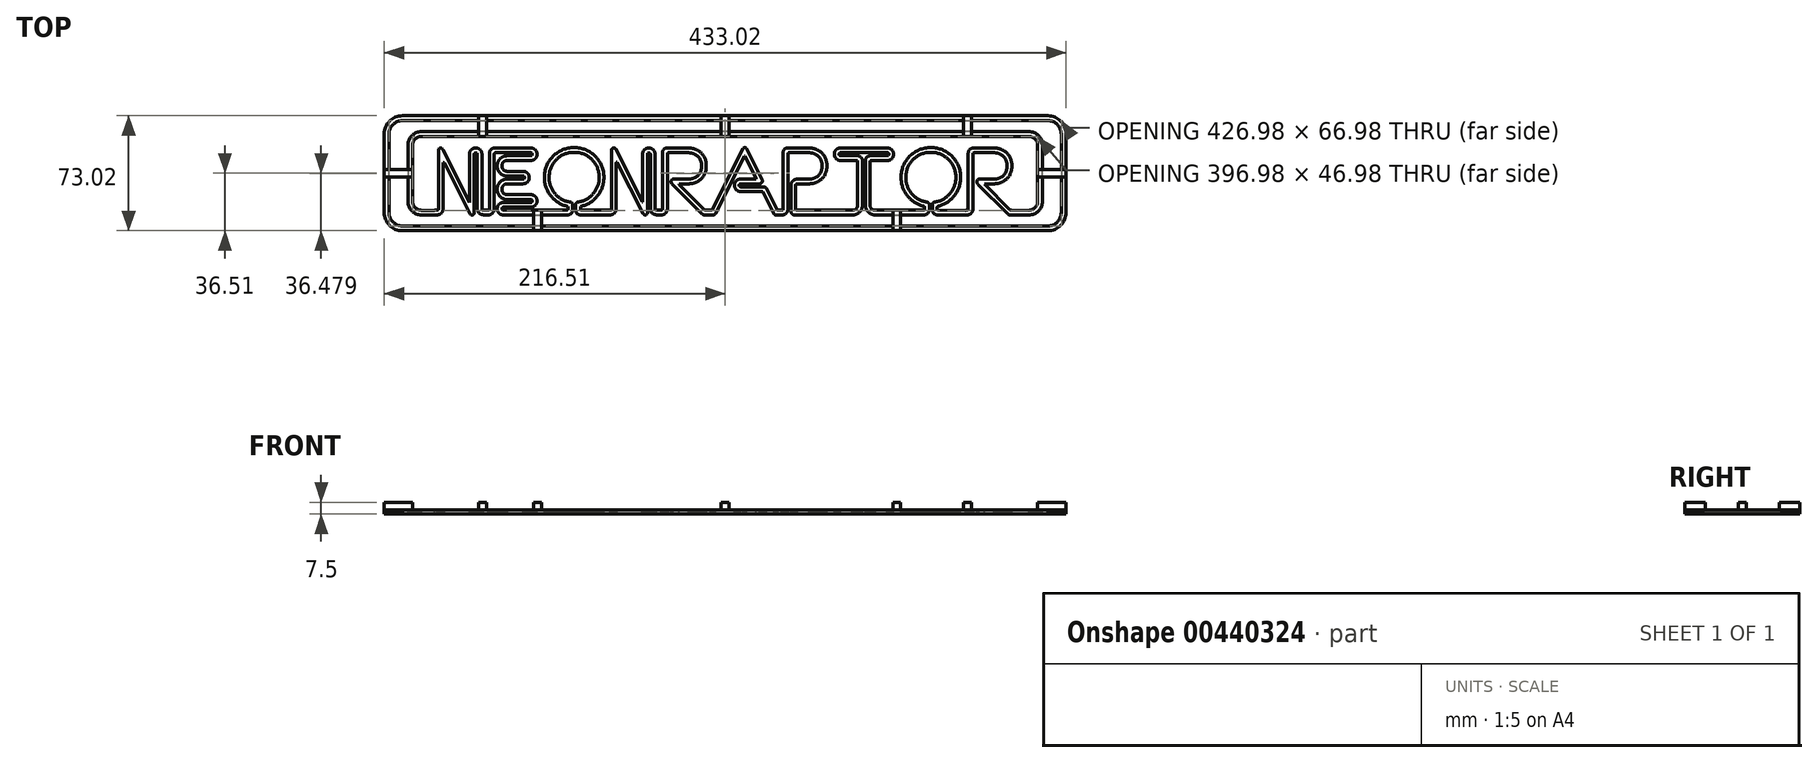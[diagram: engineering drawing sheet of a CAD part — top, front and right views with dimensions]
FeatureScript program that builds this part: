
annotation { "Feature Type Name" : "Feature", "Feature Type Description" : "" }
export const myFeature = defineFeature(function(context is Context, id is Id, definition is map)
    precondition{}
    {
        {
            var Q0;
            Q0=qCreatedBy(makeId("Top.planeOp"),FACE);
            var Q1;
            Q1=qCreatedBy(makeId("Top.planeOp"),FACE);
            var sketch = newSketch(context, id + "F0", { "sketchPlane" : qUnion([Q0, Q1])});
            skLineSegment(sketch, "E0", {"start": v(205, 36.51) * mm, "end": v(-205, 36.51) * mm});
            skLineSegment(sketch, "E1", {"start": v(-205, 36.51) * mm, "end": v(-206.18, 36.45) * mm});
            skLineSegment(sketch, "E2", {"start": v(-206.18, 36.45) * mm, "end": v(-207.32, 36.28) * mm});
            skLineSegment(sketch, "E3", {"start": v(-207.32, 36.28) * mm, "end": v(-208.42, 36) * mm});
            skLineSegment(sketch, "E4", {"start": v(-208.42, 36) * mm, "end": v(-209.48, 35.6) * mm});
            skLineSegment(sketch, "E5", {"start": v(-209.48, 35.6) * mm, "end": v(-210.48, 35.12) * mm});
            skLineSegment(sketch, "E6", {"start": v(-210.48, 35.12) * mm, "end": v(-211.43, 34.54) * mm});
            skLineSegment(sketch, "E7", {"start": v(-211.43, 34.54) * mm, "end": v(-212.32, 33.88) * mm});
            skLineSegment(sketch, "E8", {"start": v(-212.32, 33.88) * mm, "end": v(-213.14, 33.14) * mm});
            skLineSegment(sketch, "E9", {"start": v(-213.14, 33.14) * mm, "end": v(-213.88, 32.32) * mm});
            skLineSegment(sketch, "E10", {"start": v(-213.88, 32.32) * mm, "end": v(-214.54, 31.43) * mm});
            skLineSegment(sketch, "E11", {"start": v(-214.54, 31.43) * mm, "end": v(-215.12, 30.48) * mm});
            skLineSegment(sketch, "E12", {"start": v(-215.12, 30.48) * mm, "end": v(-215.6, 29.48) * mm});
            skLineSegment(sketch, "E13", {"start": v(-215.6, 29.48) * mm, "end": v(-216, 28.42) * mm});
            skLineSegment(sketch, "E14", {"start": v(-216, 28.42) * mm, "end": v(-216.28, 27.32) * mm});
            skLineSegment(sketch, "E15", {"start": v(-216.28, 27.32) * mm, "end": v(-216.45, 26.18) * mm});
            skLineSegment(sketch, "E16", {"start": v(-216.45, 26.18) * mm, "end": v(-216.51, 25) * mm});
            skLineSegment(sketch, "E17", {"start": v(-216.51, 25) * mm, "end": v(-216.51, -25) * mm});
            skLineSegment(sketch, "E18", {"start": v(-216.51, -25) * mm, "end": v(-216.45, -26.18) * mm});
            skLineSegment(sketch, "E19", {"start": v(-216.45, -26.18) * mm, "end": v(-216.28, -27.32) * mm});
            skLineSegment(sketch, "E20", {"start": v(-216.28, -27.32) * mm, "end": v(-216, -28.42) * mm});
            skLineSegment(sketch, "E21", {"start": v(-216, -28.42) * mm, "end": v(-215.6, -29.48) * mm});
            skLineSegment(sketch, "E22", {"start": v(-215.6, -29.48) * mm, "end": v(-215.12, -30.48) * mm});
            skLineSegment(sketch, "E23", {"start": v(-215.12, -30.48) * mm, "end": v(-214.54, -31.43) * mm});
            skLineSegment(sketch, "E24", {"start": v(-214.54, -31.43) * mm, "end": v(-213.88, -32.32) * mm});
            skLineSegment(sketch, "E25", {"start": v(-213.88, -32.32) * mm, "end": v(-213.14, -33.14) * mm});
            skLineSegment(sketch, "E26", {"start": v(-213.14, -33.14) * mm, "end": v(-212.32, -33.88) * mm});
            skLineSegment(sketch, "E27", {"start": v(-212.32, -33.88) * mm, "end": v(-211.43, -34.54) * mm});
            skLineSegment(sketch, "E28", {"start": v(-211.43, -34.54) * mm, "end": v(-210.48, -35.12) * mm});
            skLineSegment(sketch, "E29", {"start": v(-210.48, -35.12) * mm, "end": v(-209.48, -35.6) * mm});
            skLineSegment(sketch, "E30", {"start": v(-209.48, -35.6) * mm, "end": v(-208.42, -36) * mm});
            skLineSegment(sketch, "E31", {"start": v(-208.42, -36) * mm, "end": v(-207.32, -36.28) * mm});
            skLineSegment(sketch, "E32", {"start": v(-207.32, -36.28) * mm, "end": v(-206.18, -36.45) * mm});
            skLineSegment(sketch, "E33", {"start": v(-206.18, -36.45) * mm, "end": v(-205, -36.51) * mm});
            skLineSegment(sketch, "E34", {"start": v(-205, -36.51) * mm, "end": v(205, -36.51) * mm});
            skLineSegment(sketch, "E35", {"start": v(205, -36.51) * mm, "end": v(206.18, -36.45) * mm});
            skLineSegment(sketch, "E36", {"start": v(206.18, -36.45) * mm, "end": v(207.32, -36.28) * mm});
            skLineSegment(sketch, "E37", {"start": v(207.32, -36.28) * mm, "end": v(208.42, -36) * mm});
            skLineSegment(sketch, "E38", {"start": v(208.42, -36) * mm, "end": v(209.48, -35.6) * mm});
            skLineSegment(sketch, "E39", {"start": v(209.48, -35.6) * mm, "end": v(210.48, -35.12) * mm});
            skLineSegment(sketch, "E40", {"start": v(210.48, -35.12) * mm, "end": v(211.43, -34.54) * mm});
            skLineSegment(sketch, "E41", {"start": v(211.43, -34.54) * mm, "end": v(212.32, -33.88) * mm});
            skLineSegment(sketch, "E42", {"start": v(212.32, -33.88) * mm, "end": v(213.14, -33.14) * mm});
            skLineSegment(sketch, "E43", {"start": v(213.14, -33.14) * mm, "end": v(213.88, -32.32) * mm});
            skLineSegment(sketch, "E44", {"start": v(213.88, -32.32) * mm, "end": v(214.54, -31.43) * mm});
            skLineSegment(sketch, "E45", {"start": v(214.54, -31.43) * mm, "end": v(215.12, -30.48) * mm});
            skLineSegment(sketch, "E46", {"start": v(215.12, -30.48) * mm, "end": v(215.6, -29.48) * mm});
            skLineSegment(sketch, "E47", {"start": v(215.6, -29.48) * mm, "end": v(216, -28.42) * mm});
            skLineSegment(sketch, "E48", {"start": v(216, -28.42) * mm, "end": v(216.28, -27.32) * mm});
            skLineSegment(sketch, "E49", {"start": v(216.28, -27.32) * mm, "end": v(216.45, -26.18) * mm});
            skLineSegment(sketch, "E50", {"start": v(216.45, -26.18) * mm, "end": v(216.51, -25) * mm});
            skLineSegment(sketch, "E51", {"start": v(216.51, -25) * mm, "end": v(216.51, 25) * mm});
            skLineSegment(sketch, "E52", {"start": v(216.51, 25) * mm, "end": v(216.45, 26.18) * mm});
            skLineSegment(sketch, "E53", {"start": v(216.45, 26.18) * mm, "end": v(216.28, 27.32) * mm});
            skLineSegment(sketch, "E54", {"start": v(216.28, 27.32) * mm, "end": v(216, 28.42) * mm});
            skLineSegment(sketch, "E55", {"start": v(216, 28.42) * mm, "end": v(215.6, 29.48) * mm});
            skLineSegment(sketch, "E56", {"start": v(215.6, 29.48) * mm, "end": v(215.12, 30.48) * mm});
            skLineSegment(sketch, "E57", {"start": v(215.12, 30.48) * mm, "end": v(214.54, 31.43) * mm});
            skLineSegment(sketch, "E58", {"start": v(214.54, 31.43) * mm, "end": v(213.88, 32.32) * mm});
            skLineSegment(sketch, "E59", {"start": v(213.88, 32.32) * mm, "end": v(213.14, 33.14) * mm});
            skLineSegment(sketch, "E60", {"start": v(213.14, 33.14) * mm, "end": v(212.32, 33.88) * mm});
            skLineSegment(sketch, "E61", {"start": v(212.32, 33.88) * mm, "end": v(211.43, 34.54) * mm});
            skLineSegment(sketch, "E62", {"start": v(211.43, 34.54) * mm, "end": v(210.48, 35.12) * mm});
            skLineSegment(sketch, "E63", {"start": v(210.48, 35.12) * mm, "end": v(209.48, 35.6) * mm});
            skLineSegment(sketch, "E64", {"start": v(209.48, 35.6) * mm, "end": v(208.42, 36) * mm});
            skLineSegment(sketch, "E65", {"start": v(208.42, 36) * mm, "end": v(207.32, 36.28) * mm});
            skLineSegment(sketch, "E66", {"start": v(207.32, 36.28) * mm, "end": v(206.18, 36.45) * mm});
            skLineSegment(sketch, "E67", {"start": v(206.18, 36.45) * mm, "end": v(205, 36.51) * mm});
            skLineSegment(sketch, "E68", {"start": v(213.49, -25) * mm, "end": v(213.45, -25.87) * mm});
            skLineSegment(sketch, "E69", {"start": v(213.45, -25.87) * mm, "end": v(213.32, -26.7) * mm});
            skLineSegment(sketch, "E70", {"start": v(213.32, -26.7) * mm, "end": v(213.1, -27.52) * mm});
            skLineSegment(sketch, "E71", {"start": v(213.1, -27.52) * mm, "end": v(212.82, -28.3) * mm});
            skLineSegment(sketch, "E72", {"start": v(212.82, -28.3) * mm, "end": v(212.46, -29.04) * mm});
            skLineSegment(sketch, "E73", {"start": v(212.46, -29.04) * mm, "end": v(212.04, -29.74) * mm});
            skLineSegment(sketch, "E74", {"start": v(212.04, -29.74) * mm, "end": v(211.55, -30.4) * mm});
            skLineSegment(sketch, "E75", {"start": v(211.55, -30.4) * mm, "end": v(211, -31) * mm});
            skLineSegment(sketch, "E76", {"start": v(211, -31) * mm, "end": v(210.4, -31.55) * mm});
            skLineSegment(sketch, "E77", {"start": v(210.4, -31.55) * mm, "end": v(209.74, -32.04) * mm});
            skLineSegment(sketch, "E78", {"start": v(209.74, -32.04) * mm, "end": v(209.04, -32.46) * mm});
            skLineSegment(sketch, "E79", {"start": v(209.04, -32.46) * mm, "end": v(208.3, -32.82) * mm});
            skLineSegment(sketch, "E80", {"start": v(208.3, -32.82) * mm, "end": v(207.52, -33.1) * mm});
            skLineSegment(sketch, "E81", {"start": v(207.52, -33.1) * mm, "end": v(206.7, -33.32) * mm});
            skLineSegment(sketch, "E82", {"start": v(206.7, -33.32) * mm, "end": v(205.87, -33.45) * mm});
            skLineSegment(sketch, "E83", {"start": v(205.87, -33.45) * mm, "end": v(205, -33.49) * mm});
            skLineSegment(sketch, "E84", {"start": v(205, -33.49) * mm, "end": v(-205, -33.49) * mm});
            skLineSegment(sketch, "E85", {"start": v(-205, -33.49) * mm, "end": v(-205.87, -33.45) * mm});
            skLineSegment(sketch, "E86", {"start": v(-205.87, -33.45) * mm, "end": v(-206.7, -33.32) * mm});
            skLineSegment(sketch, "E87", {"start": v(-206.7, -33.32) * mm, "end": v(-207.52, -33.1) * mm});
            skLineSegment(sketch, "E88", {"start": v(-207.52, -33.1) * mm, "end": v(-208.3, -32.82) * mm});
            skLineSegment(sketch, "E89", {"start": v(-208.3, -32.82) * mm, "end": v(-209.04, -32.46) * mm});
            skLineSegment(sketch, "E90", {"start": v(-209.04, -32.46) * mm, "end": v(-209.74, -32.04) * mm});
            skLineSegment(sketch, "E91", {"start": v(-209.74, -32.04) * mm, "end": v(-210.4, -31.55) * mm});
            skLineSegment(sketch, "E92", {"start": v(-210.4, -31.55) * mm, "end": v(-211, -31) * mm});
            skLineSegment(sketch, "E93", {"start": v(-211, -31) * mm, "end": v(-211.55, -30.4) * mm});
            skLineSegment(sketch, "E94", {"start": v(-211.55, -30.4) * mm, "end": v(-212.04, -29.74) * mm});
            skLineSegment(sketch, "E95", {"start": v(-212.04, -29.74) * mm, "end": v(-212.46, -29.04) * mm});
            skLineSegment(sketch, "E96", {"start": v(-212.46, -29.04) * mm, "end": v(-212.82, -28.3) * mm});
            skLineSegment(sketch, "E97", {"start": v(-212.82, -28.3) * mm, "end": v(-213.1, -27.52) * mm});
            skLineSegment(sketch, "E98", {"start": v(-213.1, -27.52) * mm, "end": v(-213.32, -26.7) * mm});
            skLineSegment(sketch, "E99", {"start": v(-213.32, -26.7) * mm, "end": v(-213.44, -25.87) * mm});
            skLineSegment(sketch, "E100", {"start": v(-213.44, -25.87) * mm, "end": v(-213.49, -25) * mm});
            skLineSegment(sketch, "E101", {"start": v(-213.49, -25) * mm, "end": v(-213.49, 25) * mm});
            skLineSegment(sketch, "E102", {"start": v(-213.49, 25) * mm, "end": v(-213.44, 25.87) * mm});
            skLineSegment(sketch, "E103", {"start": v(-213.44, 25.87) * mm, "end": v(-213.32, 26.7) * mm});
            skLineSegment(sketch, "E104", {"start": v(-213.32, 26.7) * mm, "end": v(-213.1, 27.52) * mm});
            skLineSegment(sketch, "E105", {"start": v(-213.1, 27.52) * mm, "end": v(-212.82, 28.3) * mm});
            skLineSegment(sketch, "E106", {"start": v(-212.82, 28.3) * mm, "end": v(-212.46, 29.04) * mm});
            skLineSegment(sketch, "E107", {"start": v(-212.46, 29.04) * mm, "end": v(-212.04, 29.74) * mm});
            skLineSegment(sketch, "E108", {"start": v(-212.04, 29.74) * mm, "end": v(-211.55, 30.4) * mm});
            skLineSegment(sketch, "E109", {"start": v(-211.55, 30.4) * mm, "end": v(-211, 31) * mm});
            skLineSegment(sketch, "E110", {"start": v(-211, 31) * mm, "end": v(-210.4, 31.55) * mm});
            skLineSegment(sketch, "E111", {"start": v(-210.4, 31.55) * mm, "end": v(-209.74, 32.04) * mm});
            skLineSegment(sketch, "E112", {"start": v(-209.74, 32.04) * mm, "end": v(-209.04, 32.46) * mm});
            skLineSegment(sketch, "E113", {"start": v(-209.04, 32.46) * mm, "end": v(-208.3, 32.82) * mm});
            skLineSegment(sketch, "E114", {"start": v(-208.3, 32.82) * mm, "end": v(-207.52, 33.1) * mm});
            skLineSegment(sketch, "E115", {"start": v(-207.52, 33.1) * mm, "end": v(-206.7, 33.32) * mm});
            skLineSegment(sketch, "E116", {"start": v(-206.7, 33.32) * mm, "end": v(-205.87, 33.44) * mm});
            skLineSegment(sketch, "E117", {"start": v(-205.87, 33.44) * mm, "end": v(-205, 33.49) * mm});
            skLineSegment(sketch, "E118", {"start": v(-205, 33.49) * mm, "end": v(205, 33.49) * mm});
            skLineSegment(sketch, "E119", {"start": v(205, 33.49) * mm, "end": v(205.87, 33.44) * mm});
            skLineSegment(sketch, "E120", {"start": v(205.87, 33.44) * mm, "end": v(206.7, 33.32) * mm});
            skLineSegment(sketch, "E121", {"start": v(206.7, 33.32) * mm, "end": v(207.52, 33.1) * mm});
            skLineSegment(sketch, "E122", {"start": v(207.52, 33.1) * mm, "end": v(208.3, 32.82) * mm});
            skLineSegment(sketch, "E123", {"start": v(208.3, 32.82) * mm, "end": v(209.04, 32.46) * mm});
            skLineSegment(sketch, "E124", {"start": v(209.04, 32.46) * mm, "end": v(209.74, 32.04) * mm});
            skLineSegment(sketch, "E125", {"start": v(209.74, 32.04) * mm, "end": v(210.4, 31.55) * mm});
            skLineSegment(sketch, "E126", {"start": v(210.4, 31.55) * mm, "end": v(211, 31) * mm});
            skLineSegment(sketch, "E127", {"start": v(211, 31) * mm, "end": v(211.55, 30.4) * mm});
            skLineSegment(sketch, "E128", {"start": v(211.55, 30.4) * mm, "end": v(212.04, 29.74) * mm});
            skLineSegment(sketch, "E129", {"start": v(212.04, 29.74) * mm, "end": v(212.46, 29.04) * mm});
            skLineSegment(sketch, "E130", {"start": v(212.46, 29.04) * mm, "end": v(212.82, 28.3) * mm});
            skLineSegment(sketch, "E131", {"start": v(212.82, 28.3) * mm, "end": v(213.1, 27.52) * mm});
            skLineSegment(sketch, "E132", {"start": v(213.1, 27.52) * mm, "end": v(213.32, 26.7) * mm});
            skLineSegment(sketch, "E133", {"start": v(213.32, 26.7) * mm, "end": v(213.45, 25.87) * mm});
            skLineSegment(sketch, "E134", {"start": v(213.45, 25.87) * mm, "end": v(213.49, 25) * mm});
            skLineSegment(sketch, "E135", {"start": v(213.49, 25) * mm, "end": v(213.49, -25) * mm});
            skLineSegment(sketch, "E136", {"start": v(192.86, 26.48) * mm, "end": v(-192.86, 26.48) * mm});
            skLineSegment(sketch, "E137", {"start": v(-192.86, 26.48) * mm, "end": v(-193.74, 26.44) * mm});
            skLineSegment(sketch, "E138", {"start": v(-193.74, 26.44) * mm, "end": v(-194.6, 26.3) * mm});
            skLineSegment(sketch, "E139", {"start": v(-194.6, 26.3) * mm, "end": v(-195.43, 26.1) * mm});
            skLineSegment(sketch, "E140", {"start": v(-195.43, 26.1) * mm, "end": v(-196.22, 25.8) * mm});
            skLineSegment(sketch, "E141", {"start": v(-196.22, 25.8) * mm, "end": v(-196.98, 25.43) * mm});
            skLineSegment(sketch, "E142", {"start": v(-196.98, 25.43) * mm, "end": v(-197.7, 25) * mm});
            skLineSegment(sketch, "E143", {"start": v(-197.7, 25) * mm, "end": v(-198.36, 24.5) * mm});
            skLineSegment(sketch, "E144", {"start": v(-198.36, 24.5) * mm, "end": v(-198.97, 23.94) * mm});
            skLineSegment(sketch, "E145", {"start": v(-198.97, 23.94) * mm, "end": v(-199.53, 23.33) * mm});
            skLineSegment(sketch, "E146", {"start": v(-199.53, 23.33) * mm, "end": v(-200.03, 22.66) * mm});
            skLineSegment(sketch, "E147", {"start": v(-200.03, 22.66) * mm, "end": v(-200.46, 21.95) * mm});
            skLineSegment(sketch, "E148", {"start": v(-200.46, 21.95) * mm, "end": v(-200.83, 21.2) * mm});
            skLineSegment(sketch, "E149", {"start": v(-200.83, 21.2) * mm, "end": v(-201.12, 20.4) * mm});
            skLineSegment(sketch, "E150", {"start": v(-201.12, 20.4) * mm, "end": v(-201.33, 19.57) * mm});
            skLineSegment(sketch, "E151", {"start": v(-201.33, 19.57) * mm, "end": v(-201.47, 18.7) * mm});
            skLineSegment(sketch, "E152", {"start": v(-201.47, 18.7) * mm, "end": v(-201.51, 17.82) * mm});
            skLineSegment(sketch, "E153", {"start": v(-201.51, 17.82) * mm, "end": v(-201.51, -17.89) * mm});
            skLineSegment(sketch, "E154", {"start": v(-201.51, -17.89) * mm, "end": v(-201.47, -18.77) * mm});
            skLineSegment(sketch, "E155", {"start": v(-201.47, -18.77) * mm, "end": v(-201.33, -19.63) * mm});
            skLineSegment(sketch, "E156", {"start": v(-201.33, -19.63) * mm, "end": v(-201.12, -20.46) * mm});
            skLineSegment(sketch, "E157", {"start": v(-201.12, -20.46) * mm, "end": v(-200.83, -21.25) * mm});
            skLineSegment(sketch, "E158", {"start": v(-200.83, -21.25) * mm, "end": v(-200.46, -22) * mm});
            skLineSegment(sketch, "E159", {"start": v(-200.46, -22) * mm, "end": v(-200.03, -22.72) * mm});
            skLineSegment(sketch, "E160", {"start": v(-200.03, -22.72) * mm, "end": v(-199.53, -23.39) * mm});
            skLineSegment(sketch, "E161", {"start": v(-199.53, -23.39) * mm, "end": v(-198.97, -24) * mm});
            skLineSegment(sketch, "E162", {"start": v(-198.97, -24) * mm, "end": v(-198.36, -24.56) * mm});
            skLineSegment(sketch, "E163", {"start": v(-198.36, -24.56) * mm, "end": v(-197.7, -25.06) * mm});
            skLineSegment(sketch, "E164", {"start": v(-197.7, -25.06) * mm, "end": v(-196.98, -25.5) * mm});
            skLineSegment(sketch, "E165", {"start": v(-196.98, -25.5) * mm, "end": v(-196.22, -25.86) * mm});
            skLineSegment(sketch, "E166", {"start": v(-196.22, -25.86) * mm, "end": v(-195.43, -26.15) * mm});
            skLineSegment(sketch, "E167", {"start": v(-195.43, -26.15) * mm, "end": v(-194.6, -26.37) * mm});
            skLineSegment(sketch, "E168", {"start": v(-194.6, -26.37) * mm, "end": v(-193.74, -26.5) * mm});
            skLineSegment(sketch, "E169", {"start": v(-193.74, -26.5) * mm, "end": v(-192.86, -26.54) * mm});
            skLineSegment(sketch, "E170", {"start": v(-192.86, -26.54) * mm, "end": v(-184.5, -26.54) * mm});
            skLineSegment(sketch, "E171", {"start": v(-184.5, -26.54) * mm, "end": v(-184.4, -26.44) * mm});
            skLineSegment(sketch, "E172", {"start": v(-184.4, -26.44) * mm, "end": v(-184.4, -26.44) * mm});
            skLineSegment(sketch, "E173", {"start": v(-184.4, -26.44) * mm, "end": v(-183.06, -26.44) * mm});
            skLineSegment(sketch, "E174", {"start": v(-183.06, -26.44) * mm, "end": v(-182.85, -26.43) * mm});
            skLineSegment(sketch, "E175", {"start": v(-182.85, -26.43) * mm, "end": v(-182.64, -26.42) * mm});
            skLineSegment(sketch, "E176", {"start": v(-182.64, -26.42) * mm, "end": v(-182.44, -26.4) * mm});
            skLineSegment(sketch, "E177", {"start": v(-182.44, -26.4) * mm, "end": v(-182.24, -26.37) * mm});
            skLineSegment(sketch, "E178", {"start": v(-182.24, -26.37) * mm, "end": v(-182.04, -26.33) * mm});
            skLineSegment(sketch, "E179", {"start": v(-182.04, -26.33) * mm, "end": v(-181.85, -26.28) * mm});
            skLineSegment(sketch, "E180", {"start": v(-181.85, -26.28) * mm, "end": v(-181.67, -26.22) * mm});
            skLineSegment(sketch, "E181", {"start": v(-181.67, -26.22) * mm, "end": v(-181.5, -26.16) * mm});
            skLineSegment(sketch, "E182", {"start": v(-181.5, -26.16) * mm, "end": v(-181.32, -26.08) * mm});
            skLineSegment(sketch, "E183", {"start": v(-181.32, -26.08) * mm, "end": v(-181.15, -26) * mm});
            skLineSegment(sketch, "E184", {"start": v(-181.15, -26) * mm, "end": v(-180.98, -25.9) * mm});
            skLineSegment(sketch, "E185", {"start": v(-180.98, -25.9) * mm, "end": v(-180.82, -25.8) * mm});
            skLineSegment(sketch, "E186", {"start": v(-180.82, -25.8) * mm, "end": v(-180.67, -25.7) * mm});
            skLineSegment(sketch, "E187", {"start": v(-180.67, -25.7) * mm, "end": v(-180.52, -25.58) * mm});
            skLineSegment(sketch, "E188", {"start": v(-180.52, -25.58) * mm, "end": v(-180.38, -25.46) * mm});
            skLineSegment(sketch, "E189", {"start": v(-180.38, -25.46) * mm, "end": v(-180.24, -25.32) * mm});
            skLineSegment(sketch, "E190", {"start": v(-180.24, -25.32) * mm, "end": v(-180.1, -25.18) * mm});
            skLineSegment(sketch, "E191", {"start": v(-180.1, -25.18) * mm, "end": v(-179.99, -25.03) * mm});
            skLineSegment(sketch, "E192", {"start": v(-179.99, -25.03) * mm, "end": v(-179.87, -24.88) * mm});
            skLineSegment(sketch, "E193", {"start": v(-179.87, -24.88) * mm, "end": v(-179.77, -24.73) * mm});
            skLineSegment(sketch, "E194", {"start": v(-179.77, -24.73) * mm, "end": v(-179.67, -24.56) * mm});
            skLineSegment(sketch, "E195", {"start": v(-179.67, -24.56) * mm, "end": v(-179.58, -24.4) * mm});
            skLineSegment(sketch, "E196", {"start": v(-179.58, -24.4) * mm, "end": v(-179.5, -24.23) * mm});
            skLineSegment(sketch, "E197", {"start": v(-179.5, -24.23) * mm, "end": v(-179.43, -24.05) * mm});
            skLineSegment(sketch, "E198", {"start": v(-179.43, -24.05) * mm, "end": v(-179.36, -23.87) * mm});
            skLineSegment(sketch, "E199", {"start": v(-179.36, -23.87) * mm, "end": v(-179.3, -23.68) * mm});
            skLineSegment(sketch, "E200", {"start": v(-179.3, -23.68) * mm, "end": v(-179.26, -23.5) * mm});
            skLineSegment(sketch, "E201", {"start": v(-179.26, -23.5) * mm, "end": v(-179.22, -23.3) * mm});
            skLineSegment(sketch, "E202", {"start": v(-179.22, -23.3) * mm, "end": v(-179.2, -23.1) * mm});
            skLineSegment(sketch, "E203", {"start": v(-179.2, -23.1) * mm, "end": v(-179.17, -22.9) * mm});
            skLineSegment(sketch, "E204", {"start": v(-179.17, -22.9) * mm, "end": v(-179.16, -22.69) * mm});
            skLineSegment(sketch, "E205", {"start": v(-179.16, -22.69) * mm, "end": v(-179.15, -22.47) * mm});
            skLineSegment(sketch, "E206", {"start": v(-179.15, -22.47) * mm, "end": v(-179.15, 6.31) * mm});
            skLineSegment(sketch, "E207", {"start": v(-179.15, 6.31) * mm, "end": v(-179.15, 6.36) * mm});
            skLineSegment(sketch, "E208", {"start": v(-179.15, 6.36) * mm, "end": v(-179.14, 6.41) * mm});
            skLineSegment(sketch, "E209", {"start": v(-179.14, 6.41) * mm, "end": v(-179.13, 6.46) * mm});
            skLineSegment(sketch, "E210", {"start": v(-179.13, 6.46) * mm, "end": v(-179.11, 6.5) * mm});
            skLineSegment(sketch, "E211", {"start": v(-179.11, 6.5) * mm, "end": v(-179.1, 6.54) * mm});
            skLineSegment(sketch, "E212", {"start": v(-179.1, 6.54) * mm, "end": v(-179.07, 6.58) * mm});
            skLineSegment(sketch, "E213", {"start": v(-179.07, 6.58) * mm, "end": v(-179.04, 6.6) * mm});
            skLineSegment(sketch, "E214", {"start": v(-179.04, 6.6) * mm, "end": v(-179.01, 6.64) * mm});
            skLineSegment(sketch, "E215", {"start": v(-179.01, 6.64) * mm, "end": v(-178.98, 6.67) * mm});
            skLineSegment(sketch, "E216", {"start": v(-178.98, 6.67) * mm, "end": v(-178.94, 6.69) * mm});
            skLineSegment(sketch, "E217", {"start": v(-178.94, 6.69) * mm, "end": v(-178.9, 6.7) * mm});
            skLineSegment(sketch, "E218", {"start": v(-178.9, 6.7) * mm, "end": v(-178.87, 6.72) * mm});
            skLineSegment(sketch, "E219", {"start": v(-178.87, 6.72) * mm, "end": v(-178.83, 6.74) * mm});
            skLineSegment(sketch, "E220", {"start": v(-178.83, 6.74) * mm, "end": v(-178.79, 6.75) * mm});
            skLineSegment(sketch, "E221", {"start": v(-178.79, 6.75) * mm, "end": v(-178.75, 6.75) * mm});
            skLineSegment(sketch, "E222", {"start": v(-178.75, 6.75) * mm, "end": v(-178.7, 6.75) * mm});
            skLineSegment(sketch, "E223", {"start": v(-178.7, 6.75) * mm, "end": v(-178.67, 6.75) * mm});
            skLineSegment(sketch, "E224", {"start": v(-178.67, 6.75) * mm, "end": v(-178.64, 6.75) * mm});
            skLineSegment(sketch, "E225", {"start": v(-178.64, 6.75) * mm, "end": v(-178.61, 6.74) * mm});
            skLineSegment(sketch, "E226", {"start": v(-178.61, 6.74) * mm, "end": v(-178.58, 6.74) * mm});
            skLineSegment(sketch, "E227", {"start": v(-178.58, 6.74) * mm, "end": v(-178.56, 6.73) * mm});
            skLineSegment(sketch, "E228", {"start": v(-178.56, 6.73) * mm, "end": v(-178.53, 6.72) * mm});
            skLineSegment(sketch, "E229", {"start": v(-178.53, 6.72) * mm, "end": v(-178.5, 6.7) * mm});
            skLineSegment(sketch, "E230", {"start": v(-178.5, 6.7) * mm, "end": v(-178.48, 6.69) * mm});
            skLineSegment(sketch, "E231", {"start": v(-178.48, 6.69) * mm, "end": v(-178.45, 6.67) * mm});
            skLineSegment(sketch, "E232", {"start": v(-178.45, 6.67) * mm, "end": v(-178.43, 6.65) * mm});
            skLineSegment(sketch, "E233", {"start": v(-178.43, 6.65) * mm, "end": v(-178.4, 6.63) * mm});
            skLineSegment(sketch, "E234", {"start": v(-178.4, 6.63) * mm, "end": v(-178.39, 6.61) * mm});
            skLineSegment(sketch, "E235", {"start": v(-178.39, 6.61) * mm, "end": v(-178.37, 6.59) * mm});
            skLineSegment(sketch, "E236", {"start": v(-178.37, 6.59) * mm, "end": v(-178.35, 6.56) * mm});
            skLineSegment(sketch, "E237", {"start": v(-178.35, 6.56) * mm, "end": v(-178.33, 6.54) * mm});
            skLineSegment(sketch, "E238", {"start": v(-178.33, 6.54) * mm, "end": v(-178.32, 6.5) * mm});
            skLineSegment(sketch, "E239", {"start": v(-178.32, 6.5) * mm, "end": v(-162.07, -25.76) * mm});
            skLineSegment(sketch, "E240", {"start": v(-162.07, -25.76) * mm, "end": v(-162.03, -25.83) * mm});
            skLineSegment(sketch, "E241", {"start": v(-162.03, -25.83) * mm, "end": v(-161.98, -25.9) * mm});
            skLineSegment(sketch, "E242", {"start": v(-161.98, -25.9) * mm, "end": v(-161.92, -25.98) * mm});
            skLineSegment(sketch, "E243", {"start": v(-161.92, -25.98) * mm, "end": v(-161.86, -26.04) * mm});
            skLineSegment(sketch, "E244", {"start": v(-161.86, -26.04) * mm, "end": v(-161.8, -26.1) * mm});
            skLineSegment(sketch, "E245", {"start": v(-161.8, -26.1) * mm, "end": v(-161.72, -26.17) * mm});
            skLineSegment(sketch, "E246", {"start": v(-161.72, -26.17) * mm, "end": v(-161.65, -26.22) * mm});
            skLineSegment(sketch, "E247", {"start": v(-161.65, -26.22) * mm, "end": v(-161.57, -26.27) * mm});
            skLineSegment(sketch, "E248", {"start": v(-161.57, -26.27) * mm, "end": v(-161.49, -26.32) * mm});
            skLineSegment(sketch, "E249", {"start": v(-161.49, -26.32) * mm, "end": v(-161.4, -26.36) * mm});
            skLineSegment(sketch, "E250", {"start": v(-161.4, -26.36) * mm, "end": v(-161.32, -26.4) * mm});
            skLineSegment(sketch, "E251", {"start": v(-161.32, -26.4) * mm, "end": v(-161.23, -26.43) * mm});
            skLineSegment(sketch, "E252", {"start": v(-161.23, -26.43) * mm, "end": v(-161.14, -26.46) * mm});
            skLineSegment(sketch, "E253", {"start": v(-161.14, -26.46) * mm, "end": v(-161.05, -26.47) * mm});
            skLineSegment(sketch, "E254", {"start": v(-161.05, -26.47) * mm, "end": v(-160.97, -26.48) * mm});
            skLineSegment(sketch, "E255", {"start": v(-160.97, -26.48) * mm, "end": v(-160.88, -26.49) * mm});
            skLineSegment(sketch, "E256", {"start": v(-160.88, -26.49) * mm, "end": v(-160.61, -26.49) * mm});
            skLineSegment(sketch, "E257", {"start": v(-160.61, -26.49) * mm, "end": v(-160.49, -26.48) * mm});
            skLineSegment(sketch, "E258", {"start": v(-160.49, -26.48) * mm, "end": v(-160.36, -26.46) * mm});
            skLineSegment(sketch, "E259", {"start": v(-160.36, -26.46) * mm, "end": v(-160.24, -26.43) * mm});
            skLineSegment(sketch, "E260", {"start": v(-160.24, -26.43) * mm, "end": v(-160.13, -26.4) * mm});
            skLineSegment(sketch, "E261", {"start": v(-160.13, -26.4) * mm, "end": v(-160.02, -26.34) * mm});
            skLineSegment(sketch, "E262", {"start": v(-160.02, -26.34) * mm, "end": v(-159.91, -26.27) * mm});
            skLineSegment(sketch, "E263", {"start": v(-159.91, -26.27) * mm, "end": v(-159.82, -26.2) * mm});
            skLineSegment(sketch, "E264", {"start": v(-159.82, -26.2) * mm, "end": v(-159.73, -26.12) * mm});
            skLineSegment(sketch, "E265", {"start": v(-159.73, -26.12) * mm, "end": v(-159.65, -26.03) * mm});
            skLineSegment(sketch, "E266", {"start": v(-159.65, -26.03) * mm, "end": v(-159.58, -25.94) * mm});
            skLineSegment(sketch, "E267", {"start": v(-159.58, -25.94) * mm, "end": v(-159.51, -25.83) * mm});
            skLineSegment(sketch, "E268", {"start": v(-159.51, -25.83) * mm, "end": v(-159.46, -25.72) * mm});
            skLineSegment(sketch, "E269", {"start": v(-159.46, -25.72) * mm, "end": v(-159.42, -25.61) * mm});
            skLineSegment(sketch, "E270", {"start": v(-159.42, -25.61) * mm, "end": v(-159.39, -25.5) * mm});
            skLineSegment(sketch, "E271", {"start": v(-159.39, -25.5) * mm, "end": v(-159.37, -25.37) * mm});
            skLineSegment(sketch, "E272", {"start": v(-159.37, -25.37) * mm, "end": v(-159.36, -25.24) * mm});
            skLineSegment(sketch, "E273", {"start": v(-159.36, -25.24) * mm, "end": v(-159.36, 11.98) * mm});
            skLineSegment(sketch, "E274", {"start": v(-159.36, 11.98) * mm, "end": v(-159.36, 12.1) * mm});
            skLineSegment(sketch, "E275", {"start": v(-159.36, 12.1) * mm, "end": v(-159.35, 12.22) * mm});
            skLineSegment(sketch, "E276", {"start": v(-159.35, 12.22) * mm, "end": v(-159.33, 12.33) * mm});
            skLineSegment(sketch, "E277", {"start": v(-159.33, 12.33) * mm, "end": v(-159.3, 12.43) * mm});
            skLineSegment(sketch, "E278", {"start": v(-159.3, 12.43) * mm, "end": v(-159.27, 12.52) * mm});
            skLineSegment(sketch, "E279", {"start": v(-159.27, 12.52) * mm, "end": v(-159.24, 12.6) * mm});
            skLineSegment(sketch, "E280", {"start": v(-159.24, 12.6) * mm, "end": v(-159.19, 12.67) * mm});
            skLineSegment(sketch, "E281", {"start": v(-159.19, 12.67) * mm, "end": v(-159.14, 12.74) * mm});
            skLineSegment(sketch, "E282", {"start": v(-159.14, 12.74) * mm, "end": v(-159.07, 12.8) * mm});
            skLineSegment(sketch, "E283", {"start": v(-159.07, 12.8) * mm, "end": v(-159, 12.85) * mm});
            skLineSegment(sketch, "E284", {"start": v(-159, 12.85) * mm, "end": v(-158.93, 12.9) * mm});
            skLineSegment(sketch, "E285", {"start": v(-158.93, 12.9) * mm, "end": v(-158.84, 12.93) * mm});
            skLineSegment(sketch, "E286", {"start": v(-158.84, 12.93) * mm, "end": v(-158.75, 12.95) * mm});
            skLineSegment(sketch, "E287", {"start": v(-158.75, 12.95) * mm, "end": v(-158.65, 12.97) * mm});
            skLineSegment(sketch, "E288", {"start": v(-158.65, 12.97) * mm, "end": v(-158.55, 12.98) * mm});
            skLineSegment(sketch, "E289", {"start": v(-158.55, 12.98) * mm, "end": v(-158.43, 12.99) * mm});
            skLineSegment(sketch, "E290", {"start": v(-158.43, 12.99) * mm, "end": v(-158.3, 12.98) * mm});
            skLineSegment(sketch, "E291", {"start": v(-158.3, 12.98) * mm, "end": v(-158.2, 12.97) * mm});
            skLineSegment(sketch, "E292", {"start": v(-158.2, 12.97) * mm, "end": v(-158.09, 12.95) * mm});
            skLineSegment(sketch, "E293", {"start": v(-158.09, 12.95) * mm, "end": v(-158, 12.93) * mm});
            skLineSegment(sketch, "E294", {"start": v(-158, 12.93) * mm, "end": v(-157.9, 12.9) * mm});
            skLineSegment(sketch, "E295", {"start": v(-157.9, 12.9) * mm, "end": v(-157.82, 12.85) * mm});
            skLineSegment(sketch, "E296", {"start": v(-157.82, 12.85) * mm, "end": v(-157.75, 12.8) * mm});
            skLineSegment(sketch, "E297", {"start": v(-157.75, 12.8) * mm, "end": v(-157.69, 12.74) * mm});
            skLineSegment(sketch, "E298", {"start": v(-157.69, 12.74) * mm, "end": v(-157.63, 12.67) * mm});
            skLineSegment(sketch, "E299", {"start": v(-157.63, 12.67) * mm, "end": v(-157.58, 12.6) * mm});
            skLineSegment(sketch, "E300", {"start": v(-157.58, 12.6) * mm, "end": v(-157.54, 12.52) * mm});
            skLineSegment(sketch, "E301", {"start": v(-157.54, 12.52) * mm, "end": v(-157.5, 12.43) * mm});
            skLineSegment(sketch, "E302", {"start": v(-157.5, 12.43) * mm, "end": v(-157.48, 12.33) * mm});
            skLineSegment(sketch, "E303", {"start": v(-157.48, 12.33) * mm, "end": v(-157.46, 12.22) * mm});
            skLineSegment(sketch, "E304", {"start": v(-157.46, 12.22) * mm, "end": v(-157.45, 12.1) * mm});
            skLineSegment(sketch, "E305", {"start": v(-157.45, 12.1) * mm, "end": v(-157.45, 11.98) * mm});
            skLineSegment(sketch, "E306", {"start": v(-157.45, 11.98) * mm, "end": v(-157.45, -22.43) * mm});
            skLineSegment(sketch, "E307", {"start": v(-157.45, -22.43) * mm, "end": v(-157.43, -22.85) * mm});
            skLineSegment(sketch, "E308", {"start": v(-157.43, -22.85) * mm, "end": v(-157.38, -23.26) * mm});
            skLineSegment(sketch, "E309", {"start": v(-157.38, -23.26) * mm, "end": v(-157.3, -23.63) * mm});
            skLineSegment(sketch, "E310", {"start": v(-157.3, -23.63) * mm, "end": v(-157.2, -24) * mm});
            skLineSegment(sketch, "E311", {"start": v(-157.2, -24) * mm, "end": v(-157.06, -24.32) * mm});
            skLineSegment(sketch, "E312", {"start": v(-157.06, -24.32) * mm, "end": v(-156.9, -24.63) * mm});
            skLineSegment(sketch, "E313", {"start": v(-156.9, -24.63) * mm, "end": v(-156.7, -24.91) * mm});
            skLineSegment(sketch, "E314", {"start": v(-156.7, -24.91) * mm, "end": v(-156.46, -25.17) * mm});
            skLineSegment(sketch, "E315", {"start": v(-156.46, -25.17) * mm, "end": v(-156.2, -25.4) * mm});
            skLineSegment(sketch, "E316", {"start": v(-156.2, -25.4) * mm, "end": v(-155.91, -25.62) * mm});
            skLineSegment(sketch, "E317", {"start": v(-155.91, -25.62) * mm, "end": v(-155.6, -25.8) * mm});
            skLineSegment(sketch, "E318", {"start": v(-155.6, -25.8) * mm, "end": v(-155.24, -25.97) * mm});
            skLineSegment(sketch, "E319", {"start": v(-155.24, -25.97) * mm, "end": v(-154.86, -26.11) * mm});
            skLineSegment(sketch, "E320", {"start": v(-154.86, -26.11) * mm, "end": v(-154.45, -26.23) * mm});
            skLineSegment(sketch, "E321", {"start": v(-154.45, -26.23) * mm, "end": v(-154, -26.32) * mm});
            skLineSegment(sketch, "E322", {"start": v(-154, -26.32) * mm, "end": v(-153.53, -26.38) * mm});
            skLineSegment(sketch, "E323", {"start": v(-153.53, -26.38) * mm, "end": v(-150.63, -26.49) * mm});
            skLineSegment(sketch, "E324", {"start": v(-150.63, -26.49) * mm, "end": v(-150.41, -26.48) * mm});
            skLineSegment(sketch, "E325", {"start": v(-150.41, -26.48) * mm, "end": v(-150.2, -26.47) * mm});
            skLineSegment(sketch, "E326", {"start": v(-150.2, -26.47) * mm, "end": v(-150, -26.45) * mm});
            skLineSegment(sketch, "E327", {"start": v(-150, -26.45) * mm, "end": v(-149.8, -26.42) * mm});
            skLineSegment(sketch, "E328", {"start": v(-149.8, -26.42) * mm, "end": v(-149.6, -26.38) * mm});
            skLineSegment(sketch, "E329", {"start": v(-149.6, -26.38) * mm, "end": v(-149.41, -26.33) * mm});
            skLineSegment(sketch, "E330", {"start": v(-149.41, -26.33) * mm, "end": v(-149.23, -26.27) * mm});
            skLineSegment(sketch, "E331", {"start": v(-149.23, -26.27) * mm, "end": v(-149.05, -26.2) * mm});
            skLineSegment(sketch, "E332", {"start": v(-149.05, -26.2) * mm, "end": v(-148.87, -26.13) * mm});
            skLineSegment(sketch, "E333", {"start": v(-148.87, -26.13) * mm, "end": v(-148.7, -26.05) * mm});
            skLineSegment(sketch, "E334", {"start": v(-148.7, -26.05) * mm, "end": v(-148.53, -25.96) * mm});
            skLineSegment(sketch, "E335", {"start": v(-148.53, -25.96) * mm, "end": v(-148.37, -25.86) * mm});
            skLineSegment(sketch, "E336", {"start": v(-148.37, -25.86) * mm, "end": v(-148.22, -25.75) * mm});
            skLineSegment(sketch, "E337", {"start": v(-148.22, -25.75) * mm, "end": v(-148.06, -25.63) * mm});
            skLineSegment(sketch, "E338", {"start": v(-148.06, -25.63) * mm, "end": v(-147.92, -25.5) * mm});
            skLineSegment(sketch, "E339", {"start": v(-147.92, -25.5) * mm, "end": v(-147.78, -25.37) * mm});
            skLineSegment(sketch, "E340", {"start": v(-147.78, -25.37) * mm, "end": v(-147.64, -25.23) * mm});
            skLineSegment(sketch, "E341", {"start": v(-147.64, -25.23) * mm, "end": v(-147.52, -25.09) * mm});
            skLineSegment(sketch, "E342", {"start": v(-147.52, -25.09) * mm, "end": v(-147.4, -24.94) * mm});
            skLineSegment(sketch, "E343", {"start": v(-147.4, -24.94) * mm, "end": v(-147.3, -24.78) * mm});
            skLineSegment(sketch, "E344", {"start": v(-147.3, -24.78) * mm, "end": v(-147.2, -24.62) * mm});
            skLineSegment(sketch, "E345", {"start": v(-147.2, -24.62) * mm, "end": v(-147.1, -24.45) * mm});
            skLineSegment(sketch, "E346", {"start": v(-147.1, -24.45) * mm, "end": v(-147.02, -24.28) * mm});
            skLineSegment(sketch, "E347", {"start": v(-147.02, -24.28) * mm, "end": v(-146.94, -24.1) * mm});
            skLineSegment(sketch, "E348", {"start": v(-146.94, -24.1) * mm, "end": v(-146.88, -23.92) * mm});
            skLineSegment(sketch, "E349", {"start": v(-146.88, -23.92) * mm, "end": v(-146.82, -23.74) * mm});
            skLineSegment(sketch, "E350", {"start": v(-146.82, -23.74) * mm, "end": v(-146.77, -23.55) * mm});
            skLineSegment(sketch, "E351", {"start": v(-146.77, -23.55) * mm, "end": v(-146.73, -23.35) * mm});
            skLineSegment(sketch, "E352", {"start": v(-146.73, -23.35) * mm, "end": v(-146.7, -23.15) * mm});
            skLineSegment(sketch, "E353", {"start": v(-146.7, -23.15) * mm, "end": v(-146.68, -22.95) * mm});
            skLineSegment(sketch, "E354", {"start": v(-146.68, -22.95) * mm, "end": v(-146.67, -22.74) * mm});
            skLineSegment(sketch, "E355", {"start": v(-146.67, -22.74) * mm, "end": v(-146.66, -22.53) * mm});
            skLineSegment(sketch, "E356", {"start": v(-146.66, -22.53) * mm, "end": v(-146.66, 12.15) * mm});
            skLineSegment(sketch, "E357", {"start": v(-146.66, 12.15) * mm, "end": v(-146.66, 12.24) * mm});
            skLineSegment(sketch, "E358", {"start": v(-146.66, 12.24) * mm, "end": v(-146.65, 12.33) * mm});
            skLineSegment(sketch, "E359", {"start": v(-146.65, 12.33) * mm, "end": v(-146.62, 12.42) * mm});
            skLineSegment(sketch, "E360", {"start": v(-146.62, 12.42) * mm, "end": v(-146.6, 12.5) * mm});
            skLineSegment(sketch, "E361", {"start": v(-146.6, 12.5) * mm, "end": v(-146.56, 12.58) * mm});
            skLineSegment(sketch, "E362", {"start": v(-146.56, 12.58) * mm, "end": v(-146.51, 12.65) * mm});
            skLineSegment(sketch, "E363", {"start": v(-146.51, 12.65) * mm, "end": v(-146.46, 12.72) * mm});
            skLineSegment(sketch, "E364", {"start": v(-146.46, 12.72) * mm, "end": v(-146.4, 12.78) * mm});
            skLineSegment(sketch, "E365", {"start": v(-146.4, 12.78) * mm, "end": v(-146.34, 12.84) * mm});
            skLineSegment(sketch, "E366", {"start": v(-146.34, 12.84) * mm, "end": v(-146.27, 12.89) * mm});
            skLineSegment(sketch, "E367", {"start": v(-146.27, 12.89) * mm, "end": v(-146.2, 12.93) * mm});
            skLineSegment(sketch, "E368", {"start": v(-146.2, 12.93) * mm, "end": v(-146.12, 12.97) * mm});
            skLineSegment(sketch, "E369", {"start": v(-146.12, 12.97) * mm, "end": v(-146.04, 13) * mm});
            skLineSegment(sketch, "E370", {"start": v(-146.04, 13) * mm, "end": v(-145.96, 13.02) * mm});
            skLineSegment(sketch, "E371", {"start": v(-145.96, 13.02) * mm, "end": v(-145.87, 13.04) * mm});
            skLineSegment(sketch, "E372", {"start": v(-145.87, 13.04) * mm, "end": v(-145.78, 13.04) * mm});
            skLineSegment(sketch, "E373", {"start": v(-145.78, 13.04) * mm, "end": v(-123.48, 13.04) * mm});
            skLineSegment(sketch, "E374", {"start": v(-123.48, 13.04) * mm, "end": v(-123.35, 13.04) * mm});
            skLineSegment(sketch, "E375", {"start": v(-123.35, 13.04) * mm, "end": v(-123.24, 13.03) * mm});
            skLineSegment(sketch, "E376", {"start": v(-123.24, 13.03) * mm, "end": v(-123.13, 13) * mm});
            skLineSegment(sketch, "E377", {"start": v(-123.13, 13) * mm, "end": v(-123.03, 12.98) * mm});
            skLineSegment(sketch, "E378", {"start": v(-123.03, 12.98) * mm, "end": v(-122.94, 12.95) * mm});
            skLineSegment(sketch, "E379", {"start": v(-122.94, 12.95) * mm, "end": v(-122.86, 12.9) * mm});
            skLineSegment(sketch, "E380", {"start": v(-122.86, 12.9) * mm, "end": v(-122.78, 12.86) * mm});
            skLineSegment(sketch, "E381", {"start": v(-122.78, 12.86) * mm, "end": v(-122.72, 12.8) * mm});
            skLineSegment(sketch, "E382", {"start": v(-122.72, 12.8) * mm, "end": v(-122.66, 12.74) * mm});
            skLineSegment(sketch, "E383", {"start": v(-122.66, 12.74) * mm, "end": v(-122.6, 12.67) * mm});
            skLineSegment(sketch, "E384", {"start": v(-122.6, 12.67) * mm, "end": v(-122.56, 12.6) * mm});
            skLineSegment(sketch, "E385", {"start": v(-122.56, 12.6) * mm, "end": v(-122.53, 12.5) * mm});
            skLineSegment(sketch, "E386", {"start": v(-122.53, 12.5) * mm, "end": v(-122.5, 12.41) * mm});
            skLineSegment(sketch, "E387", {"start": v(-122.5, 12.41) * mm, "end": v(-122.48, 12.31) * mm});
            skLineSegment(sketch, "E388", {"start": v(-122.48, 12.31) * mm, "end": v(-122.47, 12.2) * mm});
            skLineSegment(sketch, "E389", {"start": v(-122.47, 12.2) * mm, "end": v(-122.47, 12.08) * mm});
            skLineSegment(sketch, "E390", {"start": v(-122.47, 12.08) * mm, "end": v(-122.47, 11.96) * mm});
            skLineSegment(sketch, "E391", {"start": v(-122.47, 11.96) * mm, "end": v(-122.48, 11.85) * mm});
            skLineSegment(sketch, "E392", {"start": v(-122.48, 11.85) * mm, "end": v(-122.5, 11.75) * mm});
            skLineSegment(sketch, "E393", {"start": v(-122.5, 11.75) * mm, "end": v(-122.53, 11.66) * mm});
            skLineSegment(sketch, "E394", {"start": v(-122.53, 11.66) * mm, "end": v(-122.56, 11.57) * mm});
            skLineSegment(sketch, "E395", {"start": v(-122.56, 11.57) * mm, "end": v(-122.6, 11.5) * mm});
            skLineSegment(sketch, "E396", {"start": v(-122.6, 11.5) * mm, "end": v(-122.66, 11.42) * mm});
            skLineSegment(sketch, "E397", {"start": v(-122.66, 11.42) * mm, "end": v(-122.72, 11.36) * mm});
            skLineSegment(sketch, "E398", {"start": v(-122.72, 11.36) * mm, "end": v(-122.78, 11.3) * mm});
            skLineSegment(sketch, "E399", {"start": v(-122.78, 11.3) * mm, "end": v(-122.86, 11.25) * mm});
            skLineSegment(sketch, "E400", {"start": v(-122.86, 11.25) * mm, "end": v(-122.94, 11.21) * mm});
            skLineSegment(sketch, "E401", {"start": v(-122.94, 11.21) * mm, "end": v(-123.03, 11.18) * mm});
            skLineSegment(sketch, "E402", {"start": v(-123.03, 11.18) * mm, "end": v(-123.13, 11.16) * mm});
            skLineSegment(sketch, "E403", {"start": v(-123.13, 11.16) * mm, "end": v(-123.24, 11.14) * mm});
            skLineSegment(sketch, "E404", {"start": v(-123.24, 11.14) * mm, "end": v(-123.35, 11.13) * mm});
            skLineSegment(sketch, "E405", {"start": v(-123.35, 11.13) * mm, "end": v(-123.48, 11.12) * mm});
            skLineSegment(sketch, "E406", {"start": v(-123.48, 11.12) * mm, "end": v(-138.3, 11.12) * mm});
            skLineSegment(sketch, "E407", {"start": v(-138.3, 11.12) * mm, "end": v(-138.64, 11.12) * mm});
            skLineSegment(sketch, "E408", {"start": v(-138.64, 11.12) * mm, "end": v(-138.98, 11.1) * mm});
            skLineSegment(sketch, "E409", {"start": v(-138.98, 11.1) * mm, "end": v(-139.3, 11.06) * mm});
            skLineSegment(sketch, "E410", {"start": v(-139.3, 11.06) * mm, "end": v(-139.63, 11) * mm});
            skLineSegment(sketch, "E411", {"start": v(-139.63, 11) * mm, "end": v(-139.95, 10.94) * mm});
            skLineSegment(sketch, "E412", {"start": v(-139.95, 10.94) * mm, "end": v(-140.25, 10.86) * mm});
            skLineSegment(sketch, "E413", {"start": v(-140.25, 10.86) * mm, "end": v(-140.55, 10.77) * mm});
            skLineSegment(sketch, "E414", {"start": v(-140.55, 10.77) * mm, "end": v(-140.85, 10.66) * mm});
            skLineSegment(sketch, "E415", {"start": v(-140.85, 10.66) * mm, "end": v(-141.13, 10.54) * mm});
            skLineSegment(sketch, "E416", {"start": v(-141.13, 10.54) * mm, "end": v(-141.41, 10.4) * mm});
            skLineSegment(sketch, "E417", {"start": v(-141.41, 10.4) * mm, "end": v(-141.68, 10.26) * mm});
            skLineSegment(sketch, "E418", {"start": v(-141.68, 10.26) * mm, "end": v(-141.94, 10.1) * mm});
            skLineSegment(sketch, "E419", {"start": v(-141.94, 10.1) * mm, "end": v(-142.2, 9.91) * mm});
            skLineSegment(sketch, "E420", {"start": v(-142.2, 9.91) * mm, "end": v(-142.45, 9.72) * mm});
            skLineSegment(sketch, "E421", {"start": v(-142.45, 9.72) * mm, "end": v(-142.69, 9.52) * mm});
            skLineSegment(sketch, "E422", {"start": v(-142.69, 9.52) * mm, "end": v(-142.92, 9.3) * mm});
            skLineSegment(sketch, "E423", {"start": v(-142.92, 9.3) * mm, "end": v(-143.14, 9.06) * mm});
            skLineSegment(sketch, "E424", {"start": v(-143.14, 9.06) * mm, "end": v(-143.34, 8.82) * mm});
            skLineSegment(sketch, "E425", {"start": v(-143.34, 8.82) * mm, "end": v(-143.54, 8.58) * mm});
            skLineSegment(sketch, "E426", {"start": v(-143.54, 8.58) * mm, "end": v(-143.72, 8.32) * mm});
            skLineSegment(sketch, "E427", {"start": v(-143.72, 8.32) * mm, "end": v(-143.88, 8.06) * mm});
            skLineSegment(sketch, "E428", {"start": v(-143.88, 8.06) * mm, "end": v(-144.03, 7.79) * mm});
            skLineSegment(sketch, "E429", {"start": v(-144.03, 7.79) * mm, "end": v(-144.17, 7.5) * mm});
            skLineSegment(sketch, "E430", {"start": v(-144.17, 7.5) * mm, "end": v(-144.29, 7.22) * mm});
            skLineSegment(sketch, "E431", {"start": v(-144.29, 7.22) * mm, "end": v(-144.4, 6.93) * mm});
            skLineSegment(sketch, "E432", {"start": v(-144.4, 6.93) * mm, "end": v(-144.49, 6.63) * mm});
            skLineSegment(sketch, "E433", {"start": v(-144.49, 6.63) * mm, "end": v(-144.57, 6.32) * mm});
            skLineSegment(sketch, "E434", {"start": v(-144.57, 6.32) * mm, "end": v(-144.63, 6) * mm});
            skLineSegment(sketch, "E435", {"start": v(-144.63, 6) * mm, "end": v(-144.68, 5.68) * mm});
            skLineSegment(sketch, "E436", {"start": v(-144.68, 5.68) * mm, "end": v(-144.72, 5.35) * mm});
            skLineSegment(sketch, "E437", {"start": v(-144.72, 5.35) * mm, "end": v(-144.74, 5.02) * mm});
            skLineSegment(sketch, "E438", {"start": v(-144.74, 5.02) * mm, "end": v(-144.75, 4.67) * mm});
            skLineSegment(sketch, "E439", {"start": v(-144.75, 4.67) * mm, "end": v(-144.74, 4.33) * mm});
            skLineSegment(sketch, "E440", {"start": v(-144.74, 4.33) * mm, "end": v(-144.72, 4) * mm});
            skLineSegment(sketch, "E441", {"start": v(-144.72, 4) * mm, "end": v(-144.68, 3.66) * mm});
            skLineSegment(sketch, "E442", {"start": v(-144.68, 3.66) * mm, "end": v(-144.63, 3.34) * mm});
            skLineSegment(sketch, "E443", {"start": v(-144.63, 3.34) * mm, "end": v(-144.57, 3.02) * mm});
            skLineSegment(sketch, "E444", {"start": v(-144.57, 3.02) * mm, "end": v(-144.49, 2.72) * mm});
            skLineSegment(sketch, "E445", {"start": v(-144.49, 2.72) * mm, "end": v(-144.4, 2.42) * mm});
            skLineSegment(sketch, "E446", {"start": v(-144.4, 2.42) * mm, "end": v(-144.29, 2.12) * mm});
            skLineSegment(sketch, "E447", {"start": v(-144.29, 2.12) * mm, "end": v(-144.17, 1.84) * mm});
            skLineSegment(sketch, "E448", {"start": v(-144.17, 1.84) * mm, "end": v(-144.03, 1.56) * mm});
            skLineSegment(sketch, "E449", {"start": v(-144.03, 1.56) * mm, "end": v(-143.88, 1.29) * mm});
            skLineSegment(sketch, "E450", {"start": v(-143.88, 1.29) * mm, "end": v(-143.72, 1.02) * mm});
            skLineSegment(sketch, "E451", {"start": v(-143.72, 1.02) * mm, "end": v(-143.54, 0.77) * mm});
            skLineSegment(sketch, "E452", {"start": v(-143.54, 0.77) * mm, "end": v(-143.35, 0.52) * mm});
            skLineSegment(sketch, "E453", {"start": v(-143.35, 0.52) * mm, "end": v(-143.14, 0.28) * mm});
            skLineSegment(sketch, "E454", {"start": v(-143.14, 0.28) * mm, "end": v(-142.92, 0.05) * mm});
            skLineSegment(sketch, "E455", {"start": v(-142.92, 0.05) * mm, "end": v(-142.69, -0.17) * mm});
            skLineSegment(sketch, "E456", {"start": v(-142.69, -0.17) * mm, "end": v(-142.45, -0.37) * mm});
            skLineSegment(sketch, "E457", {"start": v(-142.45, -0.37) * mm, "end": v(-142.2, -0.57) * mm});
            skLineSegment(sketch, "E458", {"start": v(-142.2, -0.57) * mm, "end": v(-141.95, -0.75) * mm});
            skLineSegment(sketch, "E459", {"start": v(-141.95, -0.75) * mm, "end": v(-141.68, -0.9) * mm});
            skLineSegment(sketch, "E460", {"start": v(-141.68, -0.9) * mm, "end": v(-141.41, -1.06) * mm});
            skLineSegment(sketch, "E461", {"start": v(-141.41, -1.06) * mm, "end": v(-141.13, -1.2) * mm});
            skLineSegment(sketch, "E462", {"start": v(-141.13, -1.2) * mm, "end": v(-140.85, -1.32) * mm});
            skLineSegment(sketch, "E463", {"start": v(-140.85, -1.32) * mm, "end": v(-140.55, -1.42) * mm});
            skLineSegment(sketch, "E464", {"start": v(-140.55, -1.42) * mm, "end": v(-140.25, -1.52) * mm});
            skLineSegment(sketch, "E465", {"start": v(-140.25, -1.52) * mm, "end": v(-139.95, -1.6) * mm});
            skLineSegment(sketch, "E466", {"start": v(-139.95, -1.6) * mm, "end": v(-139.63, -1.66) * mm});
            skLineSegment(sketch, "E467", {"start": v(-139.63, -1.66) * mm, "end": v(-139.3, -1.71) * mm});
            skLineSegment(sketch, "E468", {"start": v(-139.3, -1.71) * mm, "end": v(-138.98, -1.75) * mm});
            skLineSegment(sketch, "E469", {"start": v(-138.98, -1.75) * mm, "end": v(-138.64, -1.77) * mm});
            skLineSegment(sketch, "E470", {"start": v(-138.64, -1.77) * mm, "end": v(-138.3, -1.78) * mm});
            skLineSegment(sketch, "E471", {"start": v(-138.3, -1.78) * mm, "end": v(-128.4, -1.78) * mm});
            skLineSegment(sketch, "E472", {"start": v(-128.4, -1.78) * mm, "end": v(-128.28, -1.78) * mm});
            skLineSegment(sketch, "E473", {"start": v(-128.28, -1.78) * mm, "end": v(-128.17, -1.8) * mm});
            skLineSegment(sketch, "E474", {"start": v(-128.17, -1.8) * mm, "end": v(-128.07, -1.8) * mm});
            skLineSegment(sketch, "E475", {"start": v(-128.07, -1.8) * mm, "end": v(-127.98, -1.83) * mm});
            skLineSegment(sketch, "E476", {"start": v(-127.98, -1.83) * mm, "end": v(-127.89, -1.86) * mm});
            skLineSegment(sketch, "E477", {"start": v(-127.89, -1.86) * mm, "end": v(-127.81, -1.9) * mm});
            skLineSegment(sketch, "E478", {"start": v(-127.81, -1.9) * mm, "end": v(-127.74, -1.95) * mm});
            skLineSegment(sketch, "E479", {"start": v(-127.74, -1.95) * mm, "end": v(-127.68, -2) * mm});
            skLineSegment(sketch, "E480", {"start": v(-127.68, -2) * mm, "end": v(-127.62, -2.07) * mm});
            skLineSegment(sketch, "E481", {"start": v(-127.62, -2.07) * mm, "end": v(-127.57, -2.13) * mm});
            skLineSegment(sketch, "E482", {"start": v(-127.57, -2.13) * mm, "end": v(-127.53, -2.21) * mm});
            skLineSegment(sketch, "E483", {"start": v(-127.53, -2.21) * mm, "end": v(-127.5, -2.3) * mm});
            skLineSegment(sketch, "E484", {"start": v(-127.5, -2.3) * mm, "end": v(-127.48, -2.39) * mm});
            skLineSegment(sketch, "E485", {"start": v(-127.48, -2.39) * mm, "end": v(-127.46, -2.49) * mm});
            skLineSegment(sketch, "E486", {"start": v(-127.46, -2.49) * mm, "end": v(-127.45, -2.6) * mm});
            skLineSegment(sketch, "E487", {"start": v(-127.45, -2.6) * mm, "end": v(-127.44, -2.7) * mm});
            skLineSegment(sketch, "E488", {"start": v(-127.44, -2.7) * mm, "end": v(-127.45, -2.83) * mm});
            skLineSegment(sketch, "E489", {"start": v(-127.45, -2.83) * mm, "end": v(-127.46, -2.94) * mm});
            skLineSegment(sketch, "E490", {"start": v(-127.46, -2.94) * mm, "end": v(-127.48, -3.05) * mm});
            skLineSegment(sketch, "E491", {"start": v(-127.48, -3.05) * mm, "end": v(-127.5, -3.15) * mm});
            skLineSegment(sketch, "E492", {"start": v(-127.5, -3.15) * mm, "end": v(-127.53, -3.24) * mm});
            skLineSegment(sketch, "E493", {"start": v(-127.53, -3.24) * mm, "end": v(-127.57, -3.32) * mm});
            skLineSegment(sketch, "E494", {"start": v(-127.57, -3.32) * mm, "end": v(-127.62, -3.39) * mm});
            skLineSegment(sketch, "E495", {"start": v(-127.62, -3.39) * mm, "end": v(-127.68, -3.45) * mm});
            skLineSegment(sketch, "E496", {"start": v(-127.68, -3.45) * mm, "end": v(-127.74, -3.51) * mm});
            skLineSegment(sketch, "E497", {"start": v(-127.74, -3.51) * mm, "end": v(-127.81, -3.56) * mm});
            skLineSegment(sketch, "E498", {"start": v(-127.81, -3.56) * mm, "end": v(-127.89, -3.6) * mm});
            skLineSegment(sketch, "E499", {"start": v(-127.89, -3.6) * mm, "end": v(-127.98, -3.63) * mm});
            skLineSegment(sketch, "E500", {"start": v(-127.98, -3.63) * mm, "end": v(-128.07, -3.66) * mm});
            skLineSegment(sketch, "E501", {"start": v(-128.07, -3.66) * mm, "end": v(-128.17, -3.68) * mm});
            skLineSegment(sketch, "E502", {"start": v(-128.17, -3.68) * mm, "end": v(-128.28, -3.69) * mm});
            skLineSegment(sketch, "E503", {"start": v(-128.28, -3.69) * mm, "end": v(-128.4, -3.7) * mm});
            skLineSegment(sketch, "E504", {"start": v(-128.4, -3.7) * mm, "end": v(-138.3, -3.7) * mm});
            skLineSegment(sketch, "E505", {"start": v(-138.3, -3.7) * mm, "end": v(-138.64, -3.7) * mm});
            skLineSegment(sketch, "E506", {"start": v(-138.64, -3.7) * mm, "end": v(-138.98, -3.72) * mm});
            skLineSegment(sketch, "E507", {"start": v(-138.98, -3.72) * mm, "end": v(-139.3, -3.76) * mm});
            skLineSegment(sketch, "E508", {"start": v(-139.3, -3.76) * mm, "end": v(-139.63, -3.8) * mm});
            skLineSegment(sketch, "E509", {"start": v(-139.63, -3.8) * mm, "end": v(-139.95, -3.87) * mm});
            skLineSegment(sketch, "E510", {"start": v(-139.95, -3.87) * mm, "end": v(-140.25, -3.95) * mm});
            skLineSegment(sketch, "E511", {"start": v(-140.25, -3.95) * mm, "end": v(-140.55, -4.04) * mm});
            skLineSegment(sketch, "E512", {"start": v(-140.55, -4.04) * mm, "end": v(-140.85, -4.15) * mm});
            skLineSegment(sketch, "E513", {"start": v(-140.85, -4.15) * mm, "end": v(-141.13, -4.27) * mm});
            skLineSegment(sketch, "E514", {"start": v(-141.13, -4.27) * mm, "end": v(-141.41, -4.4) * mm});
            skLineSegment(sketch, "E515", {"start": v(-141.41, -4.4) * mm, "end": v(-141.68, -4.55) * mm});
            skLineSegment(sketch, "E516", {"start": v(-141.68, -4.55) * mm, "end": v(-141.94, -4.72) * mm});
            skLineSegment(sketch, "E517", {"start": v(-141.94, -4.72) * mm, "end": v(-142.2, -4.9) * mm});
            skLineSegment(sketch, "E518", {"start": v(-142.2, -4.9) * mm, "end": v(-142.45, -5.09) * mm});
            skLineSegment(sketch, "E519", {"start": v(-142.45, -5.09) * mm, "end": v(-142.69, -5.3) * mm});
            skLineSegment(sketch, "E520", {"start": v(-142.69, -5.3) * mm, "end": v(-142.92, -5.51) * mm});
            skLineSegment(sketch, "E521", {"start": v(-142.92, -5.51) * mm, "end": v(-143.14, -5.74) * mm});
            skLineSegment(sketch, "E522", {"start": v(-143.14, -5.74) * mm, "end": v(-143.34, -5.98) * mm});
            skLineSegment(sketch, "E523", {"start": v(-143.34, -5.98) * mm, "end": v(-143.54, -6.23) * mm});
            skLineSegment(sketch, "E524", {"start": v(-143.54, -6.23) * mm, "end": v(-143.72, -6.48) * mm});
            skLineSegment(sketch, "E525", {"start": v(-143.72, -6.48) * mm, "end": v(-143.88, -6.74) * mm});
            skLineSegment(sketch, "E526", {"start": v(-143.88, -6.74) * mm, "end": v(-144.03, -7.01) * mm});
            skLineSegment(sketch, "E527", {"start": v(-144.03, -7.01) * mm, "end": v(-144.17, -7.3) * mm});
            skLineSegment(sketch, "E528", {"start": v(-144.17, -7.3) * mm, "end": v(-144.29, -7.58) * mm});
            skLineSegment(sketch, "E529", {"start": v(-144.29, -7.58) * mm, "end": v(-144.4, -7.87) * mm});
            skLineSegment(sketch, "E530", {"start": v(-144.4, -7.87) * mm, "end": v(-144.49, -8.17) * mm});
            skLineSegment(sketch, "E531", {"start": v(-144.49, -8.17) * mm, "end": v(-144.57, -8.48) * mm});
            skLineSegment(sketch, "E532", {"start": v(-144.57, -8.48) * mm, "end": v(-144.63, -8.8) * mm});
            skLineSegment(sketch, "E533", {"start": v(-144.63, -8.8) * mm, "end": v(-144.68, -9.13) * mm});
            skLineSegment(sketch, "E534", {"start": v(-144.68, -9.13) * mm, "end": v(-144.72, -9.46) * mm});
            skLineSegment(sketch, "E535", {"start": v(-144.72, -9.46) * mm, "end": v(-144.74, -9.8) * mm});
            skLineSegment(sketch, "E536", {"start": v(-144.74, -9.8) * mm, "end": v(-144.75, -10.14) * mm});
            skLineSegment(sketch, "E537", {"start": v(-144.75, -10.14) * mm, "end": v(-144.74, -10.5) * mm});
            skLineSegment(sketch, "E538", {"start": v(-144.74, -10.5) * mm, "end": v(-144.72, -10.83) * mm});
            skLineSegment(sketch, "E539", {"start": v(-144.72, -10.83) * mm, "end": v(-144.68, -11.16) * mm});
            skLineSegment(sketch, "E540", {"start": v(-144.68, -11.16) * mm, "end": v(-144.63, -11.49) * mm});
            skLineSegment(sketch, "E541", {"start": v(-144.63, -11.49) * mm, "end": v(-144.57, -11.8) * mm});
            skLineSegment(sketch, "E542", {"start": v(-144.57, -11.8) * mm, "end": v(-144.49, -12.12) * mm});
            skLineSegment(sketch, "E543", {"start": v(-144.49, -12.12) * mm, "end": v(-144.4, -12.42) * mm});
            skLineSegment(sketch, "E544", {"start": v(-144.4, -12.42) * mm, "end": v(-144.29, -12.72) * mm});
            skLineSegment(sketch, "E545", {"start": v(-144.29, -12.72) * mm, "end": v(-144.17, -13) * mm});
            skLineSegment(sketch, "E546", {"start": v(-144.17, -13) * mm, "end": v(-144.03, -13.28) * mm});
            skLineSegment(sketch, "E547", {"start": v(-144.03, -13.28) * mm, "end": v(-143.88, -13.56) * mm});
            skLineSegment(sketch, "E548", {"start": v(-143.88, -13.56) * mm, "end": v(-143.72, -13.82) * mm});
            skLineSegment(sketch, "E549", {"start": v(-143.72, -13.82) * mm, "end": v(-143.54, -14.08) * mm});
            skLineSegment(sketch, "E550", {"start": v(-143.54, -14.08) * mm, "end": v(-143.35, -14.33) * mm});
            skLineSegment(sketch, "E551", {"start": v(-143.35, -14.33) * mm, "end": v(-143.14, -14.57) * mm});
            skLineSegment(sketch, "E552", {"start": v(-143.14, -14.57) * mm, "end": v(-142.92, -14.8) * mm});
            skLineSegment(sketch, "E553", {"start": v(-142.92, -14.8) * mm, "end": v(-142.69, -15.02) * mm});
            skLineSegment(sketch, "E554", {"start": v(-142.69, -15.02) * mm, "end": v(-142.45, -15.23) * mm});
            skLineSegment(sketch, "E555", {"start": v(-142.45, -15.23) * mm, "end": v(-142.2, -15.43) * mm});
            skLineSegment(sketch, "E556", {"start": v(-142.2, -15.43) * mm, "end": v(-141.95, -15.6) * mm});
            skLineSegment(sketch, "E557", {"start": v(-141.95, -15.6) * mm, "end": v(-141.68, -15.77) * mm});
            skLineSegment(sketch, "E558", {"start": v(-141.68, -15.77) * mm, "end": v(-141.41, -15.92) * mm});
            skLineSegment(sketch, "E559", {"start": v(-141.41, -15.92) * mm, "end": v(-141.13, -16.06) * mm});
            skLineSegment(sketch, "E560", {"start": v(-141.13, -16.06) * mm, "end": v(-140.85, -16.18) * mm});
            skLineSegment(sketch, "E561", {"start": v(-140.85, -16.18) * mm, "end": v(-140.55, -16.3) * mm});
            skLineSegment(sketch, "E562", {"start": v(-140.55, -16.3) * mm, "end": v(-140.25, -16.39) * mm});
            skLineSegment(sketch, "E563", {"start": v(-140.25, -16.39) * mm, "end": v(-139.95, -16.46) * mm});
            skLineSegment(sketch, "E564", {"start": v(-139.95, -16.46) * mm, "end": v(-139.63, -16.53) * mm});
            skLineSegment(sketch, "E565", {"start": v(-139.63, -16.53) * mm, "end": v(-139.3, -16.58) * mm});
            skLineSegment(sketch, "E566", {"start": v(-139.3, -16.58) * mm, "end": v(-138.98, -16.62) * mm});
            skLineSegment(sketch, "E567", {"start": v(-138.98, -16.62) * mm, "end": v(-138.64, -16.64) * mm});
            skLineSegment(sketch, "E568", {"start": v(-138.64, -16.64) * mm, "end": v(-138.3, -16.65) * mm});
            skLineSegment(sketch, "E569", {"start": v(-138.3, -16.65) * mm, "end": v(-123.48, -16.65) * mm});
            skLineSegment(sketch, "E570", {"start": v(-123.48, -16.65) * mm, "end": v(-123.35, -16.65) * mm});
            skLineSegment(sketch, "E571", {"start": v(-123.35, -16.65) * mm, "end": v(-123.24, -16.66) * mm});
            skLineSegment(sketch, "E572", {"start": v(-123.24, -16.66) * mm, "end": v(-123.13, -16.68) * mm});
            skLineSegment(sketch, "E573", {"start": v(-123.13, -16.68) * mm, "end": v(-123.03, -16.7) * mm});
            skLineSegment(sketch, "E574", {"start": v(-123.03, -16.7) * mm, "end": v(-122.94, -16.74) * mm});
            skLineSegment(sketch, "E575", {"start": v(-122.94, -16.74) * mm, "end": v(-122.86, -16.78) * mm});
            skLineSegment(sketch, "E576", {"start": v(-122.86, -16.78) * mm, "end": v(-122.78, -16.83) * mm});
            skLineSegment(sketch, "E577", {"start": v(-122.78, -16.83) * mm, "end": v(-122.72, -16.89) * mm});
            skLineSegment(sketch, "E578", {"start": v(-122.72, -16.89) * mm, "end": v(-122.66, -16.95) * mm});
            skLineSegment(sketch, "E579", {"start": v(-122.66, -16.95) * mm, "end": v(-122.6, -17.02) * mm});
            skLineSegment(sketch, "E580", {"start": v(-122.6, -17.02) * mm, "end": v(-122.56, -17.1) * mm});
            skLineSegment(sketch, "E581", {"start": v(-122.56, -17.1) * mm, "end": v(-122.53, -17.2) * mm});
            skLineSegment(sketch, "E582", {"start": v(-122.53, -17.2) * mm, "end": v(-122.5, -17.3) * mm});
            skLineSegment(sketch, "E583", {"start": v(-122.5, -17.3) * mm, "end": v(-122.48, -17.4) * mm});
            skLineSegment(sketch, "E584", {"start": v(-122.48, -17.4) * mm, "end": v(-122.47, -17.5) * mm});
            skLineSegment(sketch, "E585", {"start": v(-122.47, -17.5) * mm, "end": v(-122.47, -17.63) * mm});
            skLineSegment(sketch, "E586", {"start": v(-122.47, -17.63) * mm, "end": v(-122.47, -17.75) * mm});
            skLineSegment(sketch, "E587", {"start": v(-122.47, -17.75) * mm, "end": v(-122.48, -17.85) * mm});
            skLineSegment(sketch, "E588", {"start": v(-122.48, -17.85) * mm, "end": v(-122.5, -17.95) * mm});
            skLineSegment(sketch, "E589", {"start": v(-122.5, -17.95) * mm, "end": v(-122.53, -18.04) * mm});
            skLineSegment(sketch, "E590", {"start": v(-122.53, -18.04) * mm, "end": v(-122.56, -18.13) * mm});
            skLineSegment(sketch, "E591", {"start": v(-122.56, -18.13) * mm, "end": v(-122.6, -18.2) * mm});
            skLineSegment(sketch, "E592", {"start": v(-122.6, -18.2) * mm, "end": v(-122.66, -18.27) * mm});
            skLineSegment(sketch, "E593", {"start": v(-122.66, -18.27) * mm, "end": v(-122.72, -18.34) * mm});
            skLineSegment(sketch, "E594", {"start": v(-122.72, -18.34) * mm, "end": v(-122.78, -18.39) * mm});
            skLineSegment(sketch, "E595", {"start": v(-122.78, -18.39) * mm, "end": v(-122.86, -18.44) * mm});
            skLineSegment(sketch, "E596", {"start": v(-122.86, -18.44) * mm, "end": v(-122.94, -18.47) * mm});
            skLineSegment(sketch, "E597", {"start": v(-122.94, -18.47) * mm, "end": v(-123.03, -18.5) * mm});
            skLineSegment(sketch, "E598", {"start": v(-123.03, -18.5) * mm, "end": v(-123.13, -18.53) * mm});
            skLineSegment(sketch, "E599", {"start": v(-123.13, -18.53) * mm, "end": v(-123.24, -18.55) * mm});
            skLineSegment(sketch, "E600", {"start": v(-123.24, -18.55) * mm, "end": v(-123.35, -18.56) * mm});
            skLineSegment(sketch, "E601", {"start": v(-123.35, -18.56) * mm, "end": v(-123.48, -18.56) * mm});
            skLineSegment(sketch, "E602", {"start": v(-123.48, -18.56) * mm, "end": v(-140.73, -18.56) * mm});
            skLineSegment(sketch, "E603", {"start": v(-140.73, -18.56) * mm, "end": v(-140.94, -18.57) * mm});
            skLineSegment(sketch, "E604", {"start": v(-140.94, -18.57) * mm, "end": v(-141.15, -18.58) * mm});
            skLineSegment(sketch, "E605", {"start": v(-141.15, -18.58) * mm, "end": v(-141.36, -18.6) * mm});
            skLineSegment(sketch, "E606", {"start": v(-141.36, -18.6) * mm, "end": v(-141.56, -18.63) * mm});
            skLineSegment(sketch, "E607", {"start": v(-141.56, -18.63) * mm, "end": v(-141.75, -18.67) * mm});
            skLineSegment(sketch, "E608", {"start": v(-141.75, -18.67) * mm, "end": v(-141.95, -18.72) * mm});
            skLineSegment(sketch, "E609", {"start": v(-141.95, -18.72) * mm, "end": v(-142.13, -18.78) * mm});
            skLineSegment(sketch, "E610", {"start": v(-142.13, -18.78) * mm, "end": v(-142.31, -18.84) * mm});
            skLineSegment(sketch, "E611", {"start": v(-142.31, -18.84) * mm, "end": v(-142.5, -18.92) * mm});
            skLineSegment(sketch, "E612", {"start": v(-142.5, -18.92) * mm, "end": v(-142.67, -19) * mm});
            skLineSegment(sketch, "E613", {"start": v(-142.67, -19) * mm, "end": v(-142.83, -19.1) * mm});
            skLineSegment(sketch, "E614", {"start": v(-142.83, -19.1) * mm, "end": v(-143, -19.2) * mm});
            skLineSegment(sketch, "E615", {"start": v(-143, -19.2) * mm, "end": v(-143.16, -19.3) * mm});
            skLineSegment(sketch, "E616", {"start": v(-143.16, -19.3) * mm, "end": v(-143.31, -19.42) * mm});
            skLineSegment(sketch, "E617", {"start": v(-143.31, -19.42) * mm, "end": v(-143.46, -19.54) * mm});
            skLineSegment(sketch, "E618", {"start": v(-143.46, -19.54) * mm, "end": v(-143.6, -19.68) * mm});
            skLineSegment(sketch, "E619", {"start": v(-143.6, -19.68) * mm, "end": v(-143.74, -19.82) * mm});
            skLineSegment(sketch, "E620", {"start": v(-143.74, -19.82) * mm, "end": v(-143.87, -19.96) * mm});
            skLineSegment(sketch, "E621", {"start": v(-143.87, -19.96) * mm, "end": v(-144, -20.11) * mm});
            skLineSegment(sketch, "E622", {"start": v(-144, -20.11) * mm, "end": v(-144.1, -20.27) * mm});
            skLineSegment(sketch, "E623", {"start": v(-144.1, -20.27) * mm, "end": v(-144.2, -20.43) * mm});
            skLineSegment(sketch, "E624", {"start": v(-144.2, -20.43) * mm, "end": v(-144.3, -20.6) * mm});
            skLineSegment(sketch, "E625", {"start": v(-144.3, -20.6) * mm, "end": v(-144.38, -20.77) * mm});
            skLineSegment(sketch, "E626", {"start": v(-144.38, -20.77) * mm, "end": v(-144.46, -20.95) * mm});
            skLineSegment(sketch, "E627", {"start": v(-144.46, -20.95) * mm, "end": v(-144.53, -21.13) * mm});
            skLineSegment(sketch, "E628", {"start": v(-144.53, -21.13) * mm, "end": v(-144.59, -21.31) * mm});
            skLineSegment(sketch, "E629", {"start": v(-144.59, -21.31) * mm, "end": v(-144.63, -21.5) * mm});
            skLineSegment(sketch, "E630", {"start": v(-144.63, -21.5) * mm, "end": v(-144.67, -21.7) * mm});
            skLineSegment(sketch, "E631", {"start": v(-144.67, -21.7) * mm, "end": v(-144.7, -21.9) * mm});
            skLineSegment(sketch, "E632", {"start": v(-144.7, -21.9) * mm, "end": v(-144.73, -22.1) * mm});
            skLineSegment(sketch, "E633", {"start": v(-144.73, -22.1) * mm, "end": v(-144.74, -22.31) * mm});
            skLineSegment(sketch, "E634", {"start": v(-144.74, -22.31) * mm, "end": v(-144.75, -22.53) * mm});
            skLineSegment(sketch, "E635", {"start": v(-144.75, -22.53) * mm, "end": v(-144.74, -22.74) * mm});
            skLineSegment(sketch, "E636", {"start": v(-144.74, -22.74) * mm, "end": v(-144.73, -22.95) * mm});
            skLineSegment(sketch, "E637", {"start": v(-144.73, -22.95) * mm, "end": v(-144.7, -23.15) * mm});
            skLineSegment(sketch, "E638", {"start": v(-144.7, -23.15) * mm, "end": v(-144.67, -23.35) * mm});
            skLineSegment(sketch, "E639", {"start": v(-144.67, -23.35) * mm, "end": v(-144.63, -23.55) * mm});
            skLineSegment(sketch, "E640", {"start": v(-144.63, -23.55) * mm, "end": v(-144.59, -23.74) * mm});
            skLineSegment(sketch, "E641", {"start": v(-144.59, -23.74) * mm, "end": v(-144.53, -23.92) * mm});
            skLineSegment(sketch, "E642", {"start": v(-144.53, -23.92) * mm, "end": v(-144.46, -24.1) * mm});
            skLineSegment(sketch, "E643", {"start": v(-144.46, -24.1) * mm, "end": v(-144.38, -24.28) * mm});
            skLineSegment(sketch, "E644", {"start": v(-144.38, -24.28) * mm, "end": v(-144.3, -24.45) * mm});
            skLineSegment(sketch, "E645", {"start": v(-144.3, -24.45) * mm, "end": v(-144.2, -24.62) * mm});
            skLineSegment(sketch, "E646", {"start": v(-144.2, -24.62) * mm, "end": v(-144.1, -24.78) * mm});
            skLineSegment(sketch, "E647", {"start": v(-144.1, -24.78) * mm, "end": v(-144, -24.94) * mm});
            skLineSegment(sketch, "E648", {"start": v(-144, -24.94) * mm, "end": v(-143.87, -25.09) * mm});
            skLineSegment(sketch, "E649", {"start": v(-143.87, -25.09) * mm, "end": v(-143.74, -25.23) * mm});
            skLineSegment(sketch, "E650", {"start": v(-143.74, -25.23) * mm, "end": v(-143.6, -25.38) * mm});
            skLineSegment(sketch, "E651", {"start": v(-143.6, -25.38) * mm, "end": v(-143.46, -25.5) * mm});
            skLineSegment(sketch, "E652", {"start": v(-143.46, -25.5) * mm, "end": v(-143.31, -25.64) * mm});
            skLineSegment(sketch, "E653", {"start": v(-143.31, -25.64) * mm, "end": v(-143.16, -25.75) * mm});
            skLineSegment(sketch, "E654", {"start": v(-143.16, -25.75) * mm, "end": v(-143, -25.86) * mm});
            skLineSegment(sketch, "E655", {"start": v(-143, -25.86) * mm, "end": v(-142.84, -25.96) * mm});
            skLineSegment(sketch, "E656", {"start": v(-142.84, -25.96) * mm, "end": v(-142.67, -26.05) * mm});
            skLineSegment(sketch, "E657", {"start": v(-142.67, -26.05) * mm, "end": v(-142.5, -26.14) * mm});
            skLineSegment(sketch, "E658", {"start": v(-142.5, -26.14) * mm, "end": v(-142.32, -26.2) * mm});
            skLineSegment(sketch, "E659", {"start": v(-142.32, -26.2) * mm, "end": v(-142.13, -26.27) * mm});
            skLineSegment(sketch, "E660", {"start": v(-142.13, -26.27) * mm, "end": v(-141.95, -26.33) * mm});
            skLineSegment(sketch, "E661", {"start": v(-141.95, -26.33) * mm, "end": v(-141.75, -26.38) * mm});
            skLineSegment(sketch, "E662", {"start": v(-141.75, -26.38) * mm, "end": v(-141.56, -26.42) * mm});
            skLineSegment(sketch, "E663", {"start": v(-141.56, -26.42) * mm, "end": v(-141.36, -26.45) * mm});
            skLineSegment(sketch, "E664", {"start": v(-141.36, -26.45) * mm, "end": v(-141.15, -26.47) * mm});
            skLineSegment(sketch, "E665", {"start": v(-141.15, -26.47) * mm, "end": v(-140.94, -26.48) * mm});
            skLineSegment(sketch, "E666", {"start": v(-140.94, -26.48) * mm, "end": v(-140.73, -26.49) * mm});
            skLineSegment(sketch, "E667", {"start": v(-140.73, -26.49) * mm, "end": v(-100, -26.49) * mm});
            skLineSegment(sketch, "E668", {"start": v(-100, -26.49) * mm, "end": v(-99.68, -26.47) * mm});
            skLineSegment(sketch, "E669", {"start": v(-99.68, -26.47) * mm, "end": v(-99.37, -26.42) * mm});
            skLineSegment(sketch, "E670", {"start": v(-99.37, -26.42) * mm, "end": v(-99.07, -26.35) * mm});
            skLineSegment(sketch, "E671", {"start": v(-99.07, -26.35) * mm, "end": v(-98.78, -26.24) * mm});
            skLineSegment(sketch, "E672", {"start": v(-98.78, -26.24) * mm, "end": v(-98.5, -26.11) * mm});
            skLineSegment(sketch, "E673", {"start": v(-98.5, -26.11) * mm, "end": v(-98.25, -25.95) * mm});
            skLineSegment(sketch, "E674", {"start": v(-98.25, -25.95) * mm, "end": v(-98.01, -25.77) * mm});
            skLineSegment(sketch, "E675", {"start": v(-98.01, -25.77) * mm, "end": v(-97.79, -25.57) * mm});
            skLineSegment(sketch, "E676", {"start": v(-97.79, -25.57) * mm, "end": v(-97.59, -25.35) * mm});
            skLineSegment(sketch, "E677", {"start": v(-97.59, -25.35) * mm, "end": v(-97.4, -25.1) * mm});
            skLineSegment(sketch, "E678", {"start": v(-97.4, -25.1) * mm, "end": v(-97.25, -24.85) * mm});
            skLineSegment(sketch, "E679", {"start": v(-97.25, -24.85) * mm, "end": v(-97.12, -24.57) * mm});
            skLineSegment(sketch, "E680", {"start": v(-97.12, -24.57) * mm, "end": v(-97.01, -24.29) * mm});
            skLineSegment(sketch, "E681", {"start": v(-97.01, -24.29) * mm, "end": v(-96.93, -23.99) * mm});
            skLineSegment(sketch, "E682", {"start": v(-96.93, -23.99) * mm, "end": v(-96.89, -23.68) * mm});
            skLineSegment(sketch, "E683", {"start": v(-96.89, -23.68) * mm, "end": v(-96.87, -23.36) * mm});
            skLineSegment(sketch, "E684", {"start": v(-96.87, -23.36) * mm, "end": v(-96.87, -19.84) * mm});
            skLineSegment(sketch, "E685", {"start": v(-96.87, -19.84) * mm, "end": v(-96.88, -19.7) * mm});
            skLineSegment(sketch, "E686", {"start": v(-96.88, -19.7) * mm, "end": v(-96.9, -19.56) * mm});
            skLineSegment(sketch, "E687", {"start": v(-96.9, -19.56) * mm, "end": v(-96.93, -19.43) * mm});
            skLineSegment(sketch, "E688", {"start": v(-96.93, -19.43) * mm, "end": v(-96.97, -19.3) * mm});
            skLineSegment(sketch, "E689", {"start": v(-96.97, -19.3) * mm, "end": v(-97.02, -19.18) * mm});
            skLineSegment(sketch, "E690", {"start": v(-97.02, -19.18) * mm, "end": v(-97.09, -19.06) * mm});
            skLineSegment(sketch, "E691", {"start": v(-97.09, -19.06) * mm, "end": v(-97.16, -18.95) * mm});
            skLineSegment(sketch, "E692", {"start": v(-97.16, -18.95) * mm, "end": v(-97.24, -18.85) * mm});
            skLineSegment(sketch, "E693", {"start": v(-97.24, -18.85) * mm, "end": v(-97.33, -18.75) * mm});
            skLineSegment(sketch, "E694", {"start": v(-97.33, -18.75) * mm, "end": v(-97.43, -18.67) * mm});
            skLineSegment(sketch, "E695", {"start": v(-97.43, -18.67) * mm, "end": v(-97.54, -18.59) * mm});
            skLineSegment(sketch, "E696", {"start": v(-97.54, -18.59) * mm, "end": v(-97.66, -18.52) * mm});
            skLineSegment(sketch, "E697", {"start": v(-97.66, -18.52) * mm, "end": v(-97.78, -18.46) * mm});
            skLineSegment(sketch, "E698", {"start": v(-97.78, -18.46) * mm, "end": v(-97.9, -18.41) * mm});
            skLineSegment(sketch, "E699", {"start": v(-97.9, -18.41) * mm, "end": v(-98.04, -18.38) * mm});
            skLineSegment(sketch, "E700", {"start": v(-98.04, -18.38) * mm, "end": v(-98.17, -18.35) * mm});
            skLineSegment(sketch, "E701", {"start": v(-98.17, -18.35) * mm, "end": v(-98.9, -18.25) * mm});
            skLineSegment(sketch, "E702", {"start": v(-98.9, -18.25) * mm, "end": v(-99.6, -18.1) * mm});
            skLineSegment(sketch, "E703", {"start": v(-99.6, -18.1) * mm, "end": v(-100.29, -17.94) * mm});
            skLineSegment(sketch, "E704", {"start": v(-100.29, -17.94) * mm, "end": v(-100.96, -17.74) * mm});
            skLineSegment(sketch, "E705", {"start": v(-100.96, -17.74) * mm, "end": v(-101.63, -17.52) * mm});
            skLineSegment(sketch, "E706", {"start": v(-101.63, -17.52) * mm, "end": v(-102.27, -17.26) * mm});
            skLineSegment(sketch, "E707", {"start": v(-102.27, -17.26) * mm, "end": v(-102.9, -16.97) * mm});
            skLineSegment(sketch, "E708", {"start": v(-102.9, -16.97) * mm, "end": v(-103.52, -16.66) * mm});
            skLineSegment(sketch, "E709", {"start": v(-103.52, -16.66) * mm, "end": v(-104.12, -16.31) * mm});
            skLineSegment(sketch, "E710", {"start": v(-104.12, -16.31) * mm, "end": v(-104.7, -15.94) * mm});
            skLineSegment(sketch, "E711", {"start": v(-104.7, -15.94) * mm, "end": v(-105.28, -15.53) * mm});
            skLineSegment(sketch, "E712", {"start": v(-105.28, -15.53) * mm, "end": v(-105.84, -15.1) * mm});
            skLineSegment(sketch, "E713", {"start": v(-105.84, -15.1) * mm, "end": v(-106.38, -14.63) * mm});
            skLineSegment(sketch, "E714", {"start": v(-106.38, -14.63) * mm, "end": v(-106.9, -14.14) * mm});
            skLineSegment(sketch, "E715", {"start": v(-106.9, -14.14) * mm, "end": v(-107.4, -13.62) * mm});
            skLineSegment(sketch, "E716", {"start": v(-107.4, -13.62) * mm, "end": v(-107.9, -13.07) * mm});
            skLineSegment(sketch, "E717", {"start": v(-107.9, -13.07) * mm, "end": v(-108.37, -12.5) * mm});
            skLineSegment(sketch, "E718", {"start": v(-108.37, -12.5) * mm, "end": v(-108.8, -11.91) * mm});
            skLineSegment(sketch, "E719", {"start": v(-108.8, -11.91) * mm, "end": v(-109.22, -11.32) * mm});
            skLineSegment(sketch, "E720", {"start": v(-109.22, -11.32) * mm, "end": v(-109.6, -10.71) * mm});
            skLineSegment(sketch, "E721", {"start": v(-109.6, -10.71) * mm, "end": v(-109.95, -10.1) * mm});
            skLineSegment(sketch, "E722", {"start": v(-109.95, -10.1) * mm, "end": v(-110.27, -9.47) * mm});
            skLineSegment(sketch, "E723", {"start": v(-110.27, -9.47) * mm, "end": v(-110.55, -8.83) * mm});
            skLineSegment(sketch, "E724", {"start": v(-110.55, -8.83) * mm, "end": v(-110.81, -8.18) * mm});
            skLineSegment(sketch, "E725", {"start": v(-110.81, -8.18) * mm, "end": v(-111.04, -7.52) * mm});
            skLineSegment(sketch, "E726", {"start": v(-111.04, -7.52) * mm, "end": v(-111.24, -6.85) * mm});
            skLineSegment(sketch, "E727", {"start": v(-111.24, -6.85) * mm, "end": v(-111.4, -6.17) * mm});
            skLineSegment(sketch, "E728", {"start": v(-111.4, -6.17) * mm, "end": v(-111.55, -5.49) * mm});
            skLineSegment(sketch, "E729", {"start": v(-111.55, -5.49) * mm, "end": v(-111.65, -4.79) * mm});
            skLineSegment(sketch, "E730", {"start": v(-111.65, -4.79) * mm, "end": v(-111.73, -4.08) * mm});
            skLineSegment(sketch, "E731", {"start": v(-111.73, -4.08) * mm, "end": v(-111.78, -3.36) * mm});
            skLineSegment(sketch, "E732", {"start": v(-111.78, -3.36) * mm, "end": v(-111.8, -2.63) * mm});
            skLineSegment(sketch, "E733", {"start": v(-111.8, -2.63) * mm, "end": v(-111.77, -1.81) * mm});
            skLineSegment(sketch, "E734", {"start": v(-111.77, -1.81) * mm, "end": v(-111.72, -1) * mm});
            skLineSegment(sketch, "E735", {"start": v(-111.72, -1) * mm, "end": v(-111.63, -0.22) * mm});
            skLineSegment(sketch, "E736", {"start": v(-111.63, -0.22) * mm, "end": v(-111.5, 0.55) * mm});
            skLineSegment(sketch, "E737", {"start": v(-111.5, 0.55) * mm, "end": v(-111.34, 1.31) * mm});
            skLineSegment(sketch, "E738", {"start": v(-111.34, 1.31) * mm, "end": v(-111.14, 2.06) * mm});
            skLineSegment(sketch, "E739", {"start": v(-111.14, 2.06) * mm, "end": v(-110.9, 2.79) * mm});
            skLineSegment(sketch, "E740", {"start": v(-110.9, 2.79) * mm, "end": v(-110.63, 3.5) * mm});
            skLineSegment(sketch, "E741", {"start": v(-110.63, 3.5) * mm, "end": v(-110.32, 4.2) * mm});
            skLineSegment(sketch, "E742", {"start": v(-110.32, 4.2) * mm, "end": v(-109.98, 4.88) * mm});
            skLineSegment(sketch, "E743", {"start": v(-109.98, 4.88) * mm, "end": v(-109.6, 5.55) * mm});
            skLineSegment(sketch, "E744", {"start": v(-109.6, 5.55) * mm, "end": v(-109.18, 6.2) * mm});
            skLineSegment(sketch, "E745", {"start": v(-109.18, 6.2) * mm, "end": v(-108.73, 6.84) * mm});
            skLineSegment(sketch, "E746", {"start": v(-108.73, 6.84) * mm, "end": v(-108.24, 7.46) * mm});
            skLineSegment(sketch, "E747", {"start": v(-108.24, 7.46) * mm, "end": v(-107.72, 8.06) * mm});
            skLineSegment(sketch, "E748", {"start": v(-107.72, 8.06) * mm, "end": v(-107.16, 8.65) * mm});
            skLineSegment(sketch, "E749", {"start": v(-107.16, 8.65) * mm, "end": v(-106.58, 9.21) * mm});
            skLineSegment(sketch, "E750", {"start": v(-106.58, 9.21) * mm, "end": v(-105.98, 9.74) * mm});
            skLineSegment(sketch, "E751", {"start": v(-105.98, 9.74) * mm, "end": v(-105.36, 10.23) * mm});
            skLineSegment(sketch, "E752", {"start": v(-105.36, 10.23) * mm, "end": v(-104.73, 10.68) * mm});
            skLineSegment(sketch, "E753", {"start": v(-104.73, 10.68) * mm, "end": v(-104.08, 11.1) * mm});
            skLineSegment(sketch, "E754", {"start": v(-104.08, 11.1) * mm, "end": v(-103.41, 11.48) * mm});
            skLineSegment(sketch, "E755", {"start": v(-103.41, 11.48) * mm, "end": v(-102.73, 11.83) * mm});
            skLineSegment(sketch, "E756", {"start": v(-102.73, 11.83) * mm, "end": v(-102.03, 12.14) * mm});
            skLineSegment(sketch, "E757", {"start": v(-102.03, 12.14) * mm, "end": v(-101.32, 12.4) * mm});
            skLineSegment(sketch, "E758", {"start": v(-101.32, 12.4) * mm, "end": v(-100.6, 12.65) * mm});
            skLineSegment(sketch, "E759", {"start": v(-100.6, 12.65) * mm, "end": v(-99.85, 12.85) * mm});
            skLineSegment(sketch, "E760", {"start": v(-99.85, 12.85) * mm, "end": v(-99.1, 13.01) * mm});
            skLineSegment(sketch, "E761", {"start": v(-99.1, 13.01) * mm, "end": v(-98.32, 13.14) * mm});
            skLineSegment(sketch, "E762", {"start": v(-98.32, 13.14) * mm, "end": v(-97.53, 13.23) * mm});
            skLineSegment(sketch, "E763", {"start": v(-97.53, 13.23) * mm, "end": v(-96.73, 13.29) * mm});
            skLineSegment(sketch, "E764", {"start": v(-96.73, 13.29) * mm, "end": v(-95.91, 13.3) * mm});
            skLineSegment(sketch, "E765", {"start": v(-95.91, 13.3) * mm, "end": v(-95.09, 13.29) * mm});
            skLineSegment(sketch, "E766", {"start": v(-95.09, 13.29) * mm, "end": v(-94.28, 13.23) * mm});
            skLineSegment(sketch, "E767", {"start": v(-94.28, 13.23) * mm, "end": v(-93.48, 13.14) * mm});
            skLineSegment(sketch, "E768", {"start": v(-93.48, 13.14) * mm, "end": v(-92.7, 13.01) * mm});
            skLineSegment(sketch, "E769", {"start": v(-92.7, 13.01) * mm, "end": v(-91.94, 12.85) * mm});
            skLineSegment(sketch, "E770", {"start": v(-91.94, 12.85) * mm, "end": v(-91.2, 12.65) * mm});
            skLineSegment(sketch, "E771", {"start": v(-91.2, 12.65) * mm, "end": v(-90.46, 12.41) * mm});
            skLineSegment(sketch, "E772", {"start": v(-90.46, 12.41) * mm, "end": v(-89.75, 12.14) * mm});
            skLineSegment(sketch, "E773", {"start": v(-89.75, 12.14) * mm, "end": v(-89.05, 11.83) * mm});
            skLineSegment(sketch, "E774", {"start": v(-89.05, 11.83) * mm, "end": v(-88.36, 11.5) * mm});
            skLineSegment(sketch, "E775", {"start": v(-88.36, 11.5) * mm, "end": v(-87.7, 11.11) * mm});
            skLineSegment(sketch, "E776", {"start": v(-87.7, 11.11) * mm, "end": v(-87.04, 10.7) * mm});
            skLineSegment(sketch, "E777", {"start": v(-87.04, 10.7) * mm, "end": v(-86.4, 10.24) * mm});
            skLineSegment(sketch, "E778", {"start": v(-86.4, 10.24) * mm, "end": v(-85.8, 9.76) * mm});
            skLineSegment(sketch, "E779", {"start": v(-85.8, 9.76) * mm, "end": v(-85.19, 9.24) * mm});
            skLineSegment(sketch, "E780", {"start": v(-85.19, 9.24) * mm, "end": v(-84.6, 8.68) * mm});
            skLineSegment(sketch, "E781", {"start": v(-84.6, 8.68) * mm, "end": v(-84.05, 8.1) * mm});
            skLineSegment(sketch, "E782", {"start": v(-84.05, 8.1) * mm, "end": v(-83.52, 7.5) * mm});
            skLineSegment(sketch, "E783", {"start": v(-83.52, 7.5) * mm, "end": v(-83.04, 6.87) * mm});
            skLineSegment(sketch, "E784", {"start": v(-83.04, 6.87) * mm, "end": v(-82.59, 6.24) * mm});
            skLineSegment(sketch, "E785", {"start": v(-82.59, 6.24) * mm, "end": v(-82.17, 5.59) * mm});
            skLineSegment(sketch, "E786", {"start": v(-82.17, 5.59) * mm, "end": v(-81.8, 4.92) * mm});
            skLineSegment(sketch, "E787", {"start": v(-81.8, 4.92) * mm, "end": v(-81.45, 4.23) * mm});
            skLineSegment(sketch, "E788", {"start": v(-81.45, 4.23) * mm, "end": v(-81.14, 3.53) * mm});
            skLineSegment(sketch, "E789", {"start": v(-81.14, 3.53) * mm, "end": v(-80.87, 2.82) * mm});
            skLineSegment(sketch, "E790", {"start": v(-80.87, 2.82) * mm, "end": v(-80.63, 2.09) * mm});
            skLineSegment(sketch, "E791", {"start": v(-80.63, 2.09) * mm, "end": v(-80.43, 1.34) * mm});
            skLineSegment(sketch, "E792", {"start": v(-80.43, 1.34) * mm, "end": v(-80.27, 0.57) * mm});
            skLineSegment(sketch, "E793", {"start": v(-80.27, 0.57) * mm, "end": v(-80.14, -0.2) * mm});
            skLineSegment(sketch, "E794", {"start": v(-80.14, -0.2) * mm, "end": v(-80.05, -1) * mm});
            skLineSegment(sketch, "E795", {"start": v(-80.05, -1) * mm, "end": v(-80, -1.8) * mm});
            skLineSegment(sketch, "E796", {"start": v(-80, -1.8) * mm, "end": v(-79.98, -2.63) * mm});
            skLineSegment(sketch, "E797", {"start": v(-79.98, -2.63) * mm, "end": v(-80, -3.36) * mm});
            skLineSegment(sketch, "E798", {"start": v(-80, -3.36) * mm, "end": v(-80.04, -4.08) * mm});
            skLineSegment(sketch, "E799", {"start": v(-80.04, -4.08) * mm, "end": v(-80.12, -4.79) * mm});
            skLineSegment(sketch, "E800", {"start": v(-80.12, -4.79) * mm, "end": v(-80.22, -5.48) * mm});
            skLineSegment(sketch, "E801", {"start": v(-80.22, -5.48) * mm, "end": v(-80.36, -6.17) * mm});
            skLineSegment(sketch, "E802", {"start": v(-80.36, -6.17) * mm, "end": v(-80.53, -6.85) * mm});
            skLineSegment(sketch, "E803", {"start": v(-80.53, -6.85) * mm, "end": v(-80.73, -7.52) * mm});
            skLineSegment(sketch, "E804", {"start": v(-80.73, -7.52) * mm, "end": v(-80.96, -8.18) * mm});
            skLineSegment(sketch, "E805", {"start": v(-80.96, -8.18) * mm, "end": v(-81.22, -8.83) * mm});
            skLineSegment(sketch, "E806", {"start": v(-81.22, -8.83) * mm, "end": v(-81.5, -9.47) * mm});
            skLineSegment(sketch, "E807", {"start": v(-81.5, -9.47) * mm, "end": v(-81.83, -10.1) * mm});
            skLineSegment(sketch, "E808", {"start": v(-81.83, -10.1) * mm, "end": v(-82.18, -10.71) * mm});
            skLineSegment(sketch, "E809", {"start": v(-82.18, -10.71) * mm, "end": v(-82.56, -11.32) * mm});
            skLineSegment(sketch, "E810", {"start": v(-82.56, -11.32) * mm, "end": v(-82.97, -11.91) * mm});
            skLineSegment(sketch, "E811", {"start": v(-82.97, -11.91) * mm, "end": v(-83.41, -12.5) * mm});
            skLineSegment(sketch, "E812", {"start": v(-83.41, -12.5) * mm, "end": v(-83.88, -13.07) * mm});
            skLineSegment(sketch, "E813", {"start": v(-83.88, -13.07) * mm, "end": v(-84.38, -13.62) * mm});
            skLineSegment(sketch, "E814", {"start": v(-84.38, -13.62) * mm, "end": v(-84.89, -14.14) * mm});
            skLineSegment(sketch, "E815", {"start": v(-84.89, -14.14) * mm, "end": v(-85.41, -14.63) * mm});
            skLineSegment(sketch, "E816", {"start": v(-85.41, -14.63) * mm, "end": v(-85.95, -15.1) * mm});
            skLineSegment(sketch, "E817", {"start": v(-85.95, -15.1) * mm, "end": v(-86.51, -15.53) * mm});
            skLineSegment(sketch, "E818", {"start": v(-86.51, -15.53) * mm, "end": v(-87.09, -15.94) * mm});
            skLineSegment(sketch, "E819", {"start": v(-87.09, -15.94) * mm, "end": v(-87.67, -16.31) * mm});
            skLineSegment(sketch, "E820", {"start": v(-87.67, -16.31) * mm, "end": v(-88.28, -16.66) * mm});
            skLineSegment(sketch, "E821", {"start": v(-88.28, -16.66) * mm, "end": v(-88.9, -16.97) * mm});
            skLineSegment(sketch, "E822", {"start": v(-88.9, -16.97) * mm, "end": v(-89.53, -17.26) * mm});
            skLineSegment(sketch, "E823", {"start": v(-89.53, -17.26) * mm, "end": v(-90.18, -17.52) * mm});
            skLineSegment(sketch, "E824", {"start": v(-90.18, -17.52) * mm, "end": v(-90.85, -17.74) * mm});
            skLineSegment(sketch, "E825", {"start": v(-90.85, -17.74) * mm, "end": v(-91.52, -17.94) * mm});
            skLineSegment(sketch, "E826", {"start": v(-91.52, -17.94) * mm, "end": v(-92.22, -18.1) * mm});
            skLineSegment(sketch, "E827", {"start": v(-92.22, -18.1) * mm, "end": v(-92.93, -18.25) * mm});
            skLineSegment(sketch, "E828", {"start": v(-92.93, -18.25) * mm, "end": v(-93.65, -18.35) * mm});
            skLineSegment(sketch, "E829", {"start": v(-93.65, -18.35) * mm, "end": v(-93.78, -18.38) * mm});
            skLineSegment(sketch, "E830", {"start": v(-93.78, -18.38) * mm, "end": v(-93.92, -18.41) * mm});
            skLineSegment(sketch, "E831", {"start": v(-93.92, -18.41) * mm, "end": v(-94.04, -18.46) * mm});
            skLineSegment(sketch, "E832", {"start": v(-94.04, -18.46) * mm, "end": v(-94.17, -18.52) * mm});
            skLineSegment(sketch, "E833", {"start": v(-94.17, -18.52) * mm, "end": v(-94.28, -18.59) * mm});
            skLineSegment(sketch, "E834", {"start": v(-94.28, -18.59) * mm, "end": v(-94.39, -18.67) * mm});
            skLineSegment(sketch, "E835", {"start": v(-94.39, -18.67) * mm, "end": v(-94.49, -18.75) * mm});
            skLineSegment(sketch, "E836", {"start": v(-94.49, -18.75) * mm, "end": v(-94.58, -18.85) * mm});
            skLineSegment(sketch, "E837", {"start": v(-94.58, -18.85) * mm, "end": v(-94.66, -18.95) * mm});
            skLineSegment(sketch, "E838", {"start": v(-94.66, -18.95) * mm, "end": v(-94.74, -19.06) * mm});
            skLineSegment(sketch, "E839", {"start": v(-94.74, -19.06) * mm, "end": v(-94.8, -19.18) * mm});
            skLineSegment(sketch, "E840", {"start": v(-94.8, -19.18) * mm, "end": v(-94.85, -19.3) * mm});
            skLineSegment(sketch, "E841", {"start": v(-94.85, -19.3) * mm, "end": v(-94.9, -19.43) * mm});
            skLineSegment(sketch, "E842", {"start": v(-94.9, -19.43) * mm, "end": v(-94.93, -19.56) * mm});
            skLineSegment(sketch, "E843", {"start": v(-94.93, -19.56) * mm, "end": v(-94.95, -19.7) * mm});
            skLineSegment(sketch, "E844", {"start": v(-94.95, -19.7) * mm, "end": v(-94.95, -19.84) * mm});
            skLineSegment(sketch, "E845", {"start": v(-94.95, -19.84) * mm, "end": v(-94.95, -23.36) * mm});
            skLineSegment(sketch, "E846", {"start": v(-94.95, -23.36) * mm, "end": v(-94.94, -23.68) * mm});
            skLineSegment(sketch, "E847", {"start": v(-94.94, -23.68) * mm, "end": v(-94.89, -23.99) * mm});
            skLineSegment(sketch, "E848", {"start": v(-94.89, -23.99) * mm, "end": v(-94.81, -24.29) * mm});
            skLineSegment(sketch, "E849", {"start": v(-94.81, -24.29) * mm, "end": v(-94.7, -24.57) * mm});
            skLineSegment(sketch, "E850", {"start": v(-94.7, -24.57) * mm, "end": v(-94.57, -24.85) * mm});
            skLineSegment(sketch, "E851", {"start": v(-94.57, -24.85) * mm, "end": v(-94.42, -25.1) * mm});
            skLineSegment(sketch, "E852", {"start": v(-94.42, -25.1) * mm, "end": v(-94.24, -25.35) * mm});
            skLineSegment(sketch, "E853", {"start": v(-94.24, -25.35) * mm, "end": v(-94.03, -25.57) * mm});
            skLineSegment(sketch, "E854", {"start": v(-94.03, -25.57) * mm, "end": v(-93.81, -25.77) * mm});
            skLineSegment(sketch, "E855", {"start": v(-93.81, -25.77) * mm, "end": v(-93.57, -25.95) * mm});
            skLineSegment(sketch, "E856", {"start": v(-93.57, -25.95) * mm, "end": v(-93.31, -26.11) * mm});
            skLineSegment(sketch, "E857", {"start": v(-93.31, -26.11) * mm, "end": v(-93.04, -26.24) * mm});
            skLineSegment(sketch, "E858", {"start": v(-93.04, -26.24) * mm, "end": v(-92.75, -26.35) * mm});
            skLineSegment(sketch, "E859", {"start": v(-92.75, -26.35) * mm, "end": v(-92.45, -26.42) * mm});
            skLineSegment(sketch, "E860", {"start": v(-92.45, -26.42) * mm, "end": v(-92.14, -26.47) * mm});
            skLineSegment(sketch, "E861", {"start": v(-92.14, -26.47) * mm, "end": v(-91.82, -26.49) * mm});
            skLineSegment(sketch, "E862", {"start": v(-91.82, -26.49) * mm, "end": v(-73.1, -26.44) * mm});
            skLineSegment(sketch, "E863", {"start": v(-73.1, -26.44) * mm, "end": v(-72.89, -26.43) * mm});
            skLineSegment(sketch, "E864", {"start": v(-72.89, -26.43) * mm, "end": v(-72.68, -26.42) * mm});
            skLineSegment(sketch, "E865", {"start": v(-72.68, -26.42) * mm, "end": v(-72.48, -26.4) * mm});
            skLineSegment(sketch, "E866", {"start": v(-72.48, -26.4) * mm, "end": v(-72.28, -26.37) * mm});
            skLineSegment(sketch, "E867", {"start": v(-72.28, -26.37) * mm, "end": v(-72.08, -26.33) * mm});
            skLineSegment(sketch, "E868", {"start": v(-72.08, -26.33) * mm, "end": v(-71.9, -26.28) * mm});
            skLineSegment(sketch, "E869", {"start": v(-71.9, -26.28) * mm, "end": v(-71.71, -26.22) * mm});
            skLineSegment(sketch, "E870", {"start": v(-71.71, -26.22) * mm, "end": v(-71.53, -26.16) * mm});
            skLineSegment(sketch, "E871", {"start": v(-71.53, -26.16) * mm, "end": v(-71.36, -26.08) * mm});
            skLineSegment(sketch, "E872", {"start": v(-71.36, -26.08) * mm, "end": v(-71.19, -26) * mm});
            skLineSegment(sketch, "E873", {"start": v(-71.19, -26) * mm, "end": v(-71.02, -25.9) * mm});
            skLineSegment(sketch, "E874", {"start": v(-71.02, -25.9) * mm, "end": v(-70.86, -25.8) * mm});
            skLineSegment(sketch, "E875", {"start": v(-70.86, -25.8) * mm, "end": v(-70.71, -25.7) * mm});
            skLineSegment(sketch, "E876", {"start": v(-70.71, -25.7) * mm, "end": v(-70.56, -25.58) * mm});
            skLineSegment(sketch, "E877", {"start": v(-70.56, -25.58) * mm, "end": v(-70.42, -25.46) * mm});
            skLineSegment(sketch, "E878", {"start": v(-70.42, -25.46) * mm, "end": v(-70.28, -25.32) * mm});
            skLineSegment(sketch, "E879", {"start": v(-70.28, -25.32) * mm, "end": v(-70.15, -25.18) * mm});
            skLineSegment(sketch, "E880", {"start": v(-70.15, -25.18) * mm, "end": v(-70.03, -25.03) * mm});
            skLineSegment(sketch, "E881", {"start": v(-70.03, -25.03) * mm, "end": v(-69.91, -24.88) * mm});
            skLineSegment(sketch, "E882", {"start": v(-69.91, -24.88) * mm, "end": v(-69.8, -24.73) * mm});
            skLineSegment(sketch, "E883", {"start": v(-69.8, -24.73) * mm, "end": v(-69.7, -24.56) * mm});
            skLineSegment(sketch, "E884", {"start": v(-69.7, -24.56) * mm, "end": v(-69.62, -24.4) * mm});
            skLineSegment(sketch, "E885", {"start": v(-69.62, -24.4) * mm, "end": v(-69.54, -24.23) * mm});
            skLineSegment(sketch, "E886", {"start": v(-69.54, -24.23) * mm, "end": v(-69.47, -24.05) * mm});
            skLineSegment(sketch, "E887", {"start": v(-69.47, -24.05) * mm, "end": v(-69.4, -23.87) * mm});
            skLineSegment(sketch, "E888", {"start": v(-69.4, -23.87) * mm, "end": v(-69.35, -23.69) * mm});
            skLineSegment(sketch, "E889", {"start": v(-69.35, -23.69) * mm, "end": v(-69.3, -23.5) * mm});
            skLineSegment(sketch, "E890", {"start": v(-69.3, -23.5) * mm, "end": v(-69.26, -23.3) * mm});
            skLineSegment(sketch, "E891", {"start": v(-69.26, -23.3) * mm, "end": v(-69.23, -23.1) * mm});
            skLineSegment(sketch, "E892", {"start": v(-69.23, -23.1) * mm, "end": v(-69.21, -22.9) * mm});
            skLineSegment(sketch, "E893", {"start": v(-69.21, -22.9) * mm, "end": v(-69.2, -22.69) * mm});
            skLineSegment(sketch, "E894", {"start": v(-69.2, -22.69) * mm, "end": v(-69.2, -22.47) * mm});
            skLineSegment(sketch, "E895", {"start": v(-69.2, -22.47) * mm, "end": v(-69.2, 6.62) * mm});
            skLineSegment(sketch, "E896", {"start": v(-69.2, 6.62) * mm, "end": v(-69.2, 6.66) * mm});
            skLineSegment(sketch, "E897", {"start": v(-69.2, 6.66) * mm, "end": v(-69.18, 6.7) * mm});
            skLineSegment(sketch, "E898", {"start": v(-69.18, 6.7) * mm, "end": v(-69.17, 6.74) * mm});
            skLineSegment(sketch, "E899", {"start": v(-69.17, 6.74) * mm, "end": v(-69.16, 6.78) * mm});
            skLineSegment(sketch, "E900", {"start": v(-69.16, 6.78) * mm, "end": v(-69.14, 6.81) * mm});
            skLineSegment(sketch, "E901", {"start": v(-69.14, 6.81) * mm, "end": v(-69.12, 6.84) * mm});
            skLineSegment(sketch, "E902", {"start": v(-69.12, 6.84) * mm, "end": v(-69.1, 6.87) * mm});
            skLineSegment(sketch, "E903", {"start": v(-69.1, 6.87) * mm, "end": v(-69.07, 6.9) * mm});
            skLineSegment(sketch, "E904", {"start": v(-69.07, 6.9) * mm, "end": v(-69.05, 6.92) * mm});
            skLineSegment(sketch, "E905", {"start": v(-69.05, 6.92) * mm, "end": v(-69.02, 6.93) * mm});
            skLineSegment(sketch, "E906", {"start": v(-69.02, 6.93) * mm, "end": v(-68.99, 6.95) * mm});
            skLineSegment(sketch, "E907", {"start": v(-68.99, 6.95) * mm, "end": v(-68.95, 6.96) * mm});
            skLineSegment(sketch, "E908", {"start": v(-68.95, 6.96) * mm, "end": v(-68.92, 6.98) * mm});
            skLineSegment(sketch, "E909", {"start": v(-68.92, 6.98) * mm, "end": v(-68.89, 6.98) * mm});
            skLineSegment(sketch, "E910", {"start": v(-68.89, 6.98) * mm, "end": v(-68.85, 6.99) * mm});
            skLineSegment(sketch, "E911", {"start": v(-68.85, 6.99) * mm, "end": v(-68.82, 6.99) * mm});
            skLineSegment(sketch, "E912", {"start": v(-68.82, 6.99) * mm, "end": v(-68.8, 6.99) * mm});
            skLineSegment(sketch, "E913", {"start": v(-68.8, 6.99) * mm, "end": v(-68.77, 6.99) * mm});
            skLineSegment(sketch, "E914", {"start": v(-68.77, 6.99) * mm, "end": v(-68.74, 6.98) * mm});
            skLineSegment(sketch, "E915", {"start": v(-68.74, 6.98) * mm, "end": v(-68.72, 6.97) * mm});
            skLineSegment(sketch, "E916", {"start": v(-68.72, 6.97) * mm, "end": v(-68.7, 6.97) * mm});
            skLineSegment(sketch, "E917", {"start": v(-68.7, 6.97) * mm, "end": v(-68.67, 6.96) * mm});
            skLineSegment(sketch, "E918", {"start": v(-68.67, 6.96) * mm, "end": v(-68.65, 6.95) * mm});
            skLineSegment(sketch, "E919", {"start": v(-68.65, 6.95) * mm, "end": v(-68.63, 6.94) * mm});
            skLineSegment(sketch, "E920", {"start": v(-68.63, 6.94) * mm, "end": v(-68.6, 6.92) * mm});
            skLineSegment(sketch, "E921", {"start": v(-68.6, 6.92) * mm, "end": v(-68.6, 6.9) * mm});
            skLineSegment(sketch, "E922", {"start": v(-68.6, 6.9) * mm, "end": v(-68.57, 6.89) * mm});
            skLineSegment(sketch, "E923", {"start": v(-68.57, 6.89) * mm, "end": v(-68.55, 6.87) * mm});
            skLineSegment(sketch, "E924", {"start": v(-68.55, 6.87) * mm, "end": v(-68.54, 6.85) * mm});
            skLineSegment(sketch, "E925", {"start": v(-68.54, 6.85) * mm, "end": v(-68.52, 6.83) * mm});
            skLineSegment(sketch, "E926", {"start": v(-68.52, 6.83) * mm, "end": v(-68.5, 6.8) * mm});
            skLineSegment(sketch, "E927", {"start": v(-68.5, 6.8) * mm, "end": v(-68.5, 6.79) * mm});
            skLineSegment(sketch, "E928", {"start": v(-68.5, 6.79) * mm, "end": v(-52.2, -25.59) * mm});
            skLineSegment(sketch, "E929", {"start": v(-52.2, -25.59) * mm, "end": v(-52.14, -25.69) * mm});
            skLineSegment(sketch, "E930", {"start": v(-52.14, -25.69) * mm, "end": v(-52.08, -25.78) * mm});
            skLineSegment(sketch, "E931", {"start": v(-52.08, -25.78) * mm, "end": v(-52, -25.88) * mm});
            skLineSegment(sketch, "E932", {"start": v(-52, -25.88) * mm, "end": v(-51.93, -25.96) * mm});
            skLineSegment(sketch, "E933", {"start": v(-51.93, -25.96) * mm, "end": v(-51.86, -26.04) * mm});
            skLineSegment(sketch, "E934", {"start": v(-51.86, -26.04) * mm, "end": v(-51.77, -26.12) * mm});
            skLineSegment(sketch, "E935", {"start": v(-51.77, -26.12) * mm, "end": v(-51.68, -26.18) * mm});
            skLineSegment(sketch, "E936", {"start": v(-51.68, -26.18) * mm, "end": v(-51.6, -26.25) * mm});
            skLineSegment(sketch, "E937", {"start": v(-51.6, -26.25) * mm, "end": v(-51.5, -26.3) * mm});
            skLineSegment(sketch, "E938", {"start": v(-51.5, -26.3) * mm, "end": v(-51.4, -26.35) * mm});
            skLineSegment(sketch, "E939", {"start": v(-51.4, -26.35) * mm, "end": v(-51.29, -26.4) * mm});
            skLineSegment(sketch, "E940", {"start": v(-51.29, -26.4) * mm, "end": v(-51.18, -26.43) * mm});
            skLineSegment(sketch, "E941", {"start": v(-51.18, -26.43) * mm, "end": v(-51.07, -26.45) * mm});
            skLineSegment(sketch, "E942", {"start": v(-51.07, -26.45) * mm, "end": v(-50.96, -26.47) * mm});
            skLineSegment(sketch, "E943", {"start": v(-50.96, -26.47) * mm, "end": v(-50.85, -26.48) * mm});
            skLineSegment(sketch, "E944", {"start": v(-50.85, -26.48) * mm, "end": v(-50.73, -26.49) * mm});
            skLineSegment(sketch, "E945", {"start": v(-50.73, -26.49) * mm, "end": v(-50.6, -26.48) * mm});
            skLineSegment(sketch, "E946", {"start": v(-50.6, -26.48) * mm, "end": v(-50.46, -26.46) * mm});
            skLineSegment(sketch, "E947", {"start": v(-50.46, -26.46) * mm, "end": v(-50.34, -26.43) * mm});
            skLineSegment(sketch, "E948", {"start": v(-50.34, -26.43) * mm, "end": v(-50.21, -26.38) * mm});
            skLineSegment(sketch, "E949", {"start": v(-50.21, -26.38) * mm, "end": v(-50.1, -26.33) * mm});
            skLineSegment(sketch, "E950", {"start": v(-50.1, -26.33) * mm, "end": v(-49.99, -26.26) * mm});
            skLineSegment(sketch, "E951", {"start": v(-49.99, -26.26) * mm, "end": v(-49.89, -26.19) * mm});
            skLineSegment(sketch, "E952", {"start": v(-49.89, -26.19) * mm, "end": v(-49.8, -26.1) * mm});
            skLineSegment(sketch, "E953", {"start": v(-49.8, -26.1) * mm, "end": v(-49.7, -26) * mm});
            skLineSegment(sketch, "E954", {"start": v(-49.7, -26) * mm, "end": v(-49.63, -25.9) * mm});
            skLineSegment(sketch, "E955", {"start": v(-49.63, -25.9) * mm, "end": v(-49.56, -25.8) * mm});
            skLineSegment(sketch, "E956", {"start": v(-49.56, -25.8) * mm, "end": v(-49.5, -25.68) * mm});
            skLineSegment(sketch, "E957", {"start": v(-49.5, -25.68) * mm, "end": v(-49.46, -25.56) * mm});
            skLineSegment(sketch, "E958", {"start": v(-49.46, -25.56) * mm, "end": v(-49.43, -25.43) * mm});
            skLineSegment(sketch, "E959", {"start": v(-49.43, -25.43) * mm, "end": v(-49.4, -25.3) * mm});
            skLineSegment(sketch, "E960", {"start": v(-49.4, -25.3) * mm, "end": v(-49.4, -25.16) * mm});
            skLineSegment(sketch, "E961", {"start": v(-49.4, -25.16) * mm, "end": v(-49.4, 11.98) * mm});
            skLineSegment(sketch, "E962", {"start": v(-49.4, 11.98) * mm, "end": v(-49.4, 12.1) * mm});
            skLineSegment(sketch, "E963", {"start": v(-49.4, 12.1) * mm, "end": v(-49.39, 12.22) * mm});
            skLineSegment(sketch, "E964", {"start": v(-49.39, 12.22) * mm, "end": v(-49.37, 12.33) * mm});
            skLineSegment(sketch, "E965", {"start": v(-49.37, 12.33) * mm, "end": v(-49.35, 12.43) * mm});
            skLineSegment(sketch, "E966", {"start": v(-49.35, 12.43) * mm, "end": v(-49.31, 12.52) * mm});
            skLineSegment(sketch, "E967", {"start": v(-49.31, 12.52) * mm, "end": v(-49.28, 12.6) * mm});
            skLineSegment(sketch, "E968", {"start": v(-49.28, 12.6) * mm, "end": v(-49.23, 12.67) * mm});
            skLineSegment(sketch, "E969", {"start": v(-49.23, 12.67) * mm, "end": v(-49.17, 12.74) * mm});
            skLineSegment(sketch, "E970", {"start": v(-49.17, 12.74) * mm, "end": v(-49.11, 12.8) * mm});
            skLineSegment(sketch, "E971", {"start": v(-49.11, 12.8) * mm, "end": v(-49.04, 12.85) * mm});
            skLineSegment(sketch, "E972", {"start": v(-49.04, 12.85) * mm, "end": v(-48.97, 12.9) * mm});
            skLineSegment(sketch, "E973", {"start": v(-48.97, 12.9) * mm, "end": v(-48.88, 12.93) * mm});
            skLineSegment(sketch, "E974", {"start": v(-48.88, 12.93) * mm, "end": v(-48.8, 12.95) * mm});
            skLineSegment(sketch, "E975", {"start": v(-48.8, 12.95) * mm, "end": v(-48.7, 12.97) * mm});
            skLineSegment(sketch, "E976", {"start": v(-48.7, 12.97) * mm, "end": v(-48.59, 12.98) * mm});
            skLineSegment(sketch, "E977", {"start": v(-48.59, 12.98) * mm, "end": v(-48.47, 12.99) * mm});
            skLineSegment(sketch, "E978", {"start": v(-48.47, 12.99) * mm, "end": v(-48.35, 12.98) * mm});
            skLineSegment(sketch, "E979", {"start": v(-48.35, 12.98) * mm, "end": v(-48.23, 12.97) * mm});
            skLineSegment(sketch, "E980", {"start": v(-48.23, 12.97) * mm, "end": v(-48.13, 12.95) * mm});
            skLineSegment(sketch, "E981", {"start": v(-48.13, 12.95) * mm, "end": v(-48.03, 12.93) * mm});
            skLineSegment(sketch, "E982", {"start": v(-48.03, 12.93) * mm, "end": v(-47.94, 12.9) * mm});
            skLineSegment(sketch, "E983", {"start": v(-47.94, 12.9) * mm, "end": v(-47.86, 12.85) * mm});
            skLineSegment(sketch, "E984", {"start": v(-47.86, 12.85) * mm, "end": v(-47.8, 12.8) * mm});
            skLineSegment(sketch, "E985", {"start": v(-47.8, 12.8) * mm, "end": v(-47.73, 12.74) * mm});
            skLineSegment(sketch, "E986", {"start": v(-47.73, 12.74) * mm, "end": v(-47.67, 12.67) * mm});
            skLineSegment(sketch, "E987", {"start": v(-47.67, 12.67) * mm, "end": v(-47.62, 12.6) * mm});
            skLineSegment(sketch, "E988", {"start": v(-47.62, 12.6) * mm, "end": v(-47.58, 12.52) * mm});
            skLineSegment(sketch, "E989", {"start": v(-47.58, 12.52) * mm, "end": v(-47.55, 12.43) * mm});
            skLineSegment(sketch, "E990", {"start": v(-47.55, 12.43) * mm, "end": v(-47.52, 12.33) * mm});
            skLineSegment(sketch, "E991", {"start": v(-47.52, 12.33) * mm, "end": v(-47.5, 12.22) * mm});
            skLineSegment(sketch, "E992", {"start": v(-47.5, 12.22) * mm, "end": v(-47.49, 12.1) * mm});
            skLineSegment(sketch, "E993", {"start": v(-47.49, 12.1) * mm, "end": v(-47.49, 11.98) * mm});
            skLineSegment(sketch, "E994", {"start": v(-47.49, 11.98) * mm, "end": v(-47.49, -22.43) * mm});
            skLineSegment(sketch, "E995", {"start": v(-47.49, -22.43) * mm, "end": v(-47.47, -22.85) * mm});
            skLineSegment(sketch, "E996", {"start": v(-47.47, -22.85) * mm, "end": v(-47.42, -23.26) * mm});
            skLineSegment(sketch, "E997", {"start": v(-47.42, -23.26) * mm, "end": v(-47.35, -23.64) * mm});
            skLineSegment(sketch, "E998", {"start": v(-47.35, -23.64) * mm, "end": v(-47.24, -24) * mm});
            skLineSegment(sketch, "E999", {"start": v(-47.24, -24) * mm, "end": v(-47.1, -24.32) * mm});
            skLineSegment(sketch, "E1000", {"start": v(-47.1, -24.32) * mm, "end": v(-46.93, -24.63) * mm});
            skLineSegment(sketch, "E1001", {"start": v(-46.93, -24.63) * mm, "end": v(-46.73, -24.91) * mm});
            skLineSegment(sketch, "E1002", {"start": v(-46.73, -24.91) * mm, "end": v(-46.5, -25.17) * mm});
            skLineSegment(sketch, "E1003", {"start": v(-46.5, -25.17) * mm, "end": v(-46.24, -25.4) * mm});
            skLineSegment(sketch, "E1004", {"start": v(-46.24, -25.4) * mm, "end": v(-45.95, -25.62) * mm});
            skLineSegment(sketch, "E1005", {"start": v(-45.95, -25.62) * mm, "end": v(-45.63, -25.8) * mm});
            skLineSegment(sketch, "E1006", {"start": v(-45.63, -25.8) * mm, "end": v(-45.28, -25.97) * mm});
            skLineSegment(sketch, "E1007", {"start": v(-45.28, -25.97) * mm, "end": v(-44.9, -26.11) * mm});
            skLineSegment(sketch, "E1008", {"start": v(-44.9, -26.11) * mm, "end": v(-44.49, -26.23) * mm});
            skLineSegment(sketch, "E1009", {"start": v(-44.49, -26.23) * mm, "end": v(-44.04, -26.32) * mm});
            skLineSegment(sketch, "E1010", {"start": v(-44.04, -26.32) * mm, "end": v(-43.57, -26.38) * mm});
            skLineSegment(sketch, "E1011", {"start": v(-43.57, -26.38) * mm, "end": v(-40.67, -26.49) * mm});
            skLineSegment(sketch, "E1012", {"start": v(-40.67, -26.49) * mm, "end": v(-40.45, -26.48) * mm});
            skLineSegment(sketch, "E1013", {"start": v(-40.45, -26.48) * mm, "end": v(-40.24, -26.47) * mm});
            skLineSegment(sketch, "E1014", {"start": v(-40.24, -26.47) * mm, "end": v(-40.04, -26.45) * mm});
            skLineSegment(sketch, "E1015", {"start": v(-40.04, -26.45) * mm, "end": v(-39.84, -26.42) * mm});
            skLineSegment(sketch, "E1016", {"start": v(-39.84, -26.42) * mm, "end": v(-39.64, -26.38) * mm});
            skLineSegment(sketch, "E1017", {"start": v(-39.64, -26.38) * mm, "end": v(-39.45, -26.33) * mm});
            skLineSegment(sketch, "E1018", {"start": v(-39.45, -26.33) * mm, "end": v(-39.27, -26.27) * mm});
            skLineSegment(sketch, "E1019", {"start": v(-39.27, -26.27) * mm, "end": v(-39.09, -26.2) * mm});
            skLineSegment(sketch, "E1020", {"start": v(-39.09, -26.2) * mm, "end": v(-38.91, -26.13) * mm});
            skLineSegment(sketch, "E1021", {"start": v(-38.91, -26.13) * mm, "end": v(-38.74, -26.05) * mm});
            skLineSegment(sketch, "E1022", {"start": v(-38.74, -26.05) * mm, "end": v(-38.57, -25.96) * mm});
            skLineSegment(sketch, "E1023", {"start": v(-38.57, -25.96) * mm, "end": v(-38.41, -25.86) * mm});
            skLineSegment(sketch, "E1024", {"start": v(-38.41, -25.86) * mm, "end": v(-38.26, -25.75) * mm});
            skLineSegment(sketch, "E1025", {"start": v(-38.26, -25.75) * mm, "end": v(-38.1, -25.63) * mm});
            skLineSegment(sketch, "E1026", {"start": v(-38.1, -25.63) * mm, "end": v(-37.96, -25.5) * mm});
            skLineSegment(sketch, "E1027", {"start": v(-37.96, -25.5) * mm, "end": v(-37.82, -25.37) * mm});
            skLineSegment(sketch, "E1028", {"start": v(-37.82, -25.37) * mm, "end": v(-37.68, -25.23) * mm});
            skLineSegment(sketch, "E1029", {"start": v(-37.68, -25.23) * mm, "end": v(-37.56, -25.09) * mm});
            skLineSegment(sketch, "E1030", {"start": v(-37.56, -25.09) * mm, "end": v(-37.44, -24.94) * mm});
            skLineSegment(sketch, "E1031", {"start": v(-37.44, -24.94) * mm, "end": v(-37.33, -24.78) * mm});
            skLineSegment(sketch, "E1032", {"start": v(-37.33, -24.78) * mm, "end": v(-37.23, -24.62) * mm});
            skLineSegment(sketch, "E1033", {"start": v(-37.23, -24.62) * mm, "end": v(-37.14, -24.45) * mm});
            skLineSegment(sketch, "E1034", {"start": v(-37.14, -24.45) * mm, "end": v(-37.06, -24.28) * mm});
            skLineSegment(sketch, "E1035", {"start": v(-37.06, -24.28) * mm, "end": v(-36.98, -24.1) * mm});
            skLineSegment(sketch, "E1036", {"start": v(-36.98, -24.1) * mm, "end": v(-36.92, -23.92) * mm});
            skLineSegment(sketch, "E1037", {"start": v(-36.92, -23.92) * mm, "end": v(-36.86, -23.74) * mm});
            skLineSegment(sketch, "E1038", {"start": v(-36.86, -23.74) * mm, "end": v(-36.81, -23.55) * mm});
            skLineSegment(sketch, "E1039", {"start": v(-36.81, -23.55) * mm, "end": v(-36.77, -23.35) * mm});
            skLineSegment(sketch, "E1040", {"start": v(-36.77, -23.35) * mm, "end": v(-36.74, -23.15) * mm});
            skLineSegment(sketch, "E1041", {"start": v(-36.74, -23.15) * mm, "end": v(-36.72, -22.95) * mm});
            skLineSegment(sketch, "E1042", {"start": v(-36.72, -22.95) * mm, "end": v(-36.7, -22.74) * mm});
            skLineSegment(sketch, "E1043", {"start": v(-36.7, -22.74) * mm, "end": v(-36.7, -22.53) * mm});
            skLineSegment(sketch, "E1044", {"start": v(-36.7, -22.53) * mm, "end": v(-36.7, 12.27) * mm});
            skLineSegment(sketch, "E1045", {"start": v(-36.7, 12.27) * mm, "end": v(-36.7, 12.34) * mm});
            skLineSegment(sketch, "E1046", {"start": v(-36.7, 12.34) * mm, "end": v(-36.69, 12.42) * mm});
            skLineSegment(sketch, "E1047", {"start": v(-36.69, 12.42) * mm, "end": v(-36.67, 12.5) * mm});
            skLineSegment(sketch, "E1048", {"start": v(-36.67, 12.5) * mm, "end": v(-36.64, 12.57) * mm});
            skLineSegment(sketch, "E1049", {"start": v(-36.64, 12.57) * mm, "end": v(-36.6, 12.63) * mm});
            skLineSegment(sketch, "E1050", {"start": v(-36.6, 12.63) * mm, "end": v(-36.57, 12.7) * mm});
            skLineSegment(sketch, "E1051", {"start": v(-36.57, 12.7) * mm, "end": v(-36.53, 12.76) * mm});
            skLineSegment(sketch, "E1052", {"start": v(-36.53, 12.76) * mm, "end": v(-36.48, 12.81) * mm});
            skLineSegment(sketch, "E1053", {"start": v(-36.48, 12.81) * mm, "end": v(-36.42, 12.86) * mm});
            skLineSegment(sketch, "E1054", {"start": v(-36.42, 12.86) * mm, "end": v(-36.36, 12.9) * mm});
            skLineSegment(sketch, "E1055", {"start": v(-36.36, 12.9) * mm, "end": v(-36.3, 12.95) * mm});
            skLineSegment(sketch, "E1056", {"start": v(-36.3, 12.95) * mm, "end": v(-36.23, 12.98) * mm});
            skLineSegment(sketch, "E1057", {"start": v(-36.23, 12.98) * mm, "end": v(-36.16, 13) * mm});
            skLineSegment(sketch, "E1058", {"start": v(-36.16, 13) * mm, "end": v(-36.08, 13.02) * mm});
            skLineSegment(sketch, "E1059", {"start": v(-36.08, 13.02) * mm, "end": v(-36, 13.04) * mm});
            skLineSegment(sketch, "E1060", {"start": v(-36, 13.04) * mm, "end": v(-35.93, 13.04) * mm});
            skLineSegment(sketch, "E1061", {"start": v(-35.93, 13.04) * mm, "end": v(-23.09, 13.04) * mm});
            skLineSegment(sketch, "E1062", {"start": v(-23.09, 13.04) * mm, "end": v(-22.82, 13.02) * mm});
            skLineSegment(sketch, "E1063", {"start": v(-22.82, 13.02) * mm, "end": v(-22.54, 13) * mm});
            skLineSegment(sketch, "E1064", {"start": v(-22.54, 13) * mm, "end": v(-22.27, 12.97) * mm});
            skLineSegment(sketch, "E1065", {"start": v(-22.27, 12.97) * mm, "end": v(-22, 12.93) * mm});
            skLineSegment(sketch, "E1066", {"start": v(-22, 12.93) * mm, "end": v(-21.72, 12.88) * mm});
            skLineSegment(sketch, "E1067", {"start": v(-21.72, 12.88) * mm, "end": v(-21.45, 12.83) * mm});
            skLineSegment(sketch, "E1068", {"start": v(-21.45, 12.83) * mm, "end": v(-21.18, 12.76) * mm});
            skLineSegment(sketch, "E1069", {"start": v(-21.18, 12.76) * mm, "end": v(-20.9, 12.7) * mm});
            skLineSegment(sketch, "E1070", {"start": v(-20.9, 12.7) * mm, "end": v(-20.63, 12.6) * mm});
            skLineSegment(sketch, "E1071", {"start": v(-20.63, 12.6) * mm, "end": v(-20.36, 12.52) * mm});
            skLineSegment(sketch, "E1072", {"start": v(-20.36, 12.52) * mm, "end": v(-20.1, 12.42) * mm});
            skLineSegment(sketch, "E1073", {"start": v(-20.1, 12.42) * mm, "end": v(-19.82, 12.31) * mm});
            skLineSegment(sketch, "E1074", {"start": v(-19.82, 12.31) * mm, "end": v(-19.55, 12.2) * mm});
            skLineSegment(sketch, "E1075", {"start": v(-19.55, 12.2) * mm, "end": v(-19.28, 12.07) * mm});
            skLineSegment(sketch, "E1076", {"start": v(-19.28, 12.07) * mm, "end": v(-19.02, 11.94) * mm});
            skLineSegment(sketch, "E1077", {"start": v(-19.02, 11.94) * mm, "end": v(-18.53, 11.67) * mm});
            skLineSegment(sketch, "E1078", {"start": v(-18.53, 11.67) * mm, "end": v(-18.08, 11.37) * mm});
            skLineSegment(sketch, "E1079", {"start": v(-18.08, 11.37) * mm, "end": v(-17.65, 11.05) * mm});
            skLineSegment(sketch, "E1080", {"start": v(-17.65, 11.05) * mm, "end": v(-17.26, 10.7) * mm});
            skLineSegment(sketch, "E1081", {"start": v(-17.26, 10.7) * mm, "end": v(-16.9, 10.33) * mm});
            skLineSegment(sketch, "E1082", {"start": v(-16.9, 10.33) * mm, "end": v(-16.57, 9.94) * mm});
            skLineSegment(sketch, "E1083", {"start": v(-16.57, 9.94) * mm, "end": v(-16.27, 9.52) * mm});
            skLineSegment(sketch, "E1084", {"start": v(-16.27, 9.52) * mm, "end": v(-16, 9.08) * mm});
            skLineSegment(sketch, "E1085", {"start": v(-16, 9.08) * mm, "end": v(-15.77, 8.6) * mm});
            skLineSegment(sketch, "E1086", {"start": v(-15.77, 8.6) * mm, "end": v(-15.56, 8.12) * mm});
            skLineSegment(sketch, "E1087", {"start": v(-15.56, 8.12) * mm, "end": v(-15.4, 7.6) * mm});
            skLineSegment(sketch, "E1088", {"start": v(-15.4, 7.6) * mm, "end": v(-15.25, 7.06) * mm});
            skLineSegment(sketch, "E1089", {"start": v(-15.25, 7.06) * mm, "end": v(-15.14, 6.5) * mm});
            skLineSegment(sketch, "E1090", {"start": v(-15.14, 6.5) * mm, "end": v(-15.06, 5.92) * mm});
            skLineSegment(sketch, "E1091", {"start": v(-15.06, 5.92) * mm, "end": v(-15.01, 5.3) * mm});
            skLineSegment(sketch, "E1092", {"start": v(-15.01, 5.3) * mm, "end": v(-15, 4.67) * mm});
            skLineSegment(sketch, "E1093", {"start": v(-15, 4.67) * mm, "end": v(-15.01, 4.04) * mm});
            skLineSegment(sketch, "E1094", {"start": v(-15.01, 4.04) * mm, "end": v(-15.06, 3.43) * mm});
            skLineSegment(sketch, "E1095", {"start": v(-15.06, 3.43) * mm, "end": v(-15.14, 2.85) * mm});
            skLineSegment(sketch, "E1096", {"start": v(-15.14, 2.85) * mm, "end": v(-15.25, 2.28) * mm});
            skLineSegment(sketch, "E1097", {"start": v(-15.25, 2.28) * mm, "end": v(-15.4, 1.74) * mm});
            skLineSegment(sketch, "E1098", {"start": v(-15.4, 1.74) * mm, "end": v(-15.56, 1.23) * mm});
            skLineSegment(sketch, "E1099", {"start": v(-15.56, 1.23) * mm, "end": v(-15.77, 0.74) * mm});
            skLineSegment(sketch, "E1100", {"start": v(-15.77, 0.74) * mm, "end": v(-16, 0.27) * mm});
            skLineSegment(sketch, "E1101", {"start": v(-16, 0.27) * mm, "end": v(-16.27, -0.17) * mm});
            skLineSegment(sketch, "E1102", {"start": v(-16.27, -0.17) * mm, "end": v(-16.57, -0.6) * mm});
            skLineSegment(sketch, "E1103", {"start": v(-16.57, -0.6) * mm, "end": v(-16.9, -0.99) * mm});
            skLineSegment(sketch, "E1104", {"start": v(-16.9, -0.99) * mm, "end": v(-17.26, -1.36) * mm});
            skLineSegment(sketch, "E1105", {"start": v(-17.26, -1.36) * mm, "end": v(-17.65, -1.7) * mm});
            skLineSegment(sketch, "E1106", {"start": v(-17.65, -1.7) * mm, "end": v(-18.08, -2.02) * mm});
            skLineSegment(sketch, "E1107", {"start": v(-18.08, -2.02) * mm, "end": v(-18.53, -2.32) * mm});
            skLineSegment(sketch, "E1108", {"start": v(-18.53, -2.32) * mm, "end": v(-19.02, -2.6) * mm});
            skLineSegment(sketch, "E1109", {"start": v(-19.02, -2.6) * mm, "end": v(-19.3, -2.73) * mm});
            skLineSegment(sketch, "E1110", {"start": v(-19.3, -2.73) * mm, "end": v(-19.57, -2.86) * mm});
            skLineSegment(sketch, "E1111", {"start": v(-19.57, -2.86) * mm, "end": v(-19.85, -2.98) * mm});
            skLineSegment(sketch, "E1112", {"start": v(-19.85, -2.98) * mm, "end": v(-20.13, -3.1) * mm});
            skLineSegment(sketch, "E1113", {"start": v(-20.13, -3.1) * mm, "end": v(-20.4, -3.2) * mm});
            skLineSegment(sketch, "E1114", {"start": v(-20.4, -3.2) * mm, "end": v(-20.68, -3.3) * mm});
            skLineSegment(sketch, "E1115", {"start": v(-20.68, -3.3) * mm, "end": v(-20.96, -3.38) * mm});
            skLineSegment(sketch, "E1116", {"start": v(-20.96, -3.38) * mm, "end": v(-21.23, -3.46) * mm});
            skLineSegment(sketch, "E1117", {"start": v(-21.23, -3.46) * mm, "end": v(-21.5, -3.52) * mm});
            skLineSegment(sketch, "E1118", {"start": v(-21.5, -3.52) * mm, "end": v(-21.77, -3.58) * mm});
            skLineSegment(sketch, "E1119", {"start": v(-21.77, -3.58) * mm, "end": v(-22.04, -3.63) * mm});
            skLineSegment(sketch, "E1120", {"start": v(-22.04, -3.63) * mm, "end": v(-22.3, -3.67) * mm});
            skLineSegment(sketch, "E1121", {"start": v(-22.3, -3.67) * mm, "end": v(-22.57, -3.7) * mm});
            skLineSegment(sketch, "E1122", {"start": v(-22.57, -3.7) * mm, "end": v(-22.84, -3.73) * mm});
            skLineSegment(sketch, "E1123", {"start": v(-22.84, -3.73) * mm, "end": v(-23.1, -3.74) * mm});
            skLineSegment(sketch, "E1124", {"start": v(-23.1, -3.74) * mm, "end": v(-33.04, -3.75) * mm});
            skLineSegment(sketch, "E1125", {"start": v(-33.04, -3.75) * mm, "end": v(-33.16, -3.75) * mm});
            skLineSegment(sketch, "E1126", {"start": v(-33.16, -3.75) * mm, "end": v(-33.27, -3.77) * mm});
            skLineSegment(sketch, "E1127", {"start": v(-33.27, -3.77) * mm, "end": v(-33.39, -3.8) * mm});
            skLineSegment(sketch, "E1128", {"start": v(-33.39, -3.8) * mm, "end": v(-33.5, -3.84) * mm});
            skLineSegment(sketch, "E1129", {"start": v(-33.5, -3.84) * mm, "end": v(-33.6, -3.89) * mm});
            skLineSegment(sketch, "E1130", {"start": v(-33.6, -3.89) * mm, "end": v(-33.7, -3.95) * mm});
            skLineSegment(sketch, "E1131", {"start": v(-33.7, -3.95) * mm, "end": v(-33.78, -4.01) * mm});
            skLineSegment(sketch, "E1132", {"start": v(-33.78, -4.01) * mm, "end": v(-33.86, -4.09) * mm});
            skLineSegment(sketch, "E1133", {"start": v(-33.86, -4.09) * mm, "end": v(-33.94, -4.17) * mm});
            skLineSegment(sketch, "E1134", {"start": v(-33.94, -4.17) * mm, "end": v(-34, -4.26) * mm});
            skLineSegment(sketch, "E1135", {"start": v(-34, -4.26) * mm, "end": v(-34.06, -4.36) * mm});
            skLineSegment(sketch, "E1136", {"start": v(-34.06, -4.36) * mm, "end": v(-34.11, -4.46) * mm});
            skLineSegment(sketch, "E1137", {"start": v(-34.11, -4.46) * mm, "end": v(-34.15, -4.57) * mm});
            skLineSegment(sketch, "E1138", {"start": v(-34.15, -4.57) * mm, "end": v(-34.18, -4.68) * mm});
            skLineSegment(sketch, "E1139", {"start": v(-34.18, -4.68) * mm, "end": v(-34.2, -4.8) * mm});
            skLineSegment(sketch, "E1140", {"start": v(-34.2, -4.8) * mm, "end": v(-34.2, -4.91) * mm});
            skLineSegment(sketch, "E1141", {"start": v(-34.2, -4.91) * mm, "end": v(-34.2, -5.74) * mm});
            skLineSegment(sketch, "E1142", {"start": v(-34.2, -5.74) * mm, "end": v(-34.2, -5.82) * mm});
            skLineSegment(sketch, "E1143", {"start": v(-34.2, -5.82) * mm, "end": v(-34.2, -5.9) * mm});
            skLineSegment(sketch, "E1144", {"start": v(-34.2, -5.9) * mm, "end": v(-34.19, -5.98) * mm});
            skLineSegment(sketch, "E1145", {"start": v(-34.19, -5.98) * mm, "end": v(-34.17, -6.06) * mm});
            skLineSegment(sketch, "E1146", {"start": v(-34.17, -6.06) * mm, "end": v(-34.15, -6.14) * mm});
            skLineSegment(sketch, "E1147", {"start": v(-34.15, -6.14) * mm, "end": v(-34.13, -6.22) * mm});
            skLineSegment(sketch, "E1148", {"start": v(-34.13, -6.22) * mm, "end": v(-34.1, -6.3) * mm});
            skLineSegment(sketch, "E1149", {"start": v(-34.1, -6.3) * mm, "end": v(-34.08, -6.37) * mm});
            skLineSegment(sketch, "E1150", {"start": v(-34.08, -6.37) * mm, "end": v(-34.04, -6.45) * mm});
            skLineSegment(sketch, "E1151", {"start": v(-34.04, -6.45) * mm, "end": v(-34, -6.52) * mm});
            skLineSegment(sketch, "E1152", {"start": v(-34, -6.52) * mm, "end": v(-33.97, -6.6) * mm});
            skLineSegment(sketch, "E1153", {"start": v(-33.97, -6.6) * mm, "end": v(-33.92, -6.66) * mm});
            skLineSegment(sketch, "E1154", {"start": v(-33.92, -6.66) * mm, "end": v(-33.88, -6.73) * mm});
            skLineSegment(sketch, "E1155", {"start": v(-33.88, -6.73) * mm, "end": v(-33.83, -6.8) * mm});
            skLineSegment(sketch, "E1156", {"start": v(-33.83, -6.8) * mm, "end": v(-33.77, -6.86) * mm});
            skLineSegment(sketch, "E1157", {"start": v(-33.77, -6.86) * mm, "end": v(-33.72, -6.91) * mm});
            skLineSegment(sketch, "E1158", {"start": v(-33.72, -6.91) * mm, "end": v(-14.92, -25.66) * mm});
            skLineSegment(sketch, "E1159", {"start": v(-14.92, -25.66) * mm, "end": v(-14.82, -25.76) * mm});
            skLineSegment(sketch, "E1160", {"start": v(-14.82, -25.76) * mm, "end": v(-14.7, -25.85) * mm});
            skLineSegment(sketch, "E1161", {"start": v(-14.7, -25.85) * mm, "end": v(-14.6, -25.94) * mm});
            skLineSegment(sketch, "E1162", {"start": v(-14.6, -25.94) * mm, "end": v(-14.49, -26.02) * mm});
            skLineSegment(sketch, "E1163", {"start": v(-14.49, -26.02) * mm, "end": v(-14.37, -26.1) * mm});
            skLineSegment(sketch, "E1164", {"start": v(-14.37, -26.1) * mm, "end": v(-14.25, -26.16) * mm});
            skLineSegment(sketch, "E1165", {"start": v(-14.25, -26.16) * mm, "end": v(-14.13, -26.22) * mm});
            skLineSegment(sketch, "E1166", {"start": v(-14.13, -26.22) * mm, "end": v(-14, -26.28) * mm});
            skLineSegment(sketch, "E1167", {"start": v(-14, -26.28) * mm, "end": v(-13.87, -26.33) * mm});
            skLineSegment(sketch, "E1168", {"start": v(-13.87, -26.33) * mm, "end": v(-13.74, -26.37) * mm});
            skLineSegment(sketch, "E1169", {"start": v(-13.74, -26.37) * mm, "end": v(-13.61, -26.4) * mm});
            skLineSegment(sketch, "E1170", {"start": v(-13.61, -26.4) * mm, "end": v(-13.48, -26.43) * mm});
            skLineSegment(sketch, "E1171", {"start": v(-13.48, -26.43) * mm, "end": v(-13.34, -26.46) * mm});
            skLineSegment(sketch, "E1172", {"start": v(-13.34, -26.46) * mm, "end": v(-13.2, -26.48) * mm});
            skLineSegment(sketch, "E1173", {"start": v(-13.2, -26.48) * mm, "end": v(-13.06, -26.49) * mm});
            skLineSegment(sketch, "E1174", {"start": v(-13.06, -26.49) * mm, "end": v(-12.92, -26.49) * mm});
            skLineSegment(sketch, "E1175", {"start": v(-12.92, -26.49) * mm, "end": v(-7.66, -26.49) * mm});
            skLineSegment(sketch, "E1176", {"start": v(-7.66, -26.49) * mm, "end": v(-7.53, -26.48) * mm});
            skLineSegment(sketch, "E1177", {"start": v(-7.53, -26.48) * mm, "end": v(-7.4, -26.47) * mm});
            skLineSegment(sketch, "E1178", {"start": v(-7.4, -26.47) * mm, "end": v(-7.28, -26.45) * mm});
            skLineSegment(sketch, "E1179", {"start": v(-7.28, -26.45) * mm, "end": v(-7.15, -26.42) * mm});
            skLineSegment(sketch, "E1180", {"start": v(-7.15, -26.42) * mm, "end": v(-7.03, -26.38) * mm});
            skLineSegment(sketch, "E1181", {"start": v(-7.03, -26.38) * mm, "end": v(-6.92, -26.33) * mm});
            skLineSegment(sketch, "E1182", {"start": v(-6.92, -26.33) * mm, "end": v(-6.8, -26.28) * mm});
            skLineSegment(sketch, "E1183", {"start": v(-6.8, -26.28) * mm, "end": v(-6.7, -26.22) * mm});
            skLineSegment(sketch, "E1184", {"start": v(-6.7, -26.22) * mm, "end": v(-6.6, -26.15) * mm});
            skLineSegment(sketch, "E1185", {"start": v(-6.6, -26.15) * mm, "end": v(-6.5, -26.07) * mm});
            skLineSegment(sketch, "E1186", {"start": v(-6.5, -26.07) * mm, "end": v(-6.4, -25.99) * mm});
            skLineSegment(sketch, "E1187", {"start": v(-6.4, -25.99) * mm, "end": v(-6.3, -25.9) * mm});
            skLineSegment(sketch, "E1188", {"start": v(-6.3, -25.9) * mm, "end": v(-6.23, -25.8) * mm});
            skLineSegment(sketch, "E1189", {"start": v(-6.23, -25.8) * mm, "end": v(-6.15, -25.7) * mm});
            skLineSegment(sketch, "E1190", {"start": v(-6.15, -25.7) * mm, "end": v(-6.08, -25.59) * mm});
            skLineSegment(sketch, "E1191", {"start": v(-6.08, -25.59) * mm, "end": v(-6.02, -25.47) * mm});
            skLineSegment(sketch, "E1192", {"start": v(-6.02, -25.47) * mm, "end": v(12.19, 10.93) * mm});
            skLineSegment(sketch, "E1193", {"start": v(12.19, 10.93) * mm, "end": v(12.2, 10.95) * mm});
            skLineSegment(sketch, "E1194", {"start": v(12.2, 10.95) * mm, "end": v(12.2, 10.97) * mm});
            skLineSegment(sketch, "E1195", {"start": v(12.2, 10.97) * mm, "end": v(12.21, 10.98) * mm});
            skLineSegment(sketch, "E1196", {"start": v(12.21, 10.98) * mm, "end": v(12.22, 11) * mm});
            skLineSegment(sketch, "E1197", {"start": v(12.22, 11) * mm, "end": v(12.24, 11) * mm});
            skLineSegment(sketch, "E1198", {"start": v(12.24, 11) * mm, "end": v(12.25, 11.02) * mm});
            skLineSegment(sketch, "E1199", {"start": v(12.25, 11.02) * mm, "end": v(12.26, 11.03) * mm});
            skLineSegment(sketch, "E1200", {"start": v(12.26, 11.03) * mm, "end": v(12.28, 11.04) * mm});
            skLineSegment(sketch, "E1201", {"start": v(12.28, 11.04) * mm, "end": v(12.3, 11.04) * mm});
            skLineSegment(sketch, "E1202", {"start": v(12.3, 11.04) * mm, "end": v(12.3, 11.05) * mm});
            skLineSegment(sketch, "E1203", {"start": v(12.3, 11.05) * mm, "end": v(12.32, 11.06) * mm});
            skLineSegment(sketch, "E1204", {"start": v(12.32, 11.06) * mm, "end": v(12.34, 11.06) * mm});
            skLineSegment(sketch, "E1205", {"start": v(12.34, 11.06) * mm, "end": v(12.36, 11.07) * mm});
            skLineSegment(sketch, "E1206", {"start": v(12.36, 11.07) * mm, "end": v(12.37, 11.07) * mm});
            skLineSegment(sketch, "E1207", {"start": v(12.37, 11.07) * mm, "end": v(12.4, 11.07) * mm});
            skLineSegment(sketch, "E1208", {"start": v(12.4, 11.07) * mm, "end": v(12.4, 11.07) * mm});
            skLineSegment(sketch, "E1209", {"start": v(12.4, 11.07) * mm, "end": v(12.43, 11.07) * mm});
            skLineSegment(sketch, "E1210", {"start": v(12.43, 11.07) * mm, "end": v(12.44, 11.07) * mm});
            skLineSegment(sketch, "E1211", {"start": v(12.44, 11.07) * mm, "end": v(12.46, 11.07) * mm});
            skLineSegment(sketch, "E1212", {"start": v(12.46, 11.07) * mm, "end": v(12.48, 11.06) * mm});
            skLineSegment(sketch, "E1213", {"start": v(12.48, 11.06) * mm, "end": v(12.5, 11.06) * mm});
            skLineSegment(sketch, "E1214", {"start": v(12.5, 11.06) * mm, "end": v(12.51, 11.05) * mm});
            skLineSegment(sketch, "E1215", {"start": v(12.51, 11.05) * mm, "end": v(12.53, 11.04) * mm});
            skLineSegment(sketch, "E1216", {"start": v(12.53, 11.04) * mm, "end": v(12.54, 11.04) * mm});
            skLineSegment(sketch, "E1217", {"start": v(12.54, 11.04) * mm, "end": v(12.56, 11.03) * mm});
            skLineSegment(sketch, "E1218", {"start": v(12.56, 11.03) * mm, "end": v(12.57, 11.02) * mm});
            skLineSegment(sketch, "E1219", {"start": v(12.57, 11.02) * mm, "end": v(12.58, 11) * mm});
            skLineSegment(sketch, "E1220", {"start": v(12.58, 11) * mm, "end": v(12.6, 11) * mm});
            skLineSegment(sketch, "E1221", {"start": v(12.6, 11) * mm, "end": v(12.6, 10.98) * mm});
            skLineSegment(sketch, "E1222", {"start": v(12.6, 10.98) * mm, "end": v(12.61, 10.97) * mm});
            skLineSegment(sketch, "E1223", {"start": v(12.61, 10.97) * mm, "end": v(12.62, 10.95) * mm});
            skLineSegment(sketch, "E1224", {"start": v(12.62, 10.95) * mm, "end": v(12.63, 10.93) * mm});
            skLineSegment(sketch, "E1225", {"start": v(12.63, 10.93) * mm, "end": v(19.74, -3.27) * mm});
            skLineSegment(sketch, "E1226", {"start": v(19.74, -3.27) * mm, "end": v(19.74, -3.29) * mm});
            skLineSegment(sketch, "E1227", {"start": v(19.74, -3.29) * mm, "end": v(19.75, -3.3) * mm});
            skLineSegment(sketch, "E1228", {"start": v(19.75, -3.3) * mm, "end": v(19.75, -3.32) * mm});
            skLineSegment(sketch, "E1229", {"start": v(19.75, -3.32) * mm, "end": v(19.76, -3.33) * mm});
            skLineSegment(sketch, "E1230", {"start": v(19.76, -3.33) * mm, "end": v(19.76, -3.35) * mm});
            skLineSegment(sketch, "E1231", {"start": v(19.76, -3.35) * mm, "end": v(19.76, -3.37) * mm});
            skLineSegment(sketch, "E1232", {"start": v(19.76, -3.37) * mm, "end": v(19.76, -3.38) * mm});
            skLineSegment(sketch, "E1233", {"start": v(19.76, -3.38) * mm, "end": v(19.76, -3.4) * mm});
            skLineSegment(sketch, "E1234", {"start": v(19.76, -3.4) * mm, "end": v(19.76, -3.41) * mm});
            skLineSegment(sketch, "E1235", {"start": v(19.76, -3.41) * mm, "end": v(19.76, -3.43) * mm});
            skLineSegment(sketch, "E1236", {"start": v(19.76, -3.43) * mm, "end": v(19.76, -3.44) * mm});
            skLineSegment(sketch, "E1237", {"start": v(19.76, -3.44) * mm, "end": v(19.75, -3.46) * mm});
            skLineSegment(sketch, "E1238", {"start": v(19.75, -3.46) * mm, "end": v(19.75, -3.48) * mm});
            skLineSegment(sketch, "E1239", {"start": v(19.75, -3.48) * mm, "end": v(19.74, -3.5) * mm});
            skLineSegment(sketch, "E1240", {"start": v(19.74, -3.5) * mm, "end": v(19.73, -3.5) * mm});
            skLineSegment(sketch, "E1241", {"start": v(19.73, -3.5) * mm, "end": v(19.72, -3.52) * mm});
            skLineSegment(sketch, "E1242", {"start": v(19.72, -3.52) * mm, "end": v(19.72, -3.53) * mm});
            skLineSegment(sketch, "E1243", {"start": v(19.72, -3.53) * mm, "end": v(19.7, -3.55) * mm});
            skLineSegment(sketch, "E1244", {"start": v(19.7, -3.55) * mm, "end": v(19.7, -3.56) * mm});
            skLineSegment(sketch, "E1245", {"start": v(19.7, -3.56) * mm, "end": v(19.68, -3.57) * mm});
            skLineSegment(sketch, "E1246", {"start": v(19.68, -3.57) * mm, "end": v(19.67, -3.58) * mm});
            skLineSegment(sketch, "E1247", {"start": v(19.67, -3.58) * mm, "end": v(19.66, -3.6) * mm});
            skLineSegment(sketch, "E1248", {"start": v(19.66, -3.6) * mm, "end": v(19.65, -3.6) * mm});
            skLineSegment(sketch, "E1249", {"start": v(19.65, -3.6) * mm, "end": v(19.63, -3.6) * mm});
            skLineSegment(sketch, "E1250", {"start": v(19.63, -3.6) * mm, "end": v(19.62, -3.62) * mm});
            skLineSegment(sketch, "E1251", {"start": v(19.62, -3.62) * mm, "end": v(19.6, -3.62) * mm});
            skLineSegment(sketch, "E1252", {"start": v(19.6, -3.62) * mm, "end": v(19.59, -3.63) * mm});
            skLineSegment(sketch, "E1253", {"start": v(19.59, -3.63) * mm, "end": v(19.57, -3.63) * mm});
            skLineSegment(sketch, "E1254", {"start": v(19.57, -3.63) * mm, "end": v(19.56, -3.64) * mm});
            skLineSegment(sketch, "E1255", {"start": v(19.56, -3.64) * mm, "end": v(19.54, -3.64) * mm});
            skLineSegment(sketch, "E1256", {"start": v(19.54, -3.64) * mm, "end": v(19.53, -3.64) * mm});
            skLineSegment(sketch, "E1257", {"start": v(19.53, -3.64) * mm, "end": v(19.5, -3.64) * mm});
            skLineSegment(sketch, "E1258", {"start": v(19.5, -3.64) * mm, "end": v(9.92, -3.64) * mm});
            skLineSegment(sketch, "E1259", {"start": v(9.92, -3.64) * mm, "end": v(9.7, -3.64) * mm});
            skLineSegment(sketch, "E1260", {"start": v(9.7, -3.64) * mm, "end": v(9.49, -3.66) * mm});
            skLineSegment(sketch, "E1261", {"start": v(9.49, -3.66) * mm, "end": v(9.28, -3.68) * mm});
            skLineSegment(sketch, "E1262", {"start": v(9.28, -3.68) * mm, "end": v(9.07, -3.7) * mm});
            skLineSegment(sketch, "E1263", {"start": v(9.07, -3.7) * mm, "end": v(8.87, -3.75) * mm});
            skLineSegment(sketch, "E1264", {"start": v(8.87, -3.75) * mm, "end": v(8.68, -3.8) * mm});
            skLineSegment(sketch, "E1265", {"start": v(8.68, -3.8) * mm, "end": v(8.5, -3.85) * mm});
            skLineSegment(sketch, "E1266", {"start": v(8.5, -3.85) * mm, "end": v(8.31, -3.91) * mm});
            skLineSegment(sketch, "E1267", {"start": v(8.31, -3.91) * mm, "end": v(8.13, -3.99) * mm});
            skLineSegment(sketch, "E1268", {"start": v(8.13, -3.99) * mm, "end": v(7.96, -4.07) * mm});
            skLineSegment(sketch, "E1269", {"start": v(7.96, -4.07) * mm, "end": v(7.8, -4.16) * mm});
            skLineSegment(sketch, "E1270", {"start": v(7.8, -4.16) * mm, "end": v(7.63, -4.25) * mm});
            skLineSegment(sketch, "E1271", {"start": v(7.63, -4.25) * mm, "end": v(7.48, -4.36) * mm});
            skLineSegment(sketch, "E1272", {"start": v(7.48, -4.36) * mm, "end": v(7.33, -4.47) * mm});
            skLineSegment(sketch, "E1273", {"start": v(7.33, -4.47) * mm, "end": v(7.18, -4.6) * mm});
            skLineSegment(sketch, "E1274", {"start": v(7.18, -4.6) * mm, "end": v(7.05, -4.73) * mm});
            skLineSegment(sketch, "E1275", {"start": v(7.05, -4.73) * mm, "end": v(6.92, -4.87) * mm});
            skLineSegment(sketch, "E1276", {"start": v(6.92, -4.87) * mm, "end": v(6.8, -5.01) * mm});
            skLineSegment(sketch, "E1277", {"start": v(6.8, -5.01) * mm, "end": v(6.68, -5.16) * mm});
            skLineSegment(sketch, "E1278", {"start": v(6.68, -5.16) * mm, "end": v(6.57, -5.31) * mm});
            skLineSegment(sketch, "E1279", {"start": v(6.57, -5.31) * mm, "end": v(6.47, -5.48) * mm});
            skLineSegment(sketch, "E1280", {"start": v(6.47, -5.48) * mm, "end": v(6.39, -5.64) * mm});
            skLineSegment(sketch, "E1281", {"start": v(6.39, -5.64) * mm, "end": v(6.3, -5.81) * mm});
            skLineSegment(sketch, "E1282", {"start": v(6.3, -5.81) * mm, "end": v(6.23, -6) * mm});
            skLineSegment(sketch, "E1283", {"start": v(6.23, -6) * mm, "end": v(6.17, -6.17) * mm});
            skLineSegment(sketch, "E1284", {"start": v(6.17, -6.17) * mm, "end": v(6.11, -6.36) * mm});
            skLineSegment(sketch, "E1285", {"start": v(6.11, -6.36) * mm, "end": v(6.07, -6.56) * mm});
            skLineSegment(sketch, "E1286", {"start": v(6.07, -6.56) * mm, "end": v(6.03, -6.76) * mm});
            skLineSegment(sketch, "E1287", {"start": v(6.03, -6.76) * mm, "end": v(6, -6.96) * mm});
            skLineSegment(sketch, "E1288", {"start": v(6, -6.96) * mm, "end": v(5.98, -7.17) * mm});
            skLineSegment(sketch, "E1289", {"start": v(5.98, -7.17) * mm, "end": v(5.96, -7.38) * mm});
            skLineSegment(sketch, "E1290", {"start": v(5.96, -7.38) * mm, "end": v(5.96, -7.6) * mm});
            skLineSegment(sketch, "E1291", {"start": v(5.96, -7.6) * mm, "end": v(5.96, -7.82) * mm});
            skLineSegment(sketch, "E1292", {"start": v(5.96, -7.82) * mm, "end": v(5.98, -8.03) * mm});
            skLineSegment(sketch, "E1293", {"start": v(5.98, -8.03) * mm, "end": v(6, -8.23) * mm});
            skLineSegment(sketch, "E1294", {"start": v(6, -8.23) * mm, "end": v(6.03, -8.43) * mm});
            skLineSegment(sketch, "E1295", {"start": v(6.03, -8.43) * mm, "end": v(6.07, -8.63) * mm});
            skLineSegment(sketch, "E1296", {"start": v(6.07, -8.63) * mm, "end": v(6.12, -8.82) * mm});
            skLineSegment(sketch, "E1297", {"start": v(6.12, -8.82) * mm, "end": v(6.17, -9) * mm});
            skLineSegment(sketch, "E1298", {"start": v(6.17, -9) * mm, "end": v(6.24, -9.19) * mm});
            skLineSegment(sketch, "E1299", {"start": v(6.24, -9.19) * mm, "end": v(6.31, -9.37) * mm});
            skLineSegment(sketch, "E1300", {"start": v(6.31, -9.37) * mm, "end": v(6.4, -9.54) * mm});
            skLineSegment(sketch, "E1301", {"start": v(6.4, -9.54) * mm, "end": v(6.49, -9.7) * mm});
            skLineSegment(sketch, "E1302", {"start": v(6.49, -9.7) * mm, "end": v(6.59, -9.87) * mm});
            skLineSegment(sketch, "E1303", {"start": v(6.59, -9.87) * mm, "end": v(6.7, -10.03) * mm});
            skLineSegment(sketch, "E1304", {"start": v(6.7, -10.03) * mm, "end": v(6.81, -10.18) * mm});
            skLineSegment(sketch, "E1305", {"start": v(6.81, -10.18) * mm, "end": v(6.94, -10.33) * mm});
            skLineSegment(sketch, "E1306", {"start": v(6.94, -10.33) * mm, "end": v(7.07, -10.48) * mm});
            skLineSegment(sketch, "E1307", {"start": v(7.07, -10.48) * mm, "end": v(7.21, -10.62) * mm});
            skLineSegment(sketch, "E1308", {"start": v(7.21, -10.62) * mm, "end": v(7.36, -10.74) * mm});
            skLineSegment(sketch, "E1309", {"start": v(7.36, -10.74) * mm, "end": v(7.51, -10.86) * mm});
            skLineSegment(sketch, "E1310", {"start": v(7.51, -10.86) * mm, "end": v(7.67, -10.98) * mm});
            skLineSegment(sketch, "E1311", {"start": v(7.67, -10.98) * mm, "end": v(7.83, -11.08) * mm});
            skLineSegment(sketch, "E1312", {"start": v(7.83, -11.08) * mm, "end": v(8, -11.17) * mm});
            skLineSegment(sketch, "E1313", {"start": v(8, -11.17) * mm, "end": v(8.17, -11.26) * mm});
            skLineSegment(sketch, "E1314", {"start": v(8.17, -11.26) * mm, "end": v(8.34, -11.33) * mm});
            skLineSegment(sketch, "E1315", {"start": v(8.34, -11.33) * mm, "end": v(8.52, -11.4) * mm});
            skLineSegment(sketch, "E1316", {"start": v(8.52, -11.4) * mm, "end": v(8.7, -11.46) * mm});
            skLineSegment(sketch, "E1317", {"start": v(8.7, -11.46) * mm, "end": v(8.9, -11.5) * mm});
            skLineSegment(sketch, "E1318", {"start": v(8.9, -11.5) * mm, "end": v(9.1, -11.55) * mm});
            skLineSegment(sketch, "E1319", {"start": v(9.1, -11.55) * mm, "end": v(9.3, -11.58) * mm});
            skLineSegment(sketch, "E1320", {"start": v(9.3, -11.58) * mm, "end": v(9.5, -11.6) * mm});
            skLineSegment(sketch, "E1321", {"start": v(9.5, -11.6) * mm, "end": v(9.7, -11.61) * mm});
            skLineSegment(sketch, "E1322", {"start": v(9.7, -11.61) * mm, "end": v(9.92, -11.62) * mm});
            skLineSegment(sketch, "E1323", {"start": v(9.92, -11.62) * mm, "end": v(23.5, -11.62) * mm});
            skLineSegment(sketch, "E1324", {"start": v(23.5, -11.62) * mm, "end": v(23.54, -11.62) * mm});
            skLineSegment(sketch, "E1325", {"start": v(23.54, -11.62) * mm, "end": v(23.58, -11.63) * mm});
            skLineSegment(sketch, "E1326", {"start": v(23.58, -11.63) * mm, "end": v(23.63, -11.63) * mm});
            skLineSegment(sketch, "E1327", {"start": v(23.63, -11.63) * mm, "end": v(23.67, -11.64) * mm});
            skLineSegment(sketch, "E1328", {"start": v(23.67, -11.64) * mm, "end": v(23.7, -11.66) * mm});
            skLineSegment(sketch, "E1329", {"start": v(23.7, -11.66) * mm, "end": v(23.75, -11.67) * mm});
            skLineSegment(sketch, "E1330", {"start": v(23.75, -11.67) * mm, "end": v(23.79, -11.7) * mm});
            skLineSegment(sketch, "E1331", {"start": v(23.79, -11.7) * mm, "end": v(23.83, -11.71) * mm});
            skLineSegment(sketch, "E1332", {"start": v(23.83, -11.71) * mm, "end": v(23.86, -11.74) * mm});
            skLineSegment(sketch, "E1333", {"start": v(23.86, -11.74) * mm, "end": v(23.9, -11.76) * mm});
            skLineSegment(sketch, "E1334", {"start": v(23.9, -11.76) * mm, "end": v(23.93, -11.8) * mm});
            skLineSegment(sketch, "E1335", {"start": v(23.93, -11.8) * mm, "end": v(23.96, -11.82) * mm});
            skLineSegment(sketch, "E1336", {"start": v(23.96, -11.82) * mm, "end": v(23.99, -11.85) * mm});
            skLineSegment(sketch, "E1337", {"start": v(23.99, -11.85) * mm, "end": v(24.01, -11.89) * mm});
            skLineSegment(sketch, "E1338", {"start": v(24.01, -11.89) * mm, "end": v(24.04, -11.93) * mm});
            skLineSegment(sketch, "E1339", {"start": v(24.04, -11.93) * mm, "end": v(24.06, -11.97) * mm});
            skLineSegment(sketch, "E1340", {"start": v(24.06, -11.97) * mm, "end": v(30.99, -25.78) * mm});
            skLineSegment(sketch, "E1341", {"start": v(30.99, -25.78) * mm, "end": v(31.03, -25.86) * mm});
            skLineSegment(sketch, "E1342", {"start": v(31.03, -25.86) * mm, "end": v(31.08, -25.93) * mm});
            skLineSegment(sketch, "E1343", {"start": v(31.08, -25.93) * mm, "end": v(31.13, -26) * mm});
            skLineSegment(sketch, "E1344", {"start": v(31.13, -26) * mm, "end": v(31.2, -26.07) * mm});
            skLineSegment(sketch, "E1345", {"start": v(31.2, -26.07) * mm, "end": v(31.25, -26.14) * mm});
            skLineSegment(sketch, "E1346", {"start": v(31.25, -26.14) * mm, "end": v(31.32, -26.2) * mm});
            skLineSegment(sketch, "E1347", {"start": v(31.32, -26.2) * mm, "end": v(31.39, -26.25) * mm});
            skLineSegment(sketch, "E1348", {"start": v(31.39, -26.25) * mm, "end": v(31.46, -26.3) * mm});
            skLineSegment(sketch, "E1349", {"start": v(31.46, -26.3) * mm, "end": v(31.54, -26.34) * mm});
            skLineSegment(sketch, "E1350", {"start": v(31.54, -26.34) * mm, "end": v(31.62, -26.38) * mm});
            skLineSegment(sketch, "E1351", {"start": v(31.62, -26.38) * mm, "end": v(31.7, -26.41) * mm});
            skLineSegment(sketch, "E1352", {"start": v(31.7, -26.41) * mm, "end": v(31.79, -26.44) * mm});
            skLineSegment(sketch, "E1353", {"start": v(31.79, -26.44) * mm, "end": v(31.87, -26.46) * mm});
            skLineSegment(sketch, "E1354", {"start": v(31.87, -26.46) * mm, "end": v(31.96, -26.48) * mm});
            skLineSegment(sketch, "E1355", {"start": v(31.96, -26.48) * mm, "end": v(32.05, -26.49) * mm});
            skLineSegment(sketch, "E1356", {"start": v(32.05, -26.49) * mm, "end": v(32.14, -26.49) * mm});
            skLineSegment(sketch, "E1357", {"start": v(32.14, -26.49) * mm, "end": v(35.96, -26.49) * mm});
            skLineSegment(sketch, "E1358", {"start": v(35.96, -26.49) * mm, "end": v(36.17, -26.48) * mm});
            skLineSegment(sketch, "E1359", {"start": v(36.17, -26.48) * mm, "end": v(36.38, -26.47) * mm});
            skLineSegment(sketch, "E1360", {"start": v(36.38, -26.47) * mm, "end": v(36.58, -26.45) * mm});
            skLineSegment(sketch, "E1361", {"start": v(36.58, -26.45) * mm, "end": v(36.78, -26.42) * mm});
            skLineSegment(sketch, "E1362", {"start": v(36.78, -26.42) * mm, "end": v(36.98, -26.38) * mm});
            skLineSegment(sketch, "E1363", {"start": v(36.98, -26.38) * mm, "end": v(37.17, -26.33) * mm});
            skLineSegment(sketch, "E1364", {"start": v(37.17, -26.33) * mm, "end": v(37.35, -26.27) * mm});
            skLineSegment(sketch, "E1365", {"start": v(37.35, -26.27) * mm, "end": v(37.53, -26.2) * mm});
            skLineSegment(sketch, "E1366", {"start": v(37.53, -26.2) * mm, "end": v(37.71, -26.13) * mm});
            skLineSegment(sketch, "E1367", {"start": v(37.71, -26.13) * mm, "end": v(37.88, -26.05) * mm});
            skLineSegment(sketch, "E1368", {"start": v(37.88, -26.05) * mm, "end": v(38.05, -25.96) * mm});
            skLineSegment(sketch, "E1369", {"start": v(38.05, -25.96) * mm, "end": v(38.2, -25.86) * mm});
            skLineSegment(sketch, "E1370", {"start": v(38.2, -25.86) * mm, "end": v(38.37, -25.75) * mm});
            skLineSegment(sketch, "E1371", {"start": v(38.37, -25.75) * mm, "end": v(38.52, -25.63) * mm});
            skLineSegment(sketch, "E1372", {"start": v(38.52, -25.63) * mm, "end": v(38.66, -25.5) * mm});
            skLineSegment(sketch, "E1373", {"start": v(38.66, -25.5) * mm, "end": v(38.8, -25.37) * mm});
            skLineSegment(sketch, "E1374", {"start": v(38.8, -25.37) * mm, "end": v(38.94, -25.23) * mm});
            skLineSegment(sketch, "E1375", {"start": v(38.94, -25.23) * mm, "end": v(39.07, -25.09) * mm});
            skLineSegment(sketch, "E1376", {"start": v(39.07, -25.09) * mm, "end": v(39.18, -24.94) * mm});
            skLineSegment(sketch, "E1377", {"start": v(39.18, -24.94) * mm, "end": v(39.3, -24.78) * mm});
            skLineSegment(sketch, "E1378", {"start": v(39.3, -24.78) * mm, "end": v(39.4, -24.62) * mm});
            skLineSegment(sketch, "E1379", {"start": v(39.4, -24.62) * mm, "end": v(39.48, -24.45) * mm});
            skLineSegment(sketch, "E1380", {"start": v(39.48, -24.45) * mm, "end": v(39.57, -24.28) * mm});
            skLineSegment(sketch, "E1381", {"start": v(39.57, -24.28) * mm, "end": v(39.64, -24.1) * mm});
            skLineSegment(sketch, "E1382", {"start": v(39.64, -24.1) * mm, "end": v(39.7, -23.92) * mm});
            skLineSegment(sketch, "E1383", {"start": v(39.7, -23.92) * mm, "end": v(39.76, -23.74) * mm});
            skLineSegment(sketch, "E1384", {"start": v(39.76, -23.74) * mm, "end": v(39.8, -23.55) * mm});
            skLineSegment(sketch, "E1385", {"start": v(39.8, -23.55) * mm, "end": v(39.85, -23.35) * mm});
            skLineSegment(sketch, "E1386", {"start": v(39.85, -23.35) * mm, "end": v(39.88, -23.15) * mm});
            skLineSegment(sketch, "E1387", {"start": v(39.88, -23.15) * mm, "end": v(39.9, -22.95) * mm});
            skLineSegment(sketch, "E1388", {"start": v(39.9, -22.95) * mm, "end": v(39.91, -22.74) * mm});
            skLineSegment(sketch, "E1389", {"start": v(39.91, -22.74) * mm, "end": v(39.92, -22.53) * mm});
            skLineSegment(sketch, "E1390", {"start": v(39.92, -22.53) * mm, "end": v(39.92, 12.54) * mm});
            skLineSegment(sketch, "E1391", {"start": v(39.92, 12.54) * mm, "end": v(39.92, 12.6) * mm});
            skLineSegment(sketch, "E1392", {"start": v(39.92, 12.6) * mm, "end": v(39.93, 12.64) * mm});
            skLineSegment(sketch, "E1393", {"start": v(39.93, 12.64) * mm, "end": v(39.94, 12.7) * mm});
            skLineSegment(sketch, "E1394", {"start": v(39.94, 12.7) * mm, "end": v(39.96, 12.74) * mm});
            skLineSegment(sketch, "E1395", {"start": v(39.96, 12.74) * mm, "end": v(39.98, 12.78) * mm});
            skLineSegment(sketch, "E1396", {"start": v(39.98, 12.78) * mm, "end": v(40, 12.82) * mm});
            skLineSegment(sketch, "E1397", {"start": v(40, 12.82) * mm, "end": v(40.03, 12.86) * mm});
            skLineSegment(sketch, "E1398", {"start": v(40.03, 12.86) * mm, "end": v(40.06, 12.9) * mm});
            skLineSegment(sketch, "E1399", {"start": v(40.06, 12.9) * mm, "end": v(40.1, 12.93) * mm});
            skLineSegment(sketch, "E1400", {"start": v(40.1, 12.93) * mm, "end": v(40.14, 12.96) * mm});
            skLineSegment(sketch, "E1401", {"start": v(40.14, 12.96) * mm, "end": v(40.18, 12.98) * mm});
            skLineSegment(sketch, "E1402", {"start": v(40.18, 12.98) * mm, "end": v(40.22, 13) * mm});
            skLineSegment(sketch, "E1403", {"start": v(40.22, 13) * mm, "end": v(40.27, 13.02) * mm});
            skLineSegment(sketch, "E1404", {"start": v(40.27, 13.02) * mm, "end": v(40.32, 13.03) * mm});
            skLineSegment(sketch, "E1405", {"start": v(40.32, 13.03) * mm, "end": v(40.37, 13.04) * mm});
            skLineSegment(sketch, "E1406", {"start": v(40.37, 13.04) * mm, "end": v(40.42, 13.04) * mm});
            skLineSegment(sketch, "E1407", {"start": v(40.42, 13.04) * mm, "end": v(53.53, 13.04) * mm});
            skLineSegment(sketch, "E1408", {"start": v(53.53, 13.04) * mm, "end": v(53.8, 13.02) * mm});
            skLineSegment(sketch, "E1409", {"start": v(53.8, 13.02) * mm, "end": v(54.08, 13) * mm});
            skLineSegment(sketch, "E1410", {"start": v(54.08, 13) * mm, "end": v(54.35, 12.97) * mm});
            skLineSegment(sketch, "E1411", {"start": v(54.35, 12.97) * mm, "end": v(54.63, 12.93) * mm});
            skLineSegment(sketch, "E1412", {"start": v(54.63, 12.93) * mm, "end": v(54.9, 12.88) * mm});
            skLineSegment(sketch, "E1413", {"start": v(54.9, 12.88) * mm, "end": v(55.17, 12.83) * mm});
            skLineSegment(sketch, "E1414", {"start": v(55.17, 12.83) * mm, "end": v(55.45, 12.76) * mm});
            skLineSegment(sketch, "E1415", {"start": v(55.45, 12.76) * mm, "end": v(55.72, 12.7) * mm});
            skLineSegment(sketch, "E1416", {"start": v(55.72, 12.7) * mm, "end": v(55.99, 12.6) * mm});
            skLineSegment(sketch, "E1417", {"start": v(55.99, 12.6) * mm, "end": v(56.26, 12.52) * mm});
            skLineSegment(sketch, "E1418", {"start": v(56.26, 12.52) * mm, "end": v(56.53, 12.42) * mm});
            skLineSegment(sketch, "E1419", {"start": v(56.53, 12.42) * mm, "end": v(56.8, 12.31) * mm});
            skLineSegment(sketch, "E1420", {"start": v(56.8, 12.31) * mm, "end": v(57.07, 12.2) * mm});
            skLineSegment(sketch, "E1421", {"start": v(57.07, 12.2) * mm, "end": v(57.34, 12.07) * mm});
            skLineSegment(sketch, "E1422", {"start": v(57.34, 12.07) * mm, "end": v(57.6, 11.94) * mm});
            skLineSegment(sketch, "E1423", {"start": v(57.6, 11.94) * mm, "end": v(58.1, 11.67) * mm});
            skLineSegment(sketch, "E1424", {"start": v(58.1, 11.67) * mm, "end": v(58.54, 11.37) * mm});
            skLineSegment(sketch, "E1425", {"start": v(58.54, 11.37) * mm, "end": v(58.97, 11.05) * mm});
            skLineSegment(sketch, "E1426", {"start": v(58.97, 11.05) * mm, "end": v(59.36, 10.7) * mm});
            skLineSegment(sketch, "E1427", {"start": v(59.36, 10.7) * mm, "end": v(59.72, 10.33) * mm});
            skLineSegment(sketch, "E1428", {"start": v(59.72, 10.33) * mm, "end": v(60.05, 9.94) * mm});
            skLineSegment(sketch, "E1429", {"start": v(60.05, 9.94) * mm, "end": v(60.35, 9.52) * mm});
            skLineSegment(sketch, "E1430", {"start": v(60.35, 9.52) * mm, "end": v(60.62, 9.08) * mm});
            skLineSegment(sketch, "E1431", {"start": v(60.62, 9.08) * mm, "end": v(60.85, 8.6) * mm});
            skLineSegment(sketch, "E1432", {"start": v(60.85, 8.6) * mm, "end": v(61.06, 8.12) * mm});
            skLineSegment(sketch, "E1433", {"start": v(61.06, 8.12) * mm, "end": v(61.23, 7.6) * mm});
            skLineSegment(sketch, "E1434", {"start": v(61.23, 7.6) * mm, "end": v(61.37, 7.06) * mm});
            skLineSegment(sketch, "E1435", {"start": v(61.37, 7.06) * mm, "end": v(61.48, 6.5) * mm});
            skLineSegment(sketch, "E1436", {"start": v(61.48, 6.5) * mm, "end": v(61.56, 5.92) * mm});
            skLineSegment(sketch, "E1437", {"start": v(61.56, 5.92) * mm, "end": v(61.61, 5.3) * mm});
            skLineSegment(sketch, "E1438", {"start": v(61.61, 5.3) * mm, "end": v(61.63, 4.67) * mm});
            skLineSegment(sketch, "E1439", {"start": v(61.63, 4.67) * mm, "end": v(61.61, 4.04) * mm});
            skLineSegment(sketch, "E1440", {"start": v(61.61, 4.04) * mm, "end": v(61.56, 3.43) * mm});
            skLineSegment(sketch, "E1441", {"start": v(61.56, 3.43) * mm, "end": v(61.48, 2.85) * mm});
            skLineSegment(sketch, "E1442", {"start": v(61.48, 2.85) * mm, "end": v(61.37, 2.28) * mm});
            skLineSegment(sketch, "E1443", {"start": v(61.37, 2.28) * mm, "end": v(61.23, 1.74) * mm});
            skLineSegment(sketch, "E1444", {"start": v(61.23, 1.74) * mm, "end": v(61.06, 1.23) * mm});
            skLineSegment(sketch, "E1445", {"start": v(61.06, 1.23) * mm, "end": v(60.85, 0.74) * mm});
            skLineSegment(sketch, "E1446", {"start": v(60.85, 0.74) * mm, "end": v(60.62, 0.27) * mm});
            skLineSegment(sketch, "E1447", {"start": v(60.62, 0.27) * mm, "end": v(60.35, -0.17) * mm});
            skLineSegment(sketch, "E1448", {"start": v(60.35, -0.17) * mm, "end": v(60.05, -0.6) * mm});
            skLineSegment(sketch, "E1449", {"start": v(60.05, -0.6) * mm, "end": v(59.72, -0.99) * mm});
            skLineSegment(sketch, "E1450", {"start": v(59.72, -0.99) * mm, "end": v(59.36, -1.36) * mm});
            skLineSegment(sketch, "E1451", {"start": v(59.36, -1.36) * mm, "end": v(58.97, -1.7) * mm});
            skLineSegment(sketch, "E1452", {"start": v(58.97, -1.7) * mm, "end": v(58.55, -2.02) * mm});
            skLineSegment(sketch, "E1453", {"start": v(58.55, -2.02) * mm, "end": v(58.1, -2.32) * mm});
            skLineSegment(sketch, "E1454", {"start": v(58.1, -2.32) * mm, "end": v(57.6, -2.6) * mm});
            skLineSegment(sketch, "E1455", {"start": v(57.6, -2.6) * mm, "end": v(57.33, -2.73) * mm});
            skLineSegment(sketch, "E1456", {"start": v(57.33, -2.73) * mm, "end": v(57.05, -2.86) * mm});
            skLineSegment(sketch, "E1457", {"start": v(57.05, -2.86) * mm, "end": v(56.77, -2.98) * mm});
            skLineSegment(sketch, "E1458", {"start": v(56.77, -2.98) * mm, "end": v(56.5, -3.1) * mm});
            skLineSegment(sketch, "E1459", {"start": v(56.5, -3.1) * mm, "end": v(56.22, -3.2) * mm});
            skLineSegment(sketch, "E1460", {"start": v(56.22, -3.2) * mm, "end": v(55.94, -3.3) * mm});
            skLineSegment(sketch, "E1461", {"start": v(55.94, -3.3) * mm, "end": v(55.67, -3.38) * mm});
            skLineSegment(sketch, "E1462", {"start": v(55.67, -3.38) * mm, "end": v(55.4, -3.46) * mm});
            skLineSegment(sketch, "E1463", {"start": v(55.4, -3.46) * mm, "end": v(55.12, -3.52) * mm});
            skLineSegment(sketch, "E1464", {"start": v(55.12, -3.52) * mm, "end": v(54.85, -3.58) * mm});
            skLineSegment(sketch, "E1465", {"start": v(54.85, -3.58) * mm, "end": v(54.58, -3.63) * mm});
            skLineSegment(sketch, "E1466", {"start": v(54.58, -3.63) * mm, "end": v(54.31, -3.67) * mm});
            skLineSegment(sketch, "E1467", {"start": v(54.31, -3.67) * mm, "end": v(54.05, -3.7) * mm});
            skLineSegment(sketch, "E1468", {"start": v(54.05, -3.7) * mm, "end": v(53.78, -3.73) * mm});
            skLineSegment(sketch, "E1469", {"start": v(53.78, -3.73) * mm, "end": v(53.52, -3.74) * mm});
            skLineSegment(sketch, "E1470", {"start": v(53.52, -3.74) * mm, "end": v(45.85, -3.75) * mm});
            skLineSegment(sketch, "E1471", {"start": v(45.85, -3.75) * mm, "end": v(45.64, -3.75) * mm});
            skLineSegment(sketch, "E1472", {"start": v(45.64, -3.75) * mm, "end": v(45.43, -3.76) * mm});
            skLineSegment(sketch, "E1473", {"start": v(45.43, -3.76) * mm, "end": v(45.22, -3.79) * mm});
            skLineSegment(sketch, "E1474", {"start": v(45.22, -3.79) * mm, "end": v(45.02, -3.82) * mm});
            skLineSegment(sketch, "E1475", {"start": v(45.02, -3.82) * mm, "end": v(44.83, -3.86) * mm});
            skLineSegment(sketch, "E1476", {"start": v(44.83, -3.86) * mm, "end": v(44.64, -3.9) * mm});
            skLineSegment(sketch, "E1477", {"start": v(44.64, -3.9) * mm, "end": v(44.45, -3.96) * mm});
            skLineSegment(sketch, "E1478", {"start": v(44.45, -3.96) * mm, "end": v(44.27, -4.03) * mm});
            skLineSegment(sketch, "E1479", {"start": v(44.27, -4.03) * mm, "end": v(44.09, -4.1) * mm});
            skLineSegment(sketch, "E1480", {"start": v(44.09, -4.1) * mm, "end": v(43.92, -4.18) * mm});
            skLineSegment(sketch, "E1481", {"start": v(43.92, -4.18) * mm, "end": v(43.75, -4.27) * mm});
            skLineSegment(sketch, "E1482", {"start": v(43.75, -4.27) * mm, "end": v(43.58, -4.37) * mm});
            skLineSegment(sketch, "E1483", {"start": v(43.58, -4.37) * mm, "end": v(43.43, -4.48) * mm});
            skLineSegment(sketch, "E1484", {"start": v(43.43, -4.48) * mm, "end": v(43.27, -4.6) * mm});
            skLineSegment(sketch, "E1485", {"start": v(43.27, -4.6) * mm, "end": v(43.12, -4.73) * mm});
            skLineSegment(sketch, "E1486", {"start": v(43.12, -4.73) * mm, "end": v(42.98, -4.86) * mm});
            skLineSegment(sketch, "E1487", {"start": v(42.98, -4.86) * mm, "end": v(42.84, -5) * mm});
            skLineSegment(sketch, "E1488", {"start": v(42.84, -5) * mm, "end": v(42.71, -5.15) * mm});
            skLineSegment(sketch, "E1489", {"start": v(42.71, -5.15) * mm, "end": v(42.6, -5.3) * mm});
            skLineSegment(sketch, "E1490", {"start": v(42.6, -5.3) * mm, "end": v(42.48, -5.45) * mm});
            skLineSegment(sketch, "E1491", {"start": v(42.48, -5.45) * mm, "end": v(42.38, -5.62) * mm});
            skLineSegment(sketch, "E1492", {"start": v(42.38, -5.62) * mm, "end": v(42.28, -5.78) * mm});
            skLineSegment(sketch, "E1493", {"start": v(42.28, -5.78) * mm, "end": v(42.2, -5.95) * mm});
            skLineSegment(sketch, "E1494", {"start": v(42.2, -5.95) * mm, "end": v(42.12, -6.13) * mm});
            skLineSegment(sketch, "E1495", {"start": v(42.12, -6.13) * mm, "end": v(42.06, -6.31) * mm});
            skLineSegment(sketch, "E1496", {"start": v(42.06, -6.31) * mm, "end": v(42, -6.5) * mm});
            skLineSegment(sketch, "E1497", {"start": v(42, -6.5) * mm, "end": v(41.95, -6.69) * mm});
            skLineSegment(sketch, "E1498", {"start": v(41.95, -6.69) * mm, "end": v(41.9, -6.88) * mm});
            skLineSegment(sketch, "E1499", {"start": v(41.9, -6.88) * mm, "end": v(41.88, -7.08) * mm});
            skLineSegment(sketch, "E1500", {"start": v(41.88, -7.08) * mm, "end": v(41.85, -7.29) * mm});
            skLineSegment(sketch, "E1501", {"start": v(41.85, -7.29) * mm, "end": v(41.84, -7.5) * mm});
            skLineSegment(sketch, "E1502", {"start": v(41.84, -7.5) * mm, "end": v(41.84, -7.7) * mm});
            skLineSegment(sketch, "E1503", {"start": v(41.84, -7.7) * mm, "end": v(41.84, -24.27) * mm});
            skLineSegment(sketch, "E1504", {"start": v(41.84, -24.27) * mm, "end": v(41.85, -24.5) * mm});
            skLineSegment(sketch, "E1505", {"start": v(41.85, -24.5) * mm, "end": v(41.88, -24.72) * mm});
            skLineSegment(sketch, "E1506", {"start": v(41.88, -24.72) * mm, "end": v(41.94, -24.93) * mm});
            skLineSegment(sketch, "E1507", {"start": v(41.94, -24.93) * mm, "end": v(42.01, -25.13) * mm});
            skLineSegment(sketch, "E1508", {"start": v(42.01, -25.13) * mm, "end": v(42.1, -25.33) * mm});
            skLineSegment(sketch, "E1509", {"start": v(42.1, -25.33) * mm, "end": v(42.22, -25.5) * mm});
            skLineSegment(sketch, "E1510", {"start": v(42.22, -25.5) * mm, "end": v(42.34, -25.68) * mm});
            skLineSegment(sketch, "E1511", {"start": v(42.34, -25.68) * mm, "end": v(42.49, -25.84) * mm});
            skLineSegment(sketch, "E1512", {"start": v(42.49, -25.84) * mm, "end": v(42.64, -25.98) * mm});
            skLineSegment(sketch, "E1513", {"start": v(42.64, -25.98) * mm, "end": v(42.81, -26.1) * mm});
            skLineSegment(sketch, "E1514", {"start": v(42.81, -26.1) * mm, "end": v(43, -26.22) * mm});
            skLineSegment(sketch, "E1515", {"start": v(43, -26.22) * mm, "end": v(43.2, -26.31) * mm});
            skLineSegment(sketch, "E1516", {"start": v(43.2, -26.31) * mm, "end": v(43.4, -26.39) * mm});
            skLineSegment(sketch, "E1517", {"start": v(43.4, -26.39) * mm, "end": v(43.6, -26.44) * mm});
            skLineSegment(sketch, "E1518", {"start": v(43.6, -26.44) * mm, "end": v(43.83, -26.48) * mm});
            skLineSegment(sketch, "E1519", {"start": v(43.83, -26.48) * mm, "end": v(44.05, -26.49) * mm});
            skLineSegment(sketch, "E1520", {"start": v(44.05, -26.49) * mm, "end": v(80.72, -26.49) * mm});
            skLineSegment(sketch, "E1521", {"start": v(80.72, -26.49) * mm, "end": v(81.07, -26.48) * mm});
            skLineSegment(sketch, "E1522", {"start": v(81.07, -26.48) * mm, "end": v(81.42, -26.46) * mm});
            skLineSegment(sketch, "E1523", {"start": v(81.42, -26.46) * mm, "end": v(81.75, -26.42) * mm});
            skLineSegment(sketch, "E1524", {"start": v(81.75, -26.42) * mm, "end": v(82.08, -26.38) * mm});
            skLineSegment(sketch, "E1525", {"start": v(82.08, -26.38) * mm, "end": v(82.4, -26.31) * mm});
            skLineSegment(sketch, "E1526", {"start": v(82.4, -26.31) * mm, "end": v(82.7, -26.23) * mm});
            skLineSegment(sketch, "E1527", {"start": v(82.7, -26.23) * mm, "end": v(83.01, -26.14) * mm});
            skLineSegment(sketch, "E1528", {"start": v(83.01, -26.14) * mm, "end": v(83.3, -26.04) * mm});
            skLineSegment(sketch, "E1529", {"start": v(83.3, -26.04) * mm, "end": v(83.6, -25.92) * mm});
            skLineSegment(sketch, "E1530", {"start": v(83.6, -25.92) * mm, "end": v(83.87, -25.78) * mm});
            skLineSegment(sketch, "E1531", {"start": v(83.87, -25.78) * mm, "end": v(84.14, -25.63) * mm});
            skLineSegment(sketch, "E1532", {"start": v(84.14, -25.63) * mm, "end": v(84.4, -25.47) * mm});
            skLineSegment(sketch, "E1533", {"start": v(84.4, -25.47) * mm, "end": v(84.66, -25.3) * mm});
            skLineSegment(sketch, "E1534", {"start": v(84.66, -25.3) * mm, "end": v(84.9, -25.1) * mm});
            skLineSegment(sketch, "E1535", {"start": v(84.9, -25.1) * mm, "end": v(85.14, -24.9) * mm});
            skLineSegment(sketch, "E1536", {"start": v(85.14, -24.9) * mm, "end": v(85.37, -24.69) * mm});
            skLineSegment(sketch, "E1537", {"start": v(85.37, -24.69) * mm, "end": v(85.59, -24.46) * mm});
            skLineSegment(sketch, "E1538", {"start": v(85.59, -24.46) * mm, "end": v(85.8, -24.22) * mm});
            skLineSegment(sketch, "E1539", {"start": v(85.8, -24.22) * mm, "end": v(85.98, -23.98) * mm});
            skLineSegment(sketch, "E1540", {"start": v(85.98, -23.98) * mm, "end": v(86.16, -23.72) * mm});
            skLineSegment(sketch, "E1541", {"start": v(86.16, -23.72) * mm, "end": v(86.32, -23.46) * mm});
            skLineSegment(sketch, "E1542", {"start": v(86.32, -23.46) * mm, "end": v(86.47, -23.19) * mm});
            skLineSegment(sketch, "E1543", {"start": v(86.47, -23.19) * mm, "end": v(86.6, -22.9) * mm});
            skLineSegment(sketch, "E1544", {"start": v(86.6, -22.9) * mm, "end": v(86.72, -22.62) * mm});
            skLineSegment(sketch, "E1545", {"start": v(86.72, -22.62) * mm, "end": v(86.83, -22.33) * mm});
            skLineSegment(sketch, "E1546", {"start": v(86.83, -22.33) * mm, "end": v(86.92, -22.02) * mm});
            skLineSegment(sketch, "E1547", {"start": v(86.92, -22.02) * mm, "end": v(87, -21.71) * mm});
            skLineSegment(sketch, "E1548", {"start": v(87, -21.71) * mm, "end": v(87.06, -21.4) * mm});
            skLineSegment(sketch, "E1549", {"start": v(87.06, -21.4) * mm, "end": v(87.1, -21.07) * mm});
            skLineSegment(sketch, "E1550", {"start": v(87.1, -21.07) * mm, "end": v(87.15, -20.73) * mm});
            skLineSegment(sketch, "E1551", {"start": v(87.15, -20.73) * mm, "end": v(87.17, -20.39) * mm});
            skLineSegment(sketch, "E1552", {"start": v(87.17, -20.39) * mm, "end": v(87.17, -20.04) * mm});
            skLineSegment(sketch, "E1553", {"start": v(87.17, -20.04) * mm, "end": v(87.17, 7.99) * mm});
            skLineSegment(sketch, "E1554", {"start": v(87.17, 7.99) * mm, "end": v(87.16, 8.3) * mm});
            skLineSegment(sketch, "E1555", {"start": v(87.16, 8.3) * mm, "end": v(87.1, 8.62) * mm});
            skLineSegment(sketch, "E1556", {"start": v(87.1, 8.62) * mm, "end": v(87.03, 8.92) * mm});
            skLineSegment(sketch, "E1557", {"start": v(87.03, 8.92) * mm, "end": v(86.93, 9.2) * mm});
            skLineSegment(sketch, "E1558", {"start": v(86.93, 9.2) * mm, "end": v(86.8, 9.48) * mm});
            skLineSegment(sketch, "E1559", {"start": v(86.8, 9.48) * mm, "end": v(86.64, 9.74) * mm});
            skLineSegment(sketch, "E1560", {"start": v(86.64, 9.74) * mm, "end": v(86.46, 9.98) * mm});
            skLineSegment(sketch, "E1561", {"start": v(86.46, 9.98) * mm, "end": v(86.25, 10.2) * mm});
            skLineSegment(sketch, "E1562", {"start": v(86.25, 10.2) * mm, "end": v(86.03, 10.4) * mm});
            skLineSegment(sketch, "E1563", {"start": v(86.03, 10.4) * mm, "end": v(85.8, 10.59) * mm});
            skLineSegment(sketch, "E1564", {"start": v(85.8, 10.59) * mm, "end": v(85.53, 10.74) * mm});
            skLineSegment(sketch, "E1565", {"start": v(85.53, 10.74) * mm, "end": v(85.26, 10.88) * mm});
            skLineSegment(sketch, "E1566", {"start": v(85.26, 10.88) * mm, "end": v(84.97, 10.98) * mm});
            skLineSegment(sketch, "E1567", {"start": v(84.97, 10.98) * mm, "end": v(84.67, 11.06) * mm});
            skLineSegment(sketch, "E1568", {"start": v(84.67, 11.06) * mm, "end": v(84.36, 11.1) * mm});
            skLineSegment(sketch, "E1569", {"start": v(84.36, 11.1) * mm, "end": v(84.04, 11.12) * mm});
            skLineSegment(sketch, "E1570", {"start": v(84.04, 11.12) * mm, "end": v(73.32, 11.12) * mm});
            skLineSegment(sketch, "E1571", {"start": v(73.32, 11.12) * mm, "end": v(73.2, 11.13) * mm});
            skLineSegment(sketch, "E1572", {"start": v(73.2, 11.13) * mm, "end": v(73.07, 11.14) * mm});
            skLineSegment(sketch, "E1573", {"start": v(73.07, 11.14) * mm, "end": v(72.97, 11.16) * mm});
            skLineSegment(sketch, "E1574", {"start": v(72.97, 11.16) * mm, "end": v(72.87, 11.18) * mm});
            skLineSegment(sketch, "E1575", {"start": v(72.87, 11.18) * mm, "end": v(72.77, 11.21) * mm});
            skLineSegment(sketch, "E1576", {"start": v(72.77, 11.21) * mm, "end": v(72.7, 11.25) * mm});
            skLineSegment(sketch, "E1577", {"start": v(72.7, 11.25) * mm, "end": v(72.62, 11.3) * mm});
            skLineSegment(sketch, "E1578", {"start": v(72.62, 11.3) * mm, "end": v(72.55, 11.36) * mm});
            skLineSegment(sketch, "E1579", {"start": v(72.55, 11.36) * mm, "end": v(72.5, 11.42) * mm});
            skLineSegment(sketch, "E1580", {"start": v(72.5, 11.42) * mm, "end": v(72.44, 11.5) * mm});
            skLineSegment(sketch, "E1581", {"start": v(72.44, 11.5) * mm, "end": v(72.4, 11.57) * mm});
            skLineSegment(sketch, "E1582", {"start": v(72.4, 11.57) * mm, "end": v(72.36, 11.66) * mm});
            skLineSegment(sketch, "E1583", {"start": v(72.36, 11.66) * mm, "end": v(72.34, 11.75) * mm});
            skLineSegment(sketch, "E1584", {"start": v(72.34, 11.75) * mm, "end": v(72.32, 11.85) * mm});
            skLineSegment(sketch, "E1585", {"start": v(72.32, 11.85) * mm, "end": v(72.3, 11.96) * mm});
            skLineSegment(sketch, "E1586", {"start": v(72.3, 11.96) * mm, "end": v(72.3, 12.08) * mm});
            skLineSegment(sketch, "E1587", {"start": v(72.3, 12.08) * mm, "end": v(72.3, 12.2) * mm});
            skLineSegment(sketch, "E1588", {"start": v(72.3, 12.2) * mm, "end": v(72.32, 12.31) * mm});
            skLineSegment(sketch, "E1589", {"start": v(72.32, 12.31) * mm, "end": v(72.34, 12.41) * mm});
            skLineSegment(sketch, "E1590", {"start": v(72.34, 12.41) * mm, "end": v(72.36, 12.5) * mm});
            skLineSegment(sketch, "E1591", {"start": v(72.36, 12.5) * mm, "end": v(72.4, 12.6) * mm});
            skLineSegment(sketch, "E1592", {"start": v(72.4, 12.6) * mm, "end": v(72.44, 12.67) * mm});
            skLineSegment(sketch, "E1593", {"start": v(72.44, 12.67) * mm, "end": v(72.5, 12.74) * mm});
            skLineSegment(sketch, "E1594", {"start": v(72.5, 12.74) * mm, "end": v(72.55, 12.8) * mm});
            skLineSegment(sketch, "E1595", {"start": v(72.55, 12.8) * mm, "end": v(72.62, 12.86) * mm});
            skLineSegment(sketch, "E1596", {"start": v(72.62, 12.86) * mm, "end": v(72.7, 12.9) * mm});
            skLineSegment(sketch, "E1597", {"start": v(72.7, 12.9) * mm, "end": v(72.77, 12.95) * mm});
            skLineSegment(sketch, "E1598", {"start": v(72.77, 12.95) * mm, "end": v(72.87, 12.98) * mm});
            skLineSegment(sketch, "E1599", {"start": v(72.87, 12.98) * mm, "end": v(72.97, 13) * mm});
            skLineSegment(sketch, "E1600", {"start": v(72.97, 13) * mm, "end": v(73.07, 13.03) * mm});
            skLineSegment(sketch, "E1601", {"start": v(73.07, 13.03) * mm, "end": v(73.2, 13.04) * mm});
            skLineSegment(sketch, "E1602", {"start": v(73.2, 13.04) * mm, "end": v(73.32, 13.04) * mm});
            skLineSegment(sketch, "E1603", {"start": v(73.32, 13.04) * mm, "end": v(102.95, 13.04) * mm});
            skLineSegment(sketch, "E1604", {"start": v(102.95, 13.04) * mm, "end": v(103.07, 13.04) * mm});
            skLineSegment(sketch, "E1605", {"start": v(103.07, 13.04) * mm, "end": v(103.2, 13.03) * mm});
            skLineSegment(sketch, "E1606", {"start": v(103.2, 13.03) * mm, "end": v(103.3, 13) * mm});
            skLineSegment(sketch, "E1607", {"start": v(103.3, 13) * mm, "end": v(103.4, 12.98) * mm});
            skLineSegment(sketch, "E1608", {"start": v(103.4, 12.98) * mm, "end": v(103.49, 12.95) * mm});
            skLineSegment(sketch, "E1609", {"start": v(103.49, 12.95) * mm, "end": v(103.57, 12.9) * mm});
            skLineSegment(sketch, "E1610", {"start": v(103.57, 12.9) * mm, "end": v(103.65, 12.86) * mm});
            skLineSegment(sketch, "E1611", {"start": v(103.65, 12.86) * mm, "end": v(103.71, 12.8) * mm});
            skLineSegment(sketch, "E1612", {"start": v(103.71, 12.8) * mm, "end": v(103.77, 12.74) * mm});
            skLineSegment(sketch, "E1613", {"start": v(103.77, 12.74) * mm, "end": v(103.82, 12.67) * mm});
            skLineSegment(sketch, "E1614", {"start": v(103.82, 12.67) * mm, "end": v(103.86, 12.6) * mm});
            skLineSegment(sketch, "E1615", {"start": v(103.86, 12.6) * mm, "end": v(103.9, 12.5) * mm});
            skLineSegment(sketch, "E1616", {"start": v(103.9, 12.5) * mm, "end": v(103.93, 12.41) * mm});
            skLineSegment(sketch, "E1617", {"start": v(103.93, 12.41) * mm, "end": v(103.94, 12.31) * mm});
            skLineSegment(sketch, "E1618", {"start": v(103.94, 12.31) * mm, "end": v(103.96, 12.2) * mm});
            skLineSegment(sketch, "E1619", {"start": v(103.96, 12.2) * mm, "end": v(103.96, 12.08) * mm});
            skLineSegment(sketch, "E1620", {"start": v(103.96, 12.08) * mm, "end": v(103.96, 11.96) * mm});
            skLineSegment(sketch, "E1621", {"start": v(103.96, 11.96) * mm, "end": v(103.94, 11.85) * mm});
            skLineSegment(sketch, "E1622", {"start": v(103.94, 11.85) * mm, "end": v(103.93, 11.75) * mm});
            skLineSegment(sketch, "E1623", {"start": v(103.93, 11.75) * mm, "end": v(103.9, 11.66) * mm});
            skLineSegment(sketch, "E1624", {"start": v(103.9, 11.66) * mm, "end": v(103.86, 11.57) * mm});
            skLineSegment(sketch, "E1625", {"start": v(103.86, 11.57) * mm, "end": v(103.82, 11.5) * mm});
            skLineSegment(sketch, "E1626", {"start": v(103.82, 11.5) * mm, "end": v(103.77, 11.42) * mm});
            skLineSegment(sketch, "E1627", {"start": v(103.77, 11.42) * mm, "end": v(103.71, 11.36) * mm});
            skLineSegment(sketch, "E1628", {"start": v(103.71, 11.36) * mm, "end": v(103.65, 11.3) * mm});
            skLineSegment(sketch, "E1629", {"start": v(103.65, 11.3) * mm, "end": v(103.57, 11.25) * mm});
            skLineSegment(sketch, "E1630", {"start": v(103.57, 11.25) * mm, "end": v(103.49, 11.21) * mm});
            skLineSegment(sketch, "E1631", {"start": v(103.49, 11.21) * mm, "end": v(103.4, 11.18) * mm});
            skLineSegment(sketch, "E1632", {"start": v(103.4, 11.18) * mm, "end": v(103.3, 11.16) * mm});
            skLineSegment(sketch, "E1633", {"start": v(103.3, 11.16) * mm, "end": v(103.2, 11.14) * mm});
            skLineSegment(sketch, "E1634", {"start": v(103.2, 11.14) * mm, "end": v(103.07, 11.13) * mm});
            skLineSegment(sketch, "E1635", {"start": v(103.07, 11.13) * mm, "end": v(102.95, 11.12) * mm});
            skLineSegment(sketch, "E1636", {"start": v(102.95, 11.12) * mm, "end": v(92.22, 11.12) * mm});
            skLineSegment(sketch, "E1637", {"start": v(92.22, 11.12) * mm, "end": v(91.9, 11.1) * mm});
            skLineSegment(sketch, "E1638", {"start": v(91.9, 11.1) * mm, "end": v(91.6, 11.06) * mm});
            skLineSegment(sketch, "E1639", {"start": v(91.6, 11.06) * mm, "end": v(91.3, 10.98) * mm});
            skLineSegment(sketch, "E1640", {"start": v(91.3, 10.98) * mm, "end": v(91, 10.88) * mm});
            skLineSegment(sketch, "E1641", {"start": v(91, 10.88) * mm, "end": v(90.73, 10.74) * mm});
            skLineSegment(sketch, "E1642", {"start": v(90.73, 10.74) * mm, "end": v(90.47, 10.59) * mm});
            skLineSegment(sketch, "E1643", {"start": v(90.47, 10.59) * mm, "end": v(90.23, 10.4) * mm});
            skLineSegment(sketch, "E1644", {"start": v(90.23, 10.4) * mm, "end": v(90, 10.2) * mm});
            skLineSegment(sketch, "E1645", {"start": v(90, 10.2) * mm, "end": v(89.8, 9.98) * mm});
            skLineSegment(sketch, "E1646", {"start": v(89.8, 9.98) * mm, "end": v(89.63, 9.74) * mm});
            skLineSegment(sketch, "E1647", {"start": v(89.63, 9.74) * mm, "end": v(89.47, 9.48) * mm});
            skLineSegment(sketch, "E1648", {"start": v(89.47, 9.48) * mm, "end": v(89.34, 9.2) * mm});
            skLineSegment(sketch, "E1649", {"start": v(89.34, 9.2) * mm, "end": v(89.23, 8.92) * mm});
            skLineSegment(sketch, "E1650", {"start": v(89.23, 8.92) * mm, "end": v(89.15, 8.62) * mm});
            skLineSegment(sketch, "E1651", {"start": v(89.15, 8.62) * mm, "end": v(89.1, 8.3) * mm});
            skLineSegment(sketch, "E1652", {"start": v(89.1, 8.3) * mm, "end": v(89.1, 7.99) * mm});
            skLineSegment(sketch, "E1653", {"start": v(89.1, 7.99) * mm, "end": v(89.1, -20.04) * mm});
            skLineSegment(sketch, "E1654", {"start": v(89.1, -20.04) * mm, "end": v(89.1, -20.38) * mm});
            skLineSegment(sketch, "E1655", {"start": v(89.1, -20.38) * mm, "end": v(89.12, -20.72) * mm});
            skLineSegment(sketch, "E1656", {"start": v(89.12, -20.72) * mm, "end": v(89.16, -21.05) * mm});
            skLineSegment(sketch, "E1657", {"start": v(89.16, -21.05) * mm, "end": v(89.2, -21.37) * mm});
            skLineSegment(sketch, "E1658", {"start": v(89.2, -21.37) * mm, "end": v(89.27, -21.69) * mm});
            skLineSegment(sketch, "E1659", {"start": v(89.27, -21.69) * mm, "end": v(89.35, -22) * mm});
            skLineSegment(sketch, "E1660", {"start": v(89.35, -22) * mm, "end": v(89.44, -22.3) * mm});
            skLineSegment(sketch, "E1661", {"start": v(89.44, -22.3) * mm, "end": v(89.55, -22.6) * mm});
            skLineSegment(sketch, "E1662", {"start": v(89.55, -22.6) * mm, "end": v(89.67, -22.88) * mm});
            skLineSegment(sketch, "E1663", {"start": v(89.67, -22.88) * mm, "end": v(89.8, -23.15) * mm});
            skLineSegment(sketch, "E1664", {"start": v(89.8, -23.15) * mm, "end": v(89.96, -23.42) * mm});
            skLineSegment(sketch, "E1665", {"start": v(89.96, -23.42) * mm, "end": v(90.12, -23.69) * mm});
            skLineSegment(sketch, "E1666", {"start": v(90.12, -23.69) * mm, "end": v(90.3, -23.94) * mm});
            skLineSegment(sketch, "E1667", {"start": v(90.3, -23.94) * mm, "end": v(90.5, -24.19) * mm});
            skLineSegment(sketch, "E1668", {"start": v(90.5, -24.19) * mm, "end": v(90.7, -24.43) * mm});
            skLineSegment(sketch, "E1669", {"start": v(90.7, -24.43) * mm, "end": v(90.92, -24.66) * mm});
            skLineSegment(sketch, "E1670", {"start": v(90.92, -24.66) * mm, "end": v(91.15, -24.88) * mm});
            skLineSegment(sketch, "E1671", {"start": v(91.15, -24.88) * mm, "end": v(91.39, -25.09) * mm});
            skLineSegment(sketch, "E1672", {"start": v(91.39, -25.09) * mm, "end": v(91.64, -25.28) * mm});
            skLineSegment(sketch, "E1673", {"start": v(91.64, -25.28) * mm, "end": v(91.9, -25.46) * mm});
            skLineSegment(sketch, "E1674", {"start": v(91.9, -25.46) * mm, "end": v(92.15, -25.62) * mm});
            skLineSegment(sketch, "E1675", {"start": v(92.15, -25.62) * mm, "end": v(92.42, -25.77) * mm});
            skLineSegment(sketch, "E1676", {"start": v(92.42, -25.77) * mm, "end": v(92.7, -25.9) * mm});
            skLineSegment(sketch, "E1677", {"start": v(92.7, -25.9) * mm, "end": v(92.99, -26.03) * mm});
            skLineSegment(sketch, "E1678", {"start": v(92.99, -26.03) * mm, "end": v(93.28, -26.14) * mm});
            skLineSegment(sketch, "E1679", {"start": v(93.28, -26.14) * mm, "end": v(93.58, -26.23) * mm});
            skLineSegment(sketch, "E1680", {"start": v(93.58, -26.23) * mm, "end": v(93.9, -26.3) * mm});
            skLineSegment(sketch, "E1681", {"start": v(93.9, -26.3) * mm, "end": v(94.2, -26.37) * mm});
            skLineSegment(sketch, "E1682", {"start": v(94.2, -26.37) * mm, "end": v(94.53, -26.42) * mm});
            skLineSegment(sketch, "E1683", {"start": v(94.53, -26.42) * mm, "end": v(94.86, -26.46) * mm});
            skLineSegment(sketch, "E1684", {"start": v(94.86, -26.46) * mm, "end": v(95.2, -26.48) * mm});
            skLineSegment(sketch, "E1685", {"start": v(95.2, -26.48) * mm, "end": v(95.54, -26.49) * mm});
            skLineSegment(sketch, "E1686", {"start": v(95.54, -26.49) * mm, "end": v(126.33, -26.49) * mm});
            skLineSegment(sketch, "E1687", {"start": v(126.33, -26.49) * mm, "end": v(126.67, -26.47) * mm});
            skLineSegment(sketch, "E1688", {"start": v(126.67, -26.47) * mm, "end": v(127, -26.42) * mm});
            skLineSegment(sketch, "E1689", {"start": v(127, -26.42) * mm, "end": v(127.32, -26.34) * mm});
            skLineSegment(sketch, "E1690", {"start": v(127.32, -26.34) * mm, "end": v(127.63, -26.23) * mm});
            skLineSegment(sketch, "E1691", {"start": v(127.63, -26.23) * mm, "end": v(127.92, -26.09) * mm});
            skLineSegment(sketch, "E1692", {"start": v(127.92, -26.09) * mm, "end": v(128.2, -25.92) * mm});
            skLineSegment(sketch, "E1693", {"start": v(128.2, -25.92) * mm, "end": v(128.45, -25.73) * mm});
            skLineSegment(sketch, "E1694", {"start": v(128.45, -25.73) * mm, "end": v(128.69, -25.51) * mm});
            skLineSegment(sketch, "E1695", {"start": v(128.69, -25.51) * mm, "end": v(128.9, -25.27) * mm});
            skLineSegment(sketch, "E1696", {"start": v(128.9, -25.27) * mm, "end": v(129.1, -25.02) * mm});
            skLineSegment(sketch, "E1697", {"start": v(129.1, -25.02) * mm, "end": v(129.26, -24.74) * mm});
            skLineSegment(sketch, "E1698", {"start": v(129.26, -24.74) * mm, "end": v(129.4, -24.45) * mm});
            skLineSegment(sketch, "E1699", {"start": v(129.4, -24.45) * mm, "end": v(129.52, -24.14) * mm});
            skLineSegment(sketch, "E1700", {"start": v(129.52, -24.14) * mm, "end": v(129.6, -23.83) * mm});
            skLineSegment(sketch, "E1701", {"start": v(129.6, -23.83) * mm, "end": v(129.65, -23.5) * mm});
            skLineSegment(sketch, "E1702", {"start": v(129.65, -23.5) * mm, "end": v(129.67, -23.15) * mm});
            skLineSegment(sketch, "E1703", {"start": v(129.67, -23.15) * mm, "end": v(129.67, -19.84) * mm});
            skLineSegment(sketch, "E1704", {"start": v(129.67, -19.84) * mm, "end": v(129.66, -19.7) * mm});
            skLineSegment(sketch, "E1705", {"start": v(129.66, -19.7) * mm, "end": v(129.64, -19.56) * mm});
            skLineSegment(sketch, "E1706", {"start": v(129.64, -19.56) * mm, "end": v(129.6, -19.43) * mm});
            skLineSegment(sketch, "E1707", {"start": v(129.6, -19.43) * mm, "end": v(129.57, -19.3) * mm});
            skLineSegment(sketch, "E1708", {"start": v(129.57, -19.3) * mm, "end": v(129.51, -19.18) * mm});
            skLineSegment(sketch, "E1709", {"start": v(129.51, -19.18) * mm, "end": v(129.45, -19.06) * mm});
            skLineSegment(sketch, "E1710", {"start": v(129.45, -19.06) * mm, "end": v(129.37, -18.95) * mm});
            skLineSegment(sketch, "E1711", {"start": v(129.37, -18.95) * mm, "end": v(129.3, -18.85) * mm});
            skLineSegment(sketch, "E1712", {"start": v(129.3, -18.85) * mm, "end": v(129.2, -18.75) * mm});
            skLineSegment(sketch, "E1713", {"start": v(129.2, -18.75) * mm, "end": v(129.1, -18.67) * mm});
            skLineSegment(sketch, "E1714", {"start": v(129.1, -18.67) * mm, "end": v(129, -18.59) * mm});
            skLineSegment(sketch, "E1715", {"start": v(129, -18.59) * mm, "end": v(128.88, -18.52) * mm});
            skLineSegment(sketch, "E1716", {"start": v(128.88, -18.52) * mm, "end": v(128.76, -18.46) * mm});
            skLineSegment(sketch, "E1717", {"start": v(128.76, -18.46) * mm, "end": v(128.63, -18.41) * mm});
            skLineSegment(sketch, "E1718", {"start": v(128.63, -18.41) * mm, "end": v(128.5, -18.38) * mm});
            skLineSegment(sketch, "E1719", {"start": v(128.5, -18.38) * mm, "end": v(128.36, -18.35) * mm});
            skLineSegment(sketch, "E1720", {"start": v(128.36, -18.35) * mm, "end": v(127.64, -18.25) * mm});
            skLineSegment(sketch, "E1721", {"start": v(127.64, -18.25) * mm, "end": v(126.94, -18.1) * mm});
            skLineSegment(sketch, "E1722", {"start": v(126.94, -18.1) * mm, "end": v(126.25, -17.94) * mm});
            skLineSegment(sketch, "E1723", {"start": v(126.25, -17.94) * mm, "end": v(125.57, -17.74) * mm});
            skLineSegment(sketch, "E1724", {"start": v(125.57, -17.74) * mm, "end": v(124.9, -17.52) * mm});
            skLineSegment(sketch, "E1725", {"start": v(124.9, -17.52) * mm, "end": v(124.26, -17.26) * mm});
            skLineSegment(sketch, "E1726", {"start": v(124.26, -17.26) * mm, "end": v(123.63, -16.97) * mm});
            skLineSegment(sketch, "E1727", {"start": v(123.63, -16.97) * mm, "end": v(123.01, -16.66) * mm});
            skLineSegment(sketch, "E1728", {"start": v(123.01, -16.66) * mm, "end": v(122.41, -16.31) * mm});
            skLineSegment(sketch, "E1729", {"start": v(122.41, -16.31) * mm, "end": v(121.83, -15.94) * mm});
            skLineSegment(sketch, "E1730", {"start": v(121.83, -15.94) * mm, "end": v(121.25, -15.53) * mm});
            skLineSegment(sketch, "E1731", {"start": v(121.25, -15.53) * mm, "end": v(120.7, -15.1) * mm});
            skLineSegment(sketch, "E1732", {"start": v(120.7, -15.1) * mm, "end": v(120.16, -14.63) * mm});
            skLineSegment(sketch, "E1733", {"start": v(120.16, -14.63) * mm, "end": v(119.63, -14.14) * mm});
            skLineSegment(sketch, "E1734", {"start": v(119.63, -14.14) * mm, "end": v(119.13, -13.62) * mm});
            skLineSegment(sketch, "E1735", {"start": v(119.13, -13.62) * mm, "end": v(118.63, -13.07) * mm});
            skLineSegment(sketch, "E1736", {"start": v(118.63, -13.07) * mm, "end": v(118.17, -12.5) * mm});
            skLineSegment(sketch, "E1737", {"start": v(118.17, -12.5) * mm, "end": v(117.73, -11.91) * mm});
            skLineSegment(sketch, "E1738", {"start": v(117.73, -11.91) * mm, "end": v(117.32, -11.32) * mm});
            skLineSegment(sketch, "E1739", {"start": v(117.32, -11.32) * mm, "end": v(116.94, -10.71) * mm});
            skLineSegment(sketch, "E1740", {"start": v(116.94, -10.71) * mm, "end": v(116.59, -10.1) * mm});
            skLineSegment(sketch, "E1741", {"start": v(116.59, -10.1) * mm, "end": v(116.27, -9.47) * mm});
            skLineSegment(sketch, "E1742", {"start": v(116.27, -9.47) * mm, "end": v(115.98, -8.83) * mm});
            skLineSegment(sketch, "E1743", {"start": v(115.98, -8.83) * mm, "end": v(115.72, -8.18) * mm});
            skLineSegment(sketch, "E1744", {"start": v(115.72, -8.18) * mm, "end": v(115.5, -7.52) * mm});
            skLineSegment(sketch, "E1745", {"start": v(115.5, -7.52) * mm, "end": v(115.3, -6.85) * mm});
            skLineSegment(sketch, "E1746", {"start": v(115.3, -6.85) * mm, "end": v(115.13, -6.17) * mm});
            skLineSegment(sketch, "E1747", {"start": v(115.13, -6.17) * mm, "end": v(114.99, -5.49) * mm});
            skLineSegment(sketch, "E1748", {"start": v(114.99, -5.49) * mm, "end": v(114.88, -4.79) * mm});
            skLineSegment(sketch, "E1749", {"start": v(114.88, -4.79) * mm, "end": v(114.8, -4.08) * mm});
            skLineSegment(sketch, "E1750", {"start": v(114.8, -4.08) * mm, "end": v(114.76, -3.36) * mm});
            skLineSegment(sketch, "E1751", {"start": v(114.76, -3.36) * mm, "end": v(114.74, -2.63) * mm});
            skLineSegment(sketch, "E1752", {"start": v(114.74, -2.63) * mm, "end": v(114.76, -1.81) * mm});
            skLineSegment(sketch, "E1753", {"start": v(114.76, -1.81) * mm, "end": v(114.82, -1) * mm});
            skLineSegment(sketch, "E1754", {"start": v(114.82, -1) * mm, "end": v(114.9, -0.22) * mm});
            skLineSegment(sketch, "E1755", {"start": v(114.9, -0.22) * mm, "end": v(115.03, 0.55) * mm});
            skLineSegment(sketch, "E1756", {"start": v(115.03, 0.55) * mm, "end": v(115.2, 1.31) * mm});
            skLineSegment(sketch, "E1757", {"start": v(115.2, 1.31) * mm, "end": v(115.4, 2.06) * mm});
            skLineSegment(sketch, "E1758", {"start": v(115.4, 2.06) * mm, "end": v(115.63, 2.79) * mm});
            skLineSegment(sketch, "E1759", {"start": v(115.63, 2.79) * mm, "end": v(115.9, 3.5) * mm});
            skLineSegment(sketch, "E1760", {"start": v(115.9, 3.5) * mm, "end": v(116.21, 4.2) * mm});
            skLineSegment(sketch, "E1761", {"start": v(116.21, 4.2) * mm, "end": v(116.56, 4.88) * mm});
            skLineSegment(sketch, "E1762", {"start": v(116.56, 4.88) * mm, "end": v(116.94, 5.55) * mm});
            skLineSegment(sketch, "E1763", {"start": v(116.94, 5.55) * mm, "end": v(117.35, 6.2) * mm});
            skLineSegment(sketch, "E1764", {"start": v(117.35, 6.2) * mm, "end": v(117.8, 6.84) * mm});
            skLineSegment(sketch, "E1765", {"start": v(117.8, 6.84) * mm, "end": v(118.3, 7.46) * mm});
            skLineSegment(sketch, "E1766", {"start": v(118.3, 7.46) * mm, "end": v(118.81, 8.06) * mm});
            skLineSegment(sketch, "E1767", {"start": v(118.81, 8.06) * mm, "end": v(119.37, 8.65) * mm});
            skLineSegment(sketch, "E1768", {"start": v(119.37, 8.65) * mm, "end": v(119.95, 9.21) * mm});
            skLineSegment(sketch, "E1769", {"start": v(119.95, 9.21) * mm, "end": v(120.56, 9.74) * mm});
            skLineSegment(sketch, "E1770", {"start": v(120.56, 9.74) * mm, "end": v(121.17, 10.23) * mm});
            skLineSegment(sketch, "E1771", {"start": v(121.17, 10.23) * mm, "end": v(121.8, 10.68) * mm});
            skLineSegment(sketch, "E1772", {"start": v(121.8, 10.68) * mm, "end": v(122.46, 11.1) * mm});
            skLineSegment(sketch, "E1773", {"start": v(122.46, 11.1) * mm, "end": v(123.12, 11.48) * mm});
            skLineSegment(sketch, "E1774", {"start": v(123.12, 11.48) * mm, "end": v(123.8, 11.83) * mm});
            skLineSegment(sketch, "E1775", {"start": v(123.8, 11.83) * mm, "end": v(124.5, 12.14) * mm});
            skLineSegment(sketch, "E1776", {"start": v(124.5, 12.14) * mm, "end": v(125.21, 12.4) * mm});
            skLineSegment(sketch, "E1777", {"start": v(125.21, 12.4) * mm, "end": v(125.94, 12.65) * mm});
            skLineSegment(sketch, "E1778", {"start": v(125.94, 12.65) * mm, "end": v(126.68, 12.85) * mm});
            skLineSegment(sketch, "E1779", {"start": v(126.68, 12.85) * mm, "end": v(127.44, 13.01) * mm});
            skLineSegment(sketch, "E1780", {"start": v(127.44, 13.01) * mm, "end": v(128.22, 13.14) * mm});
            skLineSegment(sketch, "E1781", {"start": v(128.22, 13.14) * mm, "end": v(129, 13.23) * mm});
            skLineSegment(sketch, "E1782", {"start": v(129, 13.23) * mm, "end": v(129.8, 13.29) * mm});
            skLineSegment(sketch, "E1783", {"start": v(129.8, 13.29) * mm, "end": v(130.62, 13.3) * mm});
            skLineSegment(sketch, "E1784", {"start": v(130.62, 13.3) * mm, "end": v(131.45, 13.29) * mm});
            skLineSegment(sketch, "E1785", {"start": v(131.45, 13.29) * mm, "end": v(132.26, 13.23) * mm});
            skLineSegment(sketch, "E1786", {"start": v(132.26, 13.23) * mm, "end": v(133.05, 13.14) * mm});
            skLineSegment(sketch, "E1787", {"start": v(133.05, 13.14) * mm, "end": v(133.83, 13.01) * mm});
            skLineSegment(sketch, "E1788", {"start": v(133.83, 13.01) * mm, "end": v(134.6, 12.85) * mm});
            skLineSegment(sketch, "E1789", {"start": v(134.6, 12.85) * mm, "end": v(135.34, 12.65) * mm});
            skLineSegment(sketch, "E1790", {"start": v(135.34, 12.65) * mm, "end": v(136.07, 12.41) * mm});
            skLineSegment(sketch, "E1791", {"start": v(136.07, 12.41) * mm, "end": v(136.79, 12.14) * mm});
            skLineSegment(sketch, "E1792", {"start": v(136.79, 12.14) * mm, "end": v(137.49, 11.83) * mm});
            skLineSegment(sketch, "E1793", {"start": v(137.49, 11.83) * mm, "end": v(138.17, 11.5) * mm});
            skLineSegment(sketch, "E1794", {"start": v(138.17, 11.5) * mm, "end": v(138.84, 11.11) * mm});
            skLineSegment(sketch, "E1795", {"start": v(138.84, 11.11) * mm, "end": v(139.5, 10.7) * mm});
            skLineSegment(sketch, "E1796", {"start": v(139.5, 10.7) * mm, "end": v(140.13, 10.24) * mm});
            skLineSegment(sketch, "E1797", {"start": v(140.13, 10.24) * mm, "end": v(140.74, 9.76) * mm});
            skLineSegment(sketch, "E1798", {"start": v(140.74, 9.76) * mm, "end": v(141.35, 9.24) * mm});
            skLineSegment(sketch, "E1799", {"start": v(141.35, 9.24) * mm, "end": v(141.93, 8.68) * mm});
            skLineSegment(sketch, "E1800", {"start": v(141.93, 8.68) * mm, "end": v(142.49, 8.1) * mm});
            skLineSegment(sketch, "E1801", {"start": v(142.49, 8.1) * mm, "end": v(143.01, 7.5) * mm});
            skLineSegment(sketch, "E1802", {"start": v(143.01, 7.5) * mm, "end": v(143.5, 6.87) * mm});
            skLineSegment(sketch, "E1803", {"start": v(143.5, 6.87) * mm, "end": v(143.95, 6.24) * mm});
            skLineSegment(sketch, "E1804", {"start": v(143.95, 6.24) * mm, "end": v(144.36, 5.59) * mm});
            skLineSegment(sketch, "E1805", {"start": v(144.36, 5.59) * mm, "end": v(144.74, 4.92) * mm});
            skLineSegment(sketch, "E1806", {"start": v(144.74, 4.92) * mm, "end": v(145.09, 4.23) * mm});
            skLineSegment(sketch, "E1807", {"start": v(145.09, 4.23) * mm, "end": v(145.4, 3.53) * mm});
            skLineSegment(sketch, "E1808", {"start": v(145.4, 3.53) * mm, "end": v(145.67, 2.82) * mm});
            skLineSegment(sketch, "E1809", {"start": v(145.67, 2.82) * mm, "end": v(145.9, 2.09) * mm});
            skLineSegment(sketch, "E1810", {"start": v(145.9, 2.09) * mm, "end": v(146.1, 1.34) * mm});
            skLineSegment(sketch, "E1811", {"start": v(146.1, 1.34) * mm, "end": v(146.27, 0.57) * mm});
            skLineSegment(sketch, "E1812", {"start": v(146.27, 0.57) * mm, "end": v(146.4, -0.2) * mm});
            skLineSegment(sketch, "E1813", {"start": v(146.4, -0.2) * mm, "end": v(146.48, -1) * mm});
            skLineSegment(sketch, "E1814", {"start": v(146.48, -1) * mm, "end": v(146.54, -1.8) * mm});
            skLineSegment(sketch, "E1815", {"start": v(146.54, -1.8) * mm, "end": v(146.56, -2.63) * mm});
            skLineSegment(sketch, "E1816", {"start": v(146.56, -2.63) * mm, "end": v(146.54, -3.36) * mm});
            skLineSegment(sketch, "E1817", {"start": v(146.54, -3.36) * mm, "end": v(146.5, -4.08) * mm});
            skLineSegment(sketch, "E1818", {"start": v(146.5, -4.08) * mm, "end": v(146.42, -4.79) * mm});
            skLineSegment(sketch, "E1819", {"start": v(146.42, -4.79) * mm, "end": v(146.31, -5.48) * mm});
            skLineSegment(sketch, "E1820", {"start": v(146.31, -5.48) * mm, "end": v(146.17, -6.17) * mm});
            skLineSegment(sketch, "E1821", {"start": v(146.17, -6.17) * mm, "end": v(146, -6.85) * mm});
            skLineSegment(sketch, "E1822", {"start": v(146, -6.85) * mm, "end": v(145.8, -7.52) * mm});
            skLineSegment(sketch, "E1823", {"start": v(145.8, -7.52) * mm, "end": v(145.58, -8.18) * mm});
            skLineSegment(sketch, "E1824", {"start": v(145.58, -8.18) * mm, "end": v(145.32, -8.83) * mm});
            skLineSegment(sketch, "E1825", {"start": v(145.32, -8.83) * mm, "end": v(145.03, -9.47) * mm});
            skLineSegment(sketch, "E1826", {"start": v(145.03, -9.47) * mm, "end": v(144.7, -10.1) * mm});
            skLineSegment(sketch, "E1827", {"start": v(144.7, -10.1) * mm, "end": v(144.36, -10.71) * mm});
            skLineSegment(sketch, "E1828", {"start": v(144.36, -10.71) * mm, "end": v(143.97, -11.32) * mm});
            skLineSegment(sketch, "E1829", {"start": v(143.97, -11.32) * mm, "end": v(143.56, -11.91) * mm});
            skLineSegment(sketch, "E1830", {"start": v(143.56, -11.91) * mm, "end": v(143.12, -12.5) * mm});
            skLineSegment(sketch, "E1831", {"start": v(143.12, -12.5) * mm, "end": v(142.65, -13.07) * mm});
            skLineSegment(sketch, "E1832", {"start": v(142.65, -13.07) * mm, "end": v(142.16, -13.62) * mm});
            skLineSegment(sketch, "E1833", {"start": v(142.16, -13.62) * mm, "end": v(141.65, -14.14) * mm});
            skLineSegment(sketch, "E1834", {"start": v(141.65, -14.14) * mm, "end": v(141.12, -14.63) * mm});
            skLineSegment(sketch, "E1835", {"start": v(141.12, -14.63) * mm, "end": v(140.58, -15.1) * mm});
            skLineSegment(sketch, "E1836", {"start": v(140.58, -15.1) * mm, "end": v(140.02, -15.53) * mm});
            skLineSegment(sketch, "E1837", {"start": v(140.02, -15.53) * mm, "end": v(139.45, -15.94) * mm});
            skLineSegment(sketch, "E1838", {"start": v(139.45, -15.94) * mm, "end": v(138.86, -16.31) * mm});
            skLineSegment(sketch, "E1839", {"start": v(138.86, -16.31) * mm, "end": v(138.26, -16.66) * mm});
            skLineSegment(sketch, "E1840", {"start": v(138.26, -16.66) * mm, "end": v(137.64, -16.97) * mm});
            skLineSegment(sketch, "E1841", {"start": v(137.64, -16.97) * mm, "end": v(137, -17.26) * mm});
            skLineSegment(sketch, "E1842", {"start": v(137, -17.26) * mm, "end": v(136.35, -17.52) * mm});
            skLineSegment(sketch, "E1843", {"start": v(136.35, -17.52) * mm, "end": v(135.69, -17.74) * mm});
            skLineSegment(sketch, "E1844", {"start": v(135.69, -17.74) * mm, "end": v(135.01, -17.94) * mm});
            skLineSegment(sketch, "E1845", {"start": v(135.01, -17.94) * mm, "end": v(134.32, -18.1) * mm});
            skLineSegment(sketch, "E1846", {"start": v(134.32, -18.1) * mm, "end": v(133.6, -18.25) * mm});
            skLineSegment(sketch, "E1847", {"start": v(133.6, -18.25) * mm, "end": v(132.89, -18.35) * mm});
            skLineSegment(sketch, "E1848", {"start": v(132.89, -18.35) * mm, "end": v(132.75, -18.38) * mm});
            skLineSegment(sketch, "E1849", {"start": v(132.75, -18.38) * mm, "end": v(132.62, -18.41) * mm});
            skLineSegment(sketch, "E1850", {"start": v(132.62, -18.41) * mm, "end": v(132.5, -18.46) * mm});
            skLineSegment(sketch, "E1851", {"start": v(132.5, -18.46) * mm, "end": v(132.37, -18.52) * mm});
            skLineSegment(sketch, "E1852", {"start": v(132.37, -18.52) * mm, "end": v(132.25, -18.59) * mm});
            skLineSegment(sketch, "E1853", {"start": v(132.25, -18.59) * mm, "end": v(132.15, -18.67) * mm});
            skLineSegment(sketch, "E1854", {"start": v(132.15, -18.67) * mm, "end": v(132.05, -18.75) * mm});
            skLineSegment(sketch, "E1855", {"start": v(132.05, -18.75) * mm, "end": v(131.96, -18.85) * mm});
            skLineSegment(sketch, "E1856", {"start": v(131.96, -18.85) * mm, "end": v(131.87, -18.95) * mm});
            skLineSegment(sketch, "E1857", {"start": v(131.87, -18.95) * mm, "end": v(131.8, -19.06) * mm});
            skLineSegment(sketch, "E1858", {"start": v(131.8, -19.06) * mm, "end": v(131.73, -19.18) * mm});
            skLineSegment(sketch, "E1859", {"start": v(131.73, -19.18) * mm, "end": v(131.68, -19.3) * mm});
            skLineSegment(sketch, "E1860", {"start": v(131.68, -19.3) * mm, "end": v(131.64, -19.43) * mm});
            skLineSegment(sketch, "E1861", {"start": v(131.64, -19.43) * mm, "end": v(131.6, -19.56) * mm});
            skLineSegment(sketch, "E1862", {"start": v(131.6, -19.56) * mm, "end": v(131.59, -19.7) * mm});
            skLineSegment(sketch, "E1863", {"start": v(131.59, -19.7) * mm, "end": v(131.58, -19.84) * mm});
            skLineSegment(sketch, "E1864", {"start": v(131.58, -19.84) * mm, "end": v(131.58, -23.15) * mm});
            skLineSegment(sketch, "E1865", {"start": v(131.58, -23.15) * mm, "end": v(131.6, -23.5) * mm});
            skLineSegment(sketch, "E1866", {"start": v(131.6, -23.5) * mm, "end": v(131.65, -23.83) * mm});
            skLineSegment(sketch, "E1867", {"start": v(131.65, -23.83) * mm, "end": v(131.73, -24.14) * mm});
            skLineSegment(sketch, "E1868", {"start": v(131.73, -24.14) * mm, "end": v(131.84, -24.45) * mm});
            skLineSegment(sketch, "E1869", {"start": v(131.84, -24.45) * mm, "end": v(131.99, -24.74) * mm});
            skLineSegment(sketch, "E1870", {"start": v(131.99, -24.74) * mm, "end": v(132.15, -25.02) * mm});
            skLineSegment(sketch, "E1871", {"start": v(132.15, -25.02) * mm, "end": v(132.34, -25.27) * mm});
            skLineSegment(sketch, "E1872", {"start": v(132.34, -25.27) * mm, "end": v(132.56, -25.51) * mm});
            skLineSegment(sketch, "E1873", {"start": v(132.56, -25.51) * mm, "end": v(132.8, -25.73) * mm});
            skLineSegment(sketch, "E1874", {"start": v(132.8, -25.73) * mm, "end": v(133.05, -25.92) * mm});
            skLineSegment(sketch, "E1875", {"start": v(133.05, -25.92) * mm, "end": v(133.33, -26.09) * mm});
            skLineSegment(sketch, "E1876", {"start": v(133.33, -26.09) * mm, "end": v(133.62, -26.23) * mm});
            skLineSegment(sketch, "E1877", {"start": v(133.62, -26.23) * mm, "end": v(133.93, -26.34) * mm});
            skLineSegment(sketch, "E1878", {"start": v(133.93, -26.34) * mm, "end": v(134.25, -26.42) * mm});
            skLineSegment(sketch, "E1879", {"start": v(134.25, -26.42) * mm, "end": v(134.58, -26.47) * mm});
            skLineSegment(sketch, "E1880", {"start": v(134.58, -26.47) * mm, "end": v(134.92, -26.49) * mm});
            skLineSegment(sketch, "E1881", {"start": v(134.92, -26.49) * mm, "end": v(153.43, -26.49) * mm});
            skLineSegment(sketch, "E1882", {"start": v(153.43, -26.49) * mm, "end": v(153.64, -26.48) * mm});
            skLineSegment(sketch, "E1883", {"start": v(153.64, -26.48) * mm, "end": v(153.85, -26.47) * mm});
            skLineSegment(sketch, "E1884", {"start": v(153.85, -26.47) * mm, "end": v(154.06, -26.45) * mm});
            skLineSegment(sketch, "E1885", {"start": v(154.06, -26.45) * mm, "end": v(154.26, -26.42) * mm});
            skLineSegment(sketch, "E1886", {"start": v(154.26, -26.42) * mm, "end": v(154.45, -26.38) * mm});
            skLineSegment(sketch, "E1887", {"start": v(154.45, -26.38) * mm, "end": v(154.64, -26.33) * mm});
            skLineSegment(sketch, "E1888", {"start": v(154.64, -26.33) * mm, "end": v(154.83, -26.27) * mm});
            skLineSegment(sketch, "E1889", {"start": v(154.83, -26.27) * mm, "end": v(155, -26.2) * mm});
            skLineSegment(sketch, "E1890", {"start": v(155, -26.2) * mm, "end": v(155.19, -26.13) * mm});
            skLineSegment(sketch, "E1891", {"start": v(155.19, -26.13) * mm, "end": v(155.36, -26.05) * mm});
            skLineSegment(sketch, "E1892", {"start": v(155.36, -26.05) * mm, "end": v(155.52, -25.96) * mm});
            skLineSegment(sketch, "E1893", {"start": v(155.52, -25.96) * mm, "end": v(155.68, -25.86) * mm});
            skLineSegment(sketch, "E1894", {"start": v(155.68, -25.86) * mm, "end": v(155.84, -25.75) * mm});
            skLineSegment(sketch, "E1895", {"start": v(155.84, -25.75) * mm, "end": v(156, -25.63) * mm});
            skLineSegment(sketch, "E1896", {"start": v(156, -25.63) * mm, "end": v(156.14, -25.5) * mm});
            skLineSegment(sketch, "E1897", {"start": v(156.14, -25.5) * mm, "end": v(156.28, -25.37) * mm});
            skLineSegment(sketch, "E1898", {"start": v(156.28, -25.37) * mm, "end": v(156.41, -25.23) * mm});
            skLineSegment(sketch, "E1899", {"start": v(156.41, -25.23) * mm, "end": v(156.54, -25.09) * mm});
            skLineSegment(sketch, "E1900", {"start": v(156.54, -25.09) * mm, "end": v(156.66, -24.94) * mm});
            skLineSegment(sketch, "E1901", {"start": v(156.66, -24.94) * mm, "end": v(156.77, -24.78) * mm});
            skLineSegment(sketch, "E1902", {"start": v(156.77, -24.78) * mm, "end": v(156.87, -24.62) * mm});
            skLineSegment(sketch, "E1903", {"start": v(156.87, -24.62) * mm, "end": v(156.96, -24.45) * mm});
            skLineSegment(sketch, "E1904", {"start": v(156.96, -24.45) * mm, "end": v(157.04, -24.28) * mm});
            skLineSegment(sketch, "E1905", {"start": v(157.04, -24.28) * mm, "end": v(157.11, -24.1) * mm});
            skLineSegment(sketch, "E1906", {"start": v(157.11, -24.1) * mm, "end": v(157.18, -23.92) * mm});
            skLineSegment(sketch, "E1907", {"start": v(157.18, -23.92) * mm, "end": v(157.24, -23.74) * mm});
            skLineSegment(sketch, "E1908", {"start": v(157.24, -23.74) * mm, "end": v(157.28, -23.55) * mm});
            skLineSegment(sketch, "E1909", {"start": v(157.28, -23.55) * mm, "end": v(157.32, -23.35) * mm});
            skLineSegment(sketch, "E1910", {"start": v(157.32, -23.35) * mm, "end": v(157.35, -23.15) * mm});
            skLineSegment(sketch, "E1911", {"start": v(157.35, -23.15) * mm, "end": v(157.38, -22.95) * mm});
            skLineSegment(sketch, "E1912", {"start": v(157.38, -22.95) * mm, "end": v(157.39, -22.74) * mm});
            skLineSegment(sketch, "E1913", {"start": v(157.39, -22.74) * mm, "end": v(157.4, -22.53) * mm});
            skLineSegment(sketch, "E1914", {"start": v(157.4, -22.53) * mm, "end": v(157.4, 12.26) * mm});
            skLineSegment(sketch, "E1915", {"start": v(157.4, 12.26) * mm, "end": v(157.4, 12.34) * mm});
            skLineSegment(sketch, "E1916", {"start": v(157.4, 12.34) * mm, "end": v(157.4, 12.42) * mm});
            skLineSegment(sketch, "E1917", {"start": v(157.4, 12.42) * mm, "end": v(157.43, 12.5) * mm});
            skLineSegment(sketch, "E1918", {"start": v(157.43, 12.5) * mm, "end": v(157.45, 12.57) * mm});
            skLineSegment(sketch, "E1919", {"start": v(157.45, 12.57) * mm, "end": v(157.49, 12.63) * mm});
            skLineSegment(sketch, "E1920", {"start": v(157.49, 12.63) * mm, "end": v(157.53, 12.7) * mm});
            skLineSegment(sketch, "E1921", {"start": v(157.53, 12.7) * mm, "end": v(157.57, 12.76) * mm});
            skLineSegment(sketch, "E1922", {"start": v(157.57, 12.76) * mm, "end": v(157.62, 12.81) * mm});
            skLineSegment(sketch, "E1923", {"start": v(157.62, 12.81) * mm, "end": v(157.68, 12.86) * mm});
            skLineSegment(sketch, "E1924", {"start": v(157.68, 12.86) * mm, "end": v(157.74, 12.9) * mm});
            skLineSegment(sketch, "E1925", {"start": v(157.74, 12.9) * mm, "end": v(157.8, 12.95) * mm});
            skLineSegment(sketch, "E1926", {"start": v(157.8, 12.95) * mm, "end": v(157.87, 12.98) * mm});
            skLineSegment(sketch, "E1927", {"start": v(157.87, 12.98) * mm, "end": v(157.94, 13) * mm});
            skLineSegment(sketch, "E1928", {"start": v(157.94, 13) * mm, "end": v(158.01, 13.02) * mm});
            skLineSegment(sketch, "E1929", {"start": v(158.01, 13.02) * mm, "end": v(158.09, 13.04) * mm});
            skLineSegment(sketch, "E1930", {"start": v(158.09, 13.04) * mm, "end": v(158.17, 13.04) * mm});
            skLineSegment(sketch, "E1931", {"start": v(158.17, 13.04) * mm, "end": v(171, 13.04) * mm});
            skLineSegment(sketch, "E1932", {"start": v(171, 13.04) * mm, "end": v(171.28, 13.02) * mm});
            skLineSegment(sketch, "E1933", {"start": v(171.28, 13.02) * mm, "end": v(171.55, 13) * mm});
            skLineSegment(sketch, "E1934", {"start": v(171.55, 13) * mm, "end": v(171.83, 12.97) * mm});
            skLineSegment(sketch, "E1935", {"start": v(171.83, 12.97) * mm, "end": v(172.1, 12.93) * mm});
            skLineSegment(sketch, "E1936", {"start": v(172.1, 12.93) * mm, "end": v(172.37, 12.88) * mm});
            skLineSegment(sketch, "E1937", {"start": v(172.37, 12.88) * mm, "end": v(172.65, 12.83) * mm});
            skLineSegment(sketch, "E1938", {"start": v(172.65, 12.83) * mm, "end": v(172.92, 12.76) * mm});
            skLineSegment(sketch, "E1939", {"start": v(172.92, 12.76) * mm, "end": v(173.2, 12.7) * mm});
            skLineSegment(sketch, "E1940", {"start": v(173.2, 12.7) * mm, "end": v(173.46, 12.6) * mm});
            skLineSegment(sketch, "E1941", {"start": v(173.46, 12.6) * mm, "end": v(173.73, 12.52) * mm});
            skLineSegment(sketch, "E1942", {"start": v(173.73, 12.52) * mm, "end": v(174, 12.42) * mm});
            skLineSegment(sketch, "E1943", {"start": v(174, 12.42) * mm, "end": v(174.27, 12.31) * mm});
            skLineSegment(sketch, "E1944", {"start": v(174.27, 12.31) * mm, "end": v(174.54, 12.2) * mm});
            skLineSegment(sketch, "E1945", {"start": v(174.54, 12.2) * mm, "end": v(174.81, 12.07) * mm});
            skLineSegment(sketch, "E1946", {"start": v(174.81, 12.07) * mm, "end": v(175.08, 11.94) * mm});
            skLineSegment(sketch, "E1947", {"start": v(175.08, 11.94) * mm, "end": v(175.56, 11.67) * mm});
            skLineSegment(sketch, "E1948", {"start": v(175.56, 11.67) * mm, "end": v(176.02, 11.37) * mm});
            skLineSegment(sketch, "E1949", {"start": v(176.02, 11.37) * mm, "end": v(176.44, 11.05) * mm});
            skLineSegment(sketch, "E1950", {"start": v(176.44, 11.05) * mm, "end": v(176.83, 10.7) * mm});
            skLineSegment(sketch, "E1951", {"start": v(176.83, 10.7) * mm, "end": v(177.2, 10.33) * mm});
            skLineSegment(sketch, "E1952", {"start": v(177.2, 10.33) * mm, "end": v(177.52, 9.94) * mm});
            skLineSegment(sketch, "E1953", {"start": v(177.52, 9.94) * mm, "end": v(177.82, 9.52) * mm});
            skLineSegment(sketch, "E1954", {"start": v(177.82, 9.52) * mm, "end": v(178.1, 9.08) * mm});
            skLineSegment(sketch, "E1955", {"start": v(178.1, 9.08) * mm, "end": v(178.33, 8.6) * mm});
            skLineSegment(sketch, "E1956", {"start": v(178.33, 8.6) * mm, "end": v(178.53, 8.12) * mm});
            skLineSegment(sketch, "E1957", {"start": v(178.53, 8.12) * mm, "end": v(178.7, 7.6) * mm});
            skLineSegment(sketch, "E1958", {"start": v(178.7, 7.6) * mm, "end": v(178.85, 7.06) * mm});
            skLineSegment(sketch, "E1959", {"start": v(178.85, 7.06) * mm, "end": v(178.96, 6.5) * mm});
            skLineSegment(sketch, "E1960", {"start": v(178.96, 6.5) * mm, "end": v(179.04, 5.92) * mm});
            skLineSegment(sketch, "E1961", {"start": v(179.04, 5.92) * mm, "end": v(179.09, 5.3) * mm});
            skLineSegment(sketch, "E1962", {"start": v(179.09, 5.3) * mm, "end": v(179.1, 4.67) * mm});
            skLineSegment(sketch, "E1963", {"start": v(179.1, 4.67) * mm, "end": v(179.09, 4.04) * mm});
            skLineSegment(sketch, "E1964", {"start": v(179.09, 4.04) * mm, "end": v(179.04, 3.43) * mm});
            skLineSegment(sketch, "E1965", {"start": v(179.04, 3.43) * mm, "end": v(178.96, 2.85) * mm});
            skLineSegment(sketch, "E1966", {"start": v(178.96, 2.85) * mm, "end": v(178.85, 2.28) * mm});
            skLineSegment(sketch, "E1967", {"start": v(178.85, 2.28) * mm, "end": v(178.7, 1.74) * mm});
            skLineSegment(sketch, "E1968", {"start": v(178.7, 1.74) * mm, "end": v(178.53, 1.23) * mm});
            skLineSegment(sketch, "E1969", {"start": v(178.53, 1.23) * mm, "end": v(178.33, 0.74) * mm});
            skLineSegment(sketch, "E1970", {"start": v(178.33, 0.74) * mm, "end": v(178.1, 0.27) * mm});
            skLineSegment(sketch, "E1971", {"start": v(178.1, 0.27) * mm, "end": v(177.82, -0.17) * mm});
            skLineSegment(sketch, "E1972", {"start": v(177.82, -0.17) * mm, "end": v(177.52, -0.6) * mm});
            skLineSegment(sketch, "E1973", {"start": v(177.52, -0.6) * mm, "end": v(177.2, -0.99) * mm});
            skLineSegment(sketch, "E1974", {"start": v(177.2, -0.99) * mm, "end": v(176.83, -1.36) * mm});
            skLineSegment(sketch, "E1975", {"start": v(176.83, -1.36) * mm, "end": v(176.44, -1.7) * mm});
            skLineSegment(sketch, "E1976", {"start": v(176.44, -1.7) * mm, "end": v(176.02, -2.02) * mm});
            skLineSegment(sketch, "E1977", {"start": v(176.02, -2.02) * mm, "end": v(175.57, -2.32) * mm});
            skLineSegment(sketch, "E1978", {"start": v(175.57, -2.32) * mm, "end": v(175.08, -2.6) * mm});
            skLineSegment(sketch, "E1979", {"start": v(175.08, -2.6) * mm, "end": v(174.8, -2.73) * mm});
            skLineSegment(sketch, "E1980", {"start": v(174.8, -2.73) * mm, "end": v(174.52, -2.86) * mm});
            skLineSegment(sketch, "E1981", {"start": v(174.52, -2.86) * mm, "end": v(174.24, -2.98) * mm});
            skLineSegment(sketch, "E1982", {"start": v(174.24, -2.98) * mm, "end": v(173.97, -3.1) * mm});
            skLineSegment(sketch, "E1983", {"start": v(173.97, -3.1) * mm, "end": v(173.7, -3.2) * mm});
            skLineSegment(sketch, "E1984", {"start": v(173.7, -3.2) * mm, "end": v(173.41, -3.3) * mm});
            skLineSegment(sketch, "E1985", {"start": v(173.41, -3.3) * mm, "end": v(173.14, -3.38) * mm});
            skLineSegment(sketch, "E1986", {"start": v(173.14, -3.38) * mm, "end": v(172.87, -3.46) * mm});
            skLineSegment(sketch, "E1987", {"start": v(172.87, -3.46) * mm, "end": v(172.6, -3.52) * mm});
            skLineSegment(sketch, "E1988", {"start": v(172.6, -3.52) * mm, "end": v(172.33, -3.58) * mm});
            skLineSegment(sketch, "E1989", {"start": v(172.33, -3.58) * mm, "end": v(172.06, -3.63) * mm});
            skLineSegment(sketch, "E1990", {"start": v(172.06, -3.63) * mm, "end": v(171.79, -3.67) * mm});
            skLineSegment(sketch, "E1991", {"start": v(171.79, -3.67) * mm, "end": v(171.52, -3.7) * mm});
            skLineSegment(sketch, "E1992", {"start": v(171.52, -3.7) * mm, "end": v(171.26, -3.73) * mm});
            skLineSegment(sketch, "E1993", {"start": v(171.26, -3.73) * mm, "end": v(171, -3.74) * mm});
            skLineSegment(sketch, "E1994", {"start": v(171, -3.74) * mm, "end": v(161.26, -3.75) * mm});
            skLineSegment(sketch, "E1995", {"start": v(161.26, -3.75) * mm, "end": v(161.12, -3.75) * mm});
            skLineSegment(sketch, "E1996", {"start": v(161.12, -3.75) * mm, "end": v(160.99, -3.77) * mm});
            skLineSegment(sketch, "E1997", {"start": v(160.99, -3.77) * mm, "end": v(160.85, -3.8) * mm});
            skLineSegment(sketch, "E1998", {"start": v(160.85, -3.8) * mm, "end": v(160.73, -3.85) * mm});
            skLineSegment(sketch, "E1999", {"start": v(160.73, -3.85) * mm, "end": v(160.6, -3.91) * mm});
            skLineSegment(sketch, "E2000", {"start": v(160.6, -3.91) * mm, "end": v(160.5, -3.98) * mm});
            skLineSegment(sketch, "E2001", {"start": v(160.5, -3.98) * mm, "end": v(160.4, -4.06) * mm});
            skLineSegment(sketch, "E2002", {"start": v(160.4, -4.06) * mm, "end": v(160.3, -4.15) * mm});
            skLineSegment(sketch, "E2003", {"start": v(160.3, -4.15) * mm, "end": v(160.2, -4.24) * mm});
            skLineSegment(sketch, "E2004", {"start": v(160.2, -4.24) * mm, "end": v(160.13, -4.35) * mm});
            skLineSegment(sketch, "E2005", {"start": v(160.13, -4.35) * mm, "end": v(160.06, -4.46) * mm});
            skLineSegment(sketch, "E2006", {"start": v(160.06, -4.46) * mm, "end": v(160, -4.58) * mm});
            skLineSegment(sketch, "E2007", {"start": v(160, -4.58) * mm, "end": v(159.95, -4.7) * mm});
            skLineSegment(sketch, "E2008", {"start": v(159.95, -4.7) * mm, "end": v(159.92, -4.84) * mm});
            skLineSegment(sketch, "E2009", {"start": v(159.92, -4.84) * mm, "end": v(159.9, -4.98) * mm});
            skLineSegment(sketch, "E2010", {"start": v(159.9, -4.98) * mm, "end": v(159.9, -5.11) * mm});
            skLineSegment(sketch, "E2011", {"start": v(159.9, -5.11) * mm, "end": v(159.9, -5.43) * mm});
            skLineSegment(sketch, "E2012", {"start": v(159.9, -5.43) * mm, "end": v(159.9, -5.55) * mm});
            skLineSegment(sketch, "E2013", {"start": v(159.9, -5.55) * mm, "end": v(159.9, -5.67) * mm});
            skLineSegment(sketch, "E2014", {"start": v(159.9, -5.67) * mm, "end": v(159.92, -5.79) * mm});
            skLineSegment(sketch, "E2015", {"start": v(159.92, -5.79) * mm, "end": v(159.94, -5.9) * mm});
            skLineSegment(sketch, "E2016", {"start": v(159.94, -5.9) * mm, "end": v(159.97, -6.02) * mm});
            skLineSegment(sketch, "E2017", {"start": v(159.97, -6.02) * mm, "end": v(160, -6.13) * mm});
            skLineSegment(sketch, "E2018", {"start": v(160, -6.13) * mm, "end": v(160.03, -6.24) * mm});
            skLineSegment(sketch, "E2019", {"start": v(160.03, -6.24) * mm, "end": v(160.08, -6.35) * mm});
            skLineSegment(sketch, "E2020", {"start": v(160.08, -6.35) * mm, "end": v(160.12, -6.46) * mm});
            skLineSegment(sketch, "E2021", {"start": v(160.12, -6.46) * mm, "end": v(160.18, -6.56) * mm});
            skLineSegment(sketch, "E2022", {"start": v(160.18, -6.56) * mm, "end": v(160.23, -6.67) * mm});
            skLineSegment(sketch, "E2023", {"start": v(160.23, -6.67) * mm, "end": v(160.3, -6.76) * mm});
            skLineSegment(sketch, "E2024", {"start": v(160.3, -6.76) * mm, "end": v(160.36, -6.86) * mm});
            skLineSegment(sketch, "E2025", {"start": v(160.36, -6.86) * mm, "end": v(160.44, -6.95) * mm});
            skLineSegment(sketch, "E2026", {"start": v(160.44, -6.95) * mm, "end": v(160.51, -7.04) * mm});
            skLineSegment(sketch, "E2027", {"start": v(160.51, -7.04) * mm, "end": v(160.6, -7.13) * mm});
            skLineSegment(sketch, "E2028", {"start": v(160.6, -7.13) * mm, "end": v(179.2, -25.68) * mm});
            skLineSegment(sketch, "E2029", {"start": v(179.2, -25.68) * mm, "end": v(179.3, -25.78) * mm});
            skLineSegment(sketch, "E2030", {"start": v(179.3, -25.78) * mm, "end": v(179.4, -25.87) * mm});
            skLineSegment(sketch, "E2031", {"start": v(179.4, -25.87) * mm, "end": v(179.5, -25.95) * mm});
            skLineSegment(sketch, "E2032", {"start": v(179.5, -25.95) * mm, "end": v(179.62, -26.03) * mm});
            skLineSegment(sketch, "E2033", {"start": v(179.62, -26.03) * mm, "end": v(179.73, -26.1) * mm});
            skLineSegment(sketch, "E2034", {"start": v(179.73, -26.1) * mm, "end": v(179.85, -26.17) * mm});
            skLineSegment(sketch, "E2035", {"start": v(179.85, -26.17) * mm, "end": v(179.97, -26.23) * mm});
            skLineSegment(sketch, "E2036", {"start": v(179.97, -26.23) * mm, "end": v(180.1, -26.28) * mm});
            skLineSegment(sketch, "E2037", {"start": v(180.1, -26.28) * mm, "end": v(180.22, -26.33) * mm});
            skLineSegment(sketch, "E2038", {"start": v(180.22, -26.33) * mm, "end": v(180.34, -26.37) * mm});
            skLineSegment(sketch, "E2039", {"start": v(180.34, -26.37) * mm, "end": v(180.47, -26.4) * mm});
            skLineSegment(sketch, "E2040", {"start": v(180.47, -26.4) * mm, "end": v(180.6, -26.44) * mm});
            skLineSegment(sketch, "E2041", {"start": v(180.6, -26.44) * mm, "end": v(180.74, -26.46) * mm});
            skLineSegment(sketch, "E2042", {"start": v(180.74, -26.46) * mm, "end": v(180.87, -26.48) * mm});
            skLineSegment(sketch, "E2043", {"start": v(180.87, -26.48) * mm, "end": v(181.01, -26.49) * mm});
            skLineSegment(sketch, "E2044", {"start": v(181.01, -26.49) * mm, "end": v(181.15, -26.5) * mm});
            skLineSegment(sketch, "E2045", {"start": v(181.15, -26.5) * mm, "end": v(192.86, -26.54) * mm});
            skLineSegment(sketch, "E2046", {"start": v(192.86, -26.54) * mm, "end": v(193.74, -26.5) * mm});
            skLineSegment(sketch, "E2047", {"start": v(193.74, -26.5) * mm, "end": v(194.6, -26.37) * mm});
            skLineSegment(sketch, "E2048", {"start": v(194.6, -26.37) * mm, "end": v(195.43, -26.15) * mm});
            skLineSegment(sketch, "E2049", {"start": v(195.43, -26.15) * mm, "end": v(196.22, -25.86) * mm});
            skLineSegment(sketch, "E2050", {"start": v(196.22, -25.86) * mm, "end": v(196.98, -25.5) * mm});
            skLineSegment(sketch, "E2051", {"start": v(196.98, -25.5) * mm, "end": v(197.7, -25.06) * mm});
            skLineSegment(sketch, "E2052", {"start": v(197.7, -25.06) * mm, "end": v(198.36, -24.56) * mm});
            skLineSegment(sketch, "E2053", {"start": v(198.36, -24.56) * mm, "end": v(198.97, -24) * mm});
            skLineSegment(sketch, "E2054", {"start": v(198.97, -24) * mm, "end": v(199.53, -23.39) * mm});
            skLineSegment(sketch, "E2055", {"start": v(199.53, -23.39) * mm, "end": v(200.03, -22.72) * mm});
            skLineSegment(sketch, "E2056", {"start": v(200.03, -22.72) * mm, "end": v(200.46, -22) * mm});
            skLineSegment(sketch, "E2057", {"start": v(200.46, -22) * mm, "end": v(200.83, -21.25) * mm});
            skLineSegment(sketch, "E2058", {"start": v(200.83, -21.25) * mm, "end": v(201.12, -20.46) * mm});
            skLineSegment(sketch, "E2059", {"start": v(201.12, -20.46) * mm, "end": v(201.33, -19.63) * mm});
            skLineSegment(sketch, "E2060", {"start": v(201.33, -19.63) * mm, "end": v(201.47, -18.77) * mm});
            skLineSegment(sketch, "E2061", {"start": v(201.47, -18.77) * mm, "end": v(201.51, -17.89) * mm});
            skLineSegment(sketch, "E2062", {"start": v(201.51, -17.89) * mm, "end": v(201.51, 17.82) * mm});
            skLineSegment(sketch, "E2063", {"start": v(201.51, 17.82) * mm, "end": v(201.47, 18.7) * mm});
            skLineSegment(sketch, "E2064", {"start": v(201.47, 18.7) * mm, "end": v(201.33, 19.57) * mm});
            skLineSegment(sketch, "E2065", {"start": v(201.33, 19.57) * mm, "end": v(201.12, 20.4) * mm});
            skLineSegment(sketch, "E2066", {"start": v(201.12, 20.4) * mm, "end": v(200.83, 21.2) * mm});
            skLineSegment(sketch, "E2067", {"start": v(200.83, 21.2) * mm, "end": v(200.46, 21.95) * mm});
            skLineSegment(sketch, "E2068", {"start": v(200.46, 21.95) * mm, "end": v(200.03, 22.66) * mm});
            skLineSegment(sketch, "E2069", {"start": v(200.03, 22.66) * mm, "end": v(199.53, 23.33) * mm});
            skLineSegment(sketch, "E2070", {"start": v(199.53, 23.33) * mm, "end": v(198.97, 23.94) * mm});
            skLineSegment(sketch, "E2071", {"start": v(198.97, 23.94) * mm, "end": v(198.36, 24.5) * mm});
            skLineSegment(sketch, "E2072", {"start": v(198.36, 24.5) * mm, "end": v(197.7, 25) * mm});
            skLineSegment(sketch, "E2073", {"start": v(197.7, 25) * mm, "end": v(196.98, 25.43) * mm});
            skLineSegment(sketch, "E2074", {"start": v(196.98, 25.43) * mm, "end": v(196.22, 25.8) * mm});
            skLineSegment(sketch, "E2075", {"start": v(196.22, 25.8) * mm, "end": v(195.43, 26.1) * mm});
            skLineSegment(sketch, "E2076", {"start": v(195.43, 26.1) * mm, "end": v(194.6, 26.3) * mm});
            skLineSegment(sketch, "E2077", {"start": v(194.6, 26.3) * mm, "end": v(193.74, 26.44) * mm});
            skLineSegment(sketch, "E2078", {"start": v(193.74, 26.44) * mm, "end": v(192.86, 26.48) * mm});
            skLineSegment(sketch, "E2079", {"start": v(198.49, -17.89) * mm, "end": v(198.46, -18.46) * mm});
            skLineSegment(sketch, "E2080", {"start": v(198.46, -18.46) * mm, "end": v(198.37, -19.02) * mm});
            skLineSegment(sketch, "E2081", {"start": v(198.37, -19.02) * mm, "end": v(198.24, -19.56) * mm});
            skLineSegment(sketch, "E2082", {"start": v(198.24, -19.56) * mm, "end": v(198.05, -20.08) * mm});
            skLineSegment(sketch, "E2083", {"start": v(198.05, -20.08) * mm, "end": v(197.8, -20.57) * mm});
            skLineSegment(sketch, "E2084", {"start": v(197.8, -20.57) * mm, "end": v(197.53, -21.03) * mm});
            skLineSegment(sketch, "E2085", {"start": v(197.53, -21.03) * mm, "end": v(197.2, -21.47) * mm});
            skLineSegment(sketch, "E2086", {"start": v(197.2, -21.47) * mm, "end": v(196.84, -21.87) * mm});
            skLineSegment(sketch, "E2087", {"start": v(196.84, -21.87) * mm, "end": v(196.44, -22.23) * mm});
            skLineSegment(sketch, "E2088", {"start": v(196.44, -22.23) * mm, "end": v(196, -22.56) * mm});
            skLineSegment(sketch, "E2089", {"start": v(196, -22.56) * mm, "end": v(195.54, -22.84) * mm});
            skLineSegment(sketch, "E2090", {"start": v(195.54, -22.84) * mm, "end": v(195.05, -23.08) * mm});
            skLineSegment(sketch, "E2091", {"start": v(195.05, -23.08) * mm, "end": v(194.53, -23.27) * mm});
            skLineSegment(sketch, "E2092", {"start": v(194.53, -23.27) * mm, "end": v(193.99, -23.4) * mm});
            skLineSegment(sketch, "E2093", {"start": v(193.99, -23.4) * mm, "end": v(193.43, -23.5) * mm});
            skLineSegment(sketch, "E2094", {"start": v(193.43, -23.5) * mm, "end": v(192.86, -23.52) * mm});
            skLineSegment(sketch, "E2095", {"start": v(192.86, -23.52) * mm, "end": v(181.97, -23.49) * mm});
            skLineSegment(sketch, "E2096", {"start": v(181.97, -23.49) * mm, "end": v(181.88, -23.48) * mm});
            skLineSegment(sketch, "E2097", {"start": v(181.88, -23.48) * mm, "end": v(181.79, -23.48) * mm});
            skLineSegment(sketch, "E2098", {"start": v(181.79, -23.48) * mm, "end": v(181.7, -23.47) * mm});
            skLineSegment(sketch, "E2099", {"start": v(181.7, -23.47) * mm, "end": v(181.6, -23.45) * mm});
            skLineSegment(sketch, "E2100", {"start": v(181.6, -23.45) * mm, "end": v(181.52, -23.43) * mm});
            skLineSegment(sketch, "E2101", {"start": v(181.52, -23.43) * mm, "end": v(181.43, -23.4) * mm});
            skLineSegment(sketch, "E2102", {"start": v(181.43, -23.4) * mm, "end": v(181.34, -23.38) * mm});
            skLineSegment(sketch, "E2103", {"start": v(181.34, -23.38) * mm, "end": v(181.26, -23.34) * mm});
            skLineSegment(sketch, "E2104", {"start": v(181.26, -23.34) * mm, "end": v(181.18, -23.3) * mm});
            skLineSegment(sketch, "E2105", {"start": v(181.18, -23.3) * mm, "end": v(181.1, -23.27) * mm});
            skLineSegment(sketch, "E2106", {"start": v(181.1, -23.27) * mm, "end": v(181.02, -23.22) * mm});
            skLineSegment(sketch, "E2107", {"start": v(181.02, -23.22) * mm, "end": v(180.94, -23.17) * mm});
            skLineSegment(sketch, "E2108", {"start": v(180.94, -23.17) * mm, "end": v(180.86, -23.12) * mm});
            skLineSegment(sketch, "E2109", {"start": v(180.86, -23.12) * mm, "end": v(180.8, -23.06) * mm});
            skLineSegment(sketch, "E2110", {"start": v(180.8, -23.06) * mm, "end": v(180.72, -23) * mm});
            skLineSegment(sketch, "E2111", {"start": v(180.72, -23) * mm, "end": v(180.66, -22.94) * mm});
            skLineSegment(sketch, "E2112", {"start": v(180.66, -22.94) * mm, "end": v(164.7, -7) * mm});
            skLineSegment(sketch, "E2113", {"start": v(164.7, -7) * mm, "end": v(164.7, -6.98) * mm});
            skLineSegment(sketch, "E2114", {"start": v(164.7, -6.98) * mm, "end": v(164.69, -6.97) * mm});
            skLineSegment(sketch, "E2115", {"start": v(164.69, -6.97) * mm, "end": v(164.68, -6.96) * mm});
            skLineSegment(sketch, "E2116", {"start": v(164.68, -6.96) * mm, "end": v(164.68, -6.95) * mm});
            skLineSegment(sketch, "E2117", {"start": v(164.68, -6.95) * mm, "end": v(164.67, -6.94) * mm});
            skLineSegment(sketch, "E2118", {"start": v(164.67, -6.94) * mm, "end": v(164.67, -6.93) * mm});
            skLineSegment(sketch, "E2119", {"start": v(164.67, -6.93) * mm, "end": v(164.66, -6.92) * mm});
            skLineSegment(sketch, "E2120", {"start": v(164.66, -6.92) * mm, "end": v(164.66, -6.9) * mm});
            skLineSegment(sketch, "E2121", {"start": v(164.66, -6.9) * mm, "end": v(164.66, -6.9) * mm});
            skLineSegment(sketch, "E2122", {"start": v(164.66, -6.9) * mm, "end": v(164.66, -6.88) * mm});
            skLineSegment(sketch, "E2123", {"start": v(164.66, -6.88) * mm, "end": v(164.66, -6.87) * mm});
            skLineSegment(sketch, "E2124", {"start": v(164.66, -6.87) * mm, "end": v(164.66, -6.85) * mm});
            skLineSegment(sketch, "E2125", {"start": v(164.66, -6.85) * mm, "end": v(164.66, -6.84) * mm});
            skLineSegment(sketch, "E2126", {"start": v(164.66, -6.84) * mm, "end": v(164.66, -6.83) * mm});
            skLineSegment(sketch, "E2127", {"start": v(164.66, -6.83) * mm, "end": v(164.67, -6.82) * mm});
            skLineSegment(sketch, "E2128", {"start": v(164.67, -6.82) * mm, "end": v(164.67, -6.8) * mm});
            skLineSegment(sketch, "E2129", {"start": v(164.67, -6.8) * mm, "end": v(164.68, -6.8) * mm});
            skLineSegment(sketch, "E2130", {"start": v(164.68, -6.8) * mm, "end": v(164.68, -6.78) * mm});
            skLineSegment(sketch, "E2131", {"start": v(164.68, -6.78) * mm, "end": v(164.69, -6.77) * mm});
            skLineSegment(sketch, "E2132", {"start": v(164.69, -6.77) * mm, "end": v(164.7, -6.76) * mm});
            skLineSegment(sketch, "E2133", {"start": v(164.7, -6.76) * mm, "end": v(164.7, -6.75) * mm});
            skLineSegment(sketch, "E2134", {"start": v(164.7, -6.75) * mm, "end": v(164.71, -6.74) * mm});
            skLineSegment(sketch, "E2135", {"start": v(164.71, -6.74) * mm, "end": v(164.72, -6.73) * mm});
            skLineSegment(sketch, "E2136", {"start": v(164.72, -6.73) * mm, "end": v(164.73, -6.73) * mm});
            skLineSegment(sketch, "E2137", {"start": v(164.73, -6.73) * mm, "end": v(164.74, -6.72) * mm});
            skLineSegment(sketch, "E2138", {"start": v(164.74, -6.72) * mm, "end": v(164.75, -6.71) * mm});
            skLineSegment(sketch, "E2139", {"start": v(164.75, -6.71) * mm, "end": v(164.77, -6.7) * mm});
            skLineSegment(sketch, "E2140", {"start": v(164.77, -6.7) * mm, "end": v(164.78, -6.7) * mm});
            skLineSegment(sketch, "E2141", {"start": v(164.78, -6.7) * mm, "end": v(164.79, -6.7) * mm});
            skLineSegment(sketch, "E2142", {"start": v(164.79, -6.7) * mm, "end": v(164.8, -6.7) * mm});
            skLineSegment(sketch, "E2143", {"start": v(164.8, -6.7) * mm, "end": v(164.82, -6.7) * mm});
            skLineSegment(sketch, "E2144", {"start": v(164.82, -6.7) * mm, "end": v(164.83, -6.7) * mm});
            skLineSegment(sketch, "E2145", {"start": v(164.83, -6.7) * mm, "end": v(170.73, -6.7) * mm});
            skLineSegment(sketch, "E2146", {"start": v(170.73, -6.7) * mm, "end": v(171.23, -6.69) * mm});
            skLineSegment(sketch, "E2147", {"start": v(171.23, -6.69) * mm, "end": v(171.72, -6.66) * mm});
            skLineSegment(sketch, "E2148", {"start": v(171.72, -6.66) * mm, "end": v(172.2, -6.62) * mm});
            skLineSegment(sketch, "E2149", {"start": v(172.2, -6.62) * mm, "end": v(172.68, -6.55) * mm});
            skLineSegment(sketch, "E2150", {"start": v(172.68, -6.55) * mm, "end": v(173.15, -6.47) * mm});
            skLineSegment(sketch, "E2151", {"start": v(173.15, -6.47) * mm, "end": v(173.61, -6.37) * mm});
            skLineSegment(sketch, "E2152", {"start": v(173.61, -6.37) * mm, "end": v(174.07, -6.26) * mm});
            skLineSegment(sketch, "E2153", {"start": v(174.07, -6.26) * mm, "end": v(174.52, -6.12) * mm});
            skLineSegment(sketch, "E2154", {"start": v(174.52, -6.12) * mm, "end": v(174.97, -5.97) * mm});
            skLineSegment(sketch, "E2155", {"start": v(174.97, -5.97) * mm, "end": v(175.4, -5.8) * mm});
            skLineSegment(sketch, "E2156", {"start": v(175.4, -5.8) * mm, "end": v(175.83, -5.61) * mm});
            skLineSegment(sketch, "E2157", {"start": v(175.83, -5.61) * mm, "end": v(176.26, -5.4) * mm});
            skLineSegment(sketch, "E2158", {"start": v(176.26, -5.4) * mm, "end": v(176.68, -5.18) * mm});
            skLineSegment(sketch, "E2159", {"start": v(176.68, -5.18) * mm, "end": v(177.09, -4.94) * mm});
            skLineSegment(sketch, "E2160", {"start": v(177.09, -4.94) * mm, "end": v(177.49, -4.68) * mm});
            skLineSegment(sketch, "E2161", {"start": v(177.49, -4.68) * mm, "end": v(177.88, -4.4) * mm});
            skLineSegment(sketch, "E2162", {"start": v(177.88, -4.4) * mm, "end": v(178.4, -4) * mm});
            skLineSegment(sketch, "E2163", {"start": v(178.4, -4) * mm, "end": v(178.87, -3.59) * mm});
            skLineSegment(sketch, "E2164", {"start": v(178.87, -3.59) * mm, "end": v(179.31, -3.14) * mm});
            skLineSegment(sketch, "E2165", {"start": v(179.31, -3.14) * mm, "end": v(179.73, -2.68) * mm});
            skLineSegment(sketch, "E2166", {"start": v(179.73, -2.68) * mm, "end": v(180.1, -2.19) * mm});
            skLineSegment(sketch, "E2167", {"start": v(180.1, -2.19) * mm, "end": v(180.45, -1.67) * mm});
            skLineSegment(sketch, "E2168", {"start": v(180.45, -1.67) * mm, "end": v(180.76, -1.14) * mm});
            skLineSegment(sketch, "E2169", {"start": v(180.76, -1.14) * mm, "end": v(181.05, -0.58) * mm});
            skLineSegment(sketch, "E2170", {"start": v(181.05, -0.58) * mm, "end": v(181.3, 0) * mm});
            skLineSegment(sketch, "E2171", {"start": v(181.3, 0) * mm, "end": v(181.5, 0.6) * mm});
            skLineSegment(sketch, "E2172", {"start": v(181.5, 0.6) * mm, "end": v(181.7, 1.22) * mm});
            skLineSegment(sketch, "E2173", {"start": v(181.7, 1.22) * mm, "end": v(181.84, 1.87) * mm});
            skLineSegment(sketch, "E2174", {"start": v(181.84, 1.87) * mm, "end": v(181.96, 2.54) * mm});
            skLineSegment(sketch, "E2175", {"start": v(181.96, 2.54) * mm, "end": v(182.04, 3.23) * mm});
            skLineSegment(sketch, "E2176", {"start": v(182.04, 3.23) * mm, "end": v(182.09, 3.94) * mm});
            skLineSegment(sketch, "E2177", {"start": v(182.09, 3.94) * mm, "end": v(182.1, 4.67) * mm});
            skLineSegment(sketch, "E2178", {"start": v(182.1, 4.67) * mm, "end": v(182.09, 5.4) * mm});
            skLineSegment(sketch, "E2179", {"start": v(182.09, 5.4) * mm, "end": v(182.04, 6.12) * mm});
            skLineSegment(sketch, "E2180", {"start": v(182.04, 6.12) * mm, "end": v(181.96, 6.8) * mm});
            skLineSegment(sketch, "E2181", {"start": v(181.96, 6.8) * mm, "end": v(181.84, 7.48) * mm});
            skLineSegment(sketch, "E2182", {"start": v(181.84, 7.48) * mm, "end": v(181.7, 8.12) * mm});
            skLineSegment(sketch, "E2183", {"start": v(181.7, 8.12) * mm, "end": v(181.5, 8.75) * mm});
            skLineSegment(sketch, "E2184", {"start": v(181.5, 8.75) * mm, "end": v(181.3, 9.35) * mm});
            skLineSegment(sketch, "E2185", {"start": v(181.3, 9.35) * mm, "end": v(181.05, 9.93) * mm});
            skLineSegment(sketch, "E2186", {"start": v(181.05, 9.93) * mm, "end": v(180.76, 10.48) * mm});
            skLineSegment(sketch, "E2187", {"start": v(180.76, 10.48) * mm, "end": v(180.45, 11.02) * mm});
            skLineSegment(sketch, "E2188", {"start": v(180.45, 11.02) * mm, "end": v(180.1, 11.53) * mm});
            skLineSegment(sketch, "E2189", {"start": v(180.1, 11.53) * mm, "end": v(179.73, 12.02) * mm});
            skLineSegment(sketch, "E2190", {"start": v(179.73, 12.02) * mm, "end": v(179.31, 12.49) * mm});
            skLineSegment(sketch, "E2191", {"start": v(179.31, 12.49) * mm, "end": v(178.87, 12.93) * mm});
            skLineSegment(sketch, "E2192", {"start": v(178.87, 12.93) * mm, "end": v(178.4, 13.35) * mm});
            skLineSegment(sketch, "E2193", {"start": v(178.4, 13.35) * mm, "end": v(177.88, 13.75) * mm});
            skLineSegment(sketch, "E2194", {"start": v(177.88, 13.75) * mm, "end": v(177.49, 14.03) * mm});
            skLineSegment(sketch, "E2195", {"start": v(177.49, 14.03) * mm, "end": v(177.09, 14.29) * mm});
            skLineSegment(sketch, "E2196", {"start": v(177.09, 14.29) * mm, "end": v(176.68, 14.53) * mm});
            skLineSegment(sketch, "E2197", {"start": v(176.68, 14.53) * mm, "end": v(176.26, 14.75) * mm});
            skLineSegment(sketch, "E2198", {"start": v(176.26, 14.75) * mm, "end": v(175.83, 14.96) * mm});
            skLineSegment(sketch, "E2199", {"start": v(175.83, 14.96) * mm, "end": v(175.4, 15.15) * mm});
            skLineSegment(sketch, "E2200", {"start": v(175.4, 15.15) * mm, "end": v(174.97, 15.32) * mm});
            skLineSegment(sketch, "E2201", {"start": v(174.97, 15.32) * mm, "end": v(174.52, 15.47) * mm});
            skLineSegment(sketch, "E2202", {"start": v(174.52, 15.47) * mm, "end": v(174.07, 15.6) * mm});
            skLineSegment(sketch, "E2203", {"start": v(174.07, 15.6) * mm, "end": v(173.61, 15.72) * mm});
            skLineSegment(sketch, "E2204", {"start": v(173.61, 15.72) * mm, "end": v(173.15, 15.82) * mm});
            skLineSegment(sketch, "E2205", {"start": v(173.15, 15.82) * mm, "end": v(172.68, 15.9) * mm});
            skLineSegment(sketch, "E2206", {"start": v(172.68, 15.9) * mm, "end": v(172.2, 15.96) * mm});
            skLineSegment(sketch, "E2207", {"start": v(172.2, 15.96) * mm, "end": v(171.72, 16) * mm});
            skLineSegment(sketch, "E2208", {"start": v(171.72, 16) * mm, "end": v(171.23, 16.04) * mm});
            skLineSegment(sketch, "E2209", {"start": v(171.23, 16.04) * mm, "end": v(170.73, 16.04) * mm});
            skLineSegment(sketch, "E2210", {"start": v(170.73, 16.04) * mm, "end": v(157.68, 16.04) * mm});
            skLineSegment(sketch, "E2211", {"start": v(157.68, 16.04) * mm, "end": v(157.35, 16.03) * mm});
            skLineSegment(sketch, "E2212", {"start": v(157.35, 16.03) * mm, "end": v(157.02, 15.98) * mm});
            skLineSegment(sketch, "E2213", {"start": v(157.02, 15.98) * mm, "end": v(156.7, 15.9) * mm});
            skLineSegment(sketch, "E2214", {"start": v(156.7, 15.9) * mm, "end": v(156.4, 15.79) * mm});
            skLineSegment(sketch, "E2215", {"start": v(156.4, 15.79) * mm, "end": v(156.11, 15.65) * mm});
            skLineSegment(sketch, "E2216", {"start": v(156.11, 15.65) * mm, "end": v(155.84, 15.48) * mm});
            skLineSegment(sketch, "E2217", {"start": v(155.84, 15.48) * mm, "end": v(155.59, 15.3) * mm});
            skLineSegment(sketch, "E2218", {"start": v(155.59, 15.3) * mm, "end": v(155.35, 15.08) * mm});
            skLineSegment(sketch, "E2219", {"start": v(155.35, 15.08) * mm, "end": v(155.14, 14.85) * mm});
            skLineSegment(sketch, "E2220", {"start": v(155.14, 14.85) * mm, "end": v(154.95, 14.6) * mm});
            skLineSegment(sketch, "E2221", {"start": v(154.95, 14.6) * mm, "end": v(154.79, 14.32) * mm});
            skLineSegment(sketch, "E2222", {"start": v(154.79, 14.32) * mm, "end": v(154.65, 14.03) * mm});
            skLineSegment(sketch, "E2223", {"start": v(154.65, 14.03) * mm, "end": v(154.54, 13.73) * mm});
            skLineSegment(sketch, "E2224", {"start": v(154.54, 13.73) * mm, "end": v(154.46, 13.41) * mm});
            skLineSegment(sketch, "E2225", {"start": v(154.46, 13.41) * mm, "end": v(154.4, 13.09) * mm});
            skLineSegment(sketch, "E2226", {"start": v(154.4, 13.09) * mm, "end": v(154.39, 12.75) * mm});
            skLineSegment(sketch, "E2227", {"start": v(154.39, 12.75) * mm, "end": v(154.39, -22.53) * mm});
            skLineSegment(sketch, "E2228", {"start": v(154.39, -22.53) * mm, "end": v(154.39, -22.64) * mm});
            skLineSegment(sketch, "E2229", {"start": v(154.39, -22.64) * mm, "end": v(154.37, -22.74) * mm});
            skLineSegment(sketch, "E2230", {"start": v(154.37, -22.74) * mm, "end": v(154.35, -22.84) * mm});
            skLineSegment(sketch, "E2231", {"start": v(154.35, -22.84) * mm, "end": v(154.33, -22.93) * mm});
            skLineSegment(sketch, "E2232", {"start": v(154.33, -22.93) * mm, "end": v(154.3, -23.01) * mm});
            skLineSegment(sketch, "E2233", {"start": v(154.3, -23.01) * mm, "end": v(154.25, -23.09) * mm});
            skLineSegment(sketch, "E2234", {"start": v(154.25, -23.09) * mm, "end": v(154.2, -23.16) * mm});
            skLineSegment(sketch, "E2235", {"start": v(154.2, -23.16) * mm, "end": v(154.14, -23.22) * mm});
            skLineSegment(sketch, "E2236", {"start": v(154.14, -23.22) * mm, "end": v(154.07, -23.28) * mm});
            skLineSegment(sketch, "E2237", {"start": v(154.07, -23.28) * mm, "end": v(154, -23.33) * mm});
            skLineSegment(sketch, "E2238", {"start": v(154, -23.33) * mm, "end": v(153.91, -23.37) * mm});
            skLineSegment(sketch, "E2239", {"start": v(153.91, -23.37) * mm, "end": v(153.82, -23.4) * mm});
            skLineSegment(sketch, "E2240", {"start": v(153.82, -23.4) * mm, "end": v(153.72, -23.44) * mm});
            skLineSegment(sketch, "E2241", {"start": v(153.72, -23.44) * mm, "end": v(153.61, -23.46) * mm});
            skLineSegment(sketch, "E2242", {"start": v(153.61, -23.46) * mm, "end": v(153.5, -23.47) * mm});
            skLineSegment(sketch, "E2243", {"start": v(153.5, -23.47) * mm, "end": v(153.37, -23.48) * mm});
            skLineSegment(sketch, "E2244", {"start": v(153.37, -23.48) * mm, "end": v(152.53, -23.52) * mm});
            skLineSegment(sketch, "E2245", {"start": v(152.53, -23.52) * mm, "end": v(135.23, -23.49) * mm});
            skLineSegment(sketch, "E2246", {"start": v(135.23, -23.49) * mm, "end": v(135.17, -23.48) * mm});
            skLineSegment(sketch, "E2247", {"start": v(135.17, -23.48) * mm, "end": v(135.1, -23.47) * mm});
            skLineSegment(sketch, "E2248", {"start": v(135.1, -23.47) * mm, "end": v(135.05, -23.46) * mm});
            skLineSegment(sketch, "E2249", {"start": v(135.05, -23.46) * mm, "end": v(135, -23.44) * mm});
            skLineSegment(sketch, "E2250", {"start": v(135, -23.44) * mm, "end": v(134.95, -23.41) * mm});
            skLineSegment(sketch, "E2251", {"start": v(134.95, -23.41) * mm, "end": v(134.9, -23.38) * mm});
            skLineSegment(sketch, "E2252", {"start": v(134.9, -23.38) * mm, "end": v(134.85, -23.35) * mm});
            skLineSegment(sketch, "E2253", {"start": v(134.85, -23.35) * mm, "end": v(134.81, -23.31) * mm});
            skLineSegment(sketch, "E2254", {"start": v(134.81, -23.31) * mm, "end": v(134.77, -23.27) * mm});
            skLineSegment(sketch, "E2255", {"start": v(134.77, -23.27) * mm, "end": v(134.74, -23.23) * mm});
            skLineSegment(sketch, "E2256", {"start": v(134.74, -23.23) * mm, "end": v(134.71, -23.18) * mm});
            skLineSegment(sketch, "E2257", {"start": v(134.71, -23.18) * mm, "end": v(134.69, -23.13) * mm});
            skLineSegment(sketch, "E2258", {"start": v(134.69, -23.13) * mm, "end": v(134.67, -23.07) * mm});
            skLineSegment(sketch, "E2259", {"start": v(134.67, -23.07) * mm, "end": v(134.65, -23.02) * mm});
            skLineSegment(sketch, "E2260", {"start": v(134.65, -23.02) * mm, "end": v(134.64, -22.96) * mm});
            skLineSegment(sketch, "E2261", {"start": v(134.64, -22.96) * mm, "end": v(134.64, -22.9) * mm});
            skLineSegment(sketch, "E2262", {"start": v(134.64, -22.9) * mm, "end": v(134.64, -21.76) * mm});
            skLineSegment(sketch, "E2263", {"start": v(134.64, -21.76) * mm, "end": v(134.64, -21.69) * mm});
            skLineSegment(sketch, "E2264", {"start": v(134.64, -21.69) * mm, "end": v(134.65, -21.61) * mm});
            skLineSegment(sketch, "E2265", {"start": v(134.65, -21.61) * mm, "end": v(134.67, -21.54) * mm});
            skLineSegment(sketch, "E2266", {"start": v(134.67, -21.54) * mm, "end": v(134.69, -21.47) * mm});
            skLineSegment(sketch, "E2267", {"start": v(134.69, -21.47) * mm, "end": v(134.71, -21.4) * mm});
            skLineSegment(sketch, "E2268", {"start": v(134.71, -21.4) * mm, "end": v(134.74, -21.35) * mm});
            skLineSegment(sketch, "E2269", {"start": v(134.74, -21.35) * mm, "end": v(134.78, -21.28) * mm});
            skLineSegment(sketch, "E2270", {"start": v(134.78, -21.28) * mm, "end": v(134.82, -21.23) * mm});
            skLineSegment(sketch, "E2271", {"start": v(134.82, -21.23) * mm, "end": v(134.86, -21.17) * mm});
            skLineSegment(sketch, "E2272", {"start": v(134.86, -21.17) * mm, "end": v(134.91, -21.12) * mm});
            skLineSegment(sketch, "E2273", {"start": v(134.91, -21.12) * mm, "end": v(134.96, -21.08) * mm});
            skLineSegment(sketch, "E2274", {"start": v(134.96, -21.08) * mm, "end": v(135.02, -21.04) * mm});
            skLineSegment(sketch, "E2275", {"start": v(135.02, -21.04) * mm, "end": v(135.08, -21) * mm});
            skLineSegment(sketch, "E2276", {"start": v(135.08, -21) * mm, "end": v(135.14, -20.97) * mm});
            skLineSegment(sketch, "E2277", {"start": v(135.14, -20.97) * mm, "end": v(135.21, -20.94) * mm});
            skLineSegment(sketch, "E2278", {"start": v(135.21, -20.94) * mm, "end": v(135.28, -20.92) * mm});
            skLineSegment(sketch, "E2279", {"start": v(135.28, -20.92) * mm, "end": v(136.03, -20.72) * mm});
            skLineSegment(sketch, "E2280", {"start": v(136.03, -20.72) * mm, "end": v(136.76, -20.5) * mm});
            skLineSegment(sketch, "E2281", {"start": v(136.76, -20.5) * mm, "end": v(137.47, -20.24) * mm});
            skLineSegment(sketch, "E2282", {"start": v(137.47, -20.24) * mm, "end": v(138.17, -19.96) * mm});
            skLineSegment(sketch, "E2283", {"start": v(138.17, -19.96) * mm, "end": v(138.86, -19.65) * mm});
            skLineSegment(sketch, "E2284", {"start": v(138.86, -19.65) * mm, "end": v(139.53, -19.31) * mm});
            skLineSegment(sketch, "E2285", {"start": v(139.53, -19.31) * mm, "end": v(140.18, -18.95) * mm});
            skLineSegment(sketch, "E2286", {"start": v(140.18, -18.95) * mm, "end": v(140.82, -18.56) * mm});
            skLineSegment(sketch, "E2287", {"start": v(140.82, -18.56) * mm, "end": v(141.44, -18.14) * mm});
            skLineSegment(sketch, "E2288", {"start": v(141.44, -18.14) * mm, "end": v(142.05, -17.7) * mm});
            skLineSegment(sketch, "E2289", {"start": v(142.05, -17.7) * mm, "end": v(142.64, -17.23) * mm});
            skLineSegment(sketch, "E2290", {"start": v(142.64, -17.23) * mm, "end": v(143.2, -16.74) * mm});
            skLineSegment(sketch, "E2291", {"start": v(143.2, -16.74) * mm, "end": v(143.77, -16.21) * mm});
            skLineSegment(sketch, "E2292", {"start": v(143.77, -16.21) * mm, "end": v(144.3, -15.67) * mm});
            skLineSegment(sketch, "E2293", {"start": v(144.3, -15.67) * mm, "end": v(144.83, -15.1) * mm});
            skLineSegment(sketch, "E2294", {"start": v(144.83, -15.1) * mm, "end": v(145.33, -14.5) * mm});
            skLineSegment(sketch, "E2295", {"start": v(145.33, -14.5) * mm, "end": v(145.84, -13.84) * mm});
            skLineSegment(sketch, "E2296", {"start": v(145.84, -13.84) * mm, "end": v(146.32, -13.17) * mm});
            skLineSegment(sketch, "E2297", {"start": v(146.32, -13.17) * mm, "end": v(146.77, -12.5) * mm});
            skLineSegment(sketch, "E2298", {"start": v(146.77, -12.5) * mm, "end": v(147.18, -11.8) * mm});
            skLineSegment(sketch, "E2299", {"start": v(147.18, -11.8) * mm, "end": v(147.56, -11.1) * mm});
            skLineSegment(sketch, "E2300", {"start": v(147.56, -11.1) * mm, "end": v(147.9, -10.38) * mm});
            skLineSegment(sketch, "E2301", {"start": v(147.9, -10.38) * mm, "end": v(148.22, -9.66) * mm});
            skLineSegment(sketch, "E2302", {"start": v(148.22, -9.66) * mm, "end": v(148.5, -8.92) * mm});
            skLineSegment(sketch, "E2303", {"start": v(148.5, -8.92) * mm, "end": v(148.75, -8.17) * mm});
            skLineSegment(sketch, "E2304", {"start": v(148.75, -8.17) * mm, "end": v(148.96, -7.4) * mm});
            skLineSegment(sketch, "E2305", {"start": v(148.96, -7.4) * mm, "end": v(149.15, -6.64) * mm});
            skLineSegment(sketch, "E2306", {"start": v(149.15, -6.64) * mm, "end": v(149.3, -5.86) * mm});
            skLineSegment(sketch, "E2307", {"start": v(149.3, -5.86) * mm, "end": v(149.41, -5.07) * mm});
            skLineSegment(sketch, "E2308", {"start": v(149.41, -5.07) * mm, "end": v(149.5, -4.26) * mm});
            skLineSegment(sketch, "E2309", {"start": v(149.5, -4.26) * mm, "end": v(149.55, -3.45) * mm});
            skLineSegment(sketch, "E2310", {"start": v(149.55, -3.45) * mm, "end": v(149.56, -2.63) * mm});
            skLineSegment(sketch, "E2311", {"start": v(149.56, -2.63) * mm, "end": v(149.54, -1.65) * mm});
            skLineSegment(sketch, "E2312", {"start": v(149.54, -1.65) * mm, "end": v(149.48, -0.7) * mm});
            skLineSegment(sketch, "E2313", {"start": v(149.48, -0.7) * mm, "end": v(149.37, 0.25) * mm});
            skLineSegment(sketch, "E2314", {"start": v(149.37, 0.25) * mm, "end": v(149.22, 1.17) * mm});
            skLineSegment(sketch, "E2315", {"start": v(149.22, 1.17) * mm, "end": v(149.02, 2.08) * mm});
            skLineSegment(sketch, "E2316", {"start": v(149.02, 2.08) * mm, "end": v(148.78, 2.97) * mm});
            skLineSegment(sketch, "E2317", {"start": v(148.78, 2.97) * mm, "end": v(148.5, 3.84) * mm});
            skLineSegment(sketch, "E2318", {"start": v(148.5, 3.84) * mm, "end": v(148.18, 4.69) * mm});
            skLineSegment(sketch, "E2319", {"start": v(148.18, 4.69) * mm, "end": v(147.81, 5.52) * mm});
            skLineSegment(sketch, "E2320", {"start": v(147.81, 5.52) * mm, "end": v(147.4, 6.33) * mm});
            skLineSegment(sketch, "E2321", {"start": v(147.4, 6.33) * mm, "end": v(146.95, 7.13) * mm});
            skLineSegment(sketch, "E2322", {"start": v(146.95, 7.13) * mm, "end": v(146.46, 7.9) * mm});
            skLineSegment(sketch, "E2323", {"start": v(146.46, 7.9) * mm, "end": v(145.92, 8.66) * mm});
            skLineSegment(sketch, "E2324", {"start": v(145.92, 8.66) * mm, "end": v(145.34, 9.4) * mm});
            skLineSegment(sketch, "E2325", {"start": v(145.34, 9.4) * mm, "end": v(144.72, 10.1) * mm});
            skLineSegment(sketch, "E2326", {"start": v(144.72, 10.1) * mm, "end": v(144.06, 10.8) * mm});
            skLineSegment(sketch, "E2327", {"start": v(144.06, 10.8) * mm, "end": v(143.36, 11.47) * mm});
            skLineSegment(sketch, "E2328", {"start": v(143.36, 11.47) * mm, "end": v(142.65, 12.09) * mm});
            skLineSegment(sketch, "E2329", {"start": v(142.65, 12.09) * mm, "end": v(141.91, 12.67) * mm});
            skLineSegment(sketch, "E2330", {"start": v(141.91, 12.67) * mm, "end": v(141.16, 13.2) * mm});
            skLineSegment(sketch, "E2331", {"start": v(141.16, 13.2) * mm, "end": v(140.38, 13.7) * mm});
            skLineSegment(sketch, "E2332", {"start": v(140.38, 13.7) * mm, "end": v(139.59, 14.15) * mm});
            skLineSegment(sketch, "E2333", {"start": v(139.59, 14.15) * mm, "end": v(138.77, 14.56) * mm});
            skLineSegment(sketch, "E2334", {"start": v(138.77, 14.56) * mm, "end": v(137.94, 14.93) * mm});
            skLineSegment(sketch, "E2335", {"start": v(137.94, 14.93) * mm, "end": v(137.1, 15.25) * mm});
            skLineSegment(sketch, "E2336", {"start": v(137.1, 15.25) * mm, "end": v(136.22, 15.53) * mm});
            skLineSegment(sketch, "E2337", {"start": v(136.22, 15.53) * mm, "end": v(135.33, 15.77) * mm});
            skLineSegment(sketch, "E2338", {"start": v(135.33, 15.77) * mm, "end": v(134.43, 15.96) * mm});
            skLineSegment(sketch, "E2339", {"start": v(134.43, 15.96) * mm, "end": v(133.5, 16.11) * mm});
            skLineSegment(sketch, "E2340", {"start": v(133.5, 16.11) * mm, "end": v(132.56, 16.22) * mm});
            skLineSegment(sketch, "E2341", {"start": v(132.56, 16.22) * mm, "end": v(131.6, 16.29) * mm});
            skLineSegment(sketch, "E2342", {"start": v(131.6, 16.29) * mm, "end": v(130.62, 16.3) * mm});
            skLineSegment(sketch, "E2343", {"start": v(130.62, 16.3) * mm, "end": v(129.65, 16.29) * mm});
            skLineSegment(sketch, "E2344", {"start": v(129.65, 16.29) * mm, "end": v(128.7, 16.22) * mm});
            skLineSegment(sketch, "E2345", {"start": v(128.7, 16.22) * mm, "end": v(127.76, 16.11) * mm});
            skLineSegment(sketch, "E2346", {"start": v(127.76, 16.11) * mm, "end": v(126.84, 15.96) * mm});
            skLineSegment(sketch, "E2347", {"start": v(126.84, 15.96) * mm, "end": v(125.94, 15.77) * mm});
            skLineSegment(sketch, "E2348", {"start": v(125.94, 15.77) * mm, "end": v(125.06, 15.53) * mm});
            skLineSegment(sketch, "E2349", {"start": v(125.06, 15.53) * mm, "end": v(124.2, 15.25) * mm});
            skLineSegment(sketch, "E2350", {"start": v(124.2, 15.25) * mm, "end": v(123.34, 14.93) * mm});
            skLineSegment(sketch, "E2351", {"start": v(123.34, 14.93) * mm, "end": v(122.52, 14.56) * mm});
            skLineSegment(sketch, "E2352", {"start": v(122.52, 14.56) * mm, "end": v(121.7, 14.15) * mm});
            skLineSegment(sketch, "E2353", {"start": v(121.7, 14.15) * mm, "end": v(120.91, 13.7) * mm});
            skLineSegment(sketch, "E2354", {"start": v(120.91, 13.7) * mm, "end": v(120.14, 13.2) * mm});
            skLineSegment(sketch, "E2355", {"start": v(120.14, 13.2) * mm, "end": v(119.39, 12.67) * mm});
            skLineSegment(sketch, "E2356", {"start": v(119.39, 12.67) * mm, "end": v(118.65, 12.09) * mm});
            skLineSegment(sketch, "E2357", {"start": v(118.65, 12.09) * mm, "end": v(117.94, 11.47) * mm});
            skLineSegment(sketch, "E2358", {"start": v(117.94, 11.47) * mm, "end": v(117.24, 10.8) * mm});
            skLineSegment(sketch, "E2359", {"start": v(117.24, 10.8) * mm, "end": v(116.58, 10.1) * mm});
            skLineSegment(sketch, "E2360", {"start": v(116.58, 10.1) * mm, "end": v(115.96, 9.4) * mm});
            skLineSegment(sketch, "E2361", {"start": v(115.96, 9.4) * mm, "end": v(115.38, 8.66) * mm});
            skLineSegment(sketch, "E2362", {"start": v(115.38, 8.66) * mm, "end": v(114.84, 7.9) * mm});
            skLineSegment(sketch, "E2363", {"start": v(114.84, 7.9) * mm, "end": v(114.35, 7.13) * mm});
            skLineSegment(sketch, "E2364", {"start": v(114.35, 7.13) * mm, "end": v(113.9, 6.33) * mm});
            skLineSegment(sketch, "E2365", {"start": v(113.9, 6.33) * mm, "end": v(113.49, 5.52) * mm});
            skLineSegment(sketch, "E2366", {"start": v(113.49, 5.52) * mm, "end": v(113.12, 4.69) * mm});
            skLineSegment(sketch, "E2367", {"start": v(113.12, 4.69) * mm, "end": v(112.8, 3.84) * mm});
            skLineSegment(sketch, "E2368", {"start": v(112.8, 3.84) * mm, "end": v(112.52, 2.97) * mm});
            skLineSegment(sketch, "E2369", {"start": v(112.52, 2.97) * mm, "end": v(112.28, 2.08) * mm});
            skLineSegment(sketch, "E2370", {"start": v(112.28, 2.08) * mm, "end": v(112.08, 1.17) * mm});
            skLineSegment(sketch, "E2371", {"start": v(112.08, 1.17) * mm, "end": v(111.93, 0.25) * mm});
            skLineSegment(sketch, "E2372", {"start": v(111.93, 0.25) * mm, "end": v(111.83, -0.7) * mm});
            skLineSegment(sketch, "E2373", {"start": v(111.83, -0.7) * mm, "end": v(111.76, -1.65) * mm});
            skLineSegment(sketch, "E2374", {"start": v(111.76, -1.65) * mm, "end": v(111.74, -2.63) * mm});
            skLineSegment(sketch, "E2375", {"start": v(111.74, -2.63) * mm, "end": v(111.75, -3.45) * mm});
            skLineSegment(sketch, "E2376", {"start": v(111.75, -3.45) * mm, "end": v(111.8, -4.26) * mm});
            skLineSegment(sketch, "E2377", {"start": v(111.8, -4.26) * mm, "end": v(111.89, -5.07) * mm});
            skLineSegment(sketch, "E2378", {"start": v(111.89, -5.07) * mm, "end": v(112, -5.86) * mm});
            skLineSegment(sketch, "E2379", {"start": v(112, -5.86) * mm, "end": v(112.15, -6.64) * mm});
            skLineSegment(sketch, "E2380", {"start": v(112.15, -6.64) * mm, "end": v(112.34, -7.4) * mm});
            skLineSegment(sketch, "E2381", {"start": v(112.34, -7.4) * mm, "end": v(112.55, -8.17) * mm});
            skLineSegment(sketch, "E2382", {"start": v(112.55, -8.17) * mm, "end": v(112.8, -8.92) * mm});
            skLineSegment(sketch, "E2383", {"start": v(112.8, -8.92) * mm, "end": v(113.08, -9.66) * mm});
            skLineSegment(sketch, "E2384", {"start": v(113.08, -9.66) * mm, "end": v(113.4, -10.38) * mm});
            skLineSegment(sketch, "E2385", {"start": v(113.4, -10.38) * mm, "end": v(113.74, -11.1) * mm});
            skLineSegment(sketch, "E2386", {"start": v(113.74, -11.1) * mm, "end": v(114.12, -11.8) * mm});
            skLineSegment(sketch, "E2387", {"start": v(114.12, -11.8) * mm, "end": v(114.54, -12.5) * mm});
            skLineSegment(sketch, "E2388", {"start": v(114.54, -12.5) * mm, "end": v(114.98, -13.17) * mm});
            skLineSegment(sketch, "E2389", {"start": v(114.98, -13.17) * mm, "end": v(115.46, -13.84) * mm});
            skLineSegment(sketch, "E2390", {"start": v(115.46, -13.84) * mm, "end": v(115.97, -14.5) * mm});
            skLineSegment(sketch, "E2391", {"start": v(115.97, -14.5) * mm, "end": v(116.47, -15.1) * mm});
            skLineSegment(sketch, "E2392", {"start": v(116.47, -15.1) * mm, "end": v(117, -15.67) * mm});
            skLineSegment(sketch, "E2393", {"start": v(117, -15.67) * mm, "end": v(117.53, -16.21) * mm});
            skLineSegment(sketch, "E2394", {"start": v(117.53, -16.21) * mm, "end": v(118.1, -16.74) * mm});
            skLineSegment(sketch, "E2395", {"start": v(118.1, -16.74) * mm, "end": v(118.66, -17.23) * mm});
            skLineSegment(sketch, "E2396", {"start": v(118.66, -17.23) * mm, "end": v(119.25, -17.7) * mm});
            skLineSegment(sketch, "E2397", {"start": v(119.25, -17.7) * mm, "end": v(119.86, -18.14) * mm});
            skLineSegment(sketch, "E2398", {"start": v(119.86, -18.14) * mm, "end": v(120.48, -18.56) * mm});
            skLineSegment(sketch, "E2399", {"start": v(120.48, -18.56) * mm, "end": v(121.12, -18.95) * mm});
            skLineSegment(sketch, "E2400", {"start": v(121.12, -18.95) * mm, "end": v(121.77, -19.31) * mm});
            skLineSegment(sketch, "E2401", {"start": v(121.77, -19.31) * mm, "end": v(122.44, -19.65) * mm});
            skLineSegment(sketch, "E2402", {"start": v(122.44, -19.65) * mm, "end": v(123.13, -19.96) * mm});
            skLineSegment(sketch, "E2403", {"start": v(123.13, -19.96) * mm, "end": v(123.83, -20.24) * mm});
            skLineSegment(sketch, "E2404", {"start": v(123.83, -20.24) * mm, "end": v(124.54, -20.5) * mm});
            skLineSegment(sketch, "E2405", {"start": v(124.54, -20.5) * mm, "end": v(125.27, -20.72) * mm});
            skLineSegment(sketch, "E2406", {"start": v(125.27, -20.72) * mm, "end": v(126.02, -20.92) * mm});
            skLineSegment(sketch, "E2407", {"start": v(126.02, -20.92) * mm, "end": v(126.09, -20.94) * mm});
            skLineSegment(sketch, "E2408", {"start": v(126.09, -20.94) * mm, "end": v(126.16, -20.97) * mm});
            skLineSegment(sketch, "E2409", {"start": v(126.16, -20.97) * mm, "end": v(126.22, -21) * mm});
            skLineSegment(sketch, "E2410", {"start": v(126.22, -21) * mm, "end": v(126.28, -21.04) * mm});
            skLineSegment(sketch, "E2411", {"start": v(126.28, -21.04) * mm, "end": v(126.34, -21.08) * mm});
            skLineSegment(sketch, "E2412", {"start": v(126.34, -21.08) * mm, "end": v(126.39, -21.12) * mm});
            skLineSegment(sketch, "E2413", {"start": v(126.39, -21.12) * mm, "end": v(126.44, -21.17) * mm});
            skLineSegment(sketch, "E2414", {"start": v(126.44, -21.17) * mm, "end": v(126.48, -21.23) * mm});
            skLineSegment(sketch, "E2415", {"start": v(126.48, -21.23) * mm, "end": v(126.52, -21.28) * mm});
            skLineSegment(sketch, "E2416", {"start": v(126.52, -21.28) * mm, "end": v(126.56, -21.34) * mm});
            skLineSegment(sketch, "E2417", {"start": v(126.56, -21.34) * mm, "end": v(126.59, -21.4) * mm});
            skLineSegment(sketch, "E2418", {"start": v(126.59, -21.4) * mm, "end": v(126.61, -21.47) * mm});
            skLineSegment(sketch, "E2419", {"start": v(126.61, -21.47) * mm, "end": v(126.63, -21.54) * mm});
            skLineSegment(sketch, "E2420", {"start": v(126.63, -21.54) * mm, "end": v(126.65, -21.61) * mm});
            skLineSegment(sketch, "E2421", {"start": v(126.65, -21.61) * mm, "end": v(126.66, -21.69) * mm});
            skLineSegment(sketch, "E2422", {"start": v(126.66, -21.69) * mm, "end": v(126.66, -21.76) * mm});
            skLineSegment(sketch, "E2423", {"start": v(126.66, -21.76) * mm, "end": v(126.66, -22.9) * mm});
            skLineSegment(sketch, "E2424", {"start": v(126.66, -22.9) * mm, "end": v(126.66, -22.96) * mm});
            skLineSegment(sketch, "E2425", {"start": v(126.66, -22.96) * mm, "end": v(126.65, -23.02) * mm});
            skLineSegment(sketch, "E2426", {"start": v(126.65, -23.02) * mm, "end": v(126.63, -23.07) * mm});
            skLineSegment(sketch, "E2427", {"start": v(126.63, -23.07) * mm, "end": v(126.61, -23.13) * mm});
            skLineSegment(sketch, "E2428", {"start": v(126.61, -23.13) * mm, "end": v(126.59, -23.18) * mm});
            skLineSegment(sketch, "E2429", {"start": v(126.59, -23.18) * mm, "end": v(126.56, -23.23) * mm});
            skLineSegment(sketch, "E2430", {"start": v(126.56, -23.23) * mm, "end": v(126.53, -23.27) * mm});
            skLineSegment(sketch, "E2431", {"start": v(126.53, -23.27) * mm, "end": v(126.49, -23.31) * mm});
            skLineSegment(sketch, "E2432", {"start": v(126.49, -23.31) * mm, "end": v(126.45, -23.35) * mm});
            skLineSegment(sketch, "E2433", {"start": v(126.45, -23.35) * mm, "end": v(126.4, -23.38) * mm});
            skLineSegment(sketch, "E2434", {"start": v(126.4, -23.38) * mm, "end": v(126.35, -23.41) * mm});
            skLineSegment(sketch, "E2435", {"start": v(126.35, -23.41) * mm, "end": v(126.3, -23.44) * mm});
            skLineSegment(sketch, "E2436", {"start": v(126.3, -23.44) * mm, "end": v(126.25, -23.46) * mm});
            skLineSegment(sketch, "E2437", {"start": v(126.25, -23.46) * mm, "end": v(126.2, -23.47) * mm});
            skLineSegment(sketch, "E2438", {"start": v(126.2, -23.47) * mm, "end": v(126.13, -23.48) * mm});
            skLineSegment(sketch, "E2439", {"start": v(126.13, -23.48) * mm, "end": v(126.07, -23.48) * mm});
            skLineSegment(sketch, "E2440", {"start": v(126.07, -23.48) * mm, "end": v(95.18, -23.48) * mm});
            skLineSegment(sketch, "E2441", {"start": v(95.18, -23.48) * mm, "end": v(94.87, -23.47) * mm});
            skLineSegment(sketch, "E2442", {"start": v(94.87, -23.47) * mm, "end": v(94.56, -23.42) * mm});
            skLineSegment(sketch, "E2443", {"start": v(94.56, -23.42) * mm, "end": v(94.27, -23.35) * mm});
            skLineSegment(sketch, "E2444", {"start": v(94.27, -23.35) * mm, "end": v(93.98, -23.24) * mm});
            skLineSegment(sketch, "E2445", {"start": v(93.98, -23.24) * mm, "end": v(93.71, -23.11) * mm});
            skLineSegment(sketch, "E2446", {"start": v(93.71, -23.11) * mm, "end": v(93.46, -22.96) * mm});
            skLineSegment(sketch, "E2447", {"start": v(93.46, -22.96) * mm, "end": v(93.22, -22.78) * mm});
            skLineSegment(sketch, "E2448", {"start": v(93.22, -22.78) * mm, "end": v(93, -22.58) * mm});
            skLineSegment(sketch, "E2449", {"start": v(93, -22.58) * mm, "end": v(92.8, -22.36) * mm});
            skLineSegment(sketch, "E2450", {"start": v(92.8, -22.36) * mm, "end": v(92.62, -22.12) * mm});
            skLineSegment(sketch, "E2451", {"start": v(92.62, -22.12) * mm, "end": v(92.47, -21.87) * mm});
            skLineSegment(sketch, "E2452", {"start": v(92.47, -21.87) * mm, "end": v(92.34, -21.6) * mm});
            skLineSegment(sketch, "E2453", {"start": v(92.34, -21.6) * mm, "end": v(92.23, -21.31) * mm});
            skLineSegment(sketch, "E2454", {"start": v(92.23, -21.31) * mm, "end": v(92.16, -21.02) * mm});
            skLineSegment(sketch, "E2455", {"start": v(92.16, -21.02) * mm, "end": v(92.11, -20.7) * mm});
            skLineSegment(sketch, "E2456", {"start": v(92.11, -20.7) * mm, "end": v(92.1, -20.4) * mm});
            skLineSegment(sketch, "E2457", {"start": v(92.1, -20.4) * mm, "end": v(92.1, 7.6) * mm});
            skLineSegment(sketch, "E2458", {"start": v(92.1, 7.6) * mm, "end": v(92.1, 7.65) * mm});
            skLineSegment(sketch, "E2459", {"start": v(92.1, 7.65) * mm, "end": v(92.1, 7.7) * mm});
            skLineSegment(sketch, "E2460", {"start": v(92.1, 7.7) * mm, "end": v(92.12, 7.75) * mm});
            skLineSegment(sketch, "E2461", {"start": v(92.12, 7.75) * mm, "end": v(92.14, 7.8) * mm});
            skLineSegment(sketch, "E2462", {"start": v(92.14, 7.8) * mm, "end": v(92.16, 7.85) * mm});
            skLineSegment(sketch, "E2463", {"start": v(92.16, 7.85) * mm, "end": v(92.18, 7.89) * mm});
            skLineSegment(sketch, "E2464", {"start": v(92.18, 7.89) * mm, "end": v(92.21, 7.93) * mm});
            skLineSegment(sketch, "E2465", {"start": v(92.21, 7.93) * mm, "end": v(92.25, 7.97) * mm});
            skLineSegment(sketch, "E2466", {"start": v(92.25, 7.97) * mm, "end": v(92.28, 8) * mm});
            skLineSegment(sketch, "E2467", {"start": v(92.28, 8) * mm, "end": v(92.33, 8.03) * mm});
            skLineSegment(sketch, "E2468", {"start": v(92.33, 8.03) * mm, "end": v(92.37, 8.06) * mm});
            skLineSegment(sketch, "E2469", {"start": v(92.37, 8.06) * mm, "end": v(92.41, 8.08) * mm});
            skLineSegment(sketch, "E2470", {"start": v(92.41, 8.08) * mm, "end": v(92.46, 8.1) * mm});
            skLineSegment(sketch, "E2471", {"start": v(92.46, 8.1) * mm, "end": v(92.51, 8.1) * mm});
            skLineSegment(sketch, "E2472", {"start": v(92.51, 8.1) * mm, "end": v(92.56, 8.12) * mm});
            skLineSegment(sketch, "E2473", {"start": v(92.56, 8.12) * mm, "end": v(92.62, 8.12) * mm});
            skLineSegment(sketch, "E2474", {"start": v(92.62, 8.12) * mm, "end": v(102.95, 8.12) * mm});
            skLineSegment(sketch, "E2475", {"start": v(102.95, 8.12) * mm, "end": v(103.17, 8.12) * mm});
            skLineSegment(sketch, "E2476", {"start": v(103.17, 8.12) * mm, "end": v(103.38, 8.14) * mm});
            skLineSegment(sketch, "E2477", {"start": v(103.38, 8.14) * mm, "end": v(103.6, 8.16) * mm});
            skLineSegment(sketch, "E2478", {"start": v(103.6, 8.16) * mm, "end": v(103.8, 8.19) * mm});
            skLineSegment(sketch, "E2479", {"start": v(103.8, 8.19) * mm, "end": v(104, 8.23) * mm});
            skLineSegment(sketch, "E2480", {"start": v(104, 8.23) * mm, "end": v(104.19, 8.27) * mm});
            skLineSegment(sketch, "E2481", {"start": v(104.19, 8.27) * mm, "end": v(104.38, 8.33) * mm});
            skLineSegment(sketch, "E2482", {"start": v(104.38, 8.33) * mm, "end": v(104.56, 8.4) * mm});
            skLineSegment(sketch, "E2483", {"start": v(104.56, 8.4) * mm, "end": v(104.74, 8.46) * mm});
            skLineSegment(sketch, "E2484", {"start": v(104.74, 8.46) * mm, "end": v(104.9, 8.55) * mm});
            skLineSegment(sketch, "E2485", {"start": v(104.9, 8.55) * mm, "end": v(105.08, 8.63) * mm});
            skLineSegment(sketch, "E2486", {"start": v(105.08, 8.63) * mm, "end": v(105.24, 8.73) * mm});
            skLineSegment(sketch, "E2487", {"start": v(105.24, 8.73) * mm, "end": v(105.4, 8.84) * mm});
            skLineSegment(sketch, "E2488", {"start": v(105.4, 8.84) * mm, "end": v(105.54, 8.95) * mm});
            skLineSegment(sketch, "E2489", {"start": v(105.54, 8.95) * mm, "end": v(105.69, 9.08) * mm});
            skLineSegment(sketch, "E2490", {"start": v(105.69, 9.08) * mm, "end": v(105.82, 9.2) * mm});
            skLineSegment(sketch, "E2491", {"start": v(105.82, 9.2) * mm, "end": v(105.95, 9.34) * mm});
            skLineSegment(sketch, "E2492", {"start": v(105.95, 9.34) * mm, "end": v(106.08, 9.49) * mm});
            skLineSegment(sketch, "E2493", {"start": v(106.08, 9.49) * mm, "end": v(106.2, 9.64) * mm});
            skLineSegment(sketch, "E2494", {"start": v(106.2, 9.64) * mm, "end": v(106.3, 9.8) * mm});
            skLineSegment(sketch, "E2495", {"start": v(106.3, 9.8) * mm, "end": v(106.4, 9.95) * mm});
            skLineSegment(sketch, "E2496", {"start": v(106.4, 9.95) * mm, "end": v(106.49, 10.12) * mm});
            skLineSegment(sketch, "E2497", {"start": v(106.49, 10.12) * mm, "end": v(106.57, 10.3) * mm});
            skLineSegment(sketch, "E2498", {"start": v(106.57, 10.3) * mm, "end": v(106.64, 10.47) * mm});
            skLineSegment(sketch, "E2499", {"start": v(106.64, 10.47) * mm, "end": v(106.7, 10.65) * mm});
            skLineSegment(sketch, "E2500", {"start": v(106.7, 10.65) * mm, "end": v(106.76, 10.84) * mm});
            skLineSegment(sketch, "E2501", {"start": v(106.76, 10.84) * mm, "end": v(106.8, 11.03) * mm});
            skLineSegment(sketch, "E2502", {"start": v(106.8, 11.03) * mm, "end": v(106.84, 11.23) * mm});
            skLineSegment(sketch, "E2503", {"start": v(106.84, 11.23) * mm, "end": v(106.87, 11.44) * mm});
            skLineSegment(sketch, "E2504", {"start": v(106.87, 11.44) * mm, "end": v(106.9, 11.65) * mm});
            skLineSegment(sketch, "E2505", {"start": v(106.9, 11.65) * mm, "end": v(106.9, 11.86) * mm});
            skLineSegment(sketch, "E2506", {"start": v(106.9, 11.86) * mm, "end": v(106.91, 12.08) * mm});
            skLineSegment(sketch, "E2507", {"start": v(106.91, 12.08) * mm, "end": v(106.9, 12.3) * mm});
            skLineSegment(sketch, "E2508", {"start": v(106.9, 12.3) * mm, "end": v(106.9, 12.52) * mm});
            skLineSegment(sketch, "E2509", {"start": v(106.9, 12.52) * mm, "end": v(106.87, 12.73) * mm});
            skLineSegment(sketch, "E2510", {"start": v(106.87, 12.73) * mm, "end": v(106.84, 12.93) * mm});
            skLineSegment(sketch, "E2511", {"start": v(106.84, 12.93) * mm, "end": v(106.8, 13.13) * mm});
            skLineSegment(sketch, "E2512", {"start": v(106.8, 13.13) * mm, "end": v(106.76, 13.32) * mm});
            skLineSegment(sketch, "E2513", {"start": v(106.76, 13.32) * mm, "end": v(106.7, 13.5) * mm});
            skLineSegment(sketch, "E2514", {"start": v(106.7, 13.5) * mm, "end": v(106.64, 13.7) * mm});
            skLineSegment(sketch, "E2515", {"start": v(106.64, 13.7) * mm, "end": v(106.57, 13.87) * mm});
            skLineSegment(sketch, "E2516", {"start": v(106.57, 13.87) * mm, "end": v(106.49, 14.04) * mm});
            skLineSegment(sketch, "E2517", {"start": v(106.49, 14.04) * mm, "end": v(106.4, 14.2) * mm});
            skLineSegment(sketch, "E2518", {"start": v(106.4, 14.2) * mm, "end": v(106.3, 14.37) * mm});
            skLineSegment(sketch, "E2519", {"start": v(106.3, 14.37) * mm, "end": v(106.2, 14.52) * mm});
            skLineSegment(sketch, "E2520", {"start": v(106.2, 14.52) * mm, "end": v(106.08, 14.67) * mm});
            skLineSegment(sketch, "E2521", {"start": v(106.08, 14.67) * mm, "end": v(105.95, 14.82) * mm});
            skLineSegment(sketch, "E2522", {"start": v(105.95, 14.82) * mm, "end": v(105.82, 14.96) * mm});
            skLineSegment(sketch, "E2523", {"start": v(105.82, 14.96) * mm, "end": v(105.69, 15.09) * mm});
            skLineSegment(sketch, "E2524", {"start": v(105.69, 15.09) * mm, "end": v(105.54, 15.21) * mm});
            skLineSegment(sketch, "E2525", {"start": v(105.54, 15.21) * mm, "end": v(105.4, 15.33) * mm});
            skLineSegment(sketch, "E2526", {"start": v(105.4, 15.33) * mm, "end": v(105.24, 15.43) * mm});
            skLineSegment(sketch, "E2527", {"start": v(105.24, 15.43) * mm, "end": v(105.08, 15.53) * mm});
            skLineSegment(sketch, "E2528", {"start": v(105.08, 15.53) * mm, "end": v(104.9, 15.62) * mm});
            skLineSegment(sketch, "E2529", {"start": v(104.9, 15.62) * mm, "end": v(104.74, 15.7) * mm});
            skLineSegment(sketch, "E2530", {"start": v(104.74, 15.7) * mm, "end": v(104.56, 15.77) * mm});
            skLineSegment(sketch, "E2531", {"start": v(104.56, 15.77) * mm, "end": v(104.38, 15.84) * mm});
            skLineSegment(sketch, "E2532", {"start": v(104.38, 15.84) * mm, "end": v(104.19, 15.9) * mm});
            skLineSegment(sketch, "E2533", {"start": v(104.19, 15.9) * mm, "end": v(104, 15.94) * mm});
            skLineSegment(sketch, "E2534", {"start": v(104, 15.94) * mm, "end": v(103.8, 15.98) * mm});
            skLineSegment(sketch, "E2535", {"start": v(103.8, 15.98) * mm, "end": v(103.6, 16) * mm});
            skLineSegment(sketch, "E2536", {"start": v(103.6, 16) * mm, "end": v(103.38, 16.03) * mm});
            skLineSegment(sketch, "E2537", {"start": v(103.38, 16.03) * mm, "end": v(103.17, 16.04) * mm});
            skLineSegment(sketch, "E2538", {"start": v(103.17, 16.04) * mm, "end": v(102.95, 16.04) * mm});
            skLineSegment(sketch, "E2539", {"start": v(102.95, 16.04) * mm, "end": v(73.32, 16.04) * mm});
            skLineSegment(sketch, "E2540", {"start": v(73.32, 16.04) * mm, "end": v(73.1, 16.04) * mm});
            skLineSegment(sketch, "E2541", {"start": v(73.1, 16.04) * mm, "end": v(72.88, 16.03) * mm});
            skLineSegment(sketch, "E2542", {"start": v(72.88, 16.03) * mm, "end": v(72.67, 16) * mm});
            skLineSegment(sketch, "E2543", {"start": v(72.67, 16) * mm, "end": v(72.47, 15.98) * mm});
            skLineSegment(sketch, "E2544", {"start": v(72.47, 15.98) * mm, "end": v(72.27, 15.94) * mm});
            skLineSegment(sketch, "E2545", {"start": v(72.27, 15.94) * mm, "end": v(72.07, 15.9) * mm});
            skLineSegment(sketch, "E2546", {"start": v(72.07, 15.9) * mm, "end": v(71.89, 15.84) * mm});
            skLineSegment(sketch, "E2547", {"start": v(71.89, 15.84) * mm, "end": v(71.7, 15.77) * mm});
            skLineSegment(sketch, "E2548", {"start": v(71.7, 15.77) * mm, "end": v(71.53, 15.7) * mm});
            skLineSegment(sketch, "E2549", {"start": v(71.53, 15.7) * mm, "end": v(71.35, 15.62) * mm});
            skLineSegment(sketch, "E2550", {"start": v(71.35, 15.62) * mm, "end": v(71.19, 15.53) * mm});
            skLineSegment(sketch, "E2551", {"start": v(71.19, 15.53) * mm, "end": v(71.03, 15.43) * mm});
            skLineSegment(sketch, "E2552", {"start": v(71.03, 15.43) * mm, "end": v(70.87, 15.33) * mm});
            skLineSegment(sketch, "E2553", {"start": v(70.87, 15.33) * mm, "end": v(70.72, 15.21) * mm});
            skLineSegment(sketch, "E2554", {"start": v(70.72, 15.21) * mm, "end": v(70.58, 15.09) * mm});
            skLineSegment(sketch, "E2555", {"start": v(70.58, 15.09) * mm, "end": v(70.44, 14.96) * mm});
            skLineSegment(sketch, "E2556", {"start": v(70.44, 14.96) * mm, "end": v(70.3, 14.82) * mm});
            skLineSegment(sketch, "E2557", {"start": v(70.3, 14.82) * mm, "end": v(70.19, 14.67) * mm});
            skLineSegment(sketch, "E2558", {"start": v(70.19, 14.67) * mm, "end": v(70.07, 14.53) * mm});
            skLineSegment(sketch, "E2559", {"start": v(70.07, 14.53) * mm, "end": v(69.97, 14.37) * mm});
            skLineSegment(sketch, "E2560", {"start": v(69.97, 14.37) * mm, "end": v(69.87, 14.2) * mm});
            skLineSegment(sketch, "E2561", {"start": v(69.87, 14.2) * mm, "end": v(69.78, 14.04) * mm});
            skLineSegment(sketch, "E2562", {"start": v(69.78, 14.04) * mm, "end": v(69.7, 13.87) * mm});
            skLineSegment(sketch, "E2563", {"start": v(69.7, 13.87) * mm, "end": v(69.63, 13.7) * mm});
            skLineSegment(sketch, "E2564", {"start": v(69.63, 13.7) * mm, "end": v(69.56, 13.51) * mm});
            skLineSegment(sketch, "E2565", {"start": v(69.56, 13.51) * mm, "end": v(69.5, 13.32) * mm});
            skLineSegment(sketch, "E2566", {"start": v(69.5, 13.32) * mm, "end": v(69.46, 13.13) * mm});
            skLineSegment(sketch, "E2567", {"start": v(69.46, 13.13) * mm, "end": v(69.42, 12.93) * mm});
            skLineSegment(sketch, "E2568", {"start": v(69.42, 12.93) * mm, "end": v(69.4, 12.73) * mm});
            skLineSegment(sketch, "E2569", {"start": v(69.4, 12.73) * mm, "end": v(69.37, 12.52) * mm});
            skLineSegment(sketch, "E2570", {"start": v(69.37, 12.52) * mm, "end": v(69.36, 12.3) * mm});
            skLineSegment(sketch, "E2571", {"start": v(69.36, 12.3) * mm, "end": v(69.35, 12.08) * mm});
            skLineSegment(sketch, "E2572", {"start": v(69.35, 12.08) * mm, "end": v(69.36, 11.87) * mm});
            skLineSegment(sketch, "E2573", {"start": v(69.36, 11.87) * mm, "end": v(69.37, 11.66) * mm});
            skLineSegment(sketch, "E2574", {"start": v(69.37, 11.66) * mm, "end": v(69.4, 11.45) * mm});
            skLineSegment(sketch, "E2575", {"start": v(69.4, 11.45) * mm, "end": v(69.42, 11.25) * mm});
            skLineSegment(sketch, "E2576", {"start": v(69.42, 11.25) * mm, "end": v(69.46, 11.06) * mm});
            skLineSegment(sketch, "E2577", {"start": v(69.46, 11.06) * mm, "end": v(69.5, 10.87) * mm});
            skLineSegment(sketch, "E2578", {"start": v(69.5, 10.87) * mm, "end": v(69.57, 10.68) * mm});
            skLineSegment(sketch, "E2579", {"start": v(69.57, 10.68) * mm, "end": v(69.63, 10.5) * mm});
            skLineSegment(sketch, "E2580", {"start": v(69.63, 10.5) * mm, "end": v(69.7, 10.33) * mm});
            skLineSegment(sketch, "E2581", {"start": v(69.7, 10.33) * mm, "end": v(69.79, 10.16) * mm});
            skLineSegment(sketch, "E2582", {"start": v(69.79, 10.16) * mm, "end": v(69.88, 9.99) * mm});
            skLineSegment(sketch, "E2583", {"start": v(69.88, 9.99) * mm, "end": v(69.98, 9.83) * mm});
            skLineSegment(sketch, "E2584", {"start": v(69.98, 9.83) * mm, "end": v(70.09, 9.67) * mm});
            skLineSegment(sketch, "E2585", {"start": v(70.09, 9.67) * mm, "end": v(70.2, 9.52) * mm});
            skLineSegment(sketch, "E2586", {"start": v(70.2, 9.52) * mm, "end": v(70.33, 9.37) * mm});
            skLineSegment(sketch, "E2587", {"start": v(70.33, 9.37) * mm, "end": v(70.47, 9.23) * mm});
            skLineSegment(sketch, "E2588", {"start": v(70.47, 9.23) * mm, "end": v(70.6, 9.1) * mm});
            skLineSegment(sketch, "E2589", {"start": v(70.6, 9.1) * mm, "end": v(70.75, 8.97) * mm});
            skLineSegment(sketch, "E2590", {"start": v(70.75, 8.97) * mm, "end": v(70.9, 8.86) * mm});
            skLineSegment(sketch, "E2591", {"start": v(70.9, 8.86) * mm, "end": v(71.06, 8.75) * mm});
            skLineSegment(sketch, "E2592", {"start": v(71.06, 8.75) * mm, "end": v(71.22, 8.65) * mm});
            skLineSegment(sketch, "E2593", {"start": v(71.22, 8.65) * mm, "end": v(71.39, 8.56) * mm});
            skLineSegment(sketch, "E2594", {"start": v(71.39, 8.56) * mm, "end": v(71.56, 8.47) * mm});
            skLineSegment(sketch, "E2595", {"start": v(71.56, 8.47) * mm, "end": v(71.74, 8.4) * mm});
            skLineSegment(sketch, "E2596", {"start": v(71.74, 8.4) * mm, "end": v(71.92, 8.33) * mm});
            skLineSegment(sketch, "E2597", {"start": v(71.92, 8.33) * mm, "end": v(72.1, 8.28) * mm});
            skLineSegment(sketch, "E2598", {"start": v(72.1, 8.28) * mm, "end": v(72.3, 8.23) * mm});
            skLineSegment(sketch, "E2599", {"start": v(72.3, 8.23) * mm, "end": v(72.49, 8.19) * mm});
            skLineSegment(sketch, "E2600", {"start": v(72.49, 8.19) * mm, "end": v(72.69, 8.16) * mm});
            skLineSegment(sketch, "E2601", {"start": v(72.69, 8.16) * mm, "end": v(72.9, 8.14) * mm});
            skLineSegment(sketch, "E2602", {"start": v(72.9, 8.14) * mm, "end": v(73.1, 8.12) * mm});
            skLineSegment(sketch, "E2603", {"start": v(73.1, 8.12) * mm, "end": v(73.32, 8.12) * mm});
            skLineSegment(sketch, "E2604", {"start": v(73.32, 8.12) * mm, "end": v(83.65, 8.12) * mm});
            skLineSegment(sketch, "E2605", {"start": v(83.65, 8.12) * mm, "end": v(83.7, 8.12) * mm});
            skLineSegment(sketch, "E2606", {"start": v(83.7, 8.12) * mm, "end": v(83.75, 8.1) * mm});
            skLineSegment(sketch, "E2607", {"start": v(83.75, 8.1) * mm, "end": v(83.8, 8.1) * mm});
            skLineSegment(sketch, "E2608", {"start": v(83.8, 8.1) * mm, "end": v(83.85, 8.08) * mm});
            skLineSegment(sketch, "E2609", {"start": v(83.85, 8.08) * mm, "end": v(83.9, 8.06) * mm});
            skLineSegment(sketch, "E2610", {"start": v(83.9, 8.06) * mm, "end": v(83.94, 8.03) * mm});
            skLineSegment(sketch, "E2611", {"start": v(83.94, 8.03) * mm, "end": v(83.98, 8) * mm});
            skLineSegment(sketch, "E2612", {"start": v(83.98, 8) * mm, "end": v(84.02, 7.97) * mm});
            skLineSegment(sketch, "E2613", {"start": v(84.02, 7.97) * mm, "end": v(84.05, 7.93) * mm});
            skLineSegment(sketch, "E2614", {"start": v(84.05, 7.93) * mm, "end": v(84.08, 7.89) * mm});
            skLineSegment(sketch, "E2615", {"start": v(84.08, 7.89) * mm, "end": v(84.1, 7.85) * mm});
            skLineSegment(sketch, "E2616", {"start": v(84.1, 7.85) * mm, "end": v(84.13, 7.8) * mm});
            skLineSegment(sketch, "E2617", {"start": v(84.13, 7.8) * mm, "end": v(84.15, 7.75) * mm});
            skLineSegment(sketch, "E2618", {"start": v(84.15, 7.75) * mm, "end": v(84.16, 7.7) * mm});
            skLineSegment(sketch, "E2619", {"start": v(84.16, 7.7) * mm, "end": v(84.17, 7.65) * mm});
            skLineSegment(sketch, "E2620", {"start": v(84.17, 7.65) * mm, "end": v(84.17, 7.6) * mm});
            skLineSegment(sketch, "E2621", {"start": v(84.17, 7.6) * mm, "end": v(84.17, -20.4) * mm});
            skLineSegment(sketch, "E2622", {"start": v(84.17, -20.4) * mm, "end": v(84.15, -20.7) * mm});
            skLineSegment(sketch, "E2623", {"start": v(84.15, -20.7) * mm, "end": v(84.1, -21.02) * mm});
            skLineSegment(sketch, "E2624", {"start": v(84.1, -21.02) * mm, "end": v(84.03, -21.31) * mm});
            skLineSegment(sketch, "E2625", {"start": v(84.03, -21.31) * mm, "end": v(83.93, -21.6) * mm});
            skLineSegment(sketch, "E2626", {"start": v(83.93, -21.6) * mm, "end": v(83.8, -21.87) * mm});
            skLineSegment(sketch, "E2627", {"start": v(83.8, -21.87) * mm, "end": v(83.64, -22.12) * mm});
            skLineSegment(sketch, "E2628", {"start": v(83.64, -22.12) * mm, "end": v(83.46, -22.36) * mm});
            skLineSegment(sketch, "E2629", {"start": v(83.46, -22.36) * mm, "end": v(83.26, -22.58) * mm});
            skLineSegment(sketch, "E2630", {"start": v(83.26, -22.58) * mm, "end": v(83.04, -22.78) * mm});
            skLineSegment(sketch, "E2631", {"start": v(83.04, -22.78) * mm, "end": v(82.8, -22.96) * mm});
            skLineSegment(sketch, "E2632", {"start": v(82.8, -22.96) * mm, "end": v(82.55, -23.11) * mm});
            skLineSegment(sketch, "E2633", {"start": v(82.55, -23.11) * mm, "end": v(82.28, -23.24) * mm});
            skLineSegment(sketch, "E2634", {"start": v(82.28, -23.24) * mm, "end": v(82, -23.35) * mm});
            skLineSegment(sketch, "E2635", {"start": v(82, -23.35) * mm, "end": v(81.7, -23.42) * mm});
            skLineSegment(sketch, "E2636", {"start": v(81.7, -23.42) * mm, "end": v(81.4, -23.47) * mm});
            skLineSegment(sketch, "E2637", {"start": v(81.4, -23.47) * mm, "end": v(81.08, -23.48) * mm});
            skLineSegment(sketch, "E2638", {"start": v(81.08, -23.48) * mm, "end": v(45.27, -23.48) * mm});
            skLineSegment(sketch, "E2639", {"start": v(45.27, -23.48) * mm, "end": v(45.23, -23.48) * mm});
            skLineSegment(sketch, "E2640", {"start": v(45.23, -23.48) * mm, "end": v(45.18, -23.48) * mm});
            skLineSegment(sketch, "E2641", {"start": v(45.18, -23.48) * mm, "end": v(45.14, -23.46) * mm});
            skLineSegment(sketch, "E2642", {"start": v(45.14, -23.46) * mm, "end": v(45.1, -23.45) * mm});
            skLineSegment(sketch, "E2643", {"start": v(45.1, -23.45) * mm, "end": v(45.07, -23.43) * mm});
            skLineSegment(sketch, "E2644", {"start": v(45.07, -23.43) * mm, "end": v(45.03, -23.41) * mm});
            skLineSegment(sketch, "E2645", {"start": v(45.03, -23.41) * mm, "end": v(45, -23.39) * mm});
            skLineSegment(sketch, "E2646", {"start": v(45, -23.39) * mm, "end": v(44.97, -23.36) * mm});
            skLineSegment(sketch, "E2647", {"start": v(44.97, -23.36) * mm, "end": v(44.94, -23.33) * mm});
            skLineSegment(sketch, "E2648", {"start": v(44.94, -23.33) * mm, "end": v(44.91, -23.3) * mm});
            skLineSegment(sketch, "E2649", {"start": v(44.91, -23.3) * mm, "end": v(44.9, -23.26) * mm});
            skLineSegment(sketch, "E2650", {"start": v(44.9, -23.26) * mm, "end": v(44.87, -23.22) * mm});
            skLineSegment(sketch, "E2651", {"start": v(44.87, -23.22) * mm, "end": v(44.86, -23.18) * mm});
            skLineSegment(sketch, "E2652", {"start": v(44.86, -23.18) * mm, "end": v(44.85, -23.14) * mm});
            skLineSegment(sketch, "E2653", {"start": v(44.85, -23.14) * mm, "end": v(44.84, -23.1) * mm});
            skLineSegment(sketch, "E2654", {"start": v(44.84, -23.1) * mm, "end": v(44.84, -23.05) * mm});
            skLineSegment(sketch, "E2655", {"start": v(44.84, -23.05) * mm, "end": v(44.84, -7.35) * mm});
            skLineSegment(sketch, "E2656", {"start": v(44.84, -7.35) * mm, "end": v(44.84, -7.29) * mm});
            skLineSegment(sketch, "E2657", {"start": v(44.84, -7.29) * mm, "end": v(44.85, -7.22) * mm});
            skLineSegment(sketch, "E2658", {"start": v(44.85, -7.22) * mm, "end": v(44.87, -7.16) * mm});
            skLineSegment(sketch, "E2659", {"start": v(44.87, -7.16) * mm, "end": v(44.9, -7.1) * mm});
            skLineSegment(sketch, "E2660", {"start": v(44.9, -7.1) * mm, "end": v(44.92, -7.04) * mm});
            skLineSegment(sketch, "E2661", {"start": v(44.92, -7.04) * mm, "end": v(44.95, -6.99) * mm});
            skLineSegment(sketch, "E2662", {"start": v(44.95, -6.99) * mm, "end": v(45, -6.94) * mm});
            skLineSegment(sketch, "E2663", {"start": v(45, -6.94) * mm, "end": v(45.03, -6.9) * mm});
            skLineSegment(sketch, "E2664", {"start": v(45.03, -6.9) * mm, "end": v(45.08, -6.85) * mm});
            skLineSegment(sketch, "E2665", {"start": v(45.08, -6.85) * mm, "end": v(45.13, -6.81) * mm});
            skLineSegment(sketch, "E2666", {"start": v(45.13, -6.81) * mm, "end": v(45.18, -6.78) * mm});
            skLineSegment(sketch, "E2667", {"start": v(45.18, -6.78) * mm, "end": v(45.24, -6.75) * mm});
            skLineSegment(sketch, "E2668", {"start": v(45.24, -6.75) * mm, "end": v(45.3, -6.73) * mm});
            skLineSegment(sketch, "E2669", {"start": v(45.3, -6.73) * mm, "end": v(45.36, -6.71) * mm});
            skLineSegment(sketch, "E2670", {"start": v(45.36, -6.71) * mm, "end": v(45.43, -6.7) * mm});
            skLineSegment(sketch, "E2671", {"start": v(45.43, -6.7) * mm, "end": v(45.5, -6.7) * mm});
            skLineSegment(sketch, "E2672", {"start": v(45.5, -6.7) * mm, "end": v(53.26, -6.7) * mm});
            skLineSegment(sketch, "E2673", {"start": v(53.26, -6.7) * mm, "end": v(53.75, -6.69) * mm});
            skLineSegment(sketch, "E2674", {"start": v(53.75, -6.69) * mm, "end": v(54.24, -6.66) * mm});
            skLineSegment(sketch, "E2675", {"start": v(54.24, -6.66) * mm, "end": v(54.73, -6.62) * mm});
            skLineSegment(sketch, "E2676", {"start": v(54.73, -6.62) * mm, "end": v(55.2, -6.55) * mm});
            skLineSegment(sketch, "E2677", {"start": v(55.2, -6.55) * mm, "end": v(55.67, -6.47) * mm});
            skLineSegment(sketch, "E2678", {"start": v(55.67, -6.47) * mm, "end": v(56.14, -6.37) * mm});
            skLineSegment(sketch, "E2679", {"start": v(56.14, -6.37) * mm, "end": v(56.6, -6.26) * mm});
            skLineSegment(sketch, "E2680", {"start": v(56.6, -6.26) * mm, "end": v(57.05, -6.12) * mm});
            skLineSegment(sketch, "E2681", {"start": v(57.05, -6.12) * mm, "end": v(57.5, -5.97) * mm});
            skLineSegment(sketch, "E2682", {"start": v(57.5, -5.97) * mm, "end": v(57.93, -5.8) * mm});
            skLineSegment(sketch, "E2683", {"start": v(57.93, -5.8) * mm, "end": v(58.36, -5.61) * mm});
            skLineSegment(sketch, "E2684", {"start": v(58.36, -5.61) * mm, "end": v(58.78, -5.4) * mm});
            skLineSegment(sketch, "E2685", {"start": v(58.78, -5.4) * mm, "end": v(59.2, -5.18) * mm});
            skLineSegment(sketch, "E2686", {"start": v(59.2, -5.18) * mm, "end": v(59.61, -4.94) * mm});
            skLineSegment(sketch, "E2687", {"start": v(59.61, -4.94) * mm, "end": v(60.01, -4.68) * mm});
            skLineSegment(sketch, "E2688", {"start": v(60.01, -4.68) * mm, "end": v(60.41, -4.4) * mm});
            skLineSegment(sketch, "E2689", {"start": v(60.41, -4.4) * mm, "end": v(60.92, -4) * mm});
            skLineSegment(sketch, "E2690", {"start": v(60.92, -4) * mm, "end": v(61.4, -3.59) * mm});
            skLineSegment(sketch, "E2691", {"start": v(61.4, -3.59) * mm, "end": v(61.84, -3.14) * mm});
            skLineSegment(sketch, "E2692", {"start": v(61.84, -3.14) * mm, "end": v(62.25, -2.68) * mm});
            skLineSegment(sketch, "E2693", {"start": v(62.25, -2.68) * mm, "end": v(62.63, -2.19) * mm});
            skLineSegment(sketch, "E2694", {"start": v(62.63, -2.19) * mm, "end": v(62.98, -1.67) * mm});
            skLineSegment(sketch, "E2695", {"start": v(62.98, -1.67) * mm, "end": v(63.3, -1.14) * mm});
            skLineSegment(sketch, "E2696", {"start": v(63.3, -1.14) * mm, "end": v(63.57, -0.58) * mm});
            skLineSegment(sketch, "E2697", {"start": v(63.57, -0.58) * mm, "end": v(63.82, 0) * mm});
            skLineSegment(sketch, "E2698", {"start": v(63.82, 0) * mm, "end": v(64.03, 0.6) * mm});
            skLineSegment(sketch, "E2699", {"start": v(64.03, 0.6) * mm, "end": v(64.22, 1.22) * mm});
            skLineSegment(sketch, "E2700", {"start": v(64.22, 1.22) * mm, "end": v(64.37, 1.87) * mm});
            skLineSegment(sketch, "E2701", {"start": v(64.37, 1.87) * mm, "end": v(64.48, 2.54) * mm});
            skLineSegment(sketch, "E2702", {"start": v(64.48, 2.54) * mm, "end": v(64.56, 3.23) * mm});
            skLineSegment(sketch, "E2703", {"start": v(64.56, 3.23) * mm, "end": v(64.61, 3.94) * mm});
            skLineSegment(sketch, "E2704", {"start": v(64.61, 3.94) * mm, "end": v(64.63, 4.67) * mm});
            skLineSegment(sketch, "E2705", {"start": v(64.63, 4.67) * mm, "end": v(64.61, 5.4) * mm});
            skLineSegment(sketch, "E2706", {"start": v(64.61, 5.4) * mm, "end": v(64.56, 6.12) * mm});
            skLineSegment(sketch, "E2707", {"start": v(64.56, 6.12) * mm, "end": v(64.48, 6.8) * mm});
            skLineSegment(sketch, "E2708", {"start": v(64.48, 6.8) * mm, "end": v(64.37, 7.48) * mm});
            skLineSegment(sketch, "E2709", {"start": v(64.37, 7.48) * mm, "end": v(64.22, 8.12) * mm});
            skLineSegment(sketch, "E2710", {"start": v(64.22, 8.12) * mm, "end": v(64.03, 8.75) * mm});
            skLineSegment(sketch, "E2711", {"start": v(64.03, 8.75) * mm, "end": v(63.82, 9.35) * mm});
            skLineSegment(sketch, "E2712", {"start": v(63.82, 9.35) * mm, "end": v(63.57, 9.93) * mm});
            skLineSegment(sketch, "E2713", {"start": v(63.57, 9.93) * mm, "end": v(63.3, 10.48) * mm});
            skLineSegment(sketch, "E2714", {"start": v(63.3, 10.48) * mm, "end": v(62.98, 11.02) * mm});
            skLineSegment(sketch, "E2715", {"start": v(62.98, 11.02) * mm, "end": v(62.63, 11.53) * mm});
            skLineSegment(sketch, "E2716", {"start": v(62.63, 11.53) * mm, "end": v(62.25, 12.02) * mm});
            skLineSegment(sketch, "E2717", {"start": v(62.25, 12.02) * mm, "end": v(61.84, 12.49) * mm});
            skLineSegment(sketch, "E2718", {"start": v(61.84, 12.49) * mm, "end": v(61.4, 12.93) * mm});
            skLineSegment(sketch, "E2719", {"start": v(61.4, 12.93) * mm, "end": v(60.92, 13.35) * mm});
            skLineSegment(sketch, "E2720", {"start": v(60.92, 13.35) * mm, "end": v(60.4, 13.75) * mm});
            skLineSegment(sketch, "E2721", {"start": v(60.4, 13.75) * mm, "end": v(60.01, 14.03) * mm});
            skLineSegment(sketch, "E2722", {"start": v(60.01, 14.03) * mm, "end": v(59.61, 14.29) * mm});
            skLineSegment(sketch, "E2723", {"start": v(59.61, 14.29) * mm, "end": v(59.2, 14.53) * mm});
            skLineSegment(sketch, "E2724", {"start": v(59.2, 14.53) * mm, "end": v(58.78, 14.75) * mm});
            skLineSegment(sketch, "E2725", {"start": v(58.78, 14.75) * mm, "end": v(58.36, 14.96) * mm});
            skLineSegment(sketch, "E2726", {"start": v(58.36, 14.96) * mm, "end": v(57.93, 15.15) * mm});
            skLineSegment(sketch, "E2727", {"start": v(57.93, 15.15) * mm, "end": v(57.5, 15.32) * mm});
            skLineSegment(sketch, "E2728", {"start": v(57.5, 15.32) * mm, "end": v(57.05, 15.47) * mm});
            skLineSegment(sketch, "E2729", {"start": v(57.05, 15.47) * mm, "end": v(56.6, 15.6) * mm});
            skLineSegment(sketch, "E2730", {"start": v(56.6, 15.6) * mm, "end": v(56.14, 15.72) * mm});
            skLineSegment(sketch, "E2731", {"start": v(56.14, 15.72) * mm, "end": v(55.67, 15.82) * mm});
            skLineSegment(sketch, "E2732", {"start": v(55.67, 15.82) * mm, "end": v(55.2, 15.9) * mm});
            skLineSegment(sketch, "E2733", {"start": v(55.2, 15.9) * mm, "end": v(54.73, 15.96) * mm});
            skLineSegment(sketch, "E2734", {"start": v(54.73, 15.96) * mm, "end": v(54.24, 16) * mm});
            skLineSegment(sketch, "E2735", {"start": v(54.24, 16) * mm, "end": v(53.75, 16.04) * mm});
            skLineSegment(sketch, "E2736", {"start": v(53.75, 16.04) * mm, "end": v(53.26, 16.04) * mm});
            skLineSegment(sketch, "E2737", {"start": v(53.26, 16.04) * mm, "end": v(39.5, 16.04) * mm});
            skLineSegment(sketch, "E2738", {"start": v(39.5, 16.04) * mm, "end": v(39.24, 16.03) * mm});
            skLineSegment(sketch, "E2739", {"start": v(39.24, 16.03) * mm, "end": v(38.98, 16) * mm});
            skLineSegment(sketch, "E2740", {"start": v(38.98, 16) * mm, "end": v(38.74, 15.93) * mm});
            skLineSegment(sketch, "E2741", {"start": v(38.74, 15.93) * mm, "end": v(38.5, 15.84) * mm});
            skLineSegment(sketch, "E2742", {"start": v(38.5, 15.84) * mm, "end": v(38.27, 15.73) * mm});
            skLineSegment(sketch, "E2743", {"start": v(38.27, 15.73) * mm, "end": v(38.06, 15.6) * mm});
            skLineSegment(sketch, "E2744", {"start": v(38.06, 15.6) * mm, "end": v(37.86, 15.45) * mm});
            skLineSegment(sketch, "E2745", {"start": v(37.86, 15.45) * mm, "end": v(37.67, 15.29) * mm});
            skLineSegment(sketch, "E2746", {"start": v(37.67, 15.29) * mm, "end": v(37.5, 15.1) * mm});
            skLineSegment(sketch, "E2747", {"start": v(37.5, 15.1) * mm, "end": v(37.36, 14.9) * mm});
            skLineSegment(sketch, "E2748", {"start": v(37.36, 14.9) * mm, "end": v(37.23, 14.69) * mm});
            skLineSegment(sketch, "E2749", {"start": v(37.23, 14.69) * mm, "end": v(37.12, 14.46) * mm});
            skLineSegment(sketch, "E2750", {"start": v(37.12, 14.46) * mm, "end": v(37.03, 14.22) * mm});
            skLineSegment(sketch, "E2751", {"start": v(37.03, 14.22) * mm, "end": v(36.97, 13.98) * mm});
            skLineSegment(sketch, "E2752", {"start": v(36.97, 13.98) * mm, "end": v(36.93, 13.72) * mm});
            skLineSegment(sketch, "E2753", {"start": v(36.93, 13.72) * mm, "end": v(36.91, 13.45) * mm});
            skLineSegment(sketch, "E2754", {"start": v(36.91, 13.45) * mm, "end": v(36.91, -22.53) * mm});
            skLineSegment(sketch, "E2755", {"start": v(36.91, -22.53) * mm, "end": v(36.91, -22.64) * mm});
            skLineSegment(sketch, "E2756", {"start": v(36.91, -22.64) * mm, "end": v(36.9, -22.74) * mm});
            skLineSegment(sketch, "E2757", {"start": v(36.9, -22.74) * mm, "end": v(36.88, -22.84) * mm});
            skLineSegment(sketch, "E2758", {"start": v(36.88, -22.84) * mm, "end": v(36.85, -22.93) * mm});
            skLineSegment(sketch, "E2759", {"start": v(36.85, -22.93) * mm, "end": v(36.82, -23.01) * mm});
            skLineSegment(sketch, "E2760", {"start": v(36.82, -23.01) * mm, "end": v(36.77, -23.09) * mm});
            skLineSegment(sketch, "E2761", {"start": v(36.77, -23.09) * mm, "end": v(36.72, -23.16) * mm});
            skLineSegment(sketch, "E2762", {"start": v(36.72, -23.16) * mm, "end": v(36.66, -23.22) * mm});
            skLineSegment(sketch, "E2763", {"start": v(36.66, -23.22) * mm, "end": v(36.6, -23.28) * mm});
            skLineSegment(sketch, "E2764", {"start": v(36.6, -23.28) * mm, "end": v(36.52, -23.33) * mm});
            skLineSegment(sketch, "E2765", {"start": v(36.52, -23.33) * mm, "end": v(36.44, -23.37) * mm});
            skLineSegment(sketch, "E2766", {"start": v(36.44, -23.37) * mm, "end": v(36.35, -23.4) * mm});
            skLineSegment(sketch, "E2767", {"start": v(36.35, -23.4) * mm, "end": v(36.25, -23.44) * mm});
            skLineSegment(sketch, "E2768", {"start": v(36.25, -23.44) * mm, "end": v(36.14, -23.46) * mm});
            skLineSegment(sketch, "E2769", {"start": v(36.14, -23.46) * mm, "end": v(36.03, -23.47) * mm});
            skLineSegment(sketch, "E2770", {"start": v(36.03, -23.47) * mm, "end": v(35.9, -23.48) * mm});
            skLineSegment(sketch, "E2771", {"start": v(35.9, -23.48) * mm, "end": v(33.5, -23.48) * mm});
            skLineSegment(sketch, "E2772", {"start": v(33.5, -23.48) * mm, "end": v(33.46, -23.48) * mm});
            skLineSegment(sketch, "E2773", {"start": v(33.46, -23.48) * mm, "end": v(33.43, -23.48) * mm});
            skLineSegment(sketch, "E2774", {"start": v(33.43, -23.48) * mm, "end": v(33.39, -23.47) * mm});
            skLineSegment(sketch, "E2775", {"start": v(33.39, -23.47) * mm, "end": v(33.35, -23.46) * mm});
            skLineSegment(sketch, "E2776", {"start": v(33.35, -23.46) * mm, "end": v(33.31, -23.45) * mm});
            skLineSegment(sketch, "E2777", {"start": v(33.31, -23.45) * mm, "end": v(33.28, -23.44) * mm});
            skLineSegment(sketch, "E2778", {"start": v(33.28, -23.44) * mm, "end": v(33.25, -23.42) * mm});
            skLineSegment(sketch, "E2779", {"start": v(33.25, -23.42) * mm, "end": v(33.21, -23.4) * mm});
            skLineSegment(sketch, "E2780", {"start": v(33.21, -23.4) * mm, "end": v(33.18, -23.38) * mm});
            skLineSegment(sketch, "E2781", {"start": v(33.18, -23.38) * mm, "end": v(33.15, -23.36) * mm});
            skLineSegment(sketch, "E2782", {"start": v(33.15, -23.36) * mm, "end": v(33.12, -23.33) * mm});
            skLineSegment(sketch, "E2783", {"start": v(33.12, -23.33) * mm, "end": v(33.1, -23.3) * mm});
            skLineSegment(sketch, "E2784", {"start": v(33.1, -23.3) * mm, "end": v(33.07, -23.28) * mm});
            skLineSegment(sketch, "E2785", {"start": v(33.07, -23.28) * mm, "end": v(33.05, -23.25) * mm});
            skLineSegment(sketch, "E2786", {"start": v(33.05, -23.25) * mm, "end": v(33.03, -23.21) * mm});
            skLineSegment(sketch, "E2787", {"start": v(33.03, -23.21) * mm, "end": v(33, -23.18) * mm});
            skLineSegment(sketch, "E2788", {"start": v(33, -23.18) * mm, "end": v(26.3, -9.7) * mm});
            skLineSegment(sketch, "E2789", {"start": v(26.3, -9.7) * mm, "end": v(26.23, -9.58) * mm});
            skLineSegment(sketch, "E2790", {"start": v(26.23, -9.58) * mm, "end": v(26.15, -9.46) * mm});
            skLineSegment(sketch, "E2791", {"start": v(26.15, -9.46) * mm, "end": v(26.07, -9.35) * mm});
            skLineSegment(sketch, "E2792", {"start": v(26.07, -9.35) * mm, "end": v(25.98, -9.25) * mm});
            skLineSegment(sketch, "E2793", {"start": v(25.98, -9.25) * mm, "end": v(25.9, -9.15) * mm});
            skLineSegment(sketch, "E2794", {"start": v(25.9, -9.15) * mm, "end": v(25.79, -9.06) * mm});
            skLineSegment(sketch, "E2795", {"start": v(25.79, -9.06) * mm, "end": v(25.68, -8.98) * mm});
            skLineSegment(sketch, "E2796", {"start": v(25.68, -8.98) * mm, "end": v(25.57, -8.9) * mm});
            skLineSegment(sketch, "E2797", {"start": v(25.57, -8.9) * mm, "end": v(25.46, -8.84) * mm});
            skLineSegment(sketch, "E2798", {"start": v(25.46, -8.84) * mm, "end": v(25.34, -8.78) * mm});
            skLineSegment(sketch, "E2799", {"start": v(25.34, -8.78) * mm, "end": v(25.21, -8.73) * mm});
            skLineSegment(sketch, "E2800", {"start": v(25.21, -8.73) * mm, "end": v(25.08, -8.7) * mm});
            skLineSegment(sketch, "E2801", {"start": v(25.08, -8.7) * mm, "end": v(24.95, -8.66) * mm});
            skLineSegment(sketch, "E2802", {"start": v(24.95, -8.66) * mm, "end": v(24.82, -8.63) * mm});
            skLineSegment(sketch, "E2803", {"start": v(24.82, -8.63) * mm, "end": v(24.68, -8.62) * mm});
            skLineSegment(sketch, "E2804", {"start": v(24.68, -8.62) * mm, "end": v(24.54, -8.61) * mm});
            skLineSegment(sketch, "E2805", {"start": v(24.54, -8.61) * mm, "end": v(9.92, -8.61) * mm});
            skLineSegment(sketch, "E2806", {"start": v(9.92, -8.61) * mm, "end": v(9.8, -8.61) * mm});
            skLineSegment(sketch, "E2807", {"start": v(9.8, -8.61) * mm, "end": v(9.68, -8.6) * mm});
            skLineSegment(sketch, "E2808", {"start": v(9.68, -8.6) * mm, "end": v(9.57, -8.58) * mm});
            skLineSegment(sketch, "E2809", {"start": v(9.57, -8.58) * mm, "end": v(9.47, -8.56) * mm});
            skLineSegment(sketch, "E2810", {"start": v(9.47, -8.56) * mm, "end": v(9.38, -8.52) * mm});
            skLineSegment(sketch, "E2811", {"start": v(9.38, -8.52) * mm, "end": v(9.3, -8.48) * mm});
            skLineSegment(sketch, "E2812", {"start": v(9.3, -8.48) * mm, "end": v(9.22, -8.43) * mm});
            skLineSegment(sketch, "E2813", {"start": v(9.22, -8.43) * mm, "end": v(9.16, -8.37) * mm});
            skLineSegment(sketch, "E2814", {"start": v(9.16, -8.37) * mm, "end": v(9.1, -8.3) * mm});
            skLineSegment(sketch, "E2815", {"start": v(9.1, -8.3) * mm, "end": v(9.05, -8.24) * mm});
            skLineSegment(sketch, "E2816", {"start": v(9.05, -8.24) * mm, "end": v(9, -8.16) * mm});
            skLineSegment(sketch, "E2817", {"start": v(9, -8.16) * mm, "end": v(8.97, -8.07) * mm});
            skLineSegment(sketch, "E2818", {"start": v(8.97, -8.07) * mm, "end": v(8.94, -7.97) * mm});
            skLineSegment(sketch, "E2819", {"start": v(8.94, -7.97) * mm, "end": v(8.93, -7.87) * mm});
            skLineSegment(sketch, "E2820", {"start": v(8.93, -7.87) * mm, "end": v(8.91, -7.75) * mm});
            skLineSegment(sketch, "E2821", {"start": v(8.91, -7.75) * mm, "end": v(8.91, -7.63) * mm});
            skLineSegment(sketch, "E2822", {"start": v(8.91, -7.63) * mm, "end": v(8.91, -7.52) * mm});
            skLineSegment(sketch, "E2823", {"start": v(8.91, -7.52) * mm, "end": v(8.93, -7.4) * mm});
            skLineSegment(sketch, "E2824", {"start": v(8.93, -7.4) * mm, "end": v(8.94, -7.3) * mm});
            skLineSegment(sketch, "E2825", {"start": v(8.94, -7.3) * mm, "end": v(8.97, -7.22) * mm});
            skLineSegment(sketch, "E2826", {"start": v(8.97, -7.22) * mm, "end": v(9, -7.13) * mm});
            skLineSegment(sketch, "E2827", {"start": v(9, -7.13) * mm, "end": v(9.05, -7.06) * mm});
            skLineSegment(sketch, "E2828", {"start": v(9.05, -7.06) * mm, "end": v(9.1, -6.99) * mm});
            skLineSegment(sketch, "E2829", {"start": v(9.1, -6.99) * mm, "end": v(9.16, -6.93) * mm});
            skLineSegment(sketch, "E2830", {"start": v(9.16, -6.93) * mm, "end": v(9.22, -6.87) * mm});
            skLineSegment(sketch, "E2831", {"start": v(9.22, -6.87) * mm, "end": v(9.3, -6.83) * mm});
            skLineSegment(sketch, "E2832", {"start": v(9.3, -6.83) * mm, "end": v(9.38, -6.79) * mm});
            skLineSegment(sketch, "E2833", {"start": v(9.38, -6.79) * mm, "end": v(9.47, -6.75) * mm});
            skLineSegment(sketch, "E2834", {"start": v(9.47, -6.75) * mm, "end": v(9.57, -6.73) * mm});
            skLineSegment(sketch, "E2835", {"start": v(9.57, -6.73) * mm, "end": v(9.68, -6.71) * mm});
            skLineSegment(sketch, "E2836", {"start": v(9.68, -6.71) * mm, "end": v(9.8, -6.7) * mm});
            skLineSegment(sketch, "E2837", {"start": v(9.8, -6.7) * mm, "end": v(9.92, -6.7) * mm});
            skLineSegment(sketch, "E2838", {"start": v(9.92, -6.7) * mm, "end": v(21.86, -6.7) * mm});
            skLineSegment(sketch, "E2839", {"start": v(21.86, -6.7) * mm, "end": v(21.98, -6.7) * mm});
            skLineSegment(sketch, "E2840", {"start": v(21.98, -6.7) * mm, "end": v(22.1, -6.68) * mm});
            skLineSegment(sketch, "E2841", {"start": v(22.1, -6.68) * mm, "end": v(22.2, -6.67) * mm});
            skLineSegment(sketch, "E2842", {"start": v(22.2, -6.67) * mm, "end": v(22.31, -6.64) * mm});
            skLineSegment(sketch, "E2843", {"start": v(22.31, -6.64) * mm, "end": v(22.42, -6.6) * mm});
            skLineSegment(sketch, "E2844", {"start": v(22.42, -6.6) * mm, "end": v(22.53, -6.57) * mm});
            skLineSegment(sketch, "E2845", {"start": v(22.53, -6.57) * mm, "end": v(22.63, -6.53) * mm});
            skLineSegment(sketch, "E2846", {"start": v(22.63, -6.53) * mm, "end": v(22.73, -6.47) * mm});
            skLineSegment(sketch, "E2847", {"start": v(22.73, -6.47) * mm, "end": v(22.83, -6.42) * mm});
            skLineSegment(sketch, "E2848", {"start": v(22.83, -6.42) * mm, "end": v(22.92, -6.35) * mm});
            skLineSegment(sketch, "E2849", {"start": v(22.92, -6.35) * mm, "end": v(23, -6.28) * mm});
            skLineSegment(sketch, "E2850", {"start": v(23, -6.28) * mm, "end": v(23.1, -6.2) * mm});
            skLineSegment(sketch, "E2851", {"start": v(23.1, -6.2) * mm, "end": v(23.17, -6.13) * mm});
            skLineSegment(sketch, "E2852", {"start": v(23.17, -6.13) * mm, "end": v(23.25, -6.04) * mm});
            skLineSegment(sketch, "E2853", {"start": v(23.25, -6.04) * mm, "end": v(23.32, -5.95) * mm});
            skLineSegment(sketch, "E2854", {"start": v(23.32, -5.95) * mm, "end": v(23.38, -5.85) * mm});
            skLineSegment(sketch, "E2855", {"start": v(23.38, -5.85) * mm, "end": v(23.44, -5.75) * mm});
            skLineSegment(sketch, "E2856", {"start": v(23.44, -5.75) * mm, "end": v(23.49, -5.65) * mm});
            skLineSegment(sketch, "E2857", {"start": v(23.49, -5.65) * mm, "end": v(23.53, -5.54) * mm});
            skLineSegment(sketch, "E2858", {"start": v(23.53, -5.54) * mm, "end": v(23.57, -5.44) * mm});
            skLineSegment(sketch, "E2859", {"start": v(23.57, -5.44) * mm, "end": v(23.6, -5.33) * mm});
            skLineSegment(sketch, "E2860", {"start": v(23.6, -5.33) * mm, "end": v(23.62, -5.22) * mm});
            skLineSegment(sketch, "E2861", {"start": v(23.62, -5.22) * mm, "end": v(23.64, -5.1) * mm});
            skLineSegment(sketch, "E2862", {"start": v(23.64, -5.1) * mm, "end": v(23.65, -5) * mm});
            skLineSegment(sketch, "E2863", {"start": v(23.65, -5) * mm, "end": v(23.65, -4.88) * mm});
            skLineSegment(sketch, "E2864", {"start": v(23.65, -4.88) * mm, "end": v(23.65, -4.77) * mm});
            skLineSegment(sketch, "E2865", {"start": v(23.65, -4.77) * mm, "end": v(23.63, -4.66) * mm});
            skLineSegment(sketch, "E2866", {"start": v(23.63, -4.66) * mm, "end": v(23.61, -4.55) * mm});
            skLineSegment(sketch, "E2867", {"start": v(23.61, -4.55) * mm, "end": v(23.59, -4.44) * mm});
            skLineSegment(sketch, "E2868", {"start": v(23.59, -4.44) * mm, "end": v(23.55, -4.33) * mm});
            skLineSegment(sketch, "E2869", {"start": v(23.55, -4.33) * mm, "end": v(23.51, -4.22) * mm});
            skLineSegment(sketch, "E2870", {"start": v(23.51, -4.22) * mm, "end": v(23.46, -4.12) * mm});
            skLineSegment(sketch, "E2871", {"start": v(23.46, -4.12) * mm, "end": v(13.73, 15.58) * mm});
            skLineSegment(sketch, "E2872", {"start": v(13.73, 15.58) * mm, "end": v(13.69, 15.66) * mm});
            skLineSegment(sketch, "E2873", {"start": v(13.69, 15.66) * mm, "end": v(13.64, 15.74) * mm});
            skLineSegment(sketch, "E2874", {"start": v(13.64, 15.74) * mm, "end": v(13.58, 15.81) * mm});
            skLineSegment(sketch, "E2875", {"start": v(13.58, 15.81) * mm, "end": v(13.52, 15.88) * mm});
            skLineSegment(sketch, "E2876", {"start": v(13.52, 15.88) * mm, "end": v(13.46, 15.95) * mm});
            skLineSegment(sketch, "E2877", {"start": v(13.46, 15.95) * mm, "end": v(13.4, 16) * mm});
            skLineSegment(sketch, "E2878", {"start": v(13.4, 16) * mm, "end": v(13.32, 16.06) * mm});
            skLineSegment(sketch, "E2879", {"start": v(13.32, 16.06) * mm, "end": v(13.25, 16.11) * mm});
            skLineSegment(sketch, "E2880", {"start": v(13.25, 16.11) * mm, "end": v(13.17, 16.16) * mm});
            skLineSegment(sketch, "E2881", {"start": v(13.17, 16.16) * mm, "end": v(13.1, 16.2) * mm});
            skLineSegment(sketch, "E2882", {"start": v(13.1, 16.2) * mm, "end": v(13, 16.23) * mm});
            skLineSegment(sketch, "E2883", {"start": v(13, 16.23) * mm, "end": v(12.92, 16.26) * mm});
            skLineSegment(sketch, "E2884", {"start": v(12.92, 16.26) * mm, "end": v(12.83, 16.28) * mm});
            skLineSegment(sketch, "E2885", {"start": v(12.83, 16.28) * mm, "end": v(12.74, 16.3) * mm});
            skLineSegment(sketch, "E2886", {"start": v(12.74, 16.3) * mm, "end": v(12.65, 16.3) * mm});
            skLineSegment(sketch, "E2887", {"start": v(12.65, 16.3) * mm, "end": v(12.56, 16.3) * mm});
            skLineSegment(sketch, "E2888", {"start": v(12.56, 16.3) * mm, "end": v(12.38, 16.3) * mm});
            skLineSegment(sketch, "E2889", {"start": v(12.38, 16.3) * mm, "end": v(12.29, 16.3) * mm});
            skLineSegment(sketch, "E2890", {"start": v(12.29, 16.3) * mm, "end": v(12.2, 16.3) * mm});
            skLineSegment(sketch, "E2891", {"start": v(12.2, 16.3) * mm, "end": v(12.12, 16.28) * mm});
            skLineSegment(sketch, "E2892", {"start": v(12.12, 16.28) * mm, "end": v(12.03, 16.26) * mm});
            skLineSegment(sketch, "E2893", {"start": v(12.03, 16.26) * mm, "end": v(11.95, 16.23) * mm});
            skLineSegment(sketch, "E2894", {"start": v(11.95, 16.23) * mm, "end": v(11.87, 16.2) * mm});
            skLineSegment(sketch, "E2895", {"start": v(11.87, 16.2) * mm, "end": v(11.8, 16.17) * mm});
            skLineSegment(sketch, "E2896", {"start": v(11.8, 16.17) * mm, "end": v(11.72, 16.12) * mm});
            skLineSegment(sketch, "E2897", {"start": v(11.72, 16.12) * mm, "end": v(11.65, 16.08) * mm});
            skLineSegment(sketch, "E2898", {"start": v(11.65, 16.08) * mm, "end": v(11.58, 16.03) * mm});
            skLineSegment(sketch, "E2899", {"start": v(11.58, 16.03) * mm, "end": v(11.52, 15.97) * mm});
            skLineSegment(sketch, "E2900", {"start": v(11.52, 15.97) * mm, "end": v(11.46, 15.9) * mm});
            skLineSegment(sketch, "E2901", {"start": v(11.46, 15.9) * mm, "end": v(11.4, 15.84) * mm});
            skLineSegment(sketch, "E2902", {"start": v(11.4, 15.84) * mm, "end": v(11.35, 15.77) * mm});
            skLineSegment(sketch, "E2903", {"start": v(11.35, 15.77) * mm, "end": v(11.3, 15.7) * mm});
            skLineSegment(sketch, "E2904", {"start": v(11.3, 15.7) * mm, "end": v(11.26, 15.62) * mm});
            skLineSegment(sketch, "E2905", {"start": v(11.26, 15.62) * mm, "end": v(-8.01, -22.72) * mm});
            skLineSegment(sketch, "E2906", {"start": v(-8.01, -22.72) * mm, "end": v(-8.06, -22.8) * mm});
            skLineSegment(sketch, "E2907", {"start": v(-8.06, -22.8) * mm, "end": v(-8.11, -22.89) * mm});
            skLineSegment(sketch, "E2908", {"start": v(-8.11, -22.89) * mm, "end": v(-8.17, -22.96) * mm});
            skLineSegment(sketch, "E2909", {"start": v(-8.17, -22.96) * mm, "end": v(-8.23, -23.04) * mm});
            skLineSegment(sketch, "E2910", {"start": v(-8.23, -23.04) * mm, "end": v(-8.3, -23.1) * mm});
            skLineSegment(sketch, "E2911", {"start": v(-8.3, -23.1) * mm, "end": v(-8.37, -23.17) * mm});
            skLineSegment(sketch, "E2912", {"start": v(-8.37, -23.17) * mm, "end": v(-8.44, -23.23) * mm});
            skLineSegment(sketch, "E2913", {"start": v(-8.44, -23.23) * mm, "end": v(-8.52, -23.28) * mm});
            skLineSegment(sketch, "E2914", {"start": v(-8.52, -23.28) * mm, "end": v(-8.6, -23.32) * mm});
            skLineSegment(sketch, "E2915", {"start": v(-8.6, -23.32) * mm, "end": v(-8.7, -23.37) * mm});
            skLineSegment(sketch, "E2916", {"start": v(-8.7, -23.37) * mm, "end": v(-8.78, -23.4) * mm});
            skLineSegment(sketch, "E2917", {"start": v(-8.78, -23.4) * mm, "end": v(-8.87, -23.43) * mm});
            skLineSegment(sketch, "E2918", {"start": v(-8.87, -23.43) * mm, "end": v(-8.96, -23.45) * mm});
            skLineSegment(sketch, "E2919", {"start": v(-8.96, -23.45) * mm, "end": v(-9.06, -23.47) * mm});
            skLineSegment(sketch, "E2920", {"start": v(-9.06, -23.47) * mm, "end": v(-9.16, -23.48) * mm});
            skLineSegment(sketch, "E2921", {"start": v(-9.16, -23.48) * mm, "end": v(-9.25, -23.48) * mm});
            skLineSegment(sketch, "E2922", {"start": v(-9.25, -23.48) * mm, "end": v(-11.94, -23.48) * mm});
            skLineSegment(sketch, "E2923", {"start": v(-11.94, -23.48) * mm, "end": v(-12.06, -23.48) * mm});
            skLineSegment(sketch, "E2924", {"start": v(-12.06, -23.48) * mm, "end": v(-12.17, -23.47) * mm});
            skLineSegment(sketch, "E2925", {"start": v(-12.17, -23.47) * mm, "end": v(-12.28, -23.46) * mm});
            skLineSegment(sketch, "E2926", {"start": v(-12.28, -23.46) * mm, "end": v(-12.4, -23.44) * mm});
            skLineSegment(sketch, "E2927", {"start": v(-12.4, -23.44) * mm, "end": v(-12.5, -23.42) * mm});
            skLineSegment(sketch, "E2928", {"start": v(-12.5, -23.42) * mm, "end": v(-12.61, -23.39) * mm});
            skLineSegment(sketch, "E2929", {"start": v(-12.61, -23.39) * mm, "end": v(-12.72, -23.35) * mm});
            skLineSegment(sketch, "E2930", {"start": v(-12.72, -23.35) * mm, "end": v(-12.82, -23.3) * mm});
            skLineSegment(sketch, "E2931", {"start": v(-12.82, -23.3) * mm, "end": v(-12.93, -23.26) * mm});
            skLineSegment(sketch, "E2932", {"start": v(-12.93, -23.26) * mm, "end": v(-13.03, -23.21) * mm});
            skLineSegment(sketch, "E2933", {"start": v(-13.03, -23.21) * mm, "end": v(-13.12, -23.16) * mm});
            skLineSegment(sketch, "E2934", {"start": v(-13.12, -23.16) * mm, "end": v(-13.22, -23.1) * mm});
            skLineSegment(sketch, "E2935", {"start": v(-13.22, -23.1) * mm, "end": v(-13.31, -23.03) * mm});
            skLineSegment(sketch, "E2936", {"start": v(-13.31, -23.03) * mm, "end": v(-13.4, -22.96) * mm});
            skLineSegment(sketch, "E2937", {"start": v(-13.4, -22.96) * mm, "end": v(-13.49, -22.89) * mm});
            skLineSegment(sketch, "E2938", {"start": v(-13.49, -22.89) * mm, "end": v(-13.57, -22.8) * mm});
            skLineSegment(sketch, "E2939", {"start": v(-13.57, -22.8) * mm, "end": v(-29.29, -7.1) * mm});
            skLineSegment(sketch, "E2940", {"start": v(-29.29, -7.1) * mm, "end": v(-29.3, -7.08) * mm});
            skLineSegment(sketch, "E2941", {"start": v(-29.3, -7.08) * mm, "end": v(-29.31, -7.06) * mm});
            skLineSegment(sketch, "E2942", {"start": v(-29.31, -7.06) * mm, "end": v(-29.33, -7.04) * mm});
            skLineSegment(sketch, "E2943", {"start": v(-29.33, -7.04) * mm, "end": v(-29.33, -7.03) * mm});
            skLineSegment(sketch, "E2944", {"start": v(-29.33, -7.03) * mm, "end": v(-29.34, -7.01) * mm});
            skLineSegment(sketch, "E2945", {"start": v(-29.34, -7.01) * mm, "end": v(-29.35, -7) * mm});
            skLineSegment(sketch, "E2946", {"start": v(-29.35, -7) * mm, "end": v(-29.35, -6.98) * mm});
            skLineSegment(sketch, "E2947", {"start": v(-29.35, -6.98) * mm, "end": v(-29.35, -6.96) * mm});
            skLineSegment(sketch, "E2948", {"start": v(-29.35, -6.96) * mm, "end": v(-29.36, -6.95) * mm});
            skLineSegment(sketch, "E2949", {"start": v(-29.36, -6.95) * mm, "end": v(-29.36, -6.93) * mm});
            skLineSegment(sketch, "E2950", {"start": v(-29.36, -6.93) * mm, "end": v(-29.36, -6.91) * mm});
            skLineSegment(sketch, "E2951", {"start": v(-29.36, -6.91) * mm, "end": v(-29.35, -6.9) * mm});
            skLineSegment(sketch, "E2952", {"start": v(-29.35, -6.9) * mm, "end": v(-29.35, -6.88) * mm});
            skLineSegment(sketch, "E2953", {"start": v(-29.35, -6.88) * mm, "end": v(-29.35, -6.87) * mm});
            skLineSegment(sketch, "E2954", {"start": v(-29.35, -6.87) * mm, "end": v(-29.34, -6.85) * mm});
            skLineSegment(sketch, "E2955", {"start": v(-29.34, -6.85) * mm, "end": v(-29.34, -6.84) * mm});
            skLineSegment(sketch, "E2956", {"start": v(-29.34, -6.84) * mm, "end": v(-29.33, -6.83) * mm});
            skLineSegment(sketch, "E2957", {"start": v(-29.33, -6.83) * mm, "end": v(-29.33, -6.81) * mm});
            skLineSegment(sketch, "E2958", {"start": v(-29.33, -6.81) * mm, "end": v(-29.32, -6.8) * mm});
            skLineSegment(sketch, "E2959", {"start": v(-29.32, -6.8) * mm, "end": v(-29.3, -6.79) * mm});
            skLineSegment(sketch, "E2960", {"start": v(-29.3, -6.79) * mm, "end": v(-29.3, -6.78) * mm});
            skLineSegment(sketch, "E2961", {"start": v(-29.3, -6.78) * mm, "end": v(-29.29, -6.77) * mm});
            skLineSegment(sketch, "E2962", {"start": v(-29.29, -6.77) * mm, "end": v(-29.28, -6.75) * mm});
            skLineSegment(sketch, "E2963", {"start": v(-29.28, -6.75) * mm, "end": v(-29.26, -6.74) * mm});
            skLineSegment(sketch, "E2964", {"start": v(-29.26, -6.74) * mm, "end": v(-29.25, -6.73) * mm});
            skLineSegment(sketch, "E2965", {"start": v(-29.25, -6.73) * mm, "end": v(-29.24, -6.72) * mm});
            skLineSegment(sketch, "E2966", {"start": v(-29.24, -6.72) * mm, "end": v(-29.22, -6.72) * mm});
            skLineSegment(sketch, "E2967", {"start": v(-29.22, -6.72) * mm, "end": v(-29.2, -6.71) * mm});
            skLineSegment(sketch, "E2968", {"start": v(-29.2, -6.71) * mm, "end": v(-29.18, -6.7) * mm});
            skLineSegment(sketch, "E2969", {"start": v(-29.18, -6.7) * mm, "end": v(-29.17, -6.7) * mm});
            skLineSegment(sketch, "E2970", {"start": v(-29.17, -6.7) * mm, "end": v(-29.15, -6.7) * mm});
            skLineSegment(sketch, "E2971", {"start": v(-29.15, -6.7) * mm, "end": v(-29.13, -6.7) * mm});
            skLineSegment(sketch, "E2972", {"start": v(-29.13, -6.7) * mm, "end": v(-23.36, -6.7) * mm});
            skLineSegment(sketch, "E2973", {"start": v(-23.36, -6.7) * mm, "end": v(-22.87, -6.69) * mm});
            skLineSegment(sketch, "E2974", {"start": v(-22.87, -6.69) * mm, "end": v(-22.38, -6.66) * mm});
            skLineSegment(sketch, "E2975", {"start": v(-22.38, -6.66) * mm, "end": v(-21.9, -6.62) * mm});
            skLineSegment(sketch, "E2976", {"start": v(-21.9, -6.62) * mm, "end": v(-21.42, -6.55) * mm});
            skLineSegment(sketch, "E2977", {"start": v(-21.42, -6.55) * mm, "end": v(-20.95, -6.47) * mm});
            skLineSegment(sketch, "E2978", {"start": v(-20.95, -6.47) * mm, "end": v(-20.48, -6.37) * mm});
            skLineSegment(sketch, "E2979", {"start": v(-20.48, -6.37) * mm, "end": v(-20.03, -6.26) * mm});
            skLineSegment(sketch, "E2980", {"start": v(-20.03, -6.26) * mm, "end": v(-19.58, -6.12) * mm});
            skLineSegment(sketch, "E2981", {"start": v(-19.58, -6.12) * mm, "end": v(-19.13, -5.97) * mm});
            skLineSegment(sketch, "E2982", {"start": v(-19.13, -5.97) * mm, "end": v(-18.7, -5.8) * mm});
            skLineSegment(sketch, "E2983", {"start": v(-18.7, -5.8) * mm, "end": v(-18.26, -5.61) * mm});
            skLineSegment(sketch, "E2984", {"start": v(-18.26, -5.61) * mm, "end": v(-17.84, -5.4) * mm});
            skLineSegment(sketch, "E2985", {"start": v(-17.84, -5.4) * mm, "end": v(-17.42, -5.18) * mm});
            skLineSegment(sketch, "E2986", {"start": v(-17.42, -5.18) * mm, "end": v(-17.01, -4.94) * mm});
            skLineSegment(sketch, "E2987", {"start": v(-17.01, -4.94) * mm, "end": v(-16.6, -4.68) * mm});
            skLineSegment(sketch, "E2988", {"start": v(-16.6, -4.68) * mm, "end": v(-16.21, -4.4) * mm});
            skLineSegment(sketch, "E2989", {"start": v(-16.21, -4.4) * mm, "end": v(-15.7, -4) * mm});
            skLineSegment(sketch, "E2990", {"start": v(-15.7, -4) * mm, "end": v(-15.23, -3.59) * mm});
            skLineSegment(sketch, "E2991", {"start": v(-15.23, -3.59) * mm, "end": v(-14.78, -3.14) * mm});
            skLineSegment(sketch, "E2992", {"start": v(-14.78, -3.14) * mm, "end": v(-14.37, -2.68) * mm});
            skLineSegment(sketch, "E2993", {"start": v(-14.37, -2.68) * mm, "end": v(-14, -2.19) * mm});
            skLineSegment(sketch, "E2994", {"start": v(-14, -2.19) * mm, "end": v(-13.65, -1.67) * mm});
            skLineSegment(sketch, "E2995", {"start": v(-13.65, -1.67) * mm, "end": v(-13.33, -1.14) * mm});
            skLineSegment(sketch, "E2996", {"start": v(-13.33, -1.14) * mm, "end": v(-13.05, -0.58) * mm});
            skLineSegment(sketch, "E2997", {"start": v(-13.05, -0.58) * mm, "end": v(-12.8, 0) * mm});
            skLineSegment(sketch, "E2998", {"start": v(-12.8, 0) * mm, "end": v(-12.59, 0.6) * mm});
            skLineSegment(sketch, "E2999", {"start": v(-12.59, 0.6) * mm, "end": v(-12.4, 1.22) * mm});
            skLineSegment(sketch, "E3000", {"start": v(-12.4, 1.22) * mm, "end": v(-12.26, 1.87) * mm});
            skLineSegment(sketch, "E3001", {"start": v(-12.26, 1.87) * mm, "end": v(-12.14, 2.54) * mm});
            skLineSegment(sketch, "E3002", {"start": v(-12.14, 2.54) * mm, "end": v(-12.06, 3.23) * mm});
            skLineSegment(sketch, "E3003", {"start": v(-12.06, 3.23) * mm, "end": v(-12, 3.94) * mm});
            skLineSegment(sketch, "E3004", {"start": v(-12, 3.94) * mm, "end": v(-12, 4.67) * mm});
            skLineSegment(sketch, "E3005", {"start": v(-12, 4.67) * mm, "end": v(-12, 5.4) * mm});
            skLineSegment(sketch, "E3006", {"start": v(-12, 5.4) * mm, "end": v(-12.06, 6.12) * mm});
            skLineSegment(sketch, "E3007", {"start": v(-12.06, 6.12) * mm, "end": v(-12.14, 6.8) * mm});
            skLineSegment(sketch, "E3008", {"start": v(-12.14, 6.8) * mm, "end": v(-12.26, 7.48) * mm});
            skLineSegment(sketch, "E3009", {"start": v(-12.26, 7.48) * mm, "end": v(-12.4, 8.12) * mm});
            skLineSegment(sketch, "E3010", {"start": v(-12.4, 8.12) * mm, "end": v(-12.59, 8.75) * mm});
            skLineSegment(sketch, "E3011", {"start": v(-12.59, 8.75) * mm, "end": v(-12.8, 9.35) * mm});
            skLineSegment(sketch, "E3012", {"start": v(-12.8, 9.35) * mm, "end": v(-13.05, 9.93) * mm});
            skLineSegment(sketch, "E3013", {"start": v(-13.05, 9.93) * mm, "end": v(-13.33, 10.48) * mm});
            skLineSegment(sketch, "E3014", {"start": v(-13.33, 10.48) * mm, "end": v(-13.65, 11.02) * mm});
            skLineSegment(sketch, "E3015", {"start": v(-13.65, 11.02) * mm, "end": v(-14, 11.53) * mm});
            skLineSegment(sketch, "E3016", {"start": v(-14, 11.53) * mm, "end": v(-14.37, 12.02) * mm});
            skLineSegment(sketch, "E3017", {"start": v(-14.37, 12.02) * mm, "end": v(-14.78, 12.49) * mm});
            skLineSegment(sketch, "E3018", {"start": v(-14.78, 12.49) * mm, "end": v(-15.23, 12.93) * mm});
            skLineSegment(sketch, "E3019", {"start": v(-15.23, 12.93) * mm, "end": v(-15.7, 13.35) * mm});
            skLineSegment(sketch, "E3020", {"start": v(-15.7, 13.35) * mm, "end": v(-16.21, 13.75) * mm});
            skLineSegment(sketch, "E3021", {"start": v(-16.21, 13.75) * mm, "end": v(-16.6, 14.03) * mm});
            skLineSegment(sketch, "E3022", {"start": v(-16.6, 14.03) * mm, "end": v(-17.01, 14.29) * mm});
            skLineSegment(sketch, "E3023", {"start": v(-17.01, 14.29) * mm, "end": v(-17.42, 14.53) * mm});
            skLineSegment(sketch, "E3024", {"start": v(-17.42, 14.53) * mm, "end": v(-17.84, 14.75) * mm});
            skLineSegment(sketch, "E3025", {"start": v(-17.84, 14.75) * mm, "end": v(-18.26, 14.96) * mm});
            skLineSegment(sketch, "E3026", {"start": v(-18.26, 14.96) * mm, "end": v(-18.7, 15.15) * mm});
            skLineSegment(sketch, "E3027", {"start": v(-18.7, 15.15) * mm, "end": v(-19.13, 15.32) * mm});
            skLineSegment(sketch, "E3028", {"start": v(-19.13, 15.32) * mm, "end": v(-19.58, 15.47) * mm});
            skLineSegment(sketch, "E3029", {"start": v(-19.58, 15.47) * mm, "end": v(-20.03, 15.6) * mm});
            skLineSegment(sketch, "E3030", {"start": v(-20.03, 15.6) * mm, "end": v(-20.48, 15.72) * mm});
            skLineSegment(sketch, "E3031", {"start": v(-20.48, 15.72) * mm, "end": v(-20.95, 15.82) * mm});
            skLineSegment(sketch, "E3032", {"start": v(-20.95, 15.82) * mm, "end": v(-21.42, 15.9) * mm});
            skLineSegment(sketch, "E3033", {"start": v(-21.42, 15.9) * mm, "end": v(-21.9, 15.96) * mm});
            skLineSegment(sketch, "E3034", {"start": v(-21.9, 15.96) * mm, "end": v(-22.38, 16) * mm});
            skLineSegment(sketch, "E3035", {"start": v(-22.38, 16) * mm, "end": v(-22.87, 16.04) * mm});
            skLineSegment(sketch, "E3036", {"start": v(-22.87, 16.04) * mm, "end": v(-23.36, 16.04) * mm});
            skLineSegment(sketch, "E3037", {"start": v(-23.36, 16.04) * mm, "end": v(-36.97, 16.04) * mm});
            skLineSegment(sketch, "E3038", {"start": v(-36.97, 16.04) * mm, "end": v(-37.25, 16.03) * mm});
            skLineSegment(sketch, "E3039", {"start": v(-37.25, 16.03) * mm, "end": v(-37.52, 15.99) * mm});
            skLineSegment(sketch, "E3040", {"start": v(-37.52, 15.99) * mm, "end": v(-37.78, 15.92) * mm});
            skLineSegment(sketch, "E3041", {"start": v(-37.78, 15.92) * mm, "end": v(-38.03, 15.83) * mm});
            skLineSegment(sketch, "E3042", {"start": v(-38.03, 15.83) * mm, "end": v(-38.27, 15.71) * mm});
            skLineSegment(sketch, "E3043", {"start": v(-38.27, 15.71) * mm, "end": v(-38.5, 15.58) * mm});
            skLineSegment(sketch, "E3044", {"start": v(-38.5, 15.58) * mm, "end": v(-38.7, 15.42) * mm});
            skLineSegment(sketch, "E3045", {"start": v(-38.7, 15.42) * mm, "end": v(-38.9, 15.24) * mm});
            skLineSegment(sketch, "E3046", {"start": v(-38.9, 15.24) * mm, "end": v(-39.08, 15.05) * mm});
            skLineSegment(sketch, "E3047", {"start": v(-39.08, 15.05) * mm, "end": v(-39.24, 14.84) * mm});
            skLineSegment(sketch, "E3048", {"start": v(-39.24, 14.84) * mm, "end": v(-39.38, 14.6) * mm});
            skLineSegment(sketch, "E3049", {"start": v(-39.38, 14.6) * mm, "end": v(-39.5, 14.37) * mm});
            skLineSegment(sketch, "E3050", {"start": v(-39.5, 14.37) * mm, "end": v(-39.58, 14.12) * mm});
            skLineSegment(sketch, "E3051", {"start": v(-39.58, 14.12) * mm, "end": v(-39.65, 13.86) * mm});
            skLineSegment(sketch, "E3052", {"start": v(-39.65, 13.86) * mm, "end": v(-39.7, 13.58) * mm});
            skLineSegment(sketch, "E3053", {"start": v(-39.7, 13.58) * mm, "end": v(-39.7, 13.3) * mm});
            skLineSegment(sketch, "E3054", {"start": v(-39.7, 13.3) * mm, "end": v(-39.7, -22.53) * mm});
            skLineSegment(sketch, "E3055", {"start": v(-39.7, -22.53) * mm, "end": v(-39.71, -22.64) * mm});
            skLineSegment(sketch, "E3056", {"start": v(-39.71, -22.64) * mm, "end": v(-39.72, -22.74) * mm});
            skLineSegment(sketch, "E3057", {"start": v(-39.72, -22.74) * mm, "end": v(-39.74, -22.84) * mm});
            skLineSegment(sketch, "E3058", {"start": v(-39.74, -22.84) * mm, "end": v(-39.77, -22.93) * mm});
            skLineSegment(sketch, "E3059", {"start": v(-39.77, -22.93) * mm, "end": v(-39.8, -23.01) * mm});
            skLineSegment(sketch, "E3060", {"start": v(-39.8, -23.01) * mm, "end": v(-39.85, -23.09) * mm});
            skLineSegment(sketch, "E3061", {"start": v(-39.85, -23.09) * mm, "end": v(-39.9, -23.16) * mm});
            skLineSegment(sketch, "E3062", {"start": v(-39.9, -23.16) * mm, "end": v(-39.96, -23.22) * mm});
            skLineSegment(sketch, "E3063", {"start": v(-39.96, -23.22) * mm, "end": v(-40.03, -23.28) * mm});
            skLineSegment(sketch, "E3064", {"start": v(-40.03, -23.28) * mm, "end": v(-40.1, -23.33) * mm});
            skLineSegment(sketch, "E3065", {"start": v(-40.1, -23.33) * mm, "end": v(-40.18, -23.37) * mm});
            skLineSegment(sketch, "E3066", {"start": v(-40.18, -23.37) * mm, "end": v(-40.27, -23.4) * mm});
            skLineSegment(sketch, "E3067", {"start": v(-40.27, -23.4) * mm, "end": v(-40.37, -23.44) * mm});
            skLineSegment(sketch, "E3068", {"start": v(-40.37, -23.44) * mm, "end": v(-40.48, -23.46) * mm});
            skLineSegment(sketch, "E3069", {"start": v(-40.48, -23.46) * mm, "end": v(-40.6, -23.47) * mm});
            skLineSegment(sketch, "E3070", {"start": v(-40.6, -23.47) * mm, "end": v(-40.72, -23.48) * mm});
            skLineSegment(sketch, "E3071", {"start": v(-40.72, -23.48) * mm, "end": v(-43.52, -23.48) * mm});
            skLineSegment(sketch, "E3072", {"start": v(-43.52, -23.48) * mm, "end": v(-43.62, -23.48) * mm});
            skLineSegment(sketch, "E3073", {"start": v(-43.62, -23.48) * mm, "end": v(-43.72, -23.46) * mm});
            skLineSegment(sketch, "E3074", {"start": v(-43.72, -23.46) * mm, "end": v(-43.82, -23.44) * mm});
            skLineSegment(sketch, "E3075", {"start": v(-43.82, -23.44) * mm, "end": v(-43.91, -23.4) * mm});
            skLineSegment(sketch, "E3076", {"start": v(-43.91, -23.4) * mm, "end": v(-44, -23.36) * mm});
            skLineSegment(sketch, "E3077", {"start": v(-44, -23.36) * mm, "end": v(-44.09, -23.31) * mm});
            skLineSegment(sketch, "E3078", {"start": v(-44.09, -23.31) * mm, "end": v(-44.16, -23.25) * mm});
            skLineSegment(sketch, "E3079", {"start": v(-44.16, -23.25) * mm, "end": v(-44.24, -23.19) * mm});
            skLineSegment(sketch, "E3080", {"start": v(-44.24, -23.19) * mm, "end": v(-44.3, -23.11) * mm});
            skLineSegment(sketch, "E3081", {"start": v(-44.3, -23.11) * mm, "end": v(-44.36, -23.04) * mm});
            skLineSegment(sketch, "E3082", {"start": v(-44.36, -23.04) * mm, "end": v(-44.41, -22.95) * mm});
            skLineSegment(sketch, "E3083", {"start": v(-44.41, -22.95) * mm, "end": v(-44.45, -22.86) * mm});
            skLineSegment(sketch, "E3084", {"start": v(-44.45, -22.86) * mm, "end": v(-44.49, -22.77) * mm});
            skLineSegment(sketch, "E3085", {"start": v(-44.49, -22.77) * mm, "end": v(-44.51, -22.67) * mm});
            skLineSegment(sketch, "E3086", {"start": v(-44.51, -22.67) * mm, "end": v(-44.53, -22.57) * mm});
            skLineSegment(sketch, "E3087", {"start": v(-44.53, -22.57) * mm, "end": v(-44.53, -22.47) * mm});
            skLineSegment(sketch, "E3088", {"start": v(-44.53, -22.47) * mm, "end": v(-44.53, 12.07) * mm});
            skLineSegment(sketch, "E3089", {"start": v(-44.53, 12.07) * mm, "end": v(-44.54, 12.3) * mm});
            skLineSegment(sketch, "E3090", {"start": v(-44.54, 12.3) * mm, "end": v(-44.55, 12.5) * mm});
            skLineSegment(sketch, "E3091", {"start": v(-44.55, 12.5) * mm, "end": v(-44.57, 12.72) * mm});
            skLineSegment(sketch, "E3092", {"start": v(-44.57, 12.72) * mm, "end": v(-44.6, 12.92) * mm});
            skLineSegment(sketch, "E3093", {"start": v(-44.6, 12.92) * mm, "end": v(-44.64, 13.12) * mm});
            skLineSegment(sketch, "E3094", {"start": v(-44.64, 13.12) * mm, "end": v(-44.69, 13.31) * mm});
            skLineSegment(sketch, "E3095", {"start": v(-44.69, 13.31) * mm, "end": v(-44.74, 13.5) * mm});
            skLineSegment(sketch, "E3096", {"start": v(-44.74, 13.5) * mm, "end": v(-44.8, 13.69) * mm});
            skLineSegment(sketch, "E3097", {"start": v(-44.8, 13.69) * mm, "end": v(-44.88, 13.86) * mm});
            skLineSegment(sketch, "E3098", {"start": v(-44.88, 13.86) * mm, "end": v(-44.96, 14.04) * mm});
            skLineSegment(sketch, "E3099", {"start": v(-44.96, 14.04) * mm, "end": v(-45.05, 14.2) * mm});
            skLineSegment(sketch, "E3100", {"start": v(-45.05, 14.2) * mm, "end": v(-45.14, 14.36) * mm});
            skLineSegment(sketch, "E3101", {"start": v(-45.14, 14.36) * mm, "end": v(-45.25, 14.52) * mm});
            skLineSegment(sketch, "E3102", {"start": v(-45.25, 14.52) * mm, "end": v(-45.36, 14.67) * mm});
            skLineSegment(sketch, "E3103", {"start": v(-45.36, 14.67) * mm, "end": v(-45.48, 14.81) * mm});
            skLineSegment(sketch, "E3104", {"start": v(-45.48, 14.81) * mm, "end": v(-45.61, 14.95) * mm});
            skLineSegment(sketch, "E3105", {"start": v(-45.61, 14.95) * mm, "end": v(-45.75, 15.08) * mm});
            skLineSegment(sketch, "E3106", {"start": v(-45.75, 15.08) * mm, "end": v(-45.9, 15.2) * mm});
            skLineSegment(sketch, "E3107", {"start": v(-45.9, 15.2) * mm, "end": v(-46.04, 15.32) * mm});
            skLineSegment(sketch, "E3108", {"start": v(-46.04, 15.32) * mm, "end": v(-46.2, 15.43) * mm});
            skLineSegment(sketch, "E3109", {"start": v(-46.2, 15.43) * mm, "end": v(-46.36, 15.53) * mm});
            skLineSegment(sketch, "E3110", {"start": v(-46.36, 15.53) * mm, "end": v(-46.52, 15.62) * mm});
            skLineSegment(sketch, "E3111", {"start": v(-46.52, 15.62) * mm, "end": v(-46.7, 15.7) * mm});
            skLineSegment(sketch, "E3112", {"start": v(-46.7, 15.7) * mm, "end": v(-46.87, 15.77) * mm});
            skLineSegment(sketch, "E3113", {"start": v(-46.87, 15.77) * mm, "end": v(-47.05, 15.83) * mm});
            skLineSegment(sketch, "E3114", {"start": v(-47.05, 15.83) * mm, "end": v(-47.24, 15.9) * mm});
            skLineSegment(sketch, "E3115", {"start": v(-47.24, 15.9) * mm, "end": v(-47.43, 15.94) * mm});
            skLineSegment(sketch, "E3116", {"start": v(-47.43, 15.94) * mm, "end": v(-47.63, 15.98) * mm});
            skLineSegment(sketch, "E3117", {"start": v(-47.63, 15.98) * mm, "end": v(-47.83, 16) * mm});
            skLineSegment(sketch, "E3118", {"start": v(-47.83, 16) * mm, "end": v(-48.04, 16.03) * mm});
            skLineSegment(sketch, "E3119", {"start": v(-48.04, 16.03) * mm, "end": v(-48.25, 16.04) * mm});
            skLineSegment(sketch, "E3120", {"start": v(-48.25, 16.04) * mm, "end": v(-48.47, 16.04) * mm});
            skLineSegment(sketch, "E3121", {"start": v(-48.47, 16.04) * mm, "end": v(-48.68, 16.04) * mm});
            skLineSegment(sketch, "E3122", {"start": v(-48.68, 16.04) * mm, "end": v(-48.9, 16.03) * mm});
            skLineSegment(sketch, "E3123", {"start": v(-48.9, 16.03) * mm, "end": v(-49.1, 16) * mm});
            skLineSegment(sketch, "E3124", {"start": v(-49.1, 16) * mm, "end": v(-49.3, 15.97) * mm});
            skLineSegment(sketch, "E3125", {"start": v(-49.3, 15.97) * mm, "end": v(-49.49, 15.93) * mm});
            skLineSegment(sketch, "E3126", {"start": v(-49.49, 15.93) * mm, "end": v(-49.68, 15.89) * mm});
            skLineSegment(sketch, "E3127", {"start": v(-49.68, 15.89) * mm, "end": v(-49.86, 15.83) * mm});
            skLineSegment(sketch, "E3128", {"start": v(-49.86, 15.83) * mm, "end": v(-50.04, 15.76) * mm});
            skLineSegment(sketch, "E3129", {"start": v(-50.04, 15.76) * mm, "end": v(-50.21, 15.69) * mm});
            skLineSegment(sketch, "E3130", {"start": v(-50.21, 15.69) * mm, "end": v(-50.38, 15.6) * mm});
            skLineSegment(sketch, "E3131", {"start": v(-50.38, 15.6) * mm, "end": v(-50.55, 15.51) * mm});
            skLineSegment(sketch, "E3132", {"start": v(-50.55, 15.51) * mm, "end": v(-50.7, 15.41) * mm});
            skLineSegment(sketch, "E3133", {"start": v(-50.7, 15.41) * mm, "end": v(-50.87, 15.3) * mm});
            skLineSegment(sketch, "E3134", {"start": v(-50.87, 15.3) * mm, "end": v(-51.02, 15.19) * mm});
            skLineSegment(sketch, "E3135", {"start": v(-51.02, 15.19) * mm, "end": v(-51.16, 15.06) * mm});
            skLineSegment(sketch, "E3136", {"start": v(-51.16, 15.06) * mm, "end": v(-51.3, 14.93) * mm});
            skLineSegment(sketch, "E3137", {"start": v(-51.3, 14.93) * mm, "end": v(-51.43, 14.79) * mm});
            skLineSegment(sketch, "E3138", {"start": v(-51.43, 14.79) * mm, "end": v(-51.56, 14.64) * mm});
            skLineSegment(sketch, "E3139", {"start": v(-51.56, 14.64) * mm, "end": v(-51.68, 14.49) * mm});
            skLineSegment(sketch, "E3140", {"start": v(-51.68, 14.49) * mm, "end": v(-51.78, 14.33) * mm});
            skLineSegment(sketch, "E3141", {"start": v(-51.78, 14.33) * mm, "end": v(-51.88, 14.17) * mm});
            skLineSegment(sketch, "E3142", {"start": v(-51.88, 14.17) * mm, "end": v(-51.97, 14) * mm});
            skLineSegment(sketch, "E3143", {"start": v(-51.97, 14) * mm, "end": v(-52.06, 13.83) * mm});
            skLineSegment(sketch, "E3144", {"start": v(-52.06, 13.83) * mm, "end": v(-52.13, 13.65) * mm});
            skLineSegment(sketch, "E3145", {"start": v(-52.13, 13.65) * mm, "end": v(-52.2, 13.47) * mm});
            skLineSegment(sketch, "E3146", {"start": v(-52.2, 13.47) * mm, "end": v(-52.25, 13.29) * mm});
            skLineSegment(sketch, "E3147", {"start": v(-52.25, 13.29) * mm, "end": v(-52.3, 13.1) * mm});
            skLineSegment(sketch, "E3148", {"start": v(-52.3, 13.1) * mm, "end": v(-52.34, 12.9) * mm});
            skLineSegment(sketch, "E3149", {"start": v(-52.34, 12.9) * mm, "end": v(-52.37, 12.7) * mm});
            skLineSegment(sketch, "E3150", {"start": v(-52.37, 12.7) * mm, "end": v(-52.39, 12.5) * mm});
            skLineSegment(sketch, "E3151", {"start": v(-52.39, 12.5) * mm, "end": v(-52.4, 12.28) * mm});
            skLineSegment(sketch, "E3152", {"start": v(-52.4, 12.28) * mm, "end": v(-52.4, 12.07) * mm});
            skLineSegment(sketch, "E3153", {"start": v(-52.4, 12.07) * mm, "end": v(-52.4, -17.98) * mm});
            skLineSegment(sketch, "E3154", {"start": v(-52.4, -17.98) * mm, "end": v(-52.4, -18) * mm});
            skLineSegment(sketch, "E3155", {"start": v(-52.4, -18) * mm, "end": v(-52.41, -18.02) * mm});
            skLineSegment(sketch, "E3156", {"start": v(-52.41, -18.02) * mm, "end": v(-52.42, -18.03) * mm});
            skLineSegment(sketch, "E3157", {"start": v(-52.42, -18.03) * mm, "end": v(-52.42, -18.05) * mm});
            skLineSegment(sketch, "E3158", {"start": v(-52.42, -18.05) * mm, "end": v(-52.43, -18.06) * mm});
            skLineSegment(sketch, "E3159", {"start": v(-52.43, -18.06) * mm, "end": v(-52.44, -18.08) * mm});
            skLineSegment(sketch, "E3160", {"start": v(-52.44, -18.08) * mm, "end": v(-52.45, -18.09) * mm});
            skLineSegment(sketch, "E3161", {"start": v(-52.45, -18.09) * mm, "end": v(-52.46, -18.1) * mm});
            skLineSegment(sketch, "E3162", {"start": v(-52.46, -18.1) * mm, "end": v(-52.47, -18.11) * mm});
            skLineSegment(sketch, "E3163", {"start": v(-52.47, -18.11) * mm, "end": v(-52.48, -18.12) * mm});
            skLineSegment(sketch, "E3164", {"start": v(-52.48, -18.12) * mm, "end": v(-52.5, -18.13) * mm});
            skLineSegment(sketch, "E3165", {"start": v(-52.5, -18.13) * mm, "end": v(-52.51, -18.13) * mm});
            skLineSegment(sketch, "E3166", {"start": v(-52.51, -18.13) * mm, "end": v(-52.53, -18.14) * mm});
            skLineSegment(sketch, "E3167", {"start": v(-52.53, -18.14) * mm, "end": v(-52.54, -18.14) * mm});
            skLineSegment(sketch, "E3168", {"start": v(-52.54, -18.14) * mm, "end": v(-52.56, -18.14) * mm});
            skLineSegment(sketch, "E3169", {"start": v(-52.56, -18.14) * mm, "end": v(-52.57, -18.14) * mm});
            skLineSegment(sketch, "E3170", {"start": v(-52.57, -18.14) * mm, "end": v(-52.58, -18.14) * mm});
            skLineSegment(sketch, "E3171", {"start": v(-52.58, -18.14) * mm, "end": v(-52.59, -18.14) * mm});
            skLineSegment(sketch, "E3172", {"start": v(-52.59, -18.14) * mm, "end": v(-52.6, -18.14) * mm});
            skLineSegment(sketch, "E3173", {"start": v(-52.6, -18.14) * mm, "end": v(-52.6, -18.14) * mm});
            skLineSegment(sketch, "E3174", {"start": v(-52.6, -18.14) * mm, "end": v(-52.61, -18.14) * mm});
            skLineSegment(sketch, "E3175", {"start": v(-52.61, -18.14) * mm, "end": v(-52.62, -18.13) * mm});
            skLineSegment(sketch, "E3176", {"start": v(-52.62, -18.13) * mm, "end": v(-52.63, -18.13) * mm});
            skLineSegment(sketch, "E3177", {"start": v(-52.63, -18.13) * mm, "end": v(-52.64, -18.13) * mm});
            skLineSegment(sketch, "E3178", {"start": v(-52.64, -18.13) * mm, "end": v(-52.65, -18.12) * mm});
            skLineSegment(sketch, "E3179", {"start": v(-52.65, -18.12) * mm, "end": v(-52.66, -18.12) * mm});
            skLineSegment(sketch, "E3180", {"start": v(-52.66, -18.12) * mm, "end": v(-52.67, -18.1) * mm});
            skLineSegment(sketch, "E3181", {"start": v(-52.67, -18.1) * mm, "end": v(-52.68, -18.1) * mm});
            skLineSegment(sketch, "E3182", {"start": v(-52.68, -18.1) * mm, "end": v(-52.69, -18.09) * mm});
            skLineSegment(sketch, "E3183", {"start": v(-52.69, -18.09) * mm, "end": v(-52.7, -18.08) * mm});
            skLineSegment(sketch, "E3184", {"start": v(-52.7, -18.08) * mm, "end": v(-52.7, -18.07) * mm});
            skLineSegment(sketch, "E3185", {"start": v(-52.7, -18.07) * mm, "end": v(-52.71, -18.05) * mm});
            skLineSegment(sketch, "E3186", {"start": v(-52.71, -18.05) * mm, "end": v(-69.4, 15.25) * mm});
            skLineSegment(sketch, "E3187", {"start": v(-69.4, 15.25) * mm, "end": v(-69.46, 15.34) * mm});
            skLineSegment(sketch, "E3188", {"start": v(-69.46, 15.34) * mm, "end": v(-69.51, 15.42) * mm});
            skLineSegment(sketch, "E3189", {"start": v(-69.51, 15.42) * mm, "end": v(-69.57, 15.5) * mm});
            skLineSegment(sketch, "E3190", {"start": v(-69.57, 15.5) * mm, "end": v(-69.64, 15.58) * mm});
            skLineSegment(sketch, "E3191", {"start": v(-69.64, 15.58) * mm, "end": v(-69.7, 15.65) * mm});
            skLineSegment(sketch, "E3192", {"start": v(-69.7, 15.65) * mm, "end": v(-69.78, 15.72) * mm});
            skLineSegment(sketch, "E3193", {"start": v(-69.78, 15.72) * mm, "end": v(-69.86, 15.78) * mm});
            skLineSegment(sketch, "E3194", {"start": v(-69.86, 15.78) * mm, "end": v(-69.94, 15.83) * mm});
            skLineSegment(sketch, "E3195", {"start": v(-69.94, 15.83) * mm, "end": v(-70.03, 15.88) * mm});
            skLineSegment(sketch, "E3196", {"start": v(-70.03, 15.88) * mm, "end": v(-70.11, 15.92) * mm});
            skLineSegment(sketch, "E3197", {"start": v(-70.11, 15.92) * mm, "end": v(-70.2, 15.96) * mm});
            skLineSegment(sketch, "E3198", {"start": v(-70.2, 15.96) * mm, "end": v(-70.3, 15.99) * mm});
            skLineSegment(sketch, "E3199", {"start": v(-70.3, 15.99) * mm, "end": v(-70.4, 16.01) * mm});
            skLineSegment(sketch, "E3200", {"start": v(-70.4, 16.01) * mm, "end": v(-70.5, 16.03) * mm});
            skLineSegment(sketch, "E3201", {"start": v(-70.5, 16.03) * mm, "end": v(-70.6, 16.04) * mm});
            skLineSegment(sketch, "E3202", {"start": v(-70.6, 16.04) * mm, "end": v(-70.7, 16.04) * mm});
            skLineSegment(sketch, "E3203", {"start": v(-70.7, 16.04) * mm, "end": v(-70.85, 16.04) * mm});
            skLineSegment(sketch, "E3204", {"start": v(-70.85, 16.04) * mm, "end": v(-71, 16.02) * mm});
            skLineSegment(sketch, "E3205", {"start": v(-71, 16.02) * mm, "end": v(-71.13, 15.98) * mm});
            skLineSegment(sketch, "E3206", {"start": v(-71.13, 15.98) * mm, "end": v(-71.26, 15.93) * mm});
            skLineSegment(sketch, "E3207", {"start": v(-71.26, 15.93) * mm, "end": v(-71.39, 15.87) * mm});
            skLineSegment(sketch, "E3208", {"start": v(-71.39, 15.87) * mm, "end": v(-71.5, 15.8) * mm});
            skLineSegment(sketch, "E3209", {"start": v(-71.5, 15.8) * mm, "end": v(-71.62, 15.71) * mm});
            skLineSegment(sketch, "E3210", {"start": v(-71.62, 15.71) * mm, "end": v(-71.72, 15.62) * mm});
            skLineSegment(sketch, "E3211", {"start": v(-71.72, 15.62) * mm, "end": v(-71.81, 15.52) * mm});
            skLineSegment(sketch, "E3212", {"start": v(-71.81, 15.52) * mm, "end": v(-71.9, 15.4) * mm});
            skLineSegment(sketch, "E3213", {"start": v(-71.9, 15.4) * mm, "end": v(-71.97, 15.29) * mm});
            skLineSegment(sketch, "E3214", {"start": v(-71.97, 15.29) * mm, "end": v(-72.03, 15.16) * mm});
            skLineSegment(sketch, "E3215", {"start": v(-72.03, 15.16) * mm, "end": v(-72.08, 15.03) * mm});
            skLineSegment(sketch, "E3216", {"start": v(-72.08, 15.03) * mm, "end": v(-72.12, 14.9) * mm});
            skLineSegment(sketch, "E3217", {"start": v(-72.12, 14.9) * mm, "end": v(-72.14, 14.75) * mm});
            skLineSegment(sketch, "E3218", {"start": v(-72.14, 14.75) * mm, "end": v(-72.15, 14.6) * mm});
            skLineSegment(sketch, "E3219", {"start": v(-72.15, 14.6) * mm, "end": v(-72.15, -22.83) * mm});
            skLineSegment(sketch, "E3220", {"start": v(-72.15, -22.83) * mm, "end": v(-72.15, -22.9) * mm});
            skLineSegment(sketch, "E3221", {"start": v(-72.15, -22.9) * mm, "end": v(-72.16, -22.96) * mm});
            skLineSegment(sketch, "E3222", {"start": v(-72.16, -22.96) * mm, "end": v(-72.17, -23.02) * mm});
            skLineSegment(sketch, "E3223", {"start": v(-72.17, -23.02) * mm, "end": v(-72.2, -23.08) * mm});
            skLineSegment(sketch, "E3224", {"start": v(-72.2, -23.08) * mm, "end": v(-72.22, -23.14) * mm});
            skLineSegment(sketch, "E3225", {"start": v(-72.22, -23.14) * mm, "end": v(-72.26, -23.2) * mm});
            skLineSegment(sketch, "E3226", {"start": v(-72.26, -23.2) * mm, "end": v(-72.3, -23.25) * mm});
            skLineSegment(sketch, "E3227", {"start": v(-72.3, -23.25) * mm, "end": v(-72.34, -23.3) * mm});
            skLineSegment(sketch, "E3228", {"start": v(-72.34, -23.3) * mm, "end": v(-72.38, -23.33) * mm});
            skLineSegment(sketch, "E3229", {"start": v(-72.38, -23.33) * mm, "end": v(-72.43, -23.37) * mm});
            skLineSegment(sketch, "E3230", {"start": v(-72.43, -23.37) * mm, "end": v(-72.49, -23.4) * mm});
            skLineSegment(sketch, "E3231", {"start": v(-72.49, -23.4) * mm, "end": v(-72.55, -23.43) * mm});
            skLineSegment(sketch, "E3232", {"start": v(-72.55, -23.43) * mm, "end": v(-72.6, -23.45) * mm});
            skLineSegment(sketch, "E3233", {"start": v(-72.6, -23.45) * mm, "end": v(-72.67, -23.47) * mm});
            skLineSegment(sketch, "E3234", {"start": v(-72.67, -23.47) * mm, "end": v(-72.73, -23.48) * mm});
            skLineSegment(sketch, "E3235", {"start": v(-72.73, -23.48) * mm, "end": v(-72.8, -23.48) * mm});
            skLineSegment(sketch, "E3236", {"start": v(-72.8, -23.48) * mm, "end": v(-91.32, -23.48) * mm});
            skLineSegment(sketch, "E3237", {"start": v(-91.32, -23.48) * mm, "end": v(-91.38, -23.48) * mm});
            skLineSegment(sketch, "E3238", {"start": v(-91.38, -23.48) * mm, "end": v(-91.44, -23.47) * mm});
            skLineSegment(sketch, "E3239", {"start": v(-91.44, -23.47) * mm, "end": v(-91.5, -23.46) * mm});
            skLineSegment(sketch, "E3240", {"start": v(-91.5, -23.46) * mm, "end": v(-91.55, -23.44) * mm});
            skLineSegment(sketch, "E3241", {"start": v(-91.55, -23.44) * mm, "end": v(-91.6, -23.42) * mm});
            skLineSegment(sketch, "E3242", {"start": v(-91.6, -23.42) * mm, "end": v(-91.64, -23.39) * mm});
            skLineSegment(sketch, "E3243", {"start": v(-91.64, -23.39) * mm, "end": v(-91.69, -23.35) * mm});
            skLineSegment(sketch, "E3244", {"start": v(-91.69, -23.35) * mm, "end": v(-91.73, -23.32) * mm});
            skLineSegment(sketch, "E3245", {"start": v(-91.73, -23.32) * mm, "end": v(-91.76, -23.28) * mm});
            skLineSegment(sketch, "E3246", {"start": v(-91.76, -23.28) * mm, "end": v(-91.8, -23.23) * mm});
            skLineSegment(sketch, "E3247", {"start": v(-91.8, -23.23) * mm, "end": v(-91.83, -23.18) * mm});
            skLineSegment(sketch, "E3248", {"start": v(-91.83, -23.18) * mm, "end": v(-91.85, -23.13) * mm});
            skLineSegment(sketch, "E3249", {"start": v(-91.85, -23.13) * mm, "end": v(-91.87, -23.08) * mm});
            skLineSegment(sketch, "E3250", {"start": v(-91.87, -23.08) * mm, "end": v(-91.88, -23.03) * mm});
            skLineSegment(sketch, "E3251", {"start": v(-91.88, -23.03) * mm, "end": v(-91.9, -22.97) * mm});
            skLineSegment(sketch, "E3252", {"start": v(-91.9, -22.97) * mm, "end": v(-91.9, -22.91) * mm});
            skLineSegment(sketch, "E3253", {"start": v(-91.9, -22.91) * mm, "end": v(-91.9, -21.25) * mm});
            skLineSegment(sketch, "E3254", {"start": v(-91.9, -21.25) * mm, "end": v(-91.9, -21.23) * mm});
            skLineSegment(sketch, "E3255", {"start": v(-91.9, -21.23) * mm, "end": v(-91.9, -21.21) * mm});
            skLineSegment(sketch, "E3256", {"start": v(-91.9, -21.21) * mm, "end": v(-91.89, -21.2) * mm});
            skLineSegment(sketch, "E3257", {"start": v(-91.89, -21.2) * mm, "end": v(-91.88, -21.18) * mm});
            skLineSegment(sketch, "E3258", {"start": v(-91.88, -21.18) * mm, "end": v(-91.87, -21.16) * mm});
            skLineSegment(sketch, "E3259", {"start": v(-91.87, -21.16) * mm, "end": v(-91.87, -21.14) * mm});
            skLineSegment(sketch, "E3260", {"start": v(-91.87, -21.14) * mm, "end": v(-91.86, -21.13) * mm});
            skLineSegment(sketch, "E3261", {"start": v(-91.86, -21.13) * mm, "end": v(-91.84, -21.11) * mm});
            skLineSegment(sketch, "E3262", {"start": v(-91.84, -21.11) * mm, "end": v(-91.83, -21.1) * mm});
            skLineSegment(sketch, "E3263", {"start": v(-91.83, -21.1) * mm, "end": v(-91.82, -21.09) * mm});
            skLineSegment(sketch, "E3264", {"start": v(-91.82, -21.09) * mm, "end": v(-91.8, -21.07) * mm});
            skLineSegment(sketch, "E3265", {"start": v(-91.8, -21.07) * mm, "end": v(-91.79, -21.06) * mm});
            skLineSegment(sketch, "E3266", {"start": v(-91.79, -21.06) * mm, "end": v(-91.77, -21.05) * mm});
            skLineSegment(sketch, "E3267", {"start": v(-91.77, -21.05) * mm, "end": v(-91.75, -21.04) * mm});
            skLineSegment(sketch, "E3268", {"start": v(-91.75, -21.04) * mm, "end": v(-91.73, -21.04) * mm});
            skLineSegment(sketch, "E3269", {"start": v(-91.73, -21.04) * mm, "end": v(-91.72, -21.03) * mm});
            skLineSegment(sketch, "E3270", {"start": v(-91.72, -21.03) * mm, "end": v(-90.93, -20.84) * mm});
            skLineSegment(sketch, "E3271", {"start": v(-90.93, -20.84) * mm, "end": v(-90.16, -20.62) * mm});
            skLineSegment(sketch, "E3272", {"start": v(-90.16, -20.62) * mm, "end": v(-89.41, -20.37) * mm});
            skLineSegment(sketch, "E3273", {"start": v(-89.41, -20.37) * mm, "end": v(-88.68, -20.09) * mm});
            skLineSegment(sketch, "E3274", {"start": v(-88.68, -20.09) * mm, "end": v(-87.96, -19.78) * mm});
            skLineSegment(sketch, "E3275", {"start": v(-87.96, -19.78) * mm, "end": v(-87.26, -19.44) * mm});
            skLineSegment(sketch, "E3276", {"start": v(-87.26, -19.44) * mm, "end": v(-86.57, -19.07) * mm});
            skLineSegment(sketch, "E3277", {"start": v(-86.57, -19.07) * mm, "end": v(-85.9, -18.68) * mm});
            skLineSegment(sketch, "E3278", {"start": v(-85.9, -18.68) * mm, "end": v(-85.25, -18.25) * mm});
            skLineSegment(sketch, "E3279", {"start": v(-85.25, -18.25) * mm, "end": v(-84.62, -17.8) * mm});
            skLineSegment(sketch, "E3280", {"start": v(-84.62, -17.8) * mm, "end": v(-84, -17.32) * mm});
            skLineSegment(sketch, "E3281", {"start": v(-84, -17.32) * mm, "end": v(-83.4, -16.81) * mm});
            skLineSegment(sketch, "E3282", {"start": v(-83.4, -16.81) * mm, "end": v(-82.83, -16.27) * mm});
            skLineSegment(sketch, "E3283", {"start": v(-82.83, -16.27) * mm, "end": v(-82.27, -15.7) * mm});
            skLineSegment(sketch, "E3284", {"start": v(-82.27, -15.7) * mm, "end": v(-81.73, -15.11) * mm});
            skLineSegment(sketch, "E3285", {"start": v(-81.73, -15.11) * mm, "end": v(-81.2, -14.5) * mm});
            skLineSegment(sketch, "E3286", {"start": v(-81.2, -14.5) * mm, "end": v(-80.7, -13.84) * mm});
            skLineSegment(sketch, "E3287", {"start": v(-80.7, -13.84) * mm, "end": v(-80.21, -13.17) * mm});
            skLineSegment(sketch, "E3288", {"start": v(-80.21, -13.17) * mm, "end": v(-79.77, -12.5) * mm});
            skLineSegment(sketch, "E3289", {"start": v(-79.77, -12.5) * mm, "end": v(-79.36, -11.8) * mm});
            skLineSegment(sketch, "E3290", {"start": v(-79.36, -11.8) * mm, "end": v(-78.98, -11.1) * mm});
            skLineSegment(sketch, "E3291", {"start": v(-78.98, -11.1) * mm, "end": v(-78.63, -10.38) * mm});
            skLineSegment(sketch, "E3292", {"start": v(-78.63, -10.38) * mm, "end": v(-78.32, -9.66) * mm});
            skLineSegment(sketch, "E3293", {"start": v(-78.32, -9.66) * mm, "end": v(-78.03, -8.92) * mm});
            skLineSegment(sketch, "E3294", {"start": v(-78.03, -8.92) * mm, "end": v(-77.79, -8.17) * mm});
            skLineSegment(sketch, "E3295", {"start": v(-77.79, -8.17) * mm, "end": v(-77.57, -7.41) * mm});
            skLineSegment(sketch, "E3296", {"start": v(-77.57, -7.41) * mm, "end": v(-77.39, -6.64) * mm});
            skLineSegment(sketch, "E3297", {"start": v(-77.39, -6.64) * mm, "end": v(-77.24, -5.86) * mm});
            skLineSegment(sketch, "E3298", {"start": v(-77.24, -5.86) * mm, "end": v(-77.12, -5.07) * mm});
            skLineSegment(sketch, "E3299", {"start": v(-77.12, -5.07) * mm, "end": v(-77.04, -4.26) * mm});
            skLineSegment(sketch, "E3300", {"start": v(-77.04, -4.26) * mm, "end": v(-76.99, -3.45) * mm});
            skLineSegment(sketch, "E3301", {"start": v(-76.99, -3.45) * mm, "end": v(-76.97, -2.63) * mm});
            skLineSegment(sketch, "E3302", {"start": v(-76.97, -2.63) * mm, "end": v(-77, -1.65) * mm});
            skLineSegment(sketch, "E3303", {"start": v(-77, -1.65) * mm, "end": v(-77.06, -0.7) * mm});
            skLineSegment(sketch, "E3304", {"start": v(-77.06, -0.7) * mm, "end": v(-77.17, 0.25) * mm});
            skLineSegment(sketch, "E3305", {"start": v(-77.17, 0.25) * mm, "end": v(-77.32, 1.17) * mm});
            skLineSegment(sketch, "E3306", {"start": v(-77.32, 1.17) * mm, "end": v(-77.51, 2.08) * mm});
            skLineSegment(sketch, "E3307", {"start": v(-77.51, 2.08) * mm, "end": v(-77.75, 2.97) * mm});
            skLineSegment(sketch, "E3308", {"start": v(-77.75, 2.97) * mm, "end": v(-78.03, 3.84) * mm});
            skLineSegment(sketch, "E3309", {"start": v(-78.03, 3.84) * mm, "end": v(-78.35, 4.69) * mm});
            skLineSegment(sketch, "E3310", {"start": v(-78.35, 4.69) * mm, "end": v(-78.72, 5.52) * mm});
            skLineSegment(sketch, "E3311", {"start": v(-78.72, 5.52) * mm, "end": v(-79.13, 6.33) * mm});
            skLineSegment(sketch, "E3312", {"start": v(-79.13, 6.33) * mm, "end": v(-79.58, 7.13) * mm});
            skLineSegment(sketch, "E3313", {"start": v(-79.58, 7.13) * mm, "end": v(-80.08, 7.9) * mm});
            skLineSegment(sketch, "E3314", {"start": v(-80.08, 7.9) * mm, "end": v(-80.61, 8.66) * mm});
            skLineSegment(sketch, "E3315", {"start": v(-80.61, 8.66) * mm, "end": v(-81.2, 9.4) * mm});
            skLineSegment(sketch, "E3316", {"start": v(-81.2, 9.4) * mm, "end": v(-81.81, 10.1) * mm});
            skLineSegment(sketch, "E3317", {"start": v(-81.81, 10.1) * mm, "end": v(-82.48, 10.8) * mm});
            skLineSegment(sketch, "E3318", {"start": v(-82.48, 10.8) * mm, "end": v(-83.17, 11.47) * mm});
            skLineSegment(sketch, "E3319", {"start": v(-83.17, 11.47) * mm, "end": v(-83.89, 12.09) * mm});
            skLineSegment(sketch, "E3320", {"start": v(-83.89, 12.09) * mm, "end": v(-84.62, 12.67) * mm});
            skLineSegment(sketch, "E3321", {"start": v(-84.62, 12.67) * mm, "end": v(-85.38, 13.2) * mm});
            skLineSegment(sketch, "E3322", {"start": v(-85.38, 13.2) * mm, "end": v(-86.15, 13.7) * mm});
            skLineSegment(sketch, "E3323", {"start": v(-86.15, 13.7) * mm, "end": v(-86.95, 14.15) * mm});
            skLineSegment(sketch, "E3324", {"start": v(-86.95, 14.15) * mm, "end": v(-87.76, 14.56) * mm});
            skLineSegment(sketch, "E3325", {"start": v(-87.76, 14.56) * mm, "end": v(-88.6, 14.93) * mm});
            skLineSegment(sketch, "E3326", {"start": v(-88.6, 14.93) * mm, "end": v(-89.44, 15.25) * mm});
            skLineSegment(sketch, "E3327", {"start": v(-89.44, 15.25) * mm, "end": v(-90.31, 15.53) * mm});
            skLineSegment(sketch, "E3328", {"start": v(-90.31, 15.53) * mm, "end": v(-91.2, 15.77) * mm});
            skLineSegment(sketch, "E3329", {"start": v(-91.2, 15.77) * mm, "end": v(-92.1, 15.96) * mm});
            skLineSegment(sketch, "E3330", {"start": v(-92.1, 15.96) * mm, "end": v(-93.03, 16.11) * mm});
            skLineSegment(sketch, "E3331", {"start": v(-93.03, 16.11) * mm, "end": v(-93.97, 16.22) * mm});
            skLineSegment(sketch, "E3332", {"start": v(-93.97, 16.22) * mm, "end": v(-94.93, 16.29) * mm});
            skLineSegment(sketch, "E3333", {"start": v(-94.93, 16.29) * mm, "end": v(-95.91, 16.3) * mm});
            skLineSegment(sketch, "E3334", {"start": v(-95.91, 16.3) * mm, "end": v(-96.88, 16.29) * mm});
            skLineSegment(sketch, "E3335", {"start": v(-96.88, 16.29) * mm, "end": v(-97.84, 16.22) * mm});
            skLineSegment(sketch, "E3336", {"start": v(-97.84, 16.22) * mm, "end": v(-98.77, 16.11) * mm});
            skLineSegment(sketch, "E3337", {"start": v(-98.77, 16.11) * mm, "end": v(-99.7, 15.96) * mm});
            skLineSegment(sketch, "E3338", {"start": v(-99.7, 15.96) * mm, "end": v(-100.6, 15.77) * mm});
            skLineSegment(sketch, "E3339", {"start": v(-100.6, 15.77) * mm, "end": v(-101.48, 15.53) * mm});
            skLineSegment(sketch, "E3340", {"start": v(-101.48, 15.53) * mm, "end": v(-102.34, 15.25) * mm});
            skLineSegment(sketch, "E3341", {"start": v(-102.34, 15.25) * mm, "end": v(-103.19, 14.93) * mm});
            skLineSegment(sketch, "E3342", {"start": v(-103.19, 14.93) * mm, "end": v(-104.02, 14.56) * mm});
            skLineSegment(sketch, "E3343", {"start": v(-104.02, 14.56) * mm, "end": v(-104.83, 14.15) * mm});
            skLineSegment(sketch, "E3344", {"start": v(-104.83, 14.15) * mm, "end": v(-105.62, 13.7) * mm});
            skLineSegment(sketch, "E3345", {"start": v(-105.62, 13.7) * mm, "end": v(-106.4, 13.2) * mm});
            skLineSegment(sketch, "E3346", {"start": v(-106.4, 13.2) * mm, "end": v(-107.15, 12.67) * mm});
            skLineSegment(sketch, "E3347", {"start": v(-107.15, 12.67) * mm, "end": v(-107.88, 12.09) * mm});
            skLineSegment(sketch, "E3348", {"start": v(-107.88, 12.09) * mm, "end": v(-108.6, 11.47) * mm});
            skLineSegment(sketch, "E3349", {"start": v(-108.6, 11.47) * mm, "end": v(-109.29, 10.8) * mm});
            skLineSegment(sketch, "E3350", {"start": v(-109.29, 10.8) * mm, "end": v(-109.95, 10.1) * mm});
            skLineSegment(sketch, "E3351", {"start": v(-109.95, 10.1) * mm, "end": v(-110.58, 9.4) * mm});
            skLineSegment(sketch, "E3352", {"start": v(-110.58, 9.4) * mm, "end": v(-111.15, 8.66) * mm});
            skLineSegment(sketch, "E3353", {"start": v(-111.15, 8.66) * mm, "end": v(-111.7, 7.9) * mm});
            skLineSegment(sketch, "E3354", {"start": v(-111.7, 7.9) * mm, "end": v(-112.19, 7.13) * mm});
            skLineSegment(sketch, "E3355", {"start": v(-112.19, 7.13) * mm, "end": v(-112.64, 6.33) * mm});
            skLineSegment(sketch, "E3356", {"start": v(-112.64, 6.33) * mm, "end": v(-113.05, 5.52) * mm});
            skLineSegment(sketch, "E3357", {"start": v(-113.05, 5.52) * mm, "end": v(-113.41, 4.69) * mm});
            skLineSegment(sketch, "E3358", {"start": v(-113.41, 4.69) * mm, "end": v(-113.74, 3.84) * mm});
            skLineSegment(sketch, "E3359", {"start": v(-113.74, 3.84) * mm, "end": v(-114.02, 2.97) * mm});
            skLineSegment(sketch, "E3360", {"start": v(-114.02, 2.97) * mm, "end": v(-114.25, 2.08) * mm});
            skLineSegment(sketch, "E3361", {"start": v(-114.25, 2.08) * mm, "end": v(-114.45, 1.17) * mm});
            skLineSegment(sketch, "E3362", {"start": v(-114.45, 1.17) * mm, "end": v(-114.6, 0.25) * mm});
            skLineSegment(sketch, "E3363", {"start": v(-114.6, 0.25) * mm, "end": v(-114.7, -0.7) * mm});
            skLineSegment(sketch, "E3364", {"start": v(-114.7, -0.7) * mm, "end": v(-114.77, -1.65) * mm});
            skLineSegment(sketch, "E3365", {"start": v(-114.77, -1.65) * mm, "end": v(-114.8, -2.63) * mm});
            skLineSegment(sketch, "E3366", {"start": v(-114.8, -2.63) * mm, "end": v(-114.78, -3.45) * mm});
            skLineSegment(sketch, "E3367", {"start": v(-114.78, -3.45) * mm, "end": v(-114.73, -4.26) * mm});
            skLineSegment(sketch, "E3368", {"start": v(-114.73, -4.26) * mm, "end": v(-114.65, -5.07) * mm});
            skLineSegment(sketch, "E3369", {"start": v(-114.65, -5.07) * mm, "end": v(-114.53, -5.86) * mm});
            skLineSegment(sketch, "E3370", {"start": v(-114.53, -5.86) * mm, "end": v(-114.38, -6.64) * mm});
            skLineSegment(sketch, "E3371", {"start": v(-114.38, -6.64) * mm, "end": v(-114.2, -7.41) * mm});
            skLineSegment(sketch, "E3372", {"start": v(-114.2, -7.41) * mm, "end": v(-113.98, -8.17) * mm});
            skLineSegment(sketch, "E3373", {"start": v(-113.98, -8.17) * mm, "end": v(-113.73, -8.92) * mm});
            skLineSegment(sketch, "E3374", {"start": v(-113.73, -8.92) * mm, "end": v(-113.45, -9.66) * mm});
            skLineSegment(sketch, "E3375", {"start": v(-113.45, -9.66) * mm, "end": v(-113.14, -10.38) * mm});
            skLineSegment(sketch, "E3376", {"start": v(-113.14, -10.38) * mm, "end": v(-112.8, -11.1) * mm});
            skLineSegment(sketch, "E3377", {"start": v(-112.8, -11.1) * mm, "end": v(-112.41, -11.8) * mm});
            skLineSegment(sketch, "E3378", {"start": v(-112.41, -11.8) * mm, "end": v(-112, -12.5) * mm});
            skLineSegment(sketch, "E3379", {"start": v(-112, -12.5) * mm, "end": v(-111.55, -13.17) * mm});
            skLineSegment(sketch, "E3380", {"start": v(-111.55, -13.17) * mm, "end": v(-111.08, -13.84) * mm});
            skLineSegment(sketch, "E3381", {"start": v(-111.08, -13.84) * mm, "end": v(-110.57, -14.5) * mm});
            skLineSegment(sketch, "E3382", {"start": v(-110.57, -14.5) * mm, "end": v(-110.04, -15.11) * mm});
            skLineSegment(sketch, "E3383", {"start": v(-110.04, -15.11) * mm, "end": v(-109.5, -15.7) * mm});
            skLineSegment(sketch, "E3384", {"start": v(-109.5, -15.7) * mm, "end": v(-108.94, -16.27) * mm});
            skLineSegment(sketch, "E3385", {"start": v(-108.94, -16.27) * mm, "end": v(-108.36, -16.81) * mm});
            skLineSegment(sketch, "E3386", {"start": v(-108.36, -16.81) * mm, "end": v(-107.76, -17.32) * mm});
            skLineSegment(sketch, "E3387", {"start": v(-107.76, -17.32) * mm, "end": v(-107.15, -17.8) * mm});
            skLineSegment(sketch, "E3388", {"start": v(-107.15, -17.8) * mm, "end": v(-106.51, -18.25) * mm});
            skLineSegment(sketch, "E3389", {"start": v(-106.51, -18.25) * mm, "end": v(-105.86, -18.68) * mm});
            skLineSegment(sketch, "E3390", {"start": v(-105.86, -18.68) * mm, "end": v(-105.2, -19.07) * mm});
            skLineSegment(sketch, "E3391", {"start": v(-105.2, -19.07) * mm, "end": v(-104.51, -19.44) * mm});
            skLineSegment(sketch, "E3392", {"start": v(-104.51, -19.44) * mm, "end": v(-103.81, -19.78) * mm});
            skLineSegment(sketch, "E3393", {"start": v(-103.81, -19.78) * mm, "end": v(-103.1, -20.09) * mm});
            skLineSegment(sketch, "E3394", {"start": v(-103.1, -20.09) * mm, "end": v(-102.36, -20.37) * mm});
            skLineSegment(sketch, "E3395", {"start": v(-102.36, -20.37) * mm, "end": v(-101.6, -20.62) * mm});
            skLineSegment(sketch, "E3396", {"start": v(-101.6, -20.62) * mm, "end": v(-100.84, -20.84) * mm});
            skLineSegment(sketch, "E3397", {"start": v(-100.84, -20.84) * mm, "end": v(-100.05, -21.03) * mm});
            skLineSegment(sketch, "E3398", {"start": v(-100.05, -21.03) * mm, "end": v(-100.03, -21.04) * mm});
            skLineSegment(sketch, "E3399", {"start": v(-100.03, -21.04) * mm, "end": v(-100.01, -21.04) * mm});
            skLineSegment(sketch, "E3400", {"start": v(-100.01, -21.04) * mm, "end": v(-100, -21.05) * mm});
            skLineSegment(sketch, "E3401", {"start": v(-100, -21.05) * mm, "end": v(-99.98, -21.06) * mm});
            skLineSegment(sketch, "E3402", {"start": v(-99.98, -21.06) * mm, "end": v(-99.96, -21.07) * mm});
            skLineSegment(sketch, "E3403", {"start": v(-99.96, -21.07) * mm, "end": v(-99.95, -21.09) * mm});
            skLineSegment(sketch, "E3404", {"start": v(-99.95, -21.09) * mm, "end": v(-99.94, -21.1) * mm});
            skLineSegment(sketch, "E3405", {"start": v(-99.94, -21.1) * mm, "end": v(-99.92, -21.11) * mm});
            skLineSegment(sketch, "E3406", {"start": v(-99.92, -21.11) * mm, "end": v(-99.91, -21.13) * mm});
            skLineSegment(sketch, "E3407", {"start": v(-99.91, -21.13) * mm, "end": v(-99.9, -21.14) * mm});
            skLineSegment(sketch, "E3408", {"start": v(-99.9, -21.14) * mm, "end": v(-99.9, -21.16) * mm});
            skLineSegment(sketch, "E3409", {"start": v(-99.9, -21.16) * mm, "end": v(-99.89, -21.18) * mm});
            skLineSegment(sketch, "E3410", {"start": v(-99.89, -21.18) * mm, "end": v(-99.88, -21.2) * mm});
            skLineSegment(sketch, "E3411", {"start": v(-99.88, -21.2) * mm, "end": v(-99.88, -21.21) * mm});
            skLineSegment(sketch, "E3412", {"start": v(-99.88, -21.21) * mm, "end": v(-99.87, -21.23) * mm});
            skLineSegment(sketch, "E3413", {"start": v(-99.87, -21.23) * mm, "end": v(-99.87, -21.25) * mm});
            skLineSegment(sketch, "E3414", {"start": v(-99.87, -21.25) * mm, "end": v(-99.87, -22.91) * mm});
            skLineSegment(sketch, "E3415", {"start": v(-99.87, -22.91) * mm, "end": v(-99.88, -22.97) * mm});
            skLineSegment(sketch, "E3416", {"start": v(-99.88, -22.97) * mm, "end": v(-99.89, -23.03) * mm});
            skLineSegment(sketch, "E3417", {"start": v(-99.89, -23.03) * mm, "end": v(-99.9, -23.08) * mm});
            skLineSegment(sketch, "E3418", {"start": v(-99.9, -23.08) * mm, "end": v(-99.92, -23.13) * mm});
            skLineSegment(sketch, "E3419", {"start": v(-99.92, -23.13) * mm, "end": v(-99.94, -23.18) * mm});
            skLineSegment(sketch, "E3420", {"start": v(-99.94, -23.18) * mm, "end": v(-99.97, -23.23) * mm});
            skLineSegment(sketch, "E3421", {"start": v(-99.97, -23.23) * mm, "end": v(-100, -23.28) * mm});
            skLineSegment(sketch, "E3422", {"start": v(-100, -23.28) * mm, "end": v(-100.04, -23.32) * mm});
            skLineSegment(sketch, "E3423", {"start": v(-100.04, -23.32) * mm, "end": v(-100.08, -23.35) * mm});
            skLineSegment(sketch, "E3424", {"start": v(-100.08, -23.35) * mm, "end": v(-100.13, -23.39) * mm});
            skLineSegment(sketch, "E3425", {"start": v(-100.13, -23.39) * mm, "end": v(-100.17, -23.42) * mm});
            skLineSegment(sketch, "E3426", {"start": v(-100.17, -23.42) * mm, "end": v(-100.22, -23.44) * mm});
            skLineSegment(sketch, "E3427", {"start": v(-100.22, -23.44) * mm, "end": v(-100.28, -23.46) * mm});
            skLineSegment(sketch, "E3428", {"start": v(-100.28, -23.46) * mm, "end": v(-100.33, -23.47) * mm});
            skLineSegment(sketch, "E3429", {"start": v(-100.33, -23.47) * mm, "end": v(-100.39, -23.48) * mm});
            skLineSegment(sketch, "E3430", {"start": v(-100.39, -23.48) * mm, "end": v(-100.44, -23.48) * mm});
            skLineSegment(sketch, "E3431", {"start": v(-100.44, -23.48) * mm, "end": v(-140.73, -23.48) * mm});
            skLineSegment(sketch, "E3432", {"start": v(-140.73, -23.48) * mm, "end": v(-140.86, -23.48) * mm});
            skLineSegment(sketch, "E3433", {"start": v(-140.86, -23.48) * mm, "end": v(-140.97, -23.47) * mm});
            skLineSegment(sketch, "E3434", {"start": v(-140.97, -23.47) * mm, "end": v(-141.08, -23.45) * mm});
            skLineSegment(sketch, "E3435", {"start": v(-141.08, -23.45) * mm, "end": v(-141.18, -23.43) * mm});
            skLineSegment(sketch, "E3436", {"start": v(-141.18, -23.43) * mm, "end": v(-141.27, -23.4) * mm});
            skLineSegment(sketch, "E3437", {"start": v(-141.27, -23.4) * mm, "end": v(-141.35, -23.35) * mm});
            skLineSegment(sketch, "E3438", {"start": v(-141.35, -23.35) * mm, "end": v(-141.43, -23.3) * mm});
            skLineSegment(sketch, "E3439", {"start": v(-141.43, -23.3) * mm, "end": v(-141.5, -23.25) * mm});
            skLineSegment(sketch, "E3440", {"start": v(-141.5, -23.25) * mm, "end": v(-141.55, -23.19) * mm});
            skLineSegment(sketch, "E3441", {"start": v(-141.55, -23.19) * mm, "end": v(-141.6, -23.12) * mm});
            skLineSegment(sketch, "E3442", {"start": v(-141.6, -23.12) * mm, "end": v(-141.65, -23.04) * mm});
            skLineSegment(sketch, "E3443", {"start": v(-141.65, -23.04) * mm, "end": v(-141.68, -22.95) * mm});
            skLineSegment(sketch, "E3444", {"start": v(-141.68, -22.95) * mm, "end": v(-141.7, -22.86) * mm});
            skLineSegment(sketch, "E3445", {"start": v(-141.7, -22.86) * mm, "end": v(-141.73, -22.75) * mm});
            skLineSegment(sketch, "E3446", {"start": v(-141.73, -22.75) * mm, "end": v(-141.74, -22.64) * mm});
            skLineSegment(sketch, "E3447", {"start": v(-141.74, -22.64) * mm, "end": v(-141.74, -22.53) * mm});
            skLineSegment(sketch, "E3448", {"start": v(-141.74, -22.53) * mm, "end": v(-141.74, -22.4) * mm});
            skLineSegment(sketch, "E3449", {"start": v(-141.74, -22.4) * mm, "end": v(-141.73, -22.3) * mm});
            skLineSegment(sketch, "E3450", {"start": v(-141.73, -22.3) * mm, "end": v(-141.7, -22.2) * mm});
            skLineSegment(sketch, "E3451", {"start": v(-141.7, -22.2) * mm, "end": v(-141.68, -22.1) * mm});
            skLineSegment(sketch, "E3452", {"start": v(-141.68, -22.1) * mm, "end": v(-141.65, -22.01) * mm});
            skLineSegment(sketch, "E3453", {"start": v(-141.65, -22.01) * mm, "end": v(-141.6, -21.94) * mm});
            skLineSegment(sketch, "E3454", {"start": v(-141.6, -21.94) * mm, "end": v(-141.55, -21.86) * mm});
            skLineSegment(sketch, "E3455", {"start": v(-141.55, -21.86) * mm, "end": v(-141.5, -21.8) * mm});
            skLineSegment(sketch, "E3456", {"start": v(-141.5, -21.8) * mm, "end": v(-141.43, -21.75) * mm});
            skLineSegment(sketch, "E3457", {"start": v(-141.43, -21.75) * mm, "end": v(-141.35, -21.7) * mm});
            skLineSegment(sketch, "E3458", {"start": v(-141.35, -21.7) * mm, "end": v(-141.27, -21.66) * mm});
            skLineSegment(sketch, "E3459", {"start": v(-141.27, -21.66) * mm, "end": v(-141.18, -21.63) * mm});
            skLineSegment(sketch, "E3460", {"start": v(-141.18, -21.63) * mm, "end": v(-141.08, -21.6) * mm});
            skLineSegment(sketch, "E3461", {"start": v(-141.08, -21.6) * mm, "end": v(-140.97, -21.58) * mm});
            skLineSegment(sketch, "E3462", {"start": v(-140.97, -21.58) * mm, "end": v(-140.86, -21.57) * mm});
            skLineSegment(sketch, "E3463", {"start": v(-140.86, -21.57) * mm, "end": v(-140.73, -21.57) * mm});
            skLineSegment(sketch, "E3464", {"start": v(-140.73, -21.57) * mm, "end": v(-123.48, -21.57) * mm});
            skLineSegment(sketch, "E3465", {"start": v(-123.48, -21.57) * mm, "end": v(-123.27, -21.56) * mm});
            skLineSegment(sketch, "E3466", {"start": v(-123.27, -21.56) * mm, "end": v(-123.07, -21.55) * mm});
            skLineSegment(sketch, "E3467", {"start": v(-123.07, -21.55) * mm, "end": v(-122.87, -21.53) * mm});
            skLineSegment(sketch, "E3468", {"start": v(-122.87, -21.53) * mm, "end": v(-122.67, -21.5) * mm});
            skLineSegment(sketch, "E3469", {"start": v(-122.67, -21.5) * mm, "end": v(-122.48, -21.46) * mm});
            skLineSegment(sketch, "E3470", {"start": v(-122.48, -21.46) * mm, "end": v(-122.3, -21.4) * mm});
            skLineSegment(sketch, "E3471", {"start": v(-122.3, -21.4) * mm, "end": v(-122.1, -21.35) * mm});
            skLineSegment(sketch, "E3472", {"start": v(-122.1, -21.35) * mm, "end": v(-121.93, -21.28) * mm});
            skLineSegment(sketch, "E3473", {"start": v(-121.93, -21.28) * mm, "end": v(-121.75, -21.2) * mm});
            skLineSegment(sketch, "E3474", {"start": v(-121.75, -21.2) * mm, "end": v(-121.58, -21.12) * mm});
            skLineSegment(sketch, "E3475", {"start": v(-121.58, -21.12) * mm, "end": v(-121.41, -21.03) * mm});
            skLineSegment(sketch, "E3476", {"start": v(-121.41, -21.03) * mm, "end": v(-121.25, -20.92) * mm});
            skLineSegment(sketch, "E3477", {"start": v(-121.25, -20.92) * mm, "end": v(-121.09, -20.81) * mm});
            skLineSegment(sketch, "E3478", {"start": v(-121.09, -20.81) * mm, "end": v(-120.93, -20.7) * mm});
            skLineSegment(sketch, "E3479", {"start": v(-120.93, -20.7) * mm, "end": v(-120.78, -20.57) * mm});
            skLineSegment(sketch, "E3480", {"start": v(-120.78, -20.57) * mm, "end": v(-120.63, -20.43) * mm});
            skLineSegment(sketch, "E3481", {"start": v(-120.63, -20.43) * mm, "end": v(-120.5, -20.28) * mm});
            skLineSegment(sketch, "E3482", {"start": v(-120.5, -20.28) * mm, "end": v(-120.36, -20.13) * mm});
            skLineSegment(sketch, "E3483", {"start": v(-120.36, -20.13) * mm, "end": v(-120.24, -19.98) * mm});
            skLineSegment(sketch, "E3484", {"start": v(-120.24, -19.98) * mm, "end": v(-120.12, -19.82) * mm});
            skLineSegment(sketch, "E3485", {"start": v(-120.12, -19.82) * mm, "end": v(-120.02, -19.66) * mm});
            skLineSegment(sketch, "E3486", {"start": v(-120.02, -19.66) * mm, "end": v(-119.92, -19.5) * mm});
            skLineSegment(sketch, "E3487", {"start": v(-119.92, -19.5) * mm, "end": v(-119.84, -19.33) * mm});
            skLineSegment(sketch, "E3488", {"start": v(-119.84, -19.33) * mm, "end": v(-119.76, -19.15) * mm});
            skLineSegment(sketch, "E3489", {"start": v(-119.76, -19.15) * mm, "end": v(-119.69, -18.97) * mm});
            skLineSegment(sketch, "E3490", {"start": v(-119.69, -18.97) * mm, "end": v(-119.63, -18.79) * mm});
            skLineSegment(sketch, "E3491", {"start": v(-119.63, -18.79) * mm, "end": v(-119.58, -18.6) * mm});
            skLineSegment(sketch, "E3492", {"start": v(-119.58, -18.6) * mm, "end": v(-119.54, -18.4) * mm});
            skLineSegment(sketch, "E3493", {"start": v(-119.54, -18.4) * mm, "end": v(-119.5, -18.21) * mm});
            skLineSegment(sketch, "E3494", {"start": v(-119.5, -18.21) * mm, "end": v(-119.48, -18.02) * mm});
            skLineSegment(sketch, "E3495", {"start": v(-119.48, -18.02) * mm, "end": v(-119.47, -17.81) * mm});
            skLineSegment(sketch, "E3496", {"start": v(-119.47, -17.81) * mm, "end": v(-119.46, -17.6) * mm});
            skLineSegment(sketch, "E3497", {"start": v(-119.46, -17.6) * mm, "end": v(-119.47, -17.4) * mm});
            skLineSegment(sketch, "E3498", {"start": v(-119.47, -17.4) * mm, "end": v(-119.48, -17.18) * mm});
            skLineSegment(sketch, "E3499", {"start": v(-119.48, -17.18) * mm, "end": v(-119.5, -16.98) * mm});
            skLineSegment(sketch, "E3500", {"start": v(-119.5, -16.98) * mm, "end": v(-119.54, -16.78) * mm});
            skLineSegment(sketch, "E3501", {"start": v(-119.54, -16.78) * mm, "end": v(-119.58, -16.58) * mm});
            skLineSegment(sketch, "E3502", {"start": v(-119.58, -16.58) * mm, "end": v(-119.63, -16.39) * mm});
            skLineSegment(sketch, "E3503", {"start": v(-119.63, -16.39) * mm, "end": v(-119.68, -16.2) * mm});
            skLineSegment(sketch, "E3504", {"start": v(-119.68, -16.2) * mm, "end": v(-119.75, -16.02) * mm});
            skLineSegment(sketch, "E3505", {"start": v(-119.75, -16.02) * mm, "end": v(-119.83, -15.84) * mm});
            skLineSegment(sketch, "E3506", {"start": v(-119.83, -15.84) * mm, "end": v(-119.91, -15.67) * mm});
            skLineSegment(sketch, "E3507", {"start": v(-119.91, -15.67) * mm, "end": v(-120, -15.5) * mm});
            skLineSegment(sketch, "E3508", {"start": v(-120, -15.5) * mm, "end": v(-120.1, -15.34) * mm});
            skLineSegment(sketch, "E3509", {"start": v(-120.1, -15.34) * mm, "end": v(-120.22, -15.18) * mm});
            skLineSegment(sketch, "E3510", {"start": v(-120.22, -15.18) * mm, "end": v(-120.34, -15.02) * mm});
            skLineSegment(sketch, "E3511", {"start": v(-120.34, -15.02) * mm, "end": v(-120.47, -14.87) * mm});
            skLineSegment(sketch, "E3512", {"start": v(-120.47, -14.87) * mm, "end": v(-120.6, -14.73) * mm});
            skLineSegment(sketch, "E3513", {"start": v(-120.6, -14.73) * mm, "end": v(-120.75, -14.6) * mm});
            skLineSegment(sketch, "E3514", {"start": v(-120.75, -14.6) * mm, "end": v(-120.9, -14.46) * mm});
            skLineSegment(sketch, "E3515", {"start": v(-120.9, -14.46) * mm, "end": v(-121.05, -14.34) * mm});
            skLineSegment(sketch, "E3516", {"start": v(-121.05, -14.34) * mm, "end": v(-121.21, -14.23) * mm});
            skLineSegment(sketch, "E3517", {"start": v(-121.21, -14.23) * mm, "end": v(-121.37, -14.13) * mm});
            skLineSegment(sketch, "E3518", {"start": v(-121.37, -14.13) * mm, "end": v(-121.54, -14.04) * mm});
            skLineSegment(sketch, "E3519", {"start": v(-121.54, -14.04) * mm, "end": v(-121.72, -13.95) * mm});
            skLineSegment(sketch, "E3520", {"start": v(-121.72, -13.95) * mm, "end": v(-121.9, -13.88) * mm});
            skLineSegment(sketch, "E3521", {"start": v(-121.9, -13.88) * mm, "end": v(-122.08, -13.8) * mm});
            skLineSegment(sketch, "E3522", {"start": v(-122.08, -13.8) * mm, "end": v(-122.26, -13.75) * mm});
            skLineSegment(sketch, "E3523", {"start": v(-122.26, -13.75) * mm, "end": v(-122.46, -13.7) * mm});
            skLineSegment(sketch, "E3524", {"start": v(-122.46, -13.7) * mm, "end": v(-122.65, -13.66) * mm});
            skLineSegment(sketch, "E3525", {"start": v(-122.65, -13.66) * mm, "end": v(-122.85, -13.63) * mm});
            skLineSegment(sketch, "E3526", {"start": v(-122.85, -13.63) * mm, "end": v(-123.06, -13.6) * mm});
            skLineSegment(sketch, "E3527", {"start": v(-123.06, -13.6) * mm, "end": v(-123.27, -13.6) * mm});
            skLineSegment(sketch, "E3528", {"start": v(-123.27, -13.6) * mm, "end": v(-123.48, -13.59) * mm});
            skLineSegment(sketch, "E3529", {"start": v(-123.48, -13.59) * mm, "end": v(-138.61, -13.59) * mm});
            skLineSegment(sketch, "E3530", {"start": v(-138.61, -13.59) * mm, "end": v(-138.9, -13.58) * mm});
            skLineSegment(sketch, "E3531", {"start": v(-138.9, -13.58) * mm, "end": v(-139.18, -13.54) * mm});
            skLineSegment(sketch, "E3532", {"start": v(-139.18, -13.54) * mm, "end": v(-139.46, -13.47) * mm});
            skLineSegment(sketch, "E3533", {"start": v(-139.46, -13.47) * mm, "end": v(-139.72, -13.38) * mm});
            skLineSegment(sketch, "E3534", {"start": v(-139.72, -13.38) * mm, "end": v(-139.97, -13.27) * mm});
            skLineSegment(sketch, "E3535", {"start": v(-139.97, -13.27) * mm, "end": v(-140.22, -13.14) * mm});
            skLineSegment(sketch, "E3536", {"start": v(-140.22, -13.14) * mm, "end": v(-140.44, -13) * mm});
            skLineSegment(sketch, "E3537", {"start": v(-140.44, -13) * mm, "end": v(-140.66, -12.82) * mm});
            skLineSegment(sketch, "E3538", {"start": v(-140.66, -12.82) * mm, "end": v(-140.86, -12.63) * mm});
            skLineSegment(sketch, "E3539", {"start": v(-140.86, -12.63) * mm, "end": v(-141.04, -12.43) * mm});
            skLineSegment(sketch, "E3540", {"start": v(-141.04, -12.43) * mm, "end": v(-141.2, -12.2) * mm});
            skLineSegment(sketch, "E3541", {"start": v(-141.2, -12.2) * mm, "end": v(-141.34, -11.97) * mm});
            skLineSegment(sketch, "E3542", {"start": v(-141.34, -11.97) * mm, "end": v(-141.46, -11.72) * mm});
            skLineSegment(sketch, "E3543", {"start": v(-141.46, -11.72) * mm, "end": v(-141.56, -11.46) * mm});
            skLineSegment(sketch, "E3544", {"start": v(-141.56, -11.46) * mm, "end": v(-141.64, -11.19) * mm});
            skLineSegment(sketch, "E3545", {"start": v(-141.64, -11.19) * mm, "end": v(-141.69, -10.9) * mm});
            skLineSegment(sketch, "E3546", {"start": v(-141.69, -10.9) * mm, "end": v(-141.72, -10.65) * mm});
            skLineSegment(sketch, "E3547", {"start": v(-141.72, -10.65) * mm, "end": v(-141.74, -10.4) * mm});
            skLineSegment(sketch, "E3548", {"start": v(-141.74, -10.4) * mm, "end": v(-141.74, -10.16) * mm});
            skLineSegment(sketch, "E3549", {"start": v(-141.74, -10.16) * mm, "end": v(-141.74, -9.92) * mm});
            skLineSegment(sketch, "E3550", {"start": v(-141.74, -9.92) * mm, "end": v(-141.72, -9.7) * mm});
            skLineSegment(sketch, "E3551", {"start": v(-141.72, -9.7) * mm, "end": v(-141.7, -9.47) * mm});
            skLineSegment(sketch, "E3552", {"start": v(-141.7, -9.47) * mm, "end": v(-141.65, -9.26) * mm});
            skLineSegment(sketch, "E3553", {"start": v(-141.65, -9.26) * mm, "end": v(-141.6, -9.05) * mm});
            skLineSegment(sketch, "E3554", {"start": v(-141.6, -9.05) * mm, "end": v(-141.54, -8.85) * mm});
            skLineSegment(sketch, "E3555", {"start": v(-141.54, -8.85) * mm, "end": v(-141.47, -8.65) * mm});
            skLineSegment(sketch, "E3556", {"start": v(-141.47, -8.65) * mm, "end": v(-141.38, -8.47) * mm});
            skLineSegment(sketch, "E3557", {"start": v(-141.38, -8.47) * mm, "end": v(-141.29, -8.29) * mm});
            skLineSegment(sketch, "E3558", {"start": v(-141.29, -8.29) * mm, "end": v(-141.18, -8.12) * mm});
            skLineSegment(sketch, "E3559", {"start": v(-141.18, -8.12) * mm, "end": v(-141.06, -7.95) * mm});
            skLineSegment(sketch, "E3560", {"start": v(-141.06, -7.95) * mm, "end": v(-140.93, -7.8) * mm});
            skLineSegment(sketch, "E3561", {"start": v(-140.93, -7.8) * mm, "end": v(-140.8, -7.65) * mm});
            skLineSegment(sketch, "E3562", {"start": v(-140.8, -7.65) * mm, "end": v(-140.67, -7.53) * mm});
            skLineSegment(sketch, "E3563", {"start": v(-140.67, -7.53) * mm, "end": v(-140.55, -7.43) * mm});
            skLineSegment(sketch, "E3564", {"start": v(-140.55, -7.43) * mm, "end": v(-140.42, -7.33) * mm});
            skLineSegment(sketch, "E3565", {"start": v(-140.42, -7.33) * mm, "end": v(-140.28, -7.23) * mm});
            skLineSegment(sketch, "E3566", {"start": v(-140.28, -7.23) * mm, "end": v(-140.14, -7.15) * mm});
            skLineSegment(sketch, "E3567", {"start": v(-140.14, -7.15) * mm, "end": v(-140, -7.07) * mm});
            skLineSegment(sketch, "E3568", {"start": v(-140, -7.07) * mm, "end": v(-139.85, -7) * mm});
            skLineSegment(sketch, "E3569", {"start": v(-139.85, -7) * mm, "end": v(-139.7, -6.94) * mm});
            skLineSegment(sketch, "E3570", {"start": v(-139.7, -6.94) * mm, "end": v(-139.53, -6.88) * mm});
            skLineSegment(sketch, "E3571", {"start": v(-139.53, -6.88) * mm, "end": v(-139.37, -6.83) * mm});
            skLineSegment(sketch, "E3572", {"start": v(-139.37, -6.83) * mm, "end": v(-139.2, -6.8) * mm});
            skLineSegment(sketch, "E3573", {"start": v(-139.2, -6.8) * mm, "end": v(-139.03, -6.76) * mm});
            skLineSegment(sketch, "E3574", {"start": v(-139.03, -6.76) * mm, "end": v(-138.85, -6.73) * mm});
            skLineSegment(sketch, "E3575", {"start": v(-138.85, -6.73) * mm, "end": v(-138.67, -6.71) * mm});
            skLineSegment(sketch, "E3576", {"start": v(-138.67, -6.71) * mm, "end": v(-138.49, -6.7) * mm});
            skLineSegment(sketch, "E3577", {"start": v(-138.49, -6.7) * mm, "end": v(-138.3, -6.7) * mm});
            skLineSegment(sketch, "E3578", {"start": v(-138.3, -6.7) * mm, "end": v(-128.4, -6.7) * mm});
            skLineSegment(sketch, "E3579", {"start": v(-128.4, -6.7) * mm, "end": v(-128.18, -6.7) * mm});
            skLineSegment(sketch, "E3580", {"start": v(-128.18, -6.7) * mm, "end": v(-127.97, -6.68) * mm});
            skLineSegment(sketch, "E3581", {"start": v(-127.97, -6.68) * mm, "end": v(-127.76, -6.66) * mm});
            skLineSegment(sketch, "E3582", {"start": v(-127.76, -6.66) * mm, "end": v(-127.55, -6.63) * mm});
            skLineSegment(sketch, "E3583", {"start": v(-127.55, -6.63) * mm, "end": v(-127.35, -6.6) * mm});
            skLineSegment(sketch, "E3584", {"start": v(-127.35, -6.6) * mm, "end": v(-127.16, -6.54) * mm});
            skLineSegment(sketch, "E3585", {"start": v(-127.16, -6.54) * mm, "end": v(-126.97, -6.49) * mm});
            skLineSegment(sketch, "E3586", {"start": v(-126.97, -6.49) * mm, "end": v(-126.79, -6.42) * mm});
            skLineSegment(sketch, "E3587", {"start": v(-126.79, -6.42) * mm, "end": v(-126.61, -6.35) * mm});
            skLineSegment(sketch, "E3588", {"start": v(-126.61, -6.35) * mm, "end": v(-126.44, -6.27) * mm});
            skLineSegment(sketch, "E3589", {"start": v(-126.44, -6.27) * mm, "end": v(-126.27, -6.18) * mm});
            skLineSegment(sketch, "E3590", {"start": v(-126.27, -6.18) * mm, "end": v(-126.11, -6.08) * mm});
            skLineSegment(sketch, "E3591", {"start": v(-126.11, -6.08) * mm, "end": v(-125.96, -5.98) * mm});
            skLineSegment(sketch, "E3592", {"start": v(-125.96, -5.98) * mm, "end": v(-125.8, -5.86) * mm});
            skLineSegment(sketch, "E3593", {"start": v(-125.8, -5.86) * mm, "end": v(-125.66, -5.74) * mm});
            skLineSegment(sketch, "E3594", {"start": v(-125.66, -5.74) * mm, "end": v(-125.53, -5.61) * mm});
            skLineSegment(sketch, "E3595", {"start": v(-125.53, -5.61) * mm, "end": v(-125.4, -5.47) * mm});
            skLineSegment(sketch, "E3596", {"start": v(-125.4, -5.47) * mm, "end": v(-125.27, -5.33) * mm});
            skLineSegment(sketch, "E3597", {"start": v(-125.27, -5.33) * mm, "end": v(-125.16, -5.18) * mm});
            skLineSegment(sketch, "E3598", {"start": v(-125.16, -5.18) * mm, "end": v(-125.05, -5.02) * mm});
            skLineSegment(sketch, "E3599", {"start": v(-125.05, -5.02) * mm, "end": v(-124.95, -4.86) * mm});
            skLineSegment(sketch, "E3600", {"start": v(-124.95, -4.86) * mm, "end": v(-124.86, -4.7) * mm});
            skLineSegment(sketch, "E3601", {"start": v(-124.86, -4.7) * mm, "end": v(-124.78, -4.52) * mm});
            skLineSegment(sketch, "E3602", {"start": v(-124.78, -4.52) * mm, "end": v(-124.71, -4.35) * mm});
            skLineSegment(sketch, "E3603", {"start": v(-124.71, -4.35) * mm, "end": v(-124.65, -4.16) * mm});
            skLineSegment(sketch, "E3604", {"start": v(-124.65, -4.16) * mm, "end": v(-124.6, -3.98) * mm});
            skLineSegment(sketch, "E3605", {"start": v(-124.6, -3.98) * mm, "end": v(-124.55, -3.78) * mm});
            skLineSegment(sketch, "E3606", {"start": v(-124.55, -3.78) * mm, "end": v(-124.5, -3.58) * mm});
            skLineSegment(sketch, "E3607", {"start": v(-124.5, -3.58) * mm, "end": v(-124.48, -3.38) * mm});
            skLineSegment(sketch, "E3608", {"start": v(-124.48, -3.38) * mm, "end": v(-124.46, -3.17) * mm});
            skLineSegment(sketch, "E3609", {"start": v(-124.46, -3.17) * mm, "end": v(-124.44, -2.95) * mm});
            skLineSegment(sketch, "E3610", {"start": v(-124.44, -2.95) * mm, "end": v(-124.44, -2.74) * mm});
            skLineSegment(sketch, "E3611", {"start": v(-124.44, -2.74) * mm, "end": v(-124.44, -2.52) * mm});
            skLineSegment(sketch, "E3612", {"start": v(-124.44, -2.52) * mm, "end": v(-124.46, -2.31) * mm});
            skLineSegment(sketch, "E3613", {"start": v(-124.46, -2.31) * mm, "end": v(-124.48, -2.1) * mm});
            skLineSegment(sketch, "E3614", {"start": v(-124.48, -2.1) * mm, "end": v(-124.5, -1.9) * mm});
            skLineSegment(sketch, "E3615", {"start": v(-124.5, -1.9) * mm, "end": v(-124.55, -1.71) * mm});
            skLineSegment(sketch, "E3616", {"start": v(-124.55, -1.71) * mm, "end": v(-124.6, -1.52) * mm});
            skLineSegment(sketch, "E3617", {"start": v(-124.6, -1.52) * mm, "end": v(-124.65, -1.34) * mm});
            skLineSegment(sketch, "E3618", {"start": v(-124.65, -1.34) * mm, "end": v(-124.72, -1.16) * mm});
            skLineSegment(sketch, "E3619", {"start": v(-124.72, -1.16) * mm, "end": v(-124.8, -0.98) * mm});
            skLineSegment(sketch, "E3620", {"start": v(-124.8, -0.98) * mm, "end": v(-124.87, -0.8) * mm});
            skLineSegment(sketch, "E3621", {"start": v(-124.87, -0.8) * mm, "end": v(-124.97, -0.64) * mm});
            skLineSegment(sketch, "E3622", {"start": v(-124.97, -0.64) * mm, "end": v(-125.07, -0.48) * mm});
            skLineSegment(sketch, "E3623", {"start": v(-125.07, -0.48) * mm, "end": v(-125.18, -0.33) * mm});
            skLineSegment(sketch, "E3624", {"start": v(-125.18, -0.33) * mm, "end": v(-125.3, -0.17) * mm});
            skLineSegment(sketch, "E3625", {"start": v(-125.3, -0.17) * mm, "end": v(-125.42, -0.03) * mm});
            skLineSegment(sketch, "E3626", {"start": v(-125.42, -0.03) * mm, "end": v(-125.55, 0.11) * mm});
            skLineSegment(sketch, "E3627", {"start": v(-125.55, 0.11) * mm, "end": v(-125.7, 0.25) * mm});
            skLineSegment(sketch, "E3628", {"start": v(-125.7, 0.25) * mm, "end": v(-125.84, 0.37) * mm});
            skLineSegment(sketch, "E3629", {"start": v(-125.84, 0.37) * mm, "end": v(-126, 0.5) * mm});
            skLineSegment(sketch, "E3630", {"start": v(-126, 0.5) * mm, "end": v(-126.15, 0.6) * mm});
            skLineSegment(sketch, "E3631", {"start": v(-126.15, 0.6) * mm, "end": v(-126.3, 0.7) * mm});
            skLineSegment(sketch, "E3632", {"start": v(-126.3, 0.7) * mm, "end": v(-126.48, 0.8) * mm});
            skLineSegment(sketch, "E3633", {"start": v(-126.48, 0.8) * mm, "end": v(-126.65, 0.87) * mm});
            skLineSegment(sketch, "E3634", {"start": v(-126.65, 0.87) * mm, "end": v(-126.82, 0.95) * mm});
            skLineSegment(sketch, "E3635", {"start": v(-126.82, 0.95) * mm, "end": v(-127, 1.01) * mm});
            skLineSegment(sketch, "E3636", {"start": v(-127, 1.01) * mm, "end": v(-127.19, 1.07) * mm});
            skLineSegment(sketch, "E3637", {"start": v(-127.19, 1.07) * mm, "end": v(-127.38, 1.12) * mm});
            skLineSegment(sketch, "E3638", {"start": v(-127.38, 1.12) * mm, "end": v(-127.57, 1.16) * mm});
            skLineSegment(sketch, "E3639", {"start": v(-127.57, 1.16) * mm, "end": v(-127.77, 1.19) * mm});
            skLineSegment(sketch, "E3640", {"start": v(-127.77, 1.19) * mm, "end": v(-127.98, 1.21) * mm});
            skLineSegment(sketch, "E3641", {"start": v(-127.98, 1.21) * mm, "end": v(-128.19, 1.22) * mm});
            skLineSegment(sketch, "E3642", {"start": v(-128.19, 1.22) * mm, "end": v(-128.4, 1.23) * mm});
            skLineSegment(sketch, "E3643", {"start": v(-128.4, 1.23) * mm, "end": v(-138.3, 1.23) * mm});
            skLineSegment(sketch, "E3644", {"start": v(-138.3, 1.23) * mm, "end": v(-138.49, 1.23) * mm});
            skLineSegment(sketch, "E3645", {"start": v(-138.49, 1.23) * mm, "end": v(-138.67, 1.24) * mm});
            skLineSegment(sketch, "E3646", {"start": v(-138.67, 1.24) * mm, "end": v(-138.85, 1.26) * mm});
            skLineSegment(sketch, "E3647", {"start": v(-138.85, 1.26) * mm, "end": v(-139.03, 1.29) * mm});
            skLineSegment(sketch, "E3648", {"start": v(-139.03, 1.29) * mm, "end": v(-139.2, 1.32) * mm});
            skLineSegment(sketch, "E3649", {"start": v(-139.2, 1.32) * mm, "end": v(-139.37, 1.36) * mm});
            skLineSegment(sketch, "E3650", {"start": v(-139.37, 1.36) * mm, "end": v(-139.53, 1.41) * mm});
            skLineSegment(sketch, "E3651", {"start": v(-139.53, 1.41) * mm, "end": v(-139.7, 1.47) * mm});
            skLineSegment(sketch, "E3652", {"start": v(-139.7, 1.47) * mm, "end": v(-139.85, 1.53) * mm});
            skLineSegment(sketch, "E3653", {"start": v(-139.85, 1.53) * mm, "end": v(-140, 1.6) * mm});
            skLineSegment(sketch, "E3654", {"start": v(-140, 1.6) * mm, "end": v(-140.14, 1.68) * mm});
            skLineSegment(sketch, "E3655", {"start": v(-140.14, 1.68) * mm, "end": v(-140.28, 1.76) * mm});
            skLineSegment(sketch, "E3656", {"start": v(-140.28, 1.76) * mm, "end": v(-140.42, 1.86) * mm});
            skLineSegment(sketch, "E3657", {"start": v(-140.42, 1.86) * mm, "end": v(-140.55, 1.96) * mm});
            skLineSegment(sketch, "E3658", {"start": v(-140.55, 1.96) * mm, "end": v(-140.67, 2.06) * mm});
            skLineSegment(sketch, "E3659", {"start": v(-140.67, 2.06) * mm, "end": v(-140.8, 2.18) * mm});
            skLineSegment(sketch, "E3660", {"start": v(-140.8, 2.18) * mm, "end": v(-140.9, 2.3) * mm});
            skLineSegment(sketch, "E3661", {"start": v(-140.9, 2.3) * mm, "end": v(-141.01, 2.42) * mm});
            skLineSegment(sketch, "E3662", {"start": v(-141.01, 2.42) * mm, "end": v(-141.11, 2.55) * mm});
            skLineSegment(sketch, "E3663", {"start": v(-141.11, 2.55) * mm, "end": v(-141.2, 2.69) * mm});
            skLineSegment(sketch, "E3664", {"start": v(-141.2, 2.69) * mm, "end": v(-141.3, 2.83) * mm});
            skLineSegment(sketch, "E3665", {"start": v(-141.3, 2.83) * mm, "end": v(-141.37, 2.97) * mm});
            skLineSegment(sketch, "E3666", {"start": v(-141.37, 2.97) * mm, "end": v(-141.44, 3.12) * mm});
            skLineSegment(sketch, "E3667", {"start": v(-141.44, 3.12) * mm, "end": v(-141.5, 3.28) * mm});
            skLineSegment(sketch, "E3668", {"start": v(-141.5, 3.28) * mm, "end": v(-141.56, 3.44) * mm});
            skLineSegment(sketch, "E3669", {"start": v(-141.56, 3.44) * mm, "end": v(-141.6, 3.6) * mm});
            skLineSegment(sketch, "E3670", {"start": v(-141.6, 3.6) * mm, "end": v(-141.65, 3.77) * mm});
            skLineSegment(sketch, "E3671", {"start": v(-141.65, 3.77) * mm, "end": v(-141.68, 3.94) * mm});
            skLineSegment(sketch, "E3672", {"start": v(-141.68, 3.94) * mm, "end": v(-141.7, 4.12) * mm});
            skLineSegment(sketch, "E3673", {"start": v(-141.7, 4.12) * mm, "end": v(-141.73, 4.3) * mm});
            skLineSegment(sketch, "E3674", {"start": v(-141.73, 4.3) * mm, "end": v(-141.74, 4.48) * mm});
            skLineSegment(sketch, "E3675", {"start": v(-141.74, 4.48) * mm, "end": v(-141.74, 4.67) * mm});
            skLineSegment(sketch, "E3676", {"start": v(-141.74, 4.67) * mm, "end": v(-141.74, 4.86) * mm});
            skLineSegment(sketch, "E3677", {"start": v(-141.74, 4.86) * mm, "end": v(-141.73, 5.05) * mm});
            skLineSegment(sketch, "E3678", {"start": v(-141.73, 5.05) * mm, "end": v(-141.7, 5.23) * mm});
            skLineSegment(sketch, "E3679", {"start": v(-141.7, 5.23) * mm, "end": v(-141.68, 5.4) * mm});
            skLineSegment(sketch, "E3680", {"start": v(-141.68, 5.4) * mm, "end": v(-141.65, 5.58) * mm});
            skLineSegment(sketch, "E3681", {"start": v(-141.65, 5.58) * mm, "end": v(-141.6, 5.75) * mm});
            skLineSegment(sketch, "E3682", {"start": v(-141.6, 5.75) * mm, "end": v(-141.56, 5.91) * mm});
            skLineSegment(sketch, "E3683", {"start": v(-141.56, 5.91) * mm, "end": v(-141.5, 6.07) * mm});
            skLineSegment(sketch, "E3684", {"start": v(-141.5, 6.07) * mm, "end": v(-141.44, 6.22) * mm});
            skLineSegment(sketch, "E3685", {"start": v(-141.44, 6.22) * mm, "end": v(-141.37, 6.37) * mm});
            skLineSegment(sketch, "E3686", {"start": v(-141.37, 6.37) * mm, "end": v(-141.3, 6.52) * mm});
            skLineSegment(sketch, "E3687", {"start": v(-141.3, 6.52) * mm, "end": v(-141.2, 6.66) * mm});
            skLineSegment(sketch, "E3688", {"start": v(-141.2, 6.66) * mm, "end": v(-141.11, 6.8) * mm});
            skLineSegment(sketch, "E3689", {"start": v(-141.11, 6.8) * mm, "end": v(-141.01, 6.92) * mm});
            skLineSegment(sketch, "E3690", {"start": v(-141.01, 6.92) * mm, "end": v(-140.9, 7.05) * mm});
            skLineSegment(sketch, "E3691", {"start": v(-140.9, 7.05) * mm, "end": v(-140.8, 7.17) * mm});
            skLineSegment(sketch, "E3692", {"start": v(-140.8, 7.17) * mm, "end": v(-140.67, 7.28) * mm});
            skLineSegment(sketch, "E3693", {"start": v(-140.67, 7.28) * mm, "end": v(-140.55, 7.4) * mm});
            skLineSegment(sketch, "E3694", {"start": v(-140.55, 7.4) * mm, "end": v(-140.42, 7.5) * mm});
            skLineSegment(sketch, "E3695", {"start": v(-140.42, 7.5) * mm, "end": v(-140.28, 7.58) * mm});
            skLineSegment(sketch, "E3696", {"start": v(-140.28, 7.58) * mm, "end": v(-140.14, 7.67) * mm});
            skLineSegment(sketch, "E3697", {"start": v(-140.14, 7.67) * mm, "end": v(-140, 7.75) * mm});
            skLineSegment(sketch, "E3698", {"start": v(-140, 7.75) * mm, "end": v(-139.85, 7.82) * mm});
            skLineSegment(sketch, "E3699", {"start": v(-139.85, 7.82) * mm, "end": v(-139.7, 7.88) * mm});
            skLineSegment(sketch, "E3700", {"start": v(-139.7, 7.88) * mm, "end": v(-139.53, 7.94) * mm});
            skLineSegment(sketch, "E3701", {"start": v(-139.53, 7.94) * mm, "end": v(-139.37, 7.98) * mm});
            skLineSegment(sketch, "E3702", {"start": v(-139.37, 7.98) * mm, "end": v(-139.2, 8.03) * mm});
            skLineSegment(sketch, "E3703", {"start": v(-139.2, 8.03) * mm, "end": v(-139.03, 8.06) * mm});
            skLineSegment(sketch, "E3704", {"start": v(-139.03, 8.06) * mm, "end": v(-138.85, 8.09) * mm});
            skLineSegment(sketch, "E3705", {"start": v(-138.85, 8.09) * mm, "end": v(-138.67, 8.1) * mm});
            skLineSegment(sketch, "E3706", {"start": v(-138.67, 8.1) * mm, "end": v(-138.49, 8.11) * mm});
            skLineSegment(sketch, "E3707", {"start": v(-138.49, 8.11) * mm, "end": v(-138.3, 8.12) * mm});
            skLineSegment(sketch, "E3708", {"start": v(-138.3, 8.12) * mm, "end": v(-123.48, 8.12) * mm});
            skLineSegment(sketch, "E3709", {"start": v(-123.48, 8.12) * mm, "end": v(-123.27, 8.12) * mm});
            skLineSegment(sketch, "E3710", {"start": v(-123.27, 8.12) * mm, "end": v(-123.06, 8.14) * mm});
            skLineSegment(sketch, "E3711", {"start": v(-123.06, 8.14) * mm, "end": v(-122.85, 8.16) * mm});
            skLineSegment(sketch, "E3712", {"start": v(-122.85, 8.16) * mm, "end": v(-122.65, 8.19) * mm});
            skLineSegment(sketch, "E3713", {"start": v(-122.65, 8.19) * mm, "end": v(-122.46, 8.23) * mm});
            skLineSegment(sketch, "E3714", {"start": v(-122.46, 8.23) * mm, "end": v(-122.26, 8.28) * mm});
            skLineSegment(sketch, "E3715", {"start": v(-122.26, 8.28) * mm, "end": v(-122.08, 8.33) * mm});
            skLineSegment(sketch, "E3716", {"start": v(-122.08, 8.33) * mm, "end": v(-121.9, 8.4) * mm});
            skLineSegment(sketch, "E3717", {"start": v(-121.9, 8.4) * mm, "end": v(-121.72, 8.47) * mm});
            skLineSegment(sketch, "E3718", {"start": v(-121.72, 8.47) * mm, "end": v(-121.54, 8.56) * mm});
            skLineSegment(sketch, "E3719", {"start": v(-121.54, 8.56) * mm, "end": v(-121.38, 8.65) * mm});
            skLineSegment(sketch, "E3720", {"start": v(-121.38, 8.65) * mm, "end": v(-121.21, 8.75) * mm});
            skLineSegment(sketch, "E3721", {"start": v(-121.21, 8.75) * mm, "end": v(-121.05, 8.85) * mm});
            skLineSegment(sketch, "E3722", {"start": v(-121.05, 8.85) * mm, "end": v(-120.9, 8.97) * mm});
            skLineSegment(sketch, "E3723", {"start": v(-120.9, 8.97) * mm, "end": v(-120.75, 9.1) * mm});
            skLineSegment(sketch, "E3724", {"start": v(-120.75, 9.1) * mm, "end": v(-120.6, 9.23) * mm});
            skLineSegment(sketch, "E3725", {"start": v(-120.6, 9.23) * mm, "end": v(-120.47, 9.37) * mm});
            skLineSegment(sketch, "E3726", {"start": v(-120.47, 9.37) * mm, "end": v(-120.34, 9.52) * mm});
            skLineSegment(sketch, "E3727", {"start": v(-120.34, 9.52) * mm, "end": v(-120.22, 9.67) * mm});
            skLineSegment(sketch, "E3728", {"start": v(-120.22, 9.67) * mm, "end": v(-120.1, 9.83) * mm});
            skLineSegment(sketch, "E3729", {"start": v(-120.1, 9.83) * mm, "end": v(-120, 9.99) * mm});
            skLineSegment(sketch, "E3730", {"start": v(-120, 9.99) * mm, "end": v(-119.91, 10.15) * mm});
            skLineSegment(sketch, "E3731", {"start": v(-119.91, 10.15) * mm, "end": v(-119.83, 10.33) * mm});
            skLineSegment(sketch, "E3732", {"start": v(-119.83, 10.33) * mm, "end": v(-119.75, 10.5) * mm});
            skLineSegment(sketch, "E3733", {"start": v(-119.75, 10.5) * mm, "end": v(-119.68, 10.68) * mm});
            skLineSegment(sketch, "E3734", {"start": v(-119.68, 10.68) * mm, "end": v(-119.63, 10.87) * mm});
            skLineSegment(sketch, "E3735", {"start": v(-119.63, 10.87) * mm, "end": v(-119.58, 11.06) * mm});
            skLineSegment(sketch, "E3736", {"start": v(-119.58, 11.06) * mm, "end": v(-119.54, 11.25) * mm});
            skLineSegment(sketch, "E3737", {"start": v(-119.54, 11.25) * mm, "end": v(-119.5, 11.45) * mm});
            skLineSegment(sketch, "E3738", {"start": v(-119.5, 11.45) * mm, "end": v(-119.48, 11.66) * mm});
            skLineSegment(sketch, "E3739", {"start": v(-119.48, 11.66) * mm, "end": v(-119.47, 11.87) * mm});
            skLineSegment(sketch, "E3740", {"start": v(-119.47, 11.87) * mm, "end": v(-119.46, 12.08) * mm});
            skLineSegment(sketch, "E3741", {"start": v(-119.46, 12.08) * mm, "end": v(-119.47, 12.3) * mm});
            skLineSegment(sketch, "E3742", {"start": v(-119.47, 12.3) * mm, "end": v(-119.48, 12.5) * mm});
            skLineSegment(sketch, "E3743", {"start": v(-119.48, 12.5) * mm, "end": v(-119.5, 12.7) * mm});
            skLineSegment(sketch, "E3744", {"start": v(-119.5, 12.7) * mm, "end": v(-119.54, 12.9) * mm});
            skLineSegment(sketch, "E3745", {"start": v(-119.54, 12.9) * mm, "end": v(-119.58, 13.1) * mm});
            skLineSegment(sketch, "E3746", {"start": v(-119.58, 13.1) * mm, "end": v(-119.63, 13.3) * mm});
            skLineSegment(sketch, "E3747", {"start": v(-119.63, 13.3) * mm, "end": v(-119.68, 13.48) * mm});
            skLineSegment(sketch, "E3748", {"start": v(-119.68, 13.48) * mm, "end": v(-119.75, 13.66) * mm});
            skLineSegment(sketch, "E3749", {"start": v(-119.75, 13.66) * mm, "end": v(-119.83, 13.84) * mm});
            skLineSegment(sketch, "E3750", {"start": v(-119.83, 13.84) * mm, "end": v(-119.91, 14) * mm});
            skLineSegment(sketch, "E3751", {"start": v(-119.91, 14) * mm, "end": v(-120, 14.17) * mm});
            skLineSegment(sketch, "E3752", {"start": v(-120, 14.17) * mm, "end": v(-120.1, 14.34) * mm});
            skLineSegment(sketch, "E3753", {"start": v(-120.1, 14.34) * mm, "end": v(-120.22, 14.5) * mm});
            skLineSegment(sketch, "E3754", {"start": v(-120.22, 14.5) * mm, "end": v(-120.34, 14.64) * mm});
            skLineSegment(sketch, "E3755", {"start": v(-120.34, 14.64) * mm, "end": v(-120.47, 14.79) * mm});
            skLineSegment(sketch, "E3756", {"start": v(-120.47, 14.79) * mm, "end": v(-120.6, 14.93) * mm});
            skLineSegment(sketch, "E3757", {"start": v(-120.6, 14.93) * mm, "end": v(-120.75, 15.07) * mm});
            skLineSegment(sketch, "E3758", {"start": v(-120.75, 15.07) * mm, "end": v(-120.9, 15.2) * mm});
            skLineSegment(sketch, "E3759", {"start": v(-120.9, 15.2) * mm, "end": v(-121.05, 15.3) * mm});
            skLineSegment(sketch, "E3760", {"start": v(-121.05, 15.3) * mm, "end": v(-121.21, 15.42) * mm});
            skLineSegment(sketch, "E3761", {"start": v(-121.21, 15.42) * mm, "end": v(-121.38, 15.52) * mm});
            skLineSegment(sketch, "E3762", {"start": v(-121.38, 15.52) * mm, "end": v(-121.54, 15.6) * mm});
            skLineSegment(sketch, "E3763", {"start": v(-121.54, 15.6) * mm, "end": v(-121.72, 15.7) * mm});
            skLineSegment(sketch, "E3764", {"start": v(-121.72, 15.7) * mm, "end": v(-121.9, 15.76) * mm});
            skLineSegment(sketch, "E3765", {"start": v(-121.9, 15.76) * mm, "end": v(-122.08, 15.83) * mm});
            skLineSegment(sketch, "E3766", {"start": v(-122.08, 15.83) * mm, "end": v(-122.26, 15.89) * mm});
            skLineSegment(sketch, "E3767", {"start": v(-122.26, 15.89) * mm, "end": v(-122.46, 15.94) * mm});
            skLineSegment(sketch, "E3768", {"start": v(-122.46, 15.94) * mm, "end": v(-122.65, 15.97) * mm});
            skLineSegment(sketch, "E3769", {"start": v(-122.65, 15.97) * mm, "end": v(-122.85, 16) * mm});
            skLineSegment(sketch, "E3770", {"start": v(-122.85, 16) * mm, "end": v(-123.06, 16.03) * mm});
            skLineSegment(sketch, "E3771", {"start": v(-123.06, 16.03) * mm, "end": v(-123.27, 16.04) * mm});
            skLineSegment(sketch, "E3772", {"start": v(-123.27, 16.04) * mm, "end": v(-123.48, 16.04) * mm});
            skLineSegment(sketch, "E3773", {"start": v(-123.48, 16.04) * mm, "end": v(-146.51, 16.04) * mm});
            skLineSegment(sketch, "E3774", {"start": v(-146.51, 16.04) * mm, "end": v(-146.83, 16.03) * mm});
            skLineSegment(sketch, "E3775", {"start": v(-146.83, 16.03) * mm, "end": v(-147.15, 15.98) * mm});
            skLineSegment(sketch, "E3776", {"start": v(-147.15, 15.98) * mm, "end": v(-147.45, 15.9) * mm});
            skLineSegment(sketch, "E3777", {"start": v(-147.45, 15.9) * mm, "end": v(-147.74, 15.8) * mm});
            skLineSegment(sketch, "E3778", {"start": v(-147.74, 15.8) * mm, "end": v(-148.02, 15.66) * mm});
            skLineSegment(sketch, "E3779", {"start": v(-148.02, 15.66) * mm, "end": v(-148.28, 15.5) * mm});
            skLineSegment(sketch, "E3780", {"start": v(-148.28, 15.5) * mm, "end": v(-148.52, 15.32) * mm});
            skLineSegment(sketch, "E3781", {"start": v(-148.52, 15.32) * mm, "end": v(-148.74, 15.12) * mm});
            skLineSegment(sketch, "E3782", {"start": v(-148.74, 15.12) * mm, "end": v(-148.95, 14.9) * mm});
            skLineSegment(sketch, "E3783", {"start": v(-148.95, 14.9) * mm, "end": v(-149.13, 14.65) * mm});
            skLineSegment(sketch, "E3784", {"start": v(-149.13, 14.65) * mm, "end": v(-149.29, 14.4) * mm});
            skLineSegment(sketch, "E3785", {"start": v(-149.29, 14.4) * mm, "end": v(-149.42, 14.12) * mm});
            skLineSegment(sketch, "E3786", {"start": v(-149.42, 14.12) * mm, "end": v(-149.53, 13.83) * mm});
            skLineSegment(sketch, "E3787", {"start": v(-149.53, 13.83) * mm, "end": v(-149.6, 13.52) * mm});
            skLineSegment(sketch, "E3788", {"start": v(-149.6, 13.52) * mm, "end": v(-149.65, 13.21) * mm});
            skLineSegment(sketch, "E3789", {"start": v(-149.65, 13.21) * mm, "end": v(-149.67, 12.89) * mm});
            skLineSegment(sketch, "E3790", {"start": v(-149.67, 12.89) * mm, "end": v(-149.67, -22.53) * mm});
            skLineSegment(sketch, "E3791", {"start": v(-149.67, -22.53) * mm, "end": v(-149.67, -22.64) * mm});
            skLineSegment(sketch, "E3792", {"start": v(-149.67, -22.64) * mm, "end": v(-149.68, -22.74) * mm});
            skLineSegment(sketch, "E3793", {"start": v(-149.68, -22.74) * mm, "end": v(-149.7, -22.84) * mm});
            skLineSegment(sketch, "E3794", {"start": v(-149.7, -22.84) * mm, "end": v(-149.73, -22.93) * mm});
            skLineSegment(sketch, "E3795", {"start": v(-149.73, -22.93) * mm, "end": v(-149.77, -23.01) * mm});
            skLineSegment(sketch, "E3796", {"start": v(-149.77, -23.01) * mm, "end": v(-149.8, -23.09) * mm});
            skLineSegment(sketch, "E3797", {"start": v(-149.8, -23.09) * mm, "end": v(-149.86, -23.16) * mm});
            skLineSegment(sketch, "E3798", {"start": v(-149.86, -23.16) * mm, "end": v(-149.92, -23.22) * mm});
            skLineSegment(sketch, "E3799", {"start": v(-149.92, -23.22) * mm, "end": v(-149.99, -23.28) * mm});
            skLineSegment(sketch, "E3800", {"start": v(-149.99, -23.28) * mm, "end": v(-150.06, -23.33) * mm});
            skLineSegment(sketch, "E3801", {"start": v(-150.06, -23.33) * mm, "end": v(-150.14, -23.37) * mm});
            skLineSegment(sketch, "E3802", {"start": v(-150.14, -23.37) * mm, "end": v(-150.23, -23.4) * mm});
            skLineSegment(sketch, "E3803", {"start": v(-150.23, -23.4) * mm, "end": v(-150.33, -23.44) * mm});
            skLineSegment(sketch, "E3804", {"start": v(-150.33, -23.44) * mm, "end": v(-150.44, -23.46) * mm});
            skLineSegment(sketch, "E3805", {"start": v(-150.44, -23.46) * mm, "end": v(-150.56, -23.47) * mm});
            skLineSegment(sketch, "E3806", {"start": v(-150.56, -23.47) * mm, "end": v(-150.68, -23.48) * mm});
            skLineSegment(sketch, "E3807", {"start": v(-150.68, -23.48) * mm, "end": v(-153.84, -23.48) * mm});
            skLineSegment(sketch, "E3808", {"start": v(-153.84, -23.48) * mm, "end": v(-153.9, -23.48) * mm});
            skLineSegment(sketch, "E3809", {"start": v(-153.9, -23.48) * mm, "end": v(-153.97, -23.47) * mm});
            skLineSegment(sketch, "E3810", {"start": v(-153.97, -23.47) * mm, "end": v(-154.03, -23.45) * mm});
            skLineSegment(sketch, "E3811", {"start": v(-154.03, -23.45) * mm, "end": v(-154.1, -23.43) * mm});
            skLineSegment(sketch, "E3812", {"start": v(-154.1, -23.43) * mm, "end": v(-154.15, -23.4) * mm});
            skLineSegment(sketch, "E3813", {"start": v(-154.15, -23.4) * mm, "end": v(-154.2, -23.37) * mm});
            skLineSegment(sketch, "E3814", {"start": v(-154.2, -23.37) * mm, "end": v(-154.26, -23.33) * mm});
            skLineSegment(sketch, "E3815", {"start": v(-154.26, -23.33) * mm, "end": v(-154.3, -23.3) * mm});
            skLineSegment(sketch, "E3816", {"start": v(-154.3, -23.3) * mm, "end": v(-154.34, -23.25) * mm});
            skLineSegment(sketch, "E3817", {"start": v(-154.34, -23.25) * mm, "end": v(-154.38, -23.2) * mm});
            skLineSegment(sketch, "E3818", {"start": v(-154.38, -23.2) * mm, "end": v(-154.42, -23.14) * mm});
            skLineSegment(sketch, "E3819", {"start": v(-154.42, -23.14) * mm, "end": v(-154.44, -23.08) * mm});
            skLineSegment(sketch, "E3820", {"start": v(-154.44, -23.08) * mm, "end": v(-154.46, -23.02) * mm});
            skLineSegment(sketch, "E3821", {"start": v(-154.46, -23.02) * mm, "end": v(-154.48, -22.96) * mm});
            skLineSegment(sketch, "E3822", {"start": v(-154.48, -22.96) * mm, "end": v(-154.5, -22.9) * mm});
            skLineSegment(sketch, "E3823", {"start": v(-154.5, -22.9) * mm, "end": v(-154.5, -22.83) * mm});
            skLineSegment(sketch, "E3824", {"start": v(-154.5, -22.83) * mm, "end": v(-154.5, 12.07) * mm});
            skLineSegment(sketch, "E3825", {"start": v(-154.5, 12.07) * mm, "end": v(-154.5, 12.3) * mm});
            skLineSegment(sketch, "E3826", {"start": v(-154.5, 12.3) * mm, "end": v(-154.51, 12.5) * mm});
            skLineSegment(sketch, "E3827", {"start": v(-154.51, 12.5) * mm, "end": v(-154.53, 12.72) * mm});
            skLineSegment(sketch, "E3828", {"start": v(-154.53, 12.72) * mm, "end": v(-154.56, 12.92) * mm});
            skLineSegment(sketch, "E3829", {"start": v(-154.56, 12.92) * mm, "end": v(-154.6, 13.12) * mm});
            skLineSegment(sketch, "E3830", {"start": v(-154.6, 13.12) * mm, "end": v(-154.65, 13.31) * mm});
            skLineSegment(sketch, "E3831", {"start": v(-154.65, 13.31) * mm, "end": v(-154.7, 13.5) * mm});
            skLineSegment(sketch, "E3832", {"start": v(-154.7, 13.5) * mm, "end": v(-154.77, 13.69) * mm});
            skLineSegment(sketch, "E3833", {"start": v(-154.77, 13.69) * mm, "end": v(-154.84, 13.86) * mm});
            skLineSegment(sketch, "E3834", {"start": v(-154.84, 13.86) * mm, "end": v(-154.92, 14.04) * mm});
            skLineSegment(sketch, "E3835", {"start": v(-154.92, 14.04) * mm, "end": v(-155, 14.2) * mm});
            skLineSegment(sketch, "E3836", {"start": v(-155, 14.2) * mm, "end": v(-155.1, 14.36) * mm});
            skLineSegment(sketch, "E3837", {"start": v(-155.1, 14.36) * mm, "end": v(-155.2, 14.52) * mm});
            skLineSegment(sketch, "E3838", {"start": v(-155.2, 14.52) * mm, "end": v(-155.32, 14.67) * mm});
            skLineSegment(sketch, "E3839", {"start": v(-155.32, 14.67) * mm, "end": v(-155.44, 14.81) * mm});
            skLineSegment(sketch, "E3840", {"start": v(-155.44, 14.81) * mm, "end": v(-155.57, 14.95) * mm});
            skLineSegment(sketch, "E3841", {"start": v(-155.57, 14.95) * mm, "end": v(-155.71, 15.08) * mm});
            skLineSegment(sketch, "E3842", {"start": v(-155.71, 15.08) * mm, "end": v(-155.85, 15.2) * mm});
            skLineSegment(sketch, "E3843", {"start": v(-155.85, 15.2) * mm, "end": v(-156, 15.32) * mm});
            skLineSegment(sketch, "E3844", {"start": v(-156, 15.32) * mm, "end": v(-156.16, 15.43) * mm});
            skLineSegment(sketch, "E3845", {"start": v(-156.16, 15.43) * mm, "end": v(-156.32, 15.53) * mm});
            skLineSegment(sketch, "E3846", {"start": v(-156.32, 15.53) * mm, "end": v(-156.48, 15.62) * mm});
            skLineSegment(sketch, "E3847", {"start": v(-156.48, 15.62) * mm, "end": v(-156.65, 15.7) * mm});
            skLineSegment(sketch, "E3848", {"start": v(-156.65, 15.7) * mm, "end": v(-156.83, 15.77) * mm});
            skLineSegment(sketch, "E3849", {"start": v(-156.83, 15.77) * mm, "end": v(-157.01, 15.83) * mm});
            skLineSegment(sketch, "E3850", {"start": v(-157.01, 15.83) * mm, "end": v(-157.2, 15.9) * mm});
            skLineSegment(sketch, "E3851", {"start": v(-157.2, 15.9) * mm, "end": v(-157.4, 15.94) * mm});
            skLineSegment(sketch, "E3852", {"start": v(-157.4, 15.94) * mm, "end": v(-157.59, 15.98) * mm});
            skLineSegment(sketch, "E3853", {"start": v(-157.59, 15.98) * mm, "end": v(-157.8, 16) * mm});
            skLineSegment(sketch, "E3854", {"start": v(-157.8, 16) * mm, "end": v(-158, 16.03) * mm});
            skLineSegment(sketch, "E3855", {"start": v(-158, 16.03) * mm, "end": v(-158.21, 16.04) * mm});
            skLineSegment(sketch, "E3856", {"start": v(-158.21, 16.04) * mm, "end": v(-158.43, 16.04) * mm});
            skLineSegment(sketch, "E3857", {"start": v(-158.43, 16.04) * mm, "end": v(-158.64, 16.04) * mm});
            skLineSegment(sketch, "E3858", {"start": v(-158.64, 16.04) * mm, "end": v(-158.85, 16.03) * mm});
            skLineSegment(sketch, "E3859", {"start": v(-158.85, 16.03) * mm, "end": v(-159.05, 16) * mm});
            skLineSegment(sketch, "E3860", {"start": v(-159.05, 16) * mm, "end": v(-159.25, 15.97) * mm});
            skLineSegment(sketch, "E3861", {"start": v(-159.25, 15.97) * mm, "end": v(-159.45, 15.93) * mm});
            skLineSegment(sketch, "E3862", {"start": v(-159.45, 15.93) * mm, "end": v(-159.64, 15.89) * mm});
            skLineSegment(sketch, "E3863", {"start": v(-159.64, 15.89) * mm, "end": v(-159.82, 15.83) * mm});
            skLineSegment(sketch, "E3864", {"start": v(-159.82, 15.83) * mm, "end": v(-160, 15.76) * mm});
            skLineSegment(sketch, "E3865", {"start": v(-160, 15.76) * mm, "end": v(-160.17, 15.69) * mm});
            skLineSegment(sketch, "E3866", {"start": v(-160.17, 15.69) * mm, "end": v(-160.34, 15.6) * mm});
            skLineSegment(sketch, "E3867", {"start": v(-160.34, 15.6) * mm, "end": v(-160.5, 15.51) * mm});
            skLineSegment(sketch, "E3868", {"start": v(-160.5, 15.51) * mm, "end": v(-160.67, 15.41) * mm});
            skLineSegment(sketch, "E3869", {"start": v(-160.67, 15.41) * mm, "end": v(-160.83, 15.3) * mm});
            skLineSegment(sketch, "E3870", {"start": v(-160.83, 15.3) * mm, "end": v(-160.98, 15.19) * mm});
            skLineSegment(sketch, "E3871", {"start": v(-160.98, 15.19) * mm, "end": v(-161.12, 15.06) * mm});
            skLineSegment(sketch, "E3872", {"start": v(-161.12, 15.06) * mm, "end": v(-161.26, 14.93) * mm});
            skLineSegment(sketch, "E3873", {"start": v(-161.26, 14.93) * mm, "end": v(-161.4, 14.79) * mm});
            skLineSegment(sketch, "E3874", {"start": v(-161.4, 14.79) * mm, "end": v(-161.52, 14.64) * mm});
            skLineSegment(sketch, "E3875", {"start": v(-161.52, 14.64) * mm, "end": v(-161.64, 14.49) * mm});
            skLineSegment(sketch, "E3876", {"start": v(-161.64, 14.49) * mm, "end": v(-161.74, 14.33) * mm});
            skLineSegment(sketch, "E3877", {"start": v(-161.74, 14.33) * mm, "end": v(-161.84, 14.17) * mm});
            skLineSegment(sketch, "E3878", {"start": v(-161.84, 14.17) * mm, "end": v(-161.93, 14) * mm});
            skLineSegment(sketch, "E3879", {"start": v(-161.93, 14) * mm, "end": v(-162.02, 13.83) * mm});
            skLineSegment(sketch, "E3880", {"start": v(-162.02, 13.83) * mm, "end": v(-162.09, 13.65) * mm});
            skLineSegment(sketch, "E3881", {"start": v(-162.09, 13.65) * mm, "end": v(-162.15, 13.47) * mm});
            skLineSegment(sketch, "E3882", {"start": v(-162.15, 13.47) * mm, "end": v(-162.21, 13.29) * mm});
            skLineSegment(sketch, "E3883", {"start": v(-162.21, 13.29) * mm, "end": v(-162.26, 13.1) * mm});
            skLineSegment(sketch, "E3884", {"start": v(-162.26, 13.1) * mm, "end": v(-162.3, 12.9) * mm});
            skLineSegment(sketch, "E3885", {"start": v(-162.3, 12.9) * mm, "end": v(-162.33, 12.7) * mm});
            skLineSegment(sketch, "E3886", {"start": v(-162.33, 12.7) * mm, "end": v(-162.35, 12.5) * mm});
            skLineSegment(sketch, "E3887", {"start": v(-162.35, 12.5) * mm, "end": v(-162.36, 12.28) * mm});
            skLineSegment(sketch, "E3888", {"start": v(-162.36, 12.28) * mm, "end": v(-162.37, 12.07) * mm});
            skLineSegment(sketch, "E3889", {"start": v(-162.37, 12.07) * mm, "end": v(-162.37, -18.54) * mm});
            skLineSegment(sketch, "E3890", {"start": v(-162.37, -18.54) * mm, "end": v(-162.37, -18.54) * mm});
            skLineSegment(sketch, "E3891", {"start": v(-162.37, -18.54) * mm, "end": v(-162.37, -18.55) * mm});
            skLineSegment(sketch, "E3892", {"start": v(-162.37, -18.55) * mm, "end": v(-162.37, -18.55) * mm});
            skLineSegment(sketch, "E3893", {"start": v(-162.37, -18.55) * mm, "end": v(-162.37, -18.56) * mm});
            skLineSegment(sketch, "E3894", {"start": v(-162.37, -18.56) * mm, "end": v(-162.37, -18.56) * mm});
            skLineSegment(sketch, "E3895", {"start": v(-162.37, -18.56) * mm, "end": v(-162.38, -18.56) * mm});
            skLineSegment(sketch, "E3896", {"start": v(-162.38, -18.56) * mm, "end": v(-162.38, -18.56) * mm});
            skLineSegment(sketch, "E3897", {"start": v(-162.38, -18.56) * mm, "end": v(-162.39, -18.56) * mm});
            skLineSegment(sketch, "E3898", {"start": v(-162.39, -18.56) * mm, "end": v(-162.39, -18.56) * mm});
            skLineSegment(sketch, "E3899", {"start": v(-162.39, -18.56) * mm, "end": v(-162.4, -18.56) * mm});
            skLineSegment(sketch, "E3900", {"start": v(-162.4, -18.56) * mm, "end": v(-162.4, -18.56) * mm});
            skLineSegment(sketch, "E3901", {"start": v(-162.4, -18.56) * mm, "end": v(-162.41, -18.56) * mm});
            skLineSegment(sketch, "E3902", {"start": v(-162.41, -18.56) * mm, "end": v(-162.41, -18.56) * mm});
            skLineSegment(sketch, "E3903", {"start": v(-162.41, -18.56) * mm, "end": v(-162.42, -18.56) * mm});
            skLineSegment(sketch, "E3904", {"start": v(-162.42, -18.56) * mm, "end": v(-162.42, -18.56) * mm});
            skLineSegment(sketch, "E3905", {"start": v(-162.42, -18.56) * mm, "end": v(-162.42, -18.55) * mm});
            skLineSegment(sketch, "E3906", {"start": v(-162.42, -18.55) * mm, "end": v(-179.18, 14.87) * mm});
            skLineSegment(sketch, "E3907", {"start": v(-179.18, 14.87) * mm, "end": v(-179.24, 14.98) * mm});
            skLineSegment(sketch, "E3908", {"start": v(-179.24, 14.98) * mm, "end": v(-179.3, 15.1) * mm});
            skLineSegment(sketch, "E3909", {"start": v(-179.3, 15.1) * mm, "end": v(-179.37, 15.21) * mm});
            skLineSegment(sketch, "E3910", {"start": v(-179.37, 15.21) * mm, "end": v(-179.45, 15.33) * mm});
            skLineSegment(sketch, "E3911", {"start": v(-179.45, 15.33) * mm, "end": v(-179.53, 15.44) * mm});
            skLineSegment(sketch, "E3912", {"start": v(-179.53, 15.44) * mm, "end": v(-179.62, 15.55) * mm});
            skLineSegment(sketch, "E3913", {"start": v(-179.62, 15.55) * mm, "end": v(-179.72, 15.65) * mm});
            skLineSegment(sketch, "E3914", {"start": v(-179.72, 15.65) * mm, "end": v(-179.82, 15.75) * mm});
            skLineSegment(sketch, "E3915", {"start": v(-179.82, 15.75) * mm, "end": v(-179.93, 15.83) * mm});
            skLineSegment(sketch, "E3916", {"start": v(-179.93, 15.83) * mm, "end": v(-180.05, 15.9) * mm});
            skLineSegment(sketch, "E3917", {"start": v(-180.05, 15.9) * mm, "end": v(-180.18, 15.96) * mm});
            skLineSegment(sketch, "E3918", {"start": v(-180.18, 15.96) * mm, "end": v(-180.32, 16) * mm});
            skLineSegment(sketch, "E3919", {"start": v(-180.32, 16) * mm, "end": v(-180.47, 16.04) * mm});
            skLineSegment(sketch, "E3920", {"start": v(-180.47, 16.04) * mm, "end": v(-180.63, 16.05) * mm});
            skLineSegment(sketch, "E3921", {"start": v(-180.63, 16.05) * mm, "end": v(-180.67, 16.05) * mm});
            skLineSegment(sketch, "E3922", {"start": v(-180.67, 16.05) * mm, "end": v(-180.7, 16.04) * mm});
            skLineSegment(sketch, "E3923", {"start": v(-180.7, 16.04) * mm, "end": v(-180.73, 16.04) * mm});
            skLineSegment(sketch, "E3924", {"start": v(-180.73, 16.04) * mm, "end": v(-180.75, 16.04) * mm});
            skLineSegment(sketch, "E3925", {"start": v(-180.75, 16.04) * mm, "end": v(-180.76, 16.04) * mm});
            skLineSegment(sketch, "E3926", {"start": v(-180.76, 16.04) * mm, "end": v(-180.78, 16.04) * mm});
            skLineSegment(sketch, "E3927", {"start": v(-180.78, 16.04) * mm, "end": v(-180.83, 16.04) * mm});
            skLineSegment(sketch, "E3928", {"start": v(-180.83, 16.04) * mm, "end": v(-180.98, 16.03) * mm});
            skLineSegment(sketch, "E3929", {"start": v(-180.98, 16.03) * mm, "end": v(-181.12, 16) * mm});
            skLineSegment(sketch, "E3930", {"start": v(-181.12, 16) * mm, "end": v(-181.25, 15.96) * mm});
            skLineSegment(sketch, "E3931", {"start": v(-181.25, 15.96) * mm, "end": v(-181.37, 15.9) * mm});
            skLineSegment(sketch, "E3932", {"start": v(-181.37, 15.9) * mm, "end": v(-181.49, 15.83) * mm});
            skLineSegment(sketch, "E3933", {"start": v(-181.49, 15.83) * mm, "end": v(-181.59, 15.75) * mm});
            skLineSegment(sketch, "E3934", {"start": v(-181.59, 15.75) * mm, "end": v(-181.68, 15.66) * mm});
            skLineSegment(sketch, "E3935", {"start": v(-181.68, 15.66) * mm, "end": v(-181.77, 15.56) * mm});
            skLineSegment(sketch, "E3936", {"start": v(-181.77, 15.56) * mm, "end": v(-181.84, 15.45) * mm});
            skLineSegment(sketch, "E3937", {"start": v(-181.84, 15.45) * mm, "end": v(-181.9, 15.34) * mm});
            skLineSegment(sketch, "E3938", {"start": v(-181.9, 15.34) * mm, "end": v(-181.96, 15.23) * mm});
            skLineSegment(sketch, "E3939", {"start": v(-181.96, 15.23) * mm, "end": v(-182.01, 15.12) * mm});
            skLineSegment(sketch, "E3940", {"start": v(-182.01, 15.12) * mm, "end": v(-182.05, 15) * mm});
            skLineSegment(sketch, "E3941", {"start": v(-182.05, 15) * mm, "end": v(-182.08, 14.88) * mm});
            skLineSegment(sketch, "E3942", {"start": v(-182.08, 14.88) * mm, "end": v(-182.1, 14.77) * mm});
            skLineSegment(sketch, "E3943", {"start": v(-182.1, 14.77) * mm, "end": v(-182.1, 14.67) * mm});
            skLineSegment(sketch, "E3944", {"start": v(-182.1, 14.67) * mm, "end": v(-182.1, -22.83) * mm});
            skLineSegment(sketch, "E3945", {"start": v(-182.1, -22.83) * mm, "end": v(-182.1, -22.9) * mm});
            skLineSegment(sketch, "E3946", {"start": v(-182.1, -22.9) * mm, "end": v(-182.12, -22.96) * mm});
            skLineSegment(sketch, "E3947", {"start": v(-182.12, -22.96) * mm, "end": v(-182.13, -23.02) * mm});
            skLineSegment(sketch, "E3948", {"start": v(-182.13, -23.02) * mm, "end": v(-182.16, -23.08) * mm});
            skLineSegment(sketch, "E3949", {"start": v(-182.16, -23.08) * mm, "end": v(-182.18, -23.14) * mm});
            skLineSegment(sketch, "E3950", {"start": v(-182.18, -23.14) * mm, "end": v(-182.22, -23.2) * mm});
            skLineSegment(sketch, "E3951", {"start": v(-182.22, -23.2) * mm, "end": v(-182.26, -23.25) * mm});
            skLineSegment(sketch, "E3952", {"start": v(-182.26, -23.25) * mm, "end": v(-182.3, -23.3) * mm});
            skLineSegment(sketch, "E3953", {"start": v(-182.3, -23.3) * mm, "end": v(-182.34, -23.33) * mm});
            skLineSegment(sketch, "E3954", {"start": v(-182.34, -23.33) * mm, "end": v(-182.4, -23.37) * mm});
            skLineSegment(sketch, "E3955", {"start": v(-182.4, -23.37) * mm, "end": v(-182.45, -23.4) * mm});
            skLineSegment(sketch, "E3956", {"start": v(-182.45, -23.4) * mm, "end": v(-182.5, -23.43) * mm});
            skLineSegment(sketch, "E3957", {"start": v(-182.5, -23.43) * mm, "end": v(-182.57, -23.45) * mm});
            skLineSegment(sketch, "E3958", {"start": v(-182.57, -23.45) * mm, "end": v(-182.63, -23.47) * mm});
            skLineSegment(sketch, "E3959", {"start": v(-182.63, -23.47) * mm, "end": v(-182.7, -23.48) * mm});
            skLineSegment(sketch, "E3960", {"start": v(-182.7, -23.48) * mm, "end": v(-182.76, -23.48) * mm});
            skLineSegment(sketch, "E3961", {"start": v(-182.76, -23.48) * mm, "end": v(-184.5, -23.48) * mm});
            skLineSegment(sketch, "E3962", {"start": v(-184.5, -23.48) * mm, "end": v(-184.53, -23.52) * mm});
            skLineSegment(sketch, "E3963", {"start": v(-184.53, -23.52) * mm, "end": v(-192.86, -23.52) * mm});
            skLineSegment(sketch, "E3964", {"start": v(-192.86, -23.52) * mm, "end": v(-193.43, -23.5) * mm});
            skLineSegment(sketch, "E3965", {"start": v(-193.43, -23.5) * mm, "end": v(-193.99, -23.4) * mm});
            skLineSegment(sketch, "E3966", {"start": v(-193.99, -23.4) * mm, "end": v(-194.53, -23.27) * mm});
            skLineSegment(sketch, "E3967", {"start": v(-194.53, -23.27) * mm, "end": v(-195.05, -23.08) * mm});
            skLineSegment(sketch, "E3968", {"start": v(-195.05, -23.08) * mm, "end": v(-195.54, -22.84) * mm});
            skLineSegment(sketch, "E3969", {"start": v(-195.54, -22.84) * mm, "end": v(-196, -22.56) * mm});
            skLineSegment(sketch, "E3970", {"start": v(-196, -22.56) * mm, "end": v(-196.44, -22.23) * mm});
            skLineSegment(sketch, "E3971", {"start": v(-196.44, -22.23) * mm, "end": v(-196.84, -21.87) * mm});
            skLineSegment(sketch, "E3972", {"start": v(-196.84, -21.87) * mm, "end": v(-197.2, -21.47) * mm});
            skLineSegment(sketch, "E3973", {"start": v(-197.2, -21.47) * mm, "end": v(-197.53, -21.03) * mm});
            skLineSegment(sketch, "E3974", {"start": v(-197.53, -21.03) * mm, "end": v(-197.8, -20.57) * mm});
            skLineSegment(sketch, "E3975", {"start": v(-197.8, -20.57) * mm, "end": v(-198.05, -20.08) * mm});
            skLineSegment(sketch, "E3976", {"start": v(-198.05, -20.08) * mm, "end": v(-198.24, -19.56) * mm});
            skLineSegment(sketch, "E3977", {"start": v(-198.24, -19.56) * mm, "end": v(-198.37, -19.02) * mm});
            skLineSegment(sketch, "E3978", {"start": v(-198.37, -19.02) * mm, "end": v(-198.46, -18.46) * mm});
            skLineSegment(sketch, "E3979", {"start": v(-198.46, -18.46) * mm, "end": v(-198.49, -17.89) * mm});
            skLineSegment(sketch, "E3980", {"start": v(-198.49, -17.89) * mm, "end": v(-198.49, 17.82) * mm});
            skLineSegment(sketch, "E3981", {"start": v(-198.49, 17.82) * mm, "end": v(-198.46, 18.4) * mm});
            skLineSegment(sketch, "E3982", {"start": v(-198.46, 18.4) * mm, "end": v(-198.37, 18.96) * mm});
            skLineSegment(sketch, "E3983", {"start": v(-198.37, 18.96) * mm, "end": v(-198.24, 19.5) * mm});
            skLineSegment(sketch, "E3984", {"start": v(-198.24, 19.5) * mm, "end": v(-198.05, 20.02) * mm});
            skLineSegment(sketch, "E3985", {"start": v(-198.05, 20.02) * mm, "end": v(-197.8, 20.5) * mm});
            skLineSegment(sketch, "E3986", {"start": v(-197.8, 20.5) * mm, "end": v(-197.53, 20.97) * mm});
            skLineSegment(sketch, "E3987", {"start": v(-197.53, 20.97) * mm, "end": v(-197.2, 21.4) * mm});
            skLineSegment(sketch, "E3988", {"start": v(-197.2, 21.4) * mm, "end": v(-196.84, 21.8) * mm});
            skLineSegment(sketch, "E3989", {"start": v(-196.84, 21.8) * mm, "end": v(-196.44, 22.17) * mm});
            skLineSegment(sketch, "E3990", {"start": v(-196.44, 22.17) * mm, "end": v(-196, 22.5) * mm});
            skLineSegment(sketch, "E3991", {"start": v(-196, 22.5) * mm, "end": v(-195.54, 22.78) * mm});
            skLineSegment(sketch, "E3992", {"start": v(-195.54, 22.78) * mm, "end": v(-195.05, 23.01) * mm});
            skLineSegment(sketch, "E3993", {"start": v(-195.05, 23.01) * mm, "end": v(-194.53, 23.2) * mm});
            skLineSegment(sketch, "E3994", {"start": v(-194.53, 23.2) * mm, "end": v(-193.99, 23.34) * mm});
            skLineSegment(sketch, "E3995", {"start": v(-193.99, 23.34) * mm, "end": v(-193.43, 23.43) * mm});
            skLineSegment(sketch, "E3996", {"start": v(-193.43, 23.43) * mm, "end": v(-192.86, 23.46) * mm});
            skLineSegment(sketch, "E3997", {"start": v(-192.86, 23.46) * mm, "end": v(192.86, 23.46) * mm});
            skLineSegment(sketch, "E3998", {"start": v(192.86, 23.46) * mm, "end": v(193.43, 23.43) * mm});
            skLineSegment(sketch, "E3999", {"start": v(193.43, 23.43) * mm, "end": v(193.99, 23.34) * mm});
            skLineSegment(sketch, "E4000", {"start": v(193.99, 23.34) * mm, "end": v(194.53, 23.2) * mm});
            skLineSegment(sketch, "E4001", {"start": v(194.53, 23.2) * mm, "end": v(195.05, 23.01) * mm});
            skLineSegment(sketch, "E4002", {"start": v(195.05, 23.01) * mm, "end": v(195.54, 22.78) * mm});
            skLineSegment(sketch, "E4003", {"start": v(195.54, 22.78) * mm, "end": v(196, 22.5) * mm});
            skLineSegment(sketch, "E4004", {"start": v(196, 22.5) * mm, "end": v(196.44, 22.17) * mm});
            skLineSegment(sketch, "E4005", {"start": v(196.44, 22.17) * mm, "end": v(196.84, 21.8) * mm});
            skLineSegment(sketch, "E4006", {"start": v(196.84, 21.8) * mm, "end": v(197.2, 21.4) * mm});
            skLineSegment(sketch, "E4007", {"start": v(197.2, 21.4) * mm, "end": v(197.53, 20.97) * mm});
            skLineSegment(sketch, "E4008", {"start": v(197.53, 20.97) * mm, "end": v(197.8, 20.5) * mm});
            skLineSegment(sketch, "E4009", {"start": v(197.8, 20.5) * mm, "end": v(198.05, 20.02) * mm});
            skLineSegment(sketch, "E4010", {"start": v(198.05, 20.02) * mm, "end": v(198.24, 19.5) * mm});
            skLineSegment(sketch, "E4011", {"start": v(198.24, 19.5) * mm, "end": v(198.37, 18.96) * mm});
            skLineSegment(sketch, "E4012", {"start": v(198.37, 18.96) * mm, "end": v(198.46, 18.4) * mm});
            skLineSegment(sketch, "E4013", {"start": v(198.46, 18.4) * mm, "end": v(198.49, 17.82) * mm});
            skLineSegment(sketch, "E4014", {"start": v(198.49, 17.82) * mm, "end": v(198.49, -17.89) * mm});
            skSolve(sketch);
        }
        {
            var Q0;
            Q0=makeQuery(id+"F0.imprint","IMPRINT",FACE,{"disambiguationData":[TD([[makeQuery(id+"F0.imprint","IMPRINT",EDGE,{"derivedFrom":sQuery(id+"F0.wireOp",EDGE,"E0")}),1.0]])]});
            var Q1;
            Q1=makeQuery(id+"F0.imprint","IMPRINT",FACE,{"disambiguationData":[TD([[makeQuery(id+"F0.imprint","IMPRINT",EDGE,{"derivedFrom":sQuery(id+"F0.wireOp",EDGE,"E136")}),1.0]])]});
            extrude(context, id + "F1", {"entities" : qUnion([Q0, Q1]), "oppositeDirection" : true, "depth" : 2.5 * mm});
        }
        {
            var Q0;
            Q0=qCreatedBy(makeId("Top.planeOp"),FACE);
            var sketch = newSketch(context, id + "F2", { "sketchPlane" : qUnion([Q0])});
            skLineSegment(sketch, "E4015.top", {"start": v(0, 0) * mm, "end": v(800, 0) * mm});
            skLineSegment(sketch, "E4015.right", {"start": v(800, 200) * mm, "end": v(800, 0) * mm});
            skLineSegment(sketch, "E4016", {"start": v(0, 124.86) * mm, "end": v(0, -124.86) * mm, "construction": true});
            skLineSegment(sketch, "E4017", {"start": v(-355.85, 0) * mm, "end": v(355.85, 0) * mm, "construction": true});
            skLineSegment(sketch, "E4018.bottom", {"start": v(-156.51, 23.46) * mm, "end": v(-151.51, 23.46) * mm});
            skLineSegment(sketch, "E4018.top", {"start": v(-156.51, 36.51) * mm, "end": v(-151.51, 36.51) * mm});
            skLineSegment(sketch, "E4018.left", {"start": v(-156.51, 23.46) * mm, "end": v(-156.51, 36.51) * mm});
            skLineSegment(sketch, "E4018.right", {"start": v(-151.51, 23.46) * mm, "end": v(-151.51, 36.51) * mm});
            skLineSegment(sketch, "E4019.bottom", {"start": v(-121.51, -36.51) * mm, "end": v(-116.51, -36.51) * mm});
            skLineSegment(sketch, "E4019.top", {"start": v(-121.51, -23.48) * mm, "end": v(-116.51, -23.48) * mm});
            skLineSegment(sketch, "E4019.left", {"start": v(-121.51, -36.51) * mm, "end": v(-121.51, -23.48) * mm});
            skLineSegment(sketch, "E4019.right", {"start": v(-116.51, -36.51) * mm, "end": v(-116.51, -23.48) * mm});
            skLineSegment(sketch, "E4020.bottom", {"start": v(106.51, -36.51) * mm, "end": v(111.51, -36.51) * mm});
            skLineSegment(sketch, "E4020.top", {"start": v(106.51, -23.48) * mm, "end": v(111.51, -23.48) * mm});
            skLineSegment(sketch, "E4020.left", {"start": v(106.51, -36.51) * mm, "end": v(106.51, -23.48) * mm});
            skLineSegment(sketch, "E4020.right", {"start": v(111.51, -36.51) * mm, "end": v(111.51, -23.48) * mm});
            skLineSegment(sketch, "E4021.bottom", {"start": v(-2.51, 23.46) * mm, "end": v(2.49, 23.46) * mm});
            skLineSegment(sketch, "E4021.top", {"start": v(-2.51, 36.51) * mm, "end": v(2.49, 36.51) * mm});
            skLineSegment(sketch, "E4021.left", {"start": v(-2.51, 23.46) * mm, "end": v(-2.51, 36.51) * mm});
            skLineSegment(sketch, "E4021.right", {"start": v(2.49, 23.46) * mm, "end": v(2.49, 36.51) * mm});
            skLineSegment(sketch, "E4022.bottom", {"start": v(151.51, 23.46) * mm, "end": v(156.51, 23.46) * mm});
            skLineSegment(sketch, "E4022.top", {"start": v(151.51, 36.51) * mm, "end": v(156.51, 36.51) * mm});
            skLineSegment(sketch, "E4022.left", {"start": v(151.51, 23.46) * mm, "end": v(151.51, 36.51) * mm});
            skLineSegment(sketch, "E4022.right", {"start": v(156.51, 23.46) * mm, "end": v(156.51, 36.51) * mm});
            skLineSegment(sketch, "E4023.bottom", {"start": v(-216.51, -2.53) * mm, "end": v(-198.49, -2.53) * mm});
            skLineSegment(sketch, "E4023.top", {"start": v(-216.51, 2.47) * mm, "end": v(-198.49, 2.47) * mm});
            skLineSegment(sketch, "E4023.left", {"start": v(-216.51, -2.53) * mm, "end": v(-216.51, 2.47) * mm});
            skLineSegment(sketch, "E4023.right", {"start": v(-198.49, -2.53) * mm, "end": v(-198.49, 2.47) * mm});
            skLineSegment(sketch, "E4024.bottom", {"start": v(198.49, -2.53) * mm, "end": v(216.51, -2.53) * mm});
            skLineSegment(sketch, "E4024.top", {"start": v(198.49, 2.47) * mm, "end": v(216.51, 2.47) * mm});
            skLineSegment(sketch, "E4024.left", {"start": v(198.49, -2.53) * mm, "end": v(198.49, 2.47) * mm});
            skLineSegment(sketch, "E4024.right", {"start": v(216.51, -2.53) * mm, "end": v(216.51, 2.47) * mm});
            skSolve(sketch);
        }
        {
            var Q0;
            Q0=qSketchRegion(id+"F2",true);
            extrude(context, id + "F3", {"entities" : qUnion([Q0]), "depth" : 5 * mm, "offsetDistance" : 25 * mm});
        }
    });
